FCSTD DOCUMENT  (FreeCAD 0.16R6712 (Git))
Label: Core(XY)
License: CreativeCommons Attribution-ShareAlike
LicenseURL: http://creativecommons.org/licenses/by-sa/4.0/
objects: Part::FeaturePython×717, Part::Feature×181, App::DocumentObjectGroup×163, Part::Compound×24, Sketcher::SketchObject×10, Part::MultiFuse×5, Part::Sweep×5, Part::Cylinder×1, PartDesign::Pocket×1
note: 945 computed .brp shape members not serialized (recipe doc carries the construction recipe); baked Part::Feature solids carry a one-line shape summary decoded from their .brp

FEATURE [Part::FeaturePython] Wuerfelverbinder_20x20_import01010  label="Wuerfelverbinder_20x20_VUL"  # a2plus imported part (geometry in sourceFile) (typed FeaturePython)
  Placement = pos=(10,10,10) rot=(1,0,0;1.5708rad)
  fixedPosition = true
  sourceFile = <userpath>/CloudStation/Hobbyprojekte/3D Drucker/CoreXY/Assembly/Parts/Alu Extrusion/Wuerfelverbinder-20x20.FCStd
  timeLastImport = 1444069248
  updateColors = true
FEATURE [Part::FeaturePython] tslot20x20_import13  label="tslot20x20_import_VU"  # a2plus imported part (geometry in sourceFile) (typed FeaturePython)
  Placement = pos=(420,20,0) rot=(0,-1,0;1.5708rad)
  fixedPosition = true
  sourceFile = <userpath>/CloudStation/Hobbyprojekte/3D Drucker/CoreXY/Assembly/Parts/Alu Extrusion/tslot20x20x400.FCStd
  timeLastImport = 1444069248
  updateColors = true
FEATURE [Part::FeaturePython] tslot20x20x500_import04  label="tslot20x20x500_VL"  # a2plus imported part (geometry in sourceFile) (typed FeaturePython)
  Placement = pos=(4e-11,2.55588e-06,520) rot=(1,0,0;3.14159rad)
  fixedPosition = true
  sourceFile = <userpath>/CloudStation/Hobbyprojekte/3D Drucker/CoreXY/Assembly/Parts/Alu Extrusion/tslot20x20x500.FCStd
  timeLastImport = 1444069248
  updateColors = true
FEATURE [Part::FeaturePython] tslot20x20_import16  label="tslot20x20_UL"  # a2plus imported part (geometry in sourceFile) (typed FeaturePython)
  Placement = pos=(4e-11,420,20) rot=(1,0,0;1.5708rad)
  fixedPosition = true
  sourceFile = <userpath>/CloudStation/Hobbyprojekte/3D Drucker/CoreXY/Assembly/Parts/Alu Extrusion/tslot20x20x400.FCStd
  timeLastImport = 1444069248
  updateColors = true
FEATURE [Part::FeaturePython] Wuerfelverbinder_20x20_import01011  label="Wuerfelverbinder_20x20_HUL"  # a2plus imported part (geometry in sourceFile) (typed FeaturePython)
  Placement = pos=(10,430,10) rot=(1,0,0;3.14159rad)
  fixedPosition = true
  sourceFile = <userpath>/CloudStation/Hobbyprojekte/3D Drucker/CoreXY/Assembly/Parts/Alu Extrusion/Wuerfelverbinder-20x20.FCStd
  timeLastImport = 1444069248
  updateColors = true
FEATURE [Part::FeaturePython] tslot20x20x500_import01  # a2plus imported part (geometry in sourceFile) (typed FeaturePython)
  Placement = pos=(-1.6e-10,420,520) rot=(1,0,0;3.14159rad)
  fixedPosition = true
  sourceFile = <userpath>/CloudStation/Hobbyprojekte/3D Drucker/CoreXY/Assembly/Parts/Alu Extrusion/tslot20x20x500.FCStd
  timeLastImport = 1444069248
  updateColors = true
FEATURE [Part::FeaturePython] tslot20x20_import017  # a2plus imported part (geometry in sourceFile) (typed FeaturePython)
  Placement = pos=(420,440,0) rot=(0,-1,0;1.5708rad)
  fixedPosition = true
  sourceFile = <userpath>/CloudStation/Hobbyprojekte/3D Drucker/CoreXY/Assembly/Parts/Alu Extrusion/tslot20x20x400.FCStd
  timeLastImport = 1444069248
  updateColors = true
FEATURE [Part::FeaturePython] tslot20x20x500_import02  # a2plus imported part (geometry in sourceFile) (typed FeaturePython)
  Placement = pos=(420,420,520) rot=(1,0,0;3.14159rad)
  fixedPosition = true
  sourceFile = <userpath>/CloudStation/Hobbyprojekte/3D Drucker/CoreXY/Assembly/Parts/Alu Extrusion/tslot20x20x500.FCStd
  timeLastImport = 1444069248
  updateColors = true
FEATURE [Part::FeaturePython] tslot20x20_import14  label="tslot20x20 (RU)"  # a2plus imported part (geometry in sourceFile) (typed FeaturePython)
  Placement = pos=(420,420,20) rot=(1,0,0;1.5708rad)
  fixedPosition = true
  sourceFile = <userpath>/CloudStation/Hobbyprojekte/3D Drucker/CoreXY/Assembly/Parts/Alu Extrusion/tslot20x20x400.FCStd
  timeLastImport = 1444069248
  updateColors = true
FEATURE [Part::FeaturePython] tslot20x20x500_import03  # a2plus imported part (geometry in sourceFile) (typed FeaturePython)
  Placement = pos=(420,2.55538e-06,520) rot=(1,0,0;3.14159rad)
  fixedPosition = true
  sourceFile = <userpath>/CloudStation/Hobbyprojekte/3D Drucker/CoreXY/Assembly/Parts/Alu Extrusion/tslot20x20x500.FCStd
  timeLastImport = 1444069248
  updateColors = true
FEATURE [Part::FeaturePython] tslot20x20_import05  label="tslot20x20 (LO)"  # a2plus imported part (geometry in sourceFile) (typed FeaturePython)
  Placement = pos=(-1.6e-10,420,540) rot=(1,0,0;1.5708rad)
  fixedPosition = true
  sourceFile = <userpath>/CloudStation/Hobbyprojekte/3D Drucker/CoreXY/Assembly/Parts/Alu Extrusion/tslot20x20x400.FCStd
  timeLastImport = 1444069248
  updateColors = true
FEATURE [Part::FeaturePython] tslot20x20_import10  label="tslot20x20 (HO)"  # a2plus imported part (geometry in sourceFile) (typed FeaturePython)
  Placement = pos=(20,440,540) rot=(0,1,0;1.5708rad)
  fixedPosition = true
  sourceFile = <userpath>/CloudStation/Hobbyprojekte/3D Drucker/CoreXY/Assembly/Parts/Alu Extrusion/tslot20x20x400.FCStd
  timeLastImport = 1444069248
  updateColors = true
FEATURE [Part::FeaturePython] tslot20x20_import01  label="tslot20x20 (VO)"  # a2plus imported part (geometry in sourceFile) (typed FeaturePython)
  Placement = pos=(420,20,520) rot=(0,-1,0;1.5708rad)
  fixedPosition = true
  sourceFile = <userpath>/CloudStation/Hobbyprojekte/3D Drucker/CoreXY/Assembly/Parts/Alu Extrusion/tslot20x20x400.FCStd
  timeLastImport = 1444069248
  updateColors = true
FEATURE [Part::FeaturePython] tslot20x20_import06  label="tslot20x20 (RO)"  # a2plus imported part (geometry in sourceFile) (typed FeaturePython)
  Placement = pos=(420,420,540) rot=(1,0,0;1.5708rad)
  fixedPosition = true
  sourceFile = <userpath>/CloudStation/Hobbyprojekte/3D Drucker/CoreXY/Assembly/Parts/Alu Extrusion/tslot20x20x400.FCStd
  timeLastImport = 1444069248
  updateColors = true
FEATURE [Part::FeaturePython] Wuerfelverbinder_20x20_import01009  # a2plus imported part (geometry in sourceFile) (typed FeaturePython)
  Placement = pos=(430,10,10) rot=(0.57735,0.57735,0.57735;2.0944rad)
  fixedPosition = true
  sourceFile = <userpath>/CloudStation/Hobbyprojekte/3D Drucker/CoreXY/Assembly/Parts/Alu Extrusion/Wuerfelverbinder-20x20.FCStd
  timeLastImport = 1444069248
  updateColors = true
FEATURE [Part::FeaturePython] Wuerfelverbinder_20x20_import01008  # a2plus imported part (geometry in sourceFile) (typed FeaturePython)
  Placement = pos=(430,430,10) rot=(0.707107,-0.707107,0;3.14159rad)
  fixedPosition = true
  sourceFile = <userpath>/CloudStation/Hobbyprojekte/3D Drucker/CoreXY/Assembly/Parts/Alu Extrusion/Wuerfelverbinder-20x20.FCStd
  timeLastImport = 1444069248
  updateColors = true
FEATURE [Part::FeaturePython] Wuerfelverbinder_20x20_import01  label="Wuerfelverbinder_20x20 (VLO)"  # a2plus imported part (geometry in sourceFile) (typed FeaturePython)
  Placement = pos=(10,10,530) rot=(0,0,1;0rad)
  fixedPosition = true
  sourceFile = <userpath>/CloudStation/Hobbyprojekte/3D Drucker/CoreXY/Assembly/Parts/Alu Extrusion/Wuerfelverbinder-20x20.FCStd
  timeLastImport = 1444069248
  updateColors = true
FEATURE [Part::FeaturePython] Wuerfelverbinder_20x20_import01004  label="Wuerfelverbinder_20x20 (HIL)"  # a2plus imported part (geometry in sourceFile) (typed FeaturePython)
  Placement = pos=(10,430,530) rot=(0,0,-1;1.5708rad)
  fixedPosition = true
  sourceFile = <userpath>/CloudStation/Hobbyprojekte/3D Drucker/CoreXY/Assembly/Parts/Alu Extrusion/Wuerfelverbinder-20x20.FCStd
  timeLastImport = 1444069248
  updateColors = true
FEATURE [Part::FeaturePython] Wuerfelverbinder_20x20_import01005  label="Wuerfelverbinder_20x20 (HOR)"  # a2plus imported part (geometry in sourceFile) (typed FeaturePython)
  Placement = pos=(430,430,530) rot=(0,0,1;3.14159rad)
  fixedPosition = true
  sourceFile = <userpath>/CloudStation/Hobbyprojekte/3D Drucker/CoreXY/Assembly/Parts/Alu Extrusion/Wuerfelverbinder-20x20.FCStd
  timeLastImport = 1444069248
  updateColors = true
FEATURE [Part::FeaturePython] Wuerfelverbinder_20x20_import01001  label="Wuerfelverbinder_20x20 (VRO)"  # a2plus imported part (geometry in sourceFile) (typed FeaturePython)
  Placement = pos=(430,10,530) rot=(0,0,1;1.5708rad)
  fixedPosition = true
  sourceFile = <userpath>/CloudStation/Hobbyprojekte/3D Drucker/CoreXY/Assembly/Parts/Alu Extrusion/Wuerfelverbinder-20x20.FCStd
  timeLastImport = 1444069248
  updateColors = true
FEATURE [App::DocumentObjectGroup] Gruppe002  label="Würfelverbinder"
  Group = -> [Wuerfelverbinder_20x20_import01010,Wuerfelverbinder_20x20_import01011,Wuerfelverbinder_20x20_import01009,Wuerfelverbinder_20x20_import01008,Wuerfelverbinder_20x20_import01,Wuerfelverbinder_20x20_import01004,Wuerfelverbinder_20x20_import01005,Wuerfelverbinder_20x20_import01001]
FEATURE [Part::FeaturePython] tslot20x20_import018  # a2plus imported part (geometry in sourceFile) (typed FeaturePython)
  Placement = pos=(420,440,100) rot=(0,-1,0;1.5708rad)
  fixedPosition = true
  sourceFile = <userpath>/CloudStation/Hobbyprojekte/3D Drucker/CoreXY/Assembly/Parts/Alu Extrusion/tslot20x20x400.FCStd
  timeLastImport = 1444069248
  updateColors = true
FEATURE [Part::FeaturePython] tslot20x20_import019  label="tslot20x20_UL001"  # a2plus imported part (geometry in sourceFile) (typed FeaturePython)
  Placement = pos=(4e-11,420,120) rot=(1,0,0;1.5708rad)
  fixedPosition = true
  sourceFile = <userpath>/CloudStation/Hobbyprojekte/3D Drucker/CoreXY/Assembly/Parts/Alu Extrusion/tslot20x20x400.FCStd
  timeLastImport = 1444069248
  updateColors = true
FEATURE [Part::FeaturePython] tslot20x20_import020  label="tslot20x20_import_VU001"  # a2plus imported part (geometry in sourceFile) (typed FeaturePython)
  Placement = pos=(420,20,100) rot=(0,-1,0;1.5708rad)
  fixedPosition = true
  sourceFile = <userpath>/CloudStation/Hobbyprojekte/3D Drucker/CoreXY/Assembly/Parts/Alu Extrusion/tslot20x20x400.FCStd
  timeLastImport = 1444069248
  updateColors = true
FEATURE [Part::FeaturePython] tslot20x20_import021  label="tslot20x20 (RU)001"  # a2plus imported part (geometry in sourceFile) (typed FeaturePython)
  Placement = pos=(420,420,120) rot=(1,0,0;1.5708rad)
  fixedPosition = true
  sourceFile = <userpath>/CloudStation/Hobbyprojekte/3D Drucker/CoreXY/Assembly/Parts/Alu Extrusion/tslot20x20x400.FCStd
  timeLastImport = 1444069248
  updateColors = true
FEATURE [App::DocumentObjectGroup] Gruppe003  label="Zwischenboden"
  Group = -> [tslot20x20_import018,tslot20x20_import019,tslot20x20_import020,tslot20x20_import021]
FEATURE [Part::FeaturePython] Angle_Bracket_import02  label="Angle_Bracket_VLU_01"  # a2plus imported part (geometry in sourceFile) (typed FeaturePython)
  Placement = pos=(71.9933,2.55588e-06,100) rot=(-1,0,0;1.5708rad)
  fixedPosition = true
  sourceFile = <userpath>/CloudStation/Hobbyprojekte/3D Drucker/CoreXY/Assembly/Parts/Printed Parts/Angle_Bracket.FCStd
  timeLastImport = 1444069248
  updateColors = true
FEATURE [Part::FeaturePython] Angle_Bracket_import14  label="Angle_Bracket_VHU_01"  # a2plus imported part (geometry in sourceFile) (typed FeaturePython)
  Placement = pos=(-1.6e-10,368.007,100) rot=(0.57735,-0.57735,0.57735;4.18879rad)
  fixedPosition = true
  sourceFile = <userpath>/CloudStation/Hobbyprojekte/3D Drucker/CoreXY/Assembly/Parts/Printed Parts/Angle_Bracket.FCStd
  timeLastImport = 1444069248
  updateColors = true
FEATURE [Part::FeaturePython] Angle_Bracket_import04  label="Angle_Bracket_VRU_01"  # a2plus imported part (geometry in sourceFile) (typed FeaturePython)
  Placement = pos=(368.007,20,100) rot=(0,0.707107,-0.707107;3.14159rad)
  fixedPosition = true
  sourceFile = <userpath>/CloudStation/Hobbyprojekte/3D Drucker/CoreXY/Assembly/Parts/Printed Parts/Angle_Bracket.FCStd
  timeLastImport = 1444069248
  updateColors = true
FEATURE [Part::FeaturePython] Angle_Bracket_import10  label="Angle_Bracket_VHU_02"  # a2plus imported part (geometry in sourceFile) (typed FeaturePython)
  Placement = pos=(71.9933,420,100) rot=(-1,0,0;1.5708rad)
  fixedPosition = true
  sourceFile = <userpath>/CloudStation/Hobbyprojekte/3D Drucker/CoreXY/Assembly/Parts/Printed Parts/Angle_Bracket.FCStd
  timeLastImport = 1444069248
  updateColors = true
FEATURE [Part::FeaturePython] Angle_Bracket_import12  label="Angle_Bracket_HRU_01"  # a2plus imported part (geometry in sourceFile) (typed FeaturePython)
  Placement = pos=(420,420,48.0067) rot=(-0.57735,0.57735,0.57735;2.0944rad)
  fixedPosition = true
  sourceFile = <userpath>/CloudStation/Hobbyprojekte/3D Drucker/CoreXY/Assembly/Parts/Printed Parts/Angle_Bracket.FCStd
  timeLastImport = 1444069248
  updateColors = true
FEATURE [Part::FeaturePython] Angle_Bracket_import06  label="Angle_Bracket_VRU_02"  # a2plus imported part (geometry in sourceFile) (typed FeaturePython)
  Placement = pos=(440,71.9933,100) rot=(0.57735,0.57735,-0.57735;4.18879rad)
  fixedPosition = true
  sourceFile = <userpath>/CloudStation/Hobbyprojekte/3D Drucker/CoreXY/Assembly/Parts/Printed Parts/Angle_Bracket.FCStd
  timeLastImport = 1444069248
  updateColors = true
FEATURE [Part::FeaturePython] Angle_Bracket_import08  label="Angle_Bracket_HRU_02"  # a2plus imported part (geometry in sourceFile) (typed FeaturePython)
  Placement = pos=(420,368.007,100) rot=(0.57735,-0.57735,0.57735;4.18879rad)
  fixedPosition = true
  sourceFile = <userpath>/CloudStation/Hobbyprojekte/3D Drucker/CoreXY/Assembly/Parts/Printed Parts/Angle_Bracket.FCStd
  timeLastImport = 1444069248
  updateColors = true
FEATURE [Part::FeaturePython] Angle_Bracket_import16  label="Angle_Bracket_VLU_02"  # a2plus imported part (geometry in sourceFile) (typed FeaturePython)
  Placement = pos=(20,71.9933,100) rot=(0.57735,0.57735,-0.57735;4.18879rad)
  fixedPosition = true
  sourceFile = <userpath>/CloudStation/Hobbyprojekte/3D Drucker/CoreXY/Assembly/Parts/Printed Parts/Angle_Bracket.FCStd
  timeLastImport = 1444069248
  updateColors = true
FEATURE [Part::FeaturePython] Angle_Bracket_import11  label="Angle_Bracket_HRO_01"  # a2plus imported part (geometry in sourceFile) (typed FeaturePython)
  Placement = pos=(368.007,420,120) rot=(0,0.707107,0.707107;3.14159rad)
  fixedPosition = true
  sourceFile = <userpath>/CloudStation/Hobbyprojekte/3D Drucker/CoreXY/Assembly/Parts/Printed Parts/Angle_Bracket.FCStd
  timeLastImport = 1444069248
  updateColors = true
FEATURE [Part::FeaturePython] Angle_Bracket_import01  label="Angle_Bracket_VLO_01"  # a2plus imported part (geometry in sourceFile) (typed FeaturePython)
  Placement = pos=(71.9933,20,120) rot=(1,0,0;1.5708rad)
  fixedPosition = true
  sourceFile = <userpath>/CloudStation/Hobbyprojekte/3D Drucker/CoreXY/Assembly/Parts/Printed Parts/Angle_Bracket.FCStd
  timeLastImport = 1444069248
  updateColors = true
FEATURE [Part::FeaturePython] Angle_Bracket_import13  label="Angle_Bracket_HLO_01"  # a2plus imported part (geometry in sourceFile) (typed FeaturePython)
  Placement = pos=(20,368.007,120) rot=(0.57735,-0.57735,-0.57735;2.0944rad)
  fixedPosition = true
  sourceFile = <userpath>/CloudStation/Hobbyprojekte/3D Drucker/CoreXY/Assembly/Parts/Printed Parts/Angle_Bracket.FCStd
  timeLastImport = 1444069248
  updateColors = true
FEATURE [Part::FeaturePython] Angle_Bracket_import15  label="Angle_Bracket_VLO_02"  # a2plus imported part (geometry in sourceFile) (typed FeaturePython)
  Placement = pos=(4.1e-11,71.9933,120) rot=(0.57735,0.57735,0.57735;2.0944rad)
  fixedPosition = true
  sourceFile = <userpath>/CloudStation/Hobbyprojekte/3D Drucker/CoreXY/Assembly/Parts/Printed Parts/Angle_Bracket.FCStd
  timeLastImport = 1444069248
  updateColors = true
FEATURE [Part::FeaturePython] Angle_Bracket_import03  label="Angle_Bracket_VRO_01"  # a2plus imported part (geometry in sourceFile) (typed FeaturePython)
  Placement = pos=(368.007,2.55538e-06,120) rot=(0,0.707107,0.707107;3.14159rad)
  fixedPosition = true
  sourceFile = <userpath>/CloudStation/Hobbyprojekte/3D Drucker/CoreXY/Assembly/Parts/Printed Parts/Angle_Bracket.FCStd
  timeLastImport = 1444069248
  updateColors = true
FEATURE [Part::FeaturePython] Angle_Bracket_import09  label="Angle_Bracket_HLO_02"  # a2plus imported part (geometry in sourceFile) (typed FeaturePython)
  Placement = pos=(71.9933,440,120) rot=(1,0,0;1.5708rad)
  fixedPosition = true
  sourceFile = <userpath>/CloudStation/Hobbyprojekte/3D Drucker/CoreXY/Assembly/Parts/Printed Parts/Angle_Bracket.FCStd
  timeLastImport = 1444069248
  updateColors = true
FEATURE [Part::FeaturePython] Angle_Bracket_import05  label="Angle_Bracket_VRO_02"  # a2plus imported part (geometry in sourceFile) (typed FeaturePython)
  Placement = pos=(420,71.9933,120) rot=(0.57735,0.57735,0.57735;2.0944rad)
  fixedPosition = true
  sourceFile = <userpath>/CloudStation/Hobbyprojekte/3D Drucker/CoreXY/Assembly/Parts/Printed Parts/Angle_Bracket.FCStd
  timeLastImport = 1444069248
  updateColors = true
FEATURE [Part::FeaturePython] Angle_Bracket_import07  label="Angle_Bracket_HRO_02"  # a2plus imported part (geometry in sourceFile) (typed FeaturePython)
  Placement = pos=(440,368.007,120) rot=(0.57735,-0.57735,-0.57735;2.0944rad)
  fixedPosition = true
  sourceFile = <userpath>/CloudStation/Hobbyprojekte/3D Drucker/CoreXY/Assembly/Parts/Printed Parts/Angle_Bracket.FCStd
  timeLastImport = 1444069248
  updateColors = true
FEATURE [App::DocumentObjectGroup] Gruppe007  label="Zusätzliche Eckverbinder"
  Group = -> [Angle_Bracket_import01,Angle_Bracket_import15,Angle_Bracket_import03,Angle_Bracket_import05,Angle_Bracket_import13,Angle_Bracket_import07,Angle_Bracket_import11,Angle_Bracket_import09]
FEATURE [Part::FeaturePython] NEMA_17_Stepper_Motor_40mm_with_connector_import01  # a2plus imported part (geometry in sourceFile) (typed FeaturePython)
  Placement = pos=(356,399,524.6) rot=(1,0,0;3.14159rad)
  fixedPosition = true
  sourceFile = <userpath>/CloudStation/Hobbyprojekte/3D Drucker/CoreXY/Assembly/Parts/3D Printer Components/NEMA-17_Stepper_Motor_40mm_with_connector.fcstd
  timeLastImport = 1444068474
  updateColors = true
FEATURE [Part::FeaturePython] DIN625_1_624_ZZ_import01003  # a2plus imported part (geometry in sourceFile) (typed FeaturePython)
  Placement = pos=(383.5,417.7,478) rot=(0,1,0;3.14159rad)
  fixedPosition = false
  sourceFile = <userpath>/CloudStation/Hobbyprojekte/3D Drucker/CoreXY/Assembly/Parts/Bearings/DIN625-1_624-ZZ.FCStd
  timeLastImport = 1430517302
  updateColors = true
FEATURE [Part::FeaturePython] DIN625_1_624_ZZ_import01004  # a2plus imported part (geometry in sourceFile) (typed FeaturePython)
  Placement = pos=(383.5,417.7,473) rot=(0,1,0;3.14159rad)
  fixedPosition = false
  sourceFile = <userpath>/CloudStation/Hobbyprojekte/3D Drucker/CoreXY/Assembly/Parts/Bearings/DIN625-1_624-ZZ.FCStd
  timeLastImport = 1430517302
  updateColors = true
FEATURE [Part::FeaturePython] DIN7965___Schraubeinsatz___M3_import01  # a2plus imported part (geometry in sourceFile) (typed FeaturePython)
  Placement = pos=(385,383,478.2) rot=(0,1,0;3.14159rad)
  fixedPosition = false
  sourceFile = <userpath>/CloudStation/Hobbyprojekte/3D Drucker/CoreXY/Assembly/Parts/Screws/DIN7965 - Schraubeinsatz - M3.FCStd
  timeLastImport = 1430763186
  updateColors = true
FEATURE [Part::FeaturePython] Hammermutter_B_Typ_Nut6_M4_import01003  # a2plus imported part (geometry in sourceFile) (typed FeaturePython)
  Placement = pos=(430,408,445.3) rot=(0,0,1;3.14159rad)
  fixedPosition = false
  sourceFile = <userpath>/CloudStation/Hobbyprojekte/3D Drucker/CoreXY/Assembly/Parts/Screws/Hammermutter B-Typ Nut6 M4.FCStd
  timeLastImport = 1430523528
  updateColors = true
FEATURE [Part::FeaturePython] Hammermutter_B_Typ_Nut6_M4_import01002  # a2plus imported part (geometry in sourceFile) (typed FeaturePython)
  Placement = pos=(430,393,445.3) rot=(0,0,1;3.14159rad)
  fixedPosition = false
  sourceFile = <userpath>/CloudStation/Hobbyprojekte/3D Drucker/CoreXY/Assembly/Parts/Screws/Hammermutter B-Typ Nut6 M4.FCStd
  timeLastImport = 1430523528
  updateColors = true
FEATURE [Part::FeaturePython] Hammermutter_B_Typ_Nut6_M4_import01  # a2plus imported part (geometry in sourceFile) (typed FeaturePython)
  Placement = pos=(398,430,445.3) rot=(0,0,-1;1.5708rad)
  fixedPosition = false
  sourceFile = <userpath>/CloudStation/Hobbyprojekte/3D Drucker/CoreXY/Assembly/Parts/Screws/Hammermutter B-Typ Nut6 M4.FCStd
  timeLastImport = 1430523528
  updateColors = true
FEATURE [Part::FeaturePython] Hammermutter_B_Typ_Nut6_M4_import01001  # a2plus imported part (geometry in sourceFile) (typed FeaturePython)
  Placement = pos=(346,430,445.3) rot=(0,0,-1;1.5708rad)
  fixedPosition = false
  sourceFile = <userpath>/CloudStation/Hobbyprojekte/3D Drucker/CoreXY/Assembly/Parts/Screws/Hammermutter B-Typ Nut6 M4.FCStd
  timeLastImport = 1430523528
  updateColors = true
FEATURE [Part::FeaturePython] spacer16mm_import01  # a2plus imported part (geometry in sourceFile) (typed FeaturePython)
  Placement = pos=(407,413,452.5) rot=(0,0,1;3.14159rad)
  fixedPosition = false
  sourceFile = <userpath>/CloudStation/Hobbyprojekte/3D Drucker/CoreXY/Assembly/Parts/Printed Parts/spacer16mm.FCStd
  timeLastImport = 1444069248
  updateColors = true
FEATURE [Part::FeaturePython] spacer16mm_import03  # a2plus imported part (geometry in sourceFile) (typed FeaturePython)
  Placement = pos=(402,388,452.5) rot=(0,0,1;3.14159rad)
  fixedPosition = false
  sourceFile = <userpath>/CloudStation/Hobbyprojekte/3D Drucker/CoreXY/Assembly/Parts/Printed Parts/spacer16mm.FCStd
  timeLastImport = 1444069248
  updateColors = true
FEATURE [Part::FeaturePython] NEMA_17_Stepper_Motor_40mm_with_connector_import002  # a2plus imported part (geometry in sourceFile) (typed FeaturePython)
  Placement = pos=(84,399,524.6) rot=(0,1,0;3.14159rad)
  fixedPosition = true
  sourceFile = <userpath>/CloudStation/Hobbyprojekte/3D Drucker/CoreXY/Assembly/Parts/3D Printer Components/NEMA-17_Stepper_Motor_40mm_with_connector.fcstd
  timeLastImport = 1444068474
  updateColors = true
FEATURE [Part::FeaturePython] Hammermutter_B_Typ_Nut6_M4_import01004  # a2plus imported part (geometry in sourceFile) (typed FeaturePython)
  Placement = pos=(10,408,445.3) rot=(0,0,1;3.14159rad)
  fixedPosition = false
  sourceFile = <userpath>/CloudStation/Hobbyprojekte/3D Drucker/CoreXY/Assembly/Parts/Screws/Hammermutter B-Typ Nut6 M4.FCStd
  timeLastImport = 1430523528
  updateColors = true
FEATURE [Part::FeaturePython] Hammermutter_B_Typ_Nut6_M4_import01005  # a2plus imported part (geometry in sourceFile) (typed FeaturePython)
  Placement = pos=(42,430,445.3) rot=(0,0,-1;1.5708rad)
  fixedPosition = false
  sourceFile = <userpath>/CloudStation/Hobbyprojekte/3D Drucker/CoreXY/Assembly/Parts/Screws/Hammermutter B-Typ Nut6 M4.FCStd
  timeLastImport = 1430523528
  updateColors = true
FEATURE [Part::FeaturePython] Hammermutter_B_Typ_Nut6_M4_import01006  # a2plus imported part (geometry in sourceFile) (typed FeaturePython)
  Placement = pos=(10,393,445.3) rot=(0,0,1;3.14159rad)
  fixedPosition = false
  sourceFile = <userpath>/CloudStation/Hobbyprojekte/3D Drucker/CoreXY/Assembly/Parts/Screws/Hammermutter B-Typ Nut6 M4.FCStd
  timeLastImport = 1430523528
  updateColors = true
FEATURE [Part::FeaturePython] Hammermutter_B_Typ_Nut6_M4_import01007  # a2plus imported part (geometry in sourceFile) (typed FeaturePython)
  Placement = pos=(94,430,445.3) rot=(0,0,-1;1.5708rad)
  fixedPosition = false
  sourceFile = <userpath>/CloudStation/Hobbyprojekte/3D Drucker/CoreXY/Assembly/Parts/Screws/Hammermutter B-Typ Nut6 M4.FCStd
  timeLastImport = 1430523528
  updateColors = true
FEATURE [Part::FeaturePython] Hammermutter_B_Typ_Nut6_M4_import01009  # a2plus imported part (geometry in sourceFile) (typed FeaturePython)
  Placement = pos=(430,15,478.5) rot=(0,0.707107,0.707107;3.14159rad)
  fixedPosition = false
  sourceFile = <userpath>/CloudStation/Hobbyprojekte/3D Drucker/CoreXY/Assembly/Parts/Screws/Hammermutter B-Typ Nut6 M4.FCStd
  timeLastImport = 1430523528
  updateColors = true
FEATURE [Part::FeaturePython] Hammermutter_B_Typ_Nut6_M4_import01011  # a2plus imported part (geometry in sourceFile) (typed FeaturePython)
  Placement = pos=(430,15,455.5) rot=(0,0.707107,0.707107;3.14159rad)
  fixedPosition = false
  sourceFile = <userpath>/CloudStation/Hobbyprojekte/3D Drucker/CoreXY/Assembly/Parts/Screws/Hammermutter B-Typ Nut6 M4.FCStd
  timeLastImport = 1430523528
  updateColors = true
FEATURE [Part::FeaturePython] Hammermutter_B_Typ_Nut6_M4_import01012  # a2plus imported part (geometry in sourceFile) (typed FeaturePython)
  Placement = pos=(48,10,445.3) rot=(0,0,-1;1.5708rad)
  fixedPosition = false
  sourceFile = <userpath>/CloudStation/Hobbyprojekte/3D Drucker/CoreXY/Assembly/Parts/Screws/Hammermutter B-Typ Nut6 M4.FCStd
  timeLastImport = 1430523528
  updateColors = true
FEATURE [Part::FeaturePython] DIN7965___Schraubeinsatz___M3_import004  # a2plus imported part (geometry in sourceFile) (typed FeaturePython)
  Placement = pos=(55,35,469.5) rot=(0,1,0;3.14159rad)
  fixedPosition = false
  sourceFile = <userpath>/CloudStation/Hobbyprojekte/3D Drucker/CoreXY/Assembly/Parts/Screws/DIN7965 - Schraubeinsatz - M3.FCStd
  timeLastImport = 1430763186
  updateColors = true
FEATURE [Part::FeaturePython] Hammermutter_B_Typ_Nut6_M4_import01013  # a2plus imported part (geometry in sourceFile) (typed FeaturePython)
  Placement = pos=(10,15,478.5) rot=(0,0.707107,0.707107;3.14159rad)
  fixedPosition = false
  sourceFile = <userpath>/CloudStation/Hobbyprojekte/3D Drucker/CoreXY/Assembly/Parts/Screws/Hammermutter B-Typ Nut6 M4.FCStd
  timeLastImport = 1430523528
  updateColors = true
FEATURE [Part::FeaturePython] Hammermutter_B_Typ_Nut6_M4_import01014  # a2plus imported part (geometry in sourceFile) (typed FeaturePython)
  Placement = pos=(33,10,445.3) rot=(0,0,-1;1.5708rad)
  fixedPosition = false
  sourceFile = <userpath>/CloudStation/Hobbyprojekte/3D Drucker/CoreXY/Assembly/Parts/Screws/Hammermutter B-Typ Nut6 M4.FCStd
  timeLastImport = 1430523528
  updateColors = true
FEATURE [Part::FeaturePython] Hammermutter_B_Typ_Nut6_M4_import01015  # a2plus imported part (geometry in sourceFile) (typed FeaturePython)
  Placement = pos=(10,15,455.5) rot=(0,0.707107,0.707107;3.14159rad)
  fixedPosition = false
  sourceFile = <userpath>/CloudStation/Hobbyprojekte/3D Drucker/CoreXY/Assembly/Parts/Screws/Hammermutter B-Typ Nut6 M4.FCStd
  timeLastImport = 1430523528
  updateColors = true
FEATURE [Part::FeaturePython] spacer9mm_import006  # a2plus imported part (geometry in sourceFile) (typed FeaturePython)
  Placement = pos=(33,10,478.8) rot=(0,1,0;3.14159rad)
  fixedPosition = false
  sourceFile = <userpath>/CloudStation/Hobbyprojekte/3D Drucker/CoreXY/Assembly/Parts/Printed Parts/spacer9mm.FCStd
  timeLastImport = 1444069248
  updateColors = true
FEATURE [Part::FeaturePython] spacer9mm_import007  # a2plus imported part (geometry in sourceFile) (typed FeaturePython)
  Placement = pos=(38,28,468.9) rot=(0,1,0;3.14159rad)
  fixedPosition = false
  sourceFile = <userpath>/CloudStation/Hobbyprojekte/3D Drucker/CoreXY/Assembly/Parts/Printed Parts/spacer9mm.FCStd
  timeLastImport = 1444069248
  updateColors = true
FEATURE [App::DocumentObjectGroup] Gruppe027  label="Distancers003"
  Group = -> [spacer9mm_import007,spacer9mm_import006]
FEATURE [App::DocumentObjectGroup] Gruppe033  label="Distancers004"
FEATURE [App::DocumentObjectGroup] Gruppe038  label="Distancers005"
FEATURE [Part::FeaturePython] LM8uu_005  # a2plus imported part (geometry in sourceFile) (typed FeaturePython)
  Placement = pos=(206.657,188.8,470.2) rot=(0,0,1;1.5708rad)
  fixedPosition = false
  sourceFile = <userpath>/CloudStation/Hobbyprojekte/3D Drucker/CoreXY/Assembly/Parts/Bearings/LM8uu.fcstd
  timeLastImport = 1430143348
  updateColors = true
FEATURE [Part::FeaturePython] LM8uu_006  # a2plus imported part (geometry in sourceFile) (typed FeaturePython)
  Placement = pos=(206.657,228.8,470.2) rot=(0,0,1;1.5708rad)
  fixedPosition = false
  sourceFile = <userpath>/CloudStation/Hobbyprojekte/3D Drucker/CoreXY/Assembly/Parts/Bearings/LM8uu.fcstd
  timeLastImport = 1430143348
  updateColors = true
FEATURE [Part::FeaturePython] LM8uu_007  # a2plus imported part (geometry in sourceFile) (typed FeaturePython)
  Placement = pos=(233.657,228.8,470.2) rot=(0,0,1;1.5708rad)
  fixedPosition = false
  sourceFile = <userpath>/CloudStation/Hobbyprojekte/3D Drucker/CoreXY/Assembly/Parts/Bearings/LM8uu.fcstd
  timeLastImport = 1430143348
  updateColors = true
FEATURE [Part::FeaturePython] LM8uu_008  # a2plus imported part (geometry in sourceFile) (typed FeaturePython)
  Placement = pos=(233.657,188.8,470.2) rot=(0,0,1;1.5708rad)
  fixedPosition = true
  sourceFile = <userpath>/CloudStation/Hobbyprojekte/3D Drucker/CoreXY/Assembly/Parts/Bearings/LM8uu.fcstd
  timeLastImport = 1430143348
  updateColors = true
FEATURE [App::DocumentObjectGroup] Gruppe041  label="Bearings006"
  Group = -> [LM8uu_005,LM8uu_006,LM8uu_007,LM8uu_008]
FEATURE [App::DocumentObjectGroup] Gruppe042  label="Screws006"
FEATURE [Part::FeaturePython] GT2Pulley_01  # a2plus imported part (geometry in sourceFile) (typed FeaturePython)
  Placement = pos=(356,399,463.95) rot=(0,0,1;3.14159rad)
  fixedPosition = true
  sourceFile = <userpath>/CloudStation/Hobbyprojekte/3D Drucker/CoreXY/Assembly/Parts/Belts/GT2Pulley.fcstd
  timeLastImport = 1444675797
  updateColors = true
FEATURE [Part::FeaturePython] GT2Pulley_002  # a2plus imported part (geometry in sourceFile) (typed FeaturePython)
  Placement = pos=(84,399,474.2) rot=(1,0,0;3.14159rad)
  fixedPosition = true
  sourceFile = <userpath>/CloudStation/Hobbyprojekte/3D Drucker/CoreXY/Assembly/Parts/Belts/GT2Pulley.fcstd
  timeLastImport = 1444675797
  updateColors = true
FEATURE [Part::Feature] Part__Feature124  label="belt-clamp"
  Placement = pos=(202.907,208.742,301.2) rot=(0,0,1;0rad)
  shape: bbox 15 x 22 x 10 mm, 58 faces (baked)
FEATURE [Part::Feature] Part__Feature125  label="belt-clamp001"
  Placement = pos=(202.907,208.742,300.2) rot=(0,0,1;0rad)
  shape: bbox 15 x 22 x 10 mm, 58 faces (baked)
FEATURE [Part::Feature] Part__Feature348  label="C04H030010-Fibonacci-Support"
  Placement = pos=(216.254,203.086,536.966) rot=(0,0.707107,0.707107;3.14159rad)
  shape: bbox 41.5 x 15 x 48 mm, 19 faces (baked)
FEATURE [Part::Feature] Cut  label="carriage-up"
  Placement = pos=(219.907,209.1,476) rot=(0,0,1;3.14159rad)
  shape: bbox 70 x 90 x 3 mm, 67 faces (baked)
FEATURE [Part::Feature] Part__Feature349  label="C04H020001-Extruder-heat-sink"
  Placement = pos=(210.254,193.086,499.001) rot=(0.57735,0.57735,-0.57735;4.18879rad)
  shape: bbox 40.01 x 11.01 x 40.01 mm, 661 faces (baked)
FEATURE [Part::Feature] Part__Feature350  label="C04H030096-extruder-motor-support"
  Placement = pos=(210.254,213.086,478.001) rot=(1,0,0;1.5708rad)
  shape: bbox 45.02 x 20.02 x 47.52 mm, 42 faces (baked)
FEATURE [Part::Feature] Part__Feature354  label="Extruder_tube-end"
  Placement = pos=(216.254,203.086,541.576) rot=(0,0.707107,0.707107;3.14159rad)
  shape: bbox 54.22 x 4 x 43.22 mm, 8 faces (baked)
FEATURE [Part::Feature] Part__Feature353  label="C04H020019-extruder-spring"
  Placement = pos=(195.504,203.086,500.141) rot=(1,0,0;1.5708rad)
  shape: bbox 4 x 4.003 x 16.76 mm, 15 faces (baked)
FEATURE [Part::Feature] Part__Feature352  label="C04H020035-MK7-Drive-Gear-1.75mm"
  Placement = pos=(210.254,210.086,504.501) rot=(0.247035,-0.247035,-0.936988;1.63583rad)
  shape: bbox 12.5 x 11 x 12.5 mm, 7 faces (baked)
FEATURE [Part::Feature] Part__Feature351  label="C04H030009-Extruder-lever"
  Placement = pos=(210.254,200.586,504.501) rot=(1,0,0;1.5708rad)
  shape: bbox 42.51 x 15.01 x 16.01 mm, 23 faces (baked)
FEATURE [Part::Feature] Part__Feature377  label="Extruder-body-bolt-2"
  Placement = pos=(227.754,203.086,476.001) rot=(0.576292,-0.579462,0.576292;2.09123rad)
  shape: bbox 7.583 x 7.583 x 12.01 mm, 15 faces (baked)
FEATURE [Part::Feature] Part__Feature376  label="Extruder-body-bolt-1"
  Placement = pos=(192.754,203.086,476.001) rot=(0.576292,-0.579462,0.576292;2.09123rad)
  shape: bbox 7.583 x 7.583 x 12.01 mm, 15 faces (baked)
FEATURE [Part::Compound] Compound004  label="C04H010007-blower-fan"
  Placement = pos=(319.907,695.1,404) rot=(1,0,0;1.5708rad)
FEATURE [Part::Feature] Part__Feature375  label="C04H030024-air-nozzle"
  Placement = pos=(236.004,202.086,475.251) rot=(0,0.707107,0.707107;3.14159rad)
  shape: bbox 25.01 x 19.01 x 26.01 mm, 43 faces (baked)
FEATURE [Part::Feature] Part__Feature365  label="Extruder_thermistor"
  Placement = pos=(216.254,215.086,465.001) rot=(-1,0,0;1.5708rad)
  shape: bbox 4.68 x 42.11 x 18.36 mm, 26 faces (baked)
FEATURE [Part::Feature] Part__Feature364  label="Extruder_thermistor-connector"
  Placement = pos=(216.254,266.393,479.951) rot=(0,0.707107,0.707107;3.14159rad)
  shape: bbox 6.4 x 13.2 x 2.9 mm, 48 faces (baked)
FEATURE [Part::Feature] Part__Feature363  label="C04H040004-PTFE-tube-hotend"
  Placement = pos=(216.254,203.086,496.001) rot=(-0.707107,0.707107,0;3.14159rad)
  shape: bbox 4 x 4 x 25.2 mm, 4 faces (baked)
FEATURE [Part::Feature] Part__Feature362  label="C04H030020-hotend_short-metal-tube"
  Placement = pos=(216.254,203.086,471.001) rot=(-0.707107,0.707107,0;3.14159rad)
  shape: bbox 4 x 4 x 6 mm, 8 faces (baked)
FEATURE [Part::Feature] Part__Feature361  label="Extruder_heater-cartrigde"
  Placement = pos=(209.254,196.086,465.001) rot=(0,0.707107,0.707107;3.14159rad)
  shape: bbox 7 x 58.5 x 21.14 mm, 24 faces (baked)
FEATURE [Part::Compound] Compound003  label="C04H010011-extruder-motor"
  Placement = pos=(310.754,695.1,614.154) rot=(0.57735,-0.57735,0.57735;2.0944rad)
FEATURE [Part::Feature] Part__Feature358  label="C04H020004-hot-end-nozzle"
  Placement = pos=(216.254,203.086,465.001) rot=(-0.69493,0.719077,0;3.14159rad)
  shape: bbox 8.083 x 8.083 x 13 mm, 15 faces (baked)
FEATURE [Part::Feature] Part__Feature359  label="hot-end-PLA-filament"
  Placement = pos=(216.254,203.086,517.501) rot=(1,0,0;3.14159rad)
  shape: bbox 1.75 x 1.75 x 50 mm, 3 faces (baked)
FEATURE [Part::Feature] Part__Feature360  label="Extruder_heater-connector"
  Placement = pos=(209.254,260.736,484.401) rot=(-1,0,0;1.5708rad)
  shape: bbox 7.86 x 13.3 x 10.6 mm, 58 faces (baked)
FEATURE [Part::Compound] Compound002  label="C04H010006-Cooling-Fan-RD4010B12H"
  Placement = pos=(319.907,695.1,404) rot=(1,0,0;1.5708rad)
FEATURE [Part::Feature] Part__Feature128  label="belt-clamp002"
  Placement = pos=(236.907,208.742,300.2) rot=(0,0,1;0rad)
  shape: bbox 15 x 22 x 10 mm, 58 faces (baked)
FEATURE [Part::Feature] Part__Feature129  label="belt-clamp003"
  Placement = pos=(236.907,208.742,301.2) rot=(0,0,1;0rad)
  shape: bbox 15 x 22 x 10 mm, 58 faces (baked)
FEATURE [Part::Feature] Part__Feature357  label="C04H030007-Hot-end-main-tube"
  Placement = pos=(216.254,203.086,465.001) rot=(0.57735,0.57735,0.57735;2.0944rad)
  shape: bbox 10 x 10 x 36 mm, 30 faces (baked)
FEATURE [Part::Feature] Part__Feature356  label="C04H030011-Hot-end-heater-block"
  Placement = pos=(212.754,205.586,465.001) rot=(0,0,1;0rad)
  shape: bbox 19.01 x 19.01 x 10.01 mm, 31 faces (baked)
FEATURE [Part::Feature] Part__Feature355  label="C04H040001-pneumatic-fitting"
  Placement = pos=(216.254,203.086,552.001) rot=(-0.333674,0.666582,0.666582;3.78571rad)
  shape: bbox 13.2 x 13.2 x 34.5 mm, 43 faces (baked)
FEATURE [Part::Feature] Part__Feature372  label="C04H030033-blower-support"
  Placement = pos=(259.517,225.086,498.063) rot=(1,0,0;1.5708rad)
  shape: bbox 2.01 x 50.71 x 61.51 mm, 27 faces (baked)
FEATURE [Part::Feature] Part__Feature371  label="C04H050004-dowel-pin"
  Placement = pos=(227.504,193.086,512.501) rot=(0.57735,0.57735,-0.57735;4.18879rad)
  shape: bbox 3 x 20 x 3 mm, 5 faces (baked)
FEATURE [Part::Feature] Part__Feature370  label="Extruder_small-top-tube"
  Placement = pos=(216.254,203.086,537.576) rot=(1,0,0;1.5708rad)
  shape: bbox 4 x 4 x 4 mm, 5 faces (baked)
FEATURE [Part::Feature] Part__Feature369  label="Extruder-bolt-2"
  Placement = pos=(226.254,175.326,483.001) rot=(0.57735,0.57735,0.57735;2.0944rad)
  shape: bbox 5.958 x 23.01 x 5.958 mm, 15 faces (baked)
FEATURE [Part::Feature] Part__Feature368  label="Extruder_bolt-1"
  Placement = pos=(194.254,175.326,483.001) rot=(0.57735,0.57735,0.57735;2.0944rad)
  shape: bbox 5.958 x 23.01 x 5.958 mm, 15 faces (baked)
FEATURE [Part::Feature] Part__Feature367  label="Extruder-setscrew"
  Placement = pos=(216.254,196.086,489.001) rot=(0.57735,-0.57735,0.57735;4.18879rad)
  shape: bbox 3 x 3 x 3 mm, 12 faces (baked)
FEATURE [Part::Feature] Part__Feature366  label="C04H020008-Bearing-623zz"
  Placement = pos=(221.754,205.086,504.501) rot=(1,-0.000322,0.000322;1.5708rad)
  shape: bbox 10.82 x 4 x 10.82 mm, 29 faces (baked)
FEATURE [Part::FeaturePython] LM8uu_009  # a2plus imported part (geometry in sourceFile) (typed FeaturePython)
  Placement = pos=(206.657,176.205,470.2) rot=(0,0,1;1.5708rad)
  fixedPosition = false
  sourceFile = <userpath>/CloudStation/Hobbyprojekte/3D Drucker/CoreXY/Assembly/Parts/Bearings/LM8uu.fcstd
  timeLastImport = 1430143348
  updateColors = true
FEATURE [Part::FeaturePython] LM8uu_010  # a2plus imported part (geometry in sourceFile) (typed FeaturePython)
  Placement = pos=(233.657,241.242,470.2) rot=(0,0,1;1.5708rad)
  fixedPosition = false
  sourceFile = <userpath>/CloudStation/Hobbyprojekte/3D Drucker/CoreXY/Assembly/Parts/Bearings/LM8uu.fcstd
  timeLastImport = 1430143348
  updateColors = true
FEATURE [Part::FeaturePython] LM8uu_011  # a2plus imported part (geometry in sourceFile) (typed FeaturePython)
  Placement = pos=(206.657,241.242,470.2) rot=(0,0,1;1.5708rad)
  fixedPosition = false
  sourceFile = <userpath>/CloudStation/Hobbyprojekte/3D Drucker/CoreXY/Assembly/Parts/Bearings/LM8uu.fcstd
  timeLastImport = 1430143348
  updateColors = true
FEATURE [Part::FeaturePython] LM8uu_012  # a2plus imported part (geometry in sourceFile) (typed FeaturePython)
  Placement = pos=(233.657,176.205,470.2) rot=(0,0,1;1.5708rad)
  fixedPosition = false
  sourceFile = <userpath>/CloudStation/Hobbyprojekte/3D Drucker/CoreXY/Assembly/Parts/Bearings/LM8uu.fcstd
  timeLastImport = 1430143348
  updateColors = true
FEATURE [Part::FeaturePython] LM8uu_013  # a2plus imported part (geometry in sourceFile) (typed FeaturePython)
  Placement = pos=(13,188.705,470.2) rot=(0,0,1;0rad)
  fixedPosition = false
  sourceFile = <userpath>/CloudStation/Hobbyprojekte/3D Drucker/CoreXY/Assembly/Parts/Bearings/LM8uu.fcstd
  timeLastImport = 1430143348
  updateColors = true
FEATURE [Part::FeaturePython] LM8uu_014  # a2plus imported part (geometry in sourceFile) (typed FeaturePython)
  Placement = pos=(13,228.705,470.2) rot=(0,0,1;0rad)
  fixedPosition = false
  sourceFile = <userpath>/CloudStation/Hobbyprojekte/3D Drucker/CoreXY/Assembly/Parts/Bearings/LM8uu.fcstd
  timeLastImport = 1430143348
  updateColors = true
FEATURE [Part::FeaturePython] DIN7965___Schraubeinsatz___M3_import013  # a2plus imported part (geometry in sourceFile) (typed FeaturePython)
  Placement = pos=(41,249.705,462.2) rot=(0,0,1;0rad)
  fixedPosition = false
  sourceFile = <userpath>/CloudStation/Hobbyprojekte/3D Drucker/CoreXY/Assembly/Parts/Screws/DIN7965 - Schraubeinsatz - M3.FCStd
  timeLastImport = 1430763186
  updateColors = true
FEATURE [Part::FeaturePython] DIN7965___Schraubeinsatz___M3_import014  # a2plus imported part (geometry in sourceFile) (typed FeaturePython)
  Placement = pos=(41,231.705,462.2) rot=(0,0,1;0rad)
  fixedPosition = false
  sourceFile = <userpath>/CloudStation/Hobbyprojekte/3D Drucker/CoreXY/Assembly/Parts/Screws/DIN7965 - Schraubeinsatz - M3.FCStd
  timeLastImport = 1430763186
  updateColors = true
FEATURE [Part::FeaturePython] DIN7965___Schraubeinsatz___M3_import015  # a2plus imported part (geometry in sourceFile) (typed FeaturePython)
  Placement = pos=(41,167.705,462.2) rot=(0,0,1;0rad)
  fixedPosition = false
  sourceFile = <userpath>/CloudStation/Hobbyprojekte/3D Drucker/CoreXY/Assembly/Parts/Screws/DIN7965 - Schraubeinsatz - M3.FCStd
  timeLastImport = 1430763186
  updateColors = true
FEATURE [Part::FeaturePython] DIN7965___Schraubeinsatz___M3_import016  # a2plus imported part (geometry in sourceFile) (typed FeaturePython)
  Placement = pos=(41,185.705,462.2) rot=(0,0,1;0rad)
  fixedPosition = false
  sourceFile = <userpath>/CloudStation/Hobbyprojekte/3D Drucker/CoreXY/Assembly/Parts/Screws/DIN7965 - Schraubeinsatz - M3.FCStd
  timeLastImport = 1430763186
  updateColors = true
FEATURE [App::DocumentObjectGroup] Gruppe063  label="Bearings008"
  Group = -> [LM8uu_013,LM8uu_014]
FEATURE [App::DocumentObjectGroup] Gruppe065  label="Distancers006"
FEATURE [App::DocumentObjectGroup] Gruppe069  label="Bearings009"
  Group = -> [LM8uu_009,LM8uu_010,LM8uu_011,LM8uu_012]
FEATURE [App::DocumentObjectGroup] Gruppe070  label="Screws009"
FEATURE [App::DocumentObjectGroup] Gruppe072  label="C04H010033-Ceramic-cartridge-heater"
  Group = -> [Part__Feature361,Part__Feature360]
FEATURE [App::DocumentObjectGroup] Gruppe073  label="C04H010008-B57560G104F-Thermistor"
  Group = -> [Part__Feature365,Part__Feature364]
FEATURE [App::DocumentObjectGroup] Group001  label="Hot-end-v1"
  Group = -> [Part__Feature357,Part__Feature358,Part__Feature356,Part__Feature363,Part__Feature362,Gruppe072,Gruppe073]
FEATURE [App::DocumentObjectGroup] Gruppe077  label="Distancers007"
FEATURE [Part::FeaturePython] GT2_Belt_left_01001  label="GT2_Belt_left_01"  # a2plus imported part (geometry in sourceFile) (typed FeaturePython)
  Placement = pos=(-0.05,378.05,462.254) rot=(0,0,1;0rad)
  fixedPosition = false
  sourceFile = <userpath>/CloudStation/Hobbyprojekte/3D Drucker/CoreXY/Assembly/Parts/Belts/GT2-Belt_left.FCStd
  timeLastImport = 1444865939
  updateColors = true
FEATURE [App::DocumentObjectGroup] Gruppe087  label="Carrier002"
  Group = -> [Cut]
FEATURE [App::DocumentObjectGroup] Group  label="BQ Witbox Extruder"
  Group = -> [Compound002,Part__Feature350,Compound003,Part__Feature348,Part__Feature349,Part__Feature351,Part__Feature352,Part__Feature353,Part__Feature354,Part__Feature355,Part__Feature366,Part__Feature367,Part__Feature368,Part__Feature369,Part__Feature370,Part__Feature371,Part__Feature372,Compound004,Part__Feature375,Part__Feature359,Part__Feature376,Part__Feature377,Group001,Gruppe087]
FEATURE [App::DocumentObjectGroup] Gruppe088  label="E3D Extruder"
FEATURE [App::DocumentObjectGroup] Gruppe089  label="Stepstruder MK7"
FEATURE [App::DocumentObjectGroup] Gruppe091  label="Dual E3D Mk6 Bowden"
FEATURE [Part::FeaturePython] Kraken_01  # a2plus imported part (geometry in sourceFile) (typed FeaturePython)
  Placement = pos=(220.157,208.742,454.2) rot=(0.57735,0.57735,0.57735;2.0944rad)
  fixedPosition = false
  sourceFile = <userpath>/CloudStation/Hobbyprojekte/3D Drucker/CoreXY/Assembly/Parts/Hotend/Kraken.FCStd
  timeLastImport = 1444085950
  updateColors = true
FEATURE [Part::FeaturePython] Chimera_01  # a2plus imported part (geometry in sourceFile) (typed FeaturePython)
  Placement = pos=(170.937,210.507,514.276) rot=(0,0,1;0rad)
  fixedPosition = false
  sourceFile = /Applications/FreeCAD.app/Contents/Mod/FreeCAD-library/Electrical Parts/Hotend/E3D Cyclops/Chimera.FCStd
  timeLastImport = 1444947291
  updateColors = true
FEATURE [App::DocumentObjectGroup] Gruppe096  label="E3D Chimera"
  Group = -> [Chimera_01]
FEATURE [Part::FeaturePython] Kraken_Carriage_01  # a2plus imported part (geometry in sourceFile) (typed FeaturePython)
  Placement = pos=(222.157,208.742,477.2) rot=(0,0,1;0rad)
  fixedPosition = false
  sourceFile = <userpath>/CloudStation/Hobbyprojekte/3D Drucker/CoreXY/Assembly/Parts/Printed Parts/Kraken_Carriage.FCStd
  timeLastImport = 1445212377
  updateColors = true
FEATURE [App::DocumentObjectGroup] Gruppe090  label="Kraken"
  Group = -> [Kraken_01,Kraken_Carriage_01]
FEATURE [Part::FeaturePython] MK2_Heatbed_Mockup_215x215_01  # a2plus imported part (geometry in sourceFile) (typed FeaturePython)
  Placement = pos=(110.544,322.172,401.913) rot=(0,0,-1;1.5708rad)
  fixedPosition = false
  sourceFile = <userpath>/CloudStation/Hobbyprojekte/3D Drucker/CoreXY/Assembly/Parts/!Temp Folder/3D Printer Parts/MK2_Heatbed_Mockup_215x215.FCStd
  timeLastImport = 1428781808
  updateColors = true
FEATURE [Part::Feature] Part__Feature176  label="cable-guide010"
  Placement = pos=(247.116,0.269836,252.949) rot=(0,0,1;0rad)
  shape: bbox 14.65 x 15.57 x 5 mm, 24 faces (baked)
FEATURE [Part::Feature] BOLTS_part001  label="Radial Ball Bearing DIN625-1 608-2RS"
  Placement = pos=(55,42,107) rot=(0.707107,0.707107,0;3.14159rad)
  shape: bbox 23.81 x 23.81 x 7 mm, 20 faces, 3 solids (baked)
FEATURE [Part::Feature] BOLTS_part002  label="Radial Ball Bearing DIN625-1 608-2RS001"
  Placement = pos=(55,42,120) rot=(0.707107,0.707107,0;3.14159rad)
  shape: bbox 23.81 x 23.81 x 7 mm, 20 faces, 3 solids (baked)
FEATURE [Part::Feature] BOLTS_part003  label="Radial Ball Bearing DIN625-1 608-2RS002"
  Placement = pos=(385,42,113) rot=(0,0,1;0rad)
  shape: bbox 23.81 x 23.81 x 7 mm, 20 faces, 3 solids (baked)
FEATURE [Part::Feature] BOLTS_part004  label="Radial Ball Bearing DIN625-1 608-2RS003"
  Placement = pos=(385,42,100) rot=(0,0,1;0rad)
  shape: bbox 23.81 x 23.81 x 7 mm, 20 faces, 3 solids (baked)
FEATURE [Part::FeaturePython] Angle_Bracket_import017  label="Angle_Bracket_VHU_003"  # a2plus imported part (geometry in sourceFile) (typed FeaturePython)
  Placement = pos=(-1.6e-10,368.007,429.5) rot=(0.57735,-0.57735,0.57735;4.18879rad)
  fixedPosition = true
  sourceFile = <userpath>/CloudStation/Hobbyprojekte/3D Drucker/CoreXY/Assembly/Parts/Printed Parts/Angle_Bracket.FCStd
  timeLastImport = 1444069248
  updateColors = true
FEATURE [Part::FeaturePython] tslot20x20_import022  label="tslot20x20_UL002"  # a2plus imported part (geometry in sourceFile) (typed FeaturePython)
  Placement = pos=(4e-11,420,449.5) rot=(1,0,0;1.5708rad)
  fixedPosition = true
  sourceFile = <userpath>/CloudStation/Hobbyprojekte/3D Drucker/CoreXY/Assembly/Parts/Alu Extrusion/tslot20x20x400.FCStd
  timeLastImport = 1444069248
  updateColors = true
FEATURE [Part::FeaturePython] Angle_Bracket_import018  label="Angle_Bracket_VLU_003"  # a2plus imported part (geometry in sourceFile) (typed FeaturePython)
  Placement = pos=(20,71.9933,429.5) rot=(0.57735,0.57735,-0.57735;4.18879rad)
  fixedPosition = true
  sourceFile = <userpath>/CloudStation/Hobbyprojekte/3D Drucker/CoreXY/Assembly/Parts/Printed Parts/Angle_Bracket.FCStd
  timeLastImport = 1444069248
  updateColors = true
FEATURE [Part::FeaturePython] Angle_Bracket_import019  label="Angle_Bracket_HRU_003"  # a2plus imported part (geometry in sourceFile) (typed FeaturePython)
  Placement = pos=(420,368.007,429.5) rot=(0.57735,-0.57735,0.57735;4.18879rad)
  fixedPosition = true
  sourceFile = <userpath>/CloudStation/Hobbyprojekte/3D Drucker/CoreXY/Assembly/Parts/Printed Parts/Angle_Bracket.FCStd
  timeLastImport = 1444069248
  updateColors = true
FEATURE [Part::FeaturePython] tslot20x20_import023  label="tslot20x20 (RU)002"  # a2plus imported part (geometry in sourceFile) (typed FeaturePython)
  Placement = pos=(420,420,449.5) rot=(1,0,0;1.5708rad)
  fixedPosition = true
  sourceFile = <userpath>/CloudStation/Hobbyprojekte/3D Drucker/CoreXY/Assembly/Parts/Alu Extrusion/tslot20x20x400.FCStd
  timeLastImport = 1444069248
  updateColors = true
FEATURE [Part::FeaturePython] Angle_Bracket_import020  label="Angle_Bracket_VRU_003"  # a2plus imported part (geometry in sourceFile) (typed FeaturePython)
  Placement = pos=(440,71.9933,429.5) rot=(0.57735,0.57735,-0.57735;4.18879rad)
  fixedPosition = true
  sourceFile = <userpath>/CloudStation/Hobbyprojekte/3D Drucker/CoreXY/Assembly/Parts/Printed Parts/Angle_Bracket.FCStd
  timeLastImport = 1444069248
  updateColors = true
FEATURE [Part::FeaturePython] Hammermutter_B_Typ_Nut6_M4_import01048  # a2plus imported part (geometry in sourceFile) (typed FeaturePython)
  Placement = pos=(10,425,415.5) rot=(1,0,0;1.5708rad)
  fixedPosition = false
  sourceFile = <userpath>/CloudStation/Hobbyprojekte/3D Drucker/CoreXY/Assembly/Parts/Screws/Hammermutter B-Typ Nut6 M4.FCStd
  timeLastImport = 1430523528
  updateColors = true
FEATURE [Part::FeaturePython] Hammermutter_B_Typ_Nut6_M4_import01049  # a2plus imported part (geometry in sourceFile) (typed FeaturePython)
  Placement = pos=(10,15,415.5) rot=(-1,0,0;1.5708rad)
  fixedPosition = false
  sourceFile = <userpath>/CloudStation/Hobbyprojekte/3D Drucker/CoreXY/Assembly/Parts/Screws/Hammermutter B-Typ Nut6 M4.FCStd
  timeLastImport = 1430523528
  updateColors = true
FEATURE [Part::FeaturePython] Hammermutter_B_Typ_Nut6_M4_import01050  # a2plus imported part (geometry in sourceFile) (typed FeaturePython)
  Placement = pos=(10,33.9988,434.5) rot=(1,0,0;3.14159rad)
  fixedPosition = false
  sourceFile = <userpath>/CloudStation/Hobbyprojekte/3D Drucker/CoreXY/Assembly/Parts/Screws/Hammermutter B-Typ Nut6 M4.FCStd
  timeLastImport = 1430523528
  updateColors = true
FEATURE [Part::FeaturePython] Hammermutter_B_Typ_Nut6_M4_import01051  # a2plus imported part (geometry in sourceFile) (typed FeaturePython)
  Placement = pos=(10,406.001,434.5) rot=(1,0,0;3.14159rad)
  fixedPosition = false
  sourceFile = <userpath>/CloudStation/Hobbyprojekte/3D Drucker/CoreXY/Assembly/Parts/Screws/Hammermutter B-Typ Nut6 M4.FCStd
  timeLastImport = 1430523528
  updateColors = true
FEATURE [Part::FeaturePython] Hammermutter_B_Typ_Nut6_M4_import01052  # a2plus imported part (geometry in sourceFile) (typed FeaturePython)
  Placement = pos=(430,15,415.5) rot=(-1,0,0;1.5708rad)
  fixedPosition = false
  sourceFile = <userpath>/CloudStation/Hobbyprojekte/3D Drucker/CoreXY/Assembly/Parts/Screws/Hammermutter B-Typ Nut6 M4.FCStd
  timeLastImport = 1430523528
  updateColors = true
FEATURE [Part::FeaturePython] Hammermutter_B_Typ_Nut6_M4_import01053  # a2plus imported part (geometry in sourceFile) (typed FeaturePython)
  Placement = pos=(430,33.9988,434.4) rot=(1,0,0;3.14159rad)
  fixedPosition = false
  sourceFile = <userpath>/CloudStation/Hobbyprojekte/3D Drucker/CoreXY/Assembly/Parts/Screws/Hammermutter B-Typ Nut6 M4.FCStd
  timeLastImport = 1430523528
  updateColors = true
FEATURE [Part::FeaturePython] Hammermutter_B_Typ_Nut6_M4_import01054  # a2plus imported part (geometry in sourceFile) (typed FeaturePython)
  Placement = pos=(430,425,415.5) rot=(1,0,0;1.5708rad)
  fixedPosition = false
  sourceFile = <userpath>/CloudStation/Hobbyprojekte/3D Drucker/CoreXY/Assembly/Parts/Screws/Hammermutter B-Typ Nut6 M4.FCStd
  timeLastImport = 1430523528
  updateColors = true
FEATURE [Part::FeaturePython] Hammermutter_B_Typ_Nut6_M4_import01055  # a2plus imported part (geometry in sourceFile) (typed FeaturePython)
  Placement = pos=(430,406.001,434.5) rot=(1,0,0;3.14159rad)
  fixedPosition = false
  sourceFile = <userpath>/CloudStation/Hobbyprojekte/3D Drucker/CoreXY/Assembly/Parts/Screws/Hammermutter B-Typ Nut6 M4.FCStd
  timeLastImport = 1430523528
  updateColors = true
FEATURE [App::DocumentObjectGroup] Gruppe100  label="Zwischenboden001"
  Group = -> [Angle_Bracket_import02,Angle_Bracket_import16,Angle_Bracket_import14,Angle_Bracket_import10,Angle_Bracket_import04,Angle_Bracket_import06,Angle_Bracket_import12,Angle_Bracket_import08,Gruppe007]
FEATURE [Part::FeaturePython] Hammermutter_B_Typ_Nut6_M4_import01056  # a2plus imported part (geometry in sourceFile) (typed FeaturePython)
  Placement = pos=(357.5,15,110) rot=(0.57735,-0.57735,-0.57735;4.18879rad)
  fixedPosition = false
  sourceFile = <userpath>/CloudStation/Hobbyprojekte/3D Drucker/CoreXY/Assembly/Parts/Screws/Hammermutter B-Typ Nut6 M4.FCStd
  timeLastImport = 1430523528
  updateColors = true
FEATURE [Part::FeaturePython] Hammermutter_B_Typ_Nut6_M4_import01057  # a2plus imported part (geometry in sourceFile) (typed FeaturePython)
  Placement = pos=(425,74,110) rot=(0,-1,0;1.5708rad)
  fixedPosition = false
  sourceFile = <userpath>/CloudStation/Hobbyprojekte/3D Drucker/CoreXY/Assembly/Parts/Screws/Hammermutter B-Typ Nut6 M4.FCStd
  timeLastImport = 1430523528
  updateColors = true
FEATURE [Part::FeaturePython] Hammermutter_B_Typ_Nut6_M4_import01058  # a2plus imported part (geometry in sourceFile) (typed FeaturePython)
  Placement = pos=(82.5,15,110) rot=(0.57735,-0.57735,-0.57735;4.18879rad)
  fixedPosition = false
  sourceFile = <userpath>/CloudStation/Hobbyprojekte/3D Drucker/CoreXY/Assembly/Parts/Screws/Hammermutter B-Typ Nut6 M4.FCStd
  timeLastImport = 1430523528
  updateColors = true
FEATURE [Part::FeaturePython] Hammermutter_B_Typ_Nut6_M4_import01059  # a2plus imported part (geometry in sourceFile) (typed FeaturePython)
  Placement = pos=(15,74,110) rot=(0,1,0;1.5708rad)
  fixedPosition = false
  sourceFile = <userpath>/CloudStation/Hobbyprojekte/3D Drucker/CoreXY/Assembly/Parts/Screws/Hammermutter B-Typ Nut6 M4.FCStd
  timeLastImport = 1430523528
  updateColors = true
FEATURE [Part::FeaturePython] Z_leadscrew_edge_bearing_block_01  # a2plus imported part (geometry in sourceFile) (typed FeaturePython)
  Placement = pos=(385,42,120) rot=(1,0,0;3.14159rad)
  fixedPosition = false
  sourceFile = <userpath>/CloudStation/Hobbyprojekte/3D Drucker/CoreXY/Assembly/Parts/Printed Parts/Z-leadscrew-edge-bearing-block.FCStd
  timeLastImport = 1445300322
  updateColors = true
FEATURE [Part::FeaturePython] Z_leadscrew_edge_bearing_block_01001  # a2plus imported part (geometry in sourceFile) (typed FeaturePython)
  Placement = pos=(55,42,100) rot=(0,0,1;3.14159rad)
  fixedPosition = false
  sourceFile = <userpath>/CloudStation/Hobbyprojekte/3D Drucker/CoreXY/Assembly/Parts/Printed Parts/Z-leadscrew-edge-bearing-block.FCStd
  timeLastImport = 1445300322
  updateColors = true
FEATURE [Part::FeaturePython] Z_axis_clamp_1_01  # a2plus imported part (geometry in sourceFile) (typed FeaturePython)
  Placement = pos=(35,65,429.5) rot=(0,0,1;1.5708rad)
  fixedPosition = true
  sourceFile = <userpath>/CloudStation/Hobbyprojekte/3D Drucker/CoreXY/Assembly/Parts/Printed Parts/Z-axis-clamp-1.FCStd
  timeLastImport = 1445300847
  updateColors = true
FEATURE [Part::FeaturePython] Z_axis_clamp_1_01001  # a2plus imported part (geometry in sourceFile) (typed FeaturePython)
  Placement = pos=(405,65,429.5) rot=(0,0,-1;1.5708rad)
  fixedPosition = false
  sourceFile = <userpath>/CloudStation/Hobbyprojekte/3D Drucker/CoreXY/Assembly/Parts/Printed Parts/Z-axis-clamp-1.FCStd
  timeLastImport = 1445300847
  updateColors = true
FEATURE [Part::FeaturePython] Z_axis_clamp_2_01  # a2plus imported part (geometry in sourceFile) (typed FeaturePython)
  Placement = pos=(405,65,429.5) rot=(0,0,-1;1.5708rad)
  fixedPosition = false
  sourceFile = <userpath>/CloudStation/Hobbyprojekte/3D Drucker/CoreXY/Assembly/Parts/Printed Parts/Z-axis-clamp-2.FCStd
  timeLastImport = 1445301196
  updateColors = true
FEATURE [Part::FeaturePython] Hammermutter_B_Typ_Nut6_M4_import01060  # a2plus imported part (geometry in sourceFile) (typed FeaturePython)
  Placement = pos=(425,76,439.5) rot=(0,-1,0;1.5708rad)
  fixedPosition = false
  sourceFile = <userpath>/CloudStation/Hobbyprojekte/3D Drucker/CoreXY/Assembly/Parts/Screws/Hammermutter B-Typ Nut6 M4.FCStd
  timeLastImport = 1430523528
  updateColors = true
FEATURE [Part::FeaturePython] Hammermutter_B_Typ_Nut6_M4_import01061  # a2plus imported part (geometry in sourceFile) (typed FeaturePython)
  Placement = pos=(425,54,439.5) rot=(0,-1,0;1.5708rad)
  fixedPosition = false
  sourceFile = <userpath>/CloudStation/Hobbyprojekte/3D Drucker/CoreXY/Assembly/Parts/Screws/Hammermutter B-Typ Nut6 M4.FCStd
  timeLastImport = 1430523528
  updateColors = true
FEATURE [Part::FeaturePython] Hammermutter_B_Typ_Nut6_M4_import01062  # a2plus imported part (geometry in sourceFile) (typed FeaturePython)
  Placement = pos=(15,54,439.5) rot=(0,1,0;1.5708rad)
  fixedPosition = false
  sourceFile = <userpath>/CloudStation/Hobbyprojekte/3D Drucker/CoreXY/Assembly/Parts/Screws/Hammermutter B-Typ Nut6 M4.FCStd
  timeLastImport = 1430523528
  updateColors = true
FEATURE [Part::FeaturePython] Hammermutter_B_Typ_Nut6_M4_import01063  # a2plus imported part (geometry in sourceFile) (typed FeaturePython)
  Placement = pos=(15,76,439.5) rot=(0,1,0;1.5708rad)
  fixedPosition = false
  sourceFile = <userpath>/CloudStation/Hobbyprojekte/3D Drucker/CoreXY/Assembly/Parts/Screws/Hammermutter B-Typ Nut6 M4.FCStd
  timeLastImport = 1430523528
  updateColors = true
FEATURE [Part::FeaturePython] XY_Chain_01  # a2plus imported part (geometry in sourceFile) (typed FeaturePython)
  Placement = pos=(1.89117,-1.744,-31.9) rot=(0,0,1;0rad)
  fixedPosition = false
  sourceFile = <userpath>/CloudStation/Hobbyprojekte/3D Drucker/CoreXY/Assembly/Parts/Cable Chain/XY-Chain.FCStd
  timeLastImport = 1445302721
  updateColors = true
FEATURE [Part::FeaturePython] GT2_Belt_right_01  # a2plus imported part (geometry in sourceFile) (typed FeaturePython)
  Placement = pos=(-0.018028,377.997,464.507) rot=(0,0,1;0rad)
  fixedPosition = false
  sourceFile = <userpath>/CloudStation/Hobbyprojekte/3D Drucker/CoreXY/Assembly/Parts/Belts/GT2-Belt_right.FCStd
  timeLastImport = 1445379945
  updateColors = true
FEATURE [App::DocumentObjectGroup] Gruppe044  label="Belt"
  Group = -> [GT2_Belt_left_01001,GT2_Belt_right_01]
FEATURE [Part::FeaturePython] motor_block_left_top_01  label="idler_block_mirrored_bottom_topM001"  # a2plus imported part (geometry in sourceFile) (typed FeaturePython)
  Placement = pos=(20,20,449.5) rot=(0,0,1;3.14159rad)
  fixedPosition = true
  sourceFile = <userpath>/CloudStation/Hobbyprojekte/3D Drucker/CoreXY/Assembly/Parts/Printed Parts/idler-block-bottom-mirrored-topM.FCStd
  timeLastImport = 1445381463
  updateColors = true
FEATURE [Part::FeaturePython] tslot20x20_import024  label="tslot20x20_import_VU002"  # a2plus imported part (geometry in sourceFile) (typed FeaturePython)
  Placement = pos=(420,20,429.5) rot=(0,-1,0;1.5708rad)
  fixedPosition = true
  sourceFile = <userpath>/CloudStation/Hobbyprojekte/3D Drucker/CoreXY/Assembly/Parts/Alu Extrusion/tslot20x20x400.FCStd
  timeLastImport = 1444069248
  updateColors = true
FEATURE [Part::FeaturePython] Angle_Bracket_import022  label="Angle_Bracket_VRU_004"  # a2plus imported part (geometry in sourceFile) (typed FeaturePython)
  Placement = pos=(368.007,20,429.5) rot=(0,0.707107,-0.707107;3.14159rad)
  fixedPosition = true
  sourceFile = <userpath>/CloudStation/Hobbyprojekte/3D Drucker/CoreXY/Assembly/Parts/Printed Parts/Angle_Bracket.FCStd
  timeLastImport = 1444069248
  updateColors = true
FEATURE [Part::FeaturePython] Hammermutter_B_Typ_Nut6_M4_import01065  # a2plus imported part (geometry in sourceFile) (typed FeaturePython)
  Placement = pos=(425,10,415.5) rot=(0.57735,0.57735,-0.57735;4.18879rad)
  fixedPosition = false
  sourceFile = <userpath>/CloudStation/Hobbyprojekte/3D Drucker/CoreXY/Assembly/Parts/Screws/Hammermutter B-Typ Nut6 M4.FCStd
  timeLastImport = 1430523528
  updateColors = true
FEATURE [Part::FeaturePython] Angle_Bracket_import024  label="Angle_Bracket_VLU_004"  # a2plus imported part (geometry in sourceFile) (typed FeaturePython)
  Placement = pos=(71.9933,2.55588e-06,429.5) rot=(-1,0,0;1.5708rad)
  fixedPosition = true
  sourceFile = <userpath>/CloudStation/Hobbyprojekte/3D Drucker/CoreXY/Assembly/Parts/Printed Parts/Angle_Bracket.FCStd
  timeLastImport = 1444069248
  updateColors = true
FEATURE [Part::FeaturePython] Hammermutter_B_Typ_Nut6_M4_import01066  # a2plus imported part (geometry in sourceFile) (typed FeaturePython)
  Placement = pos=(406.001,10,434.5) rot=(0.707107,0.707107,0;3.14159rad)
  fixedPosition = false
  sourceFile = <userpath>/CloudStation/Hobbyprojekte/3D Drucker/CoreXY/Assembly/Parts/Screws/Hammermutter B-Typ Nut6 M4.FCStd
  timeLastImport = 1430523528
  updateColors = true
FEATURE [Part::FeaturePython] Hammermutter_B_Typ_Nut6_M4_import01069  # a2plus imported part (geometry in sourceFile) (typed FeaturePython)
  Placement = pos=(15,10,415.5) rot=(0.57735,-0.57735,0.57735;4.18879rad)
  fixedPosition = false
  sourceFile = <userpath>/CloudStation/Hobbyprojekte/3D Drucker/CoreXY/Assembly/Parts/Screws/Hammermutter B-Typ Nut6 M4.FCStd
  timeLastImport = 1430523528
  updateColors = true
FEATURE [Part::FeaturePython] Hammermutter_B_Typ_Nut6_M4_import01071  # a2plus imported part (geometry in sourceFile) (typed FeaturePython)
  Placement = pos=(33.9988,10,434.5) rot=(0.707107,0.707107,0;3.14159rad)
  fixedPosition = false
  sourceFile = <userpath>/CloudStation/Hobbyprojekte/3D Drucker/CoreXY/Assembly/Parts/Screws/Hammermutter B-Typ Nut6 M4.FCStd
  timeLastImport = 1430523528
  updateColors = true
FEATURE [Part::FeaturePython] tslot20x20_import025  # a2plus imported part (geometry in sourceFile) (typed FeaturePython)
  Placement = pos=(420,440,429.5) rot=(0,-1,0;1.5708rad)
  fixedPosition = true
  sourceFile = <userpath>/CloudStation/Hobbyprojekte/3D Drucker/CoreXY/Assembly/Parts/Alu Extrusion/tslot20x20x400.FCStd
  timeLastImport = 1444069248
  updateColors = true
FEATURE [App::DocumentObjectGroup] Gruppe098  label="x-Befestigung"
  Group = -> [tslot20x20_import024,tslot20x20_import025]
FEATURE [Part::FeaturePython] Angle_Bracket_import026  label="Angle_Bracket_HRU_004"  # a2plus imported part (geometry in sourceFile) (typed FeaturePython)
  Placement = pos=(420,420,377.507) rot=(-0.57735,0.57735,0.57735;2.0944rad)
  fixedPosition = true
  sourceFile = <userpath>/CloudStation/Hobbyprojekte/3D Drucker/CoreXY/Assembly/Parts/Printed Parts/Angle_Bracket.FCStd
  timeLastImport = 1444069248
  updateColors = true
FEATURE [Part::FeaturePython] Hammermutter_B_Typ_Nut6_M4_import01073  # a2plus imported part (geometry in sourceFile) (typed FeaturePython)
  Placement = pos=(425,430,415.501) rot=(0.57735,-0.57735,-0.57735;2.0944rad)
  fixedPosition = false
  sourceFile = <userpath>/CloudStation/Hobbyprojekte/3D Drucker/CoreXY/Assembly/Parts/Screws/Hammermutter B-Typ Nut6 M4.FCStd
  timeLastImport = 1430523528
  updateColors = true
FEATURE [Part::FeaturePython] Hammermutter_B_Typ_Nut6_M4_import01075  # a2plus imported part (geometry in sourceFile) (typed FeaturePython)
  Placement = pos=(406,430,434.5) rot=(0.707107,0.707107,0;3.14159rad)
  fixedPosition = false
  sourceFile = <userpath>/CloudStation/Hobbyprojekte/3D Drucker/CoreXY/Assembly/Parts/Screws/Hammermutter B-Typ Nut6 M4.FCStd
  timeLastImport = 1430523528
  updateColors = true
FEATURE [Part::FeaturePython] Hammermutter_B_Typ_Nut6_M4_import01077  # a2plus imported part (geometry in sourceFile) (typed FeaturePython)
  Placement = pos=(15,430,415.501) rot=(0.57735,0.57735,0.57735;2.0944rad)
  fixedPosition = false
  sourceFile = <userpath>/CloudStation/Hobbyprojekte/3D Drucker/CoreXY/Assembly/Parts/Screws/Hammermutter B-Typ Nut6 M4.FCStd
  timeLastImport = 1430523528
  updateColors = true
FEATURE [Part::FeaturePython] Angle_Bracket_import028  label="Angle_Bracket_VHU_004"  # a2plus imported part (geometry in sourceFile) (typed FeaturePython)
  Placement = pos=(71.9933,420,429.5) rot=(-1,0,0;1.5708rad)
  fixedPosition = true
  sourceFile = <userpath>/CloudStation/Hobbyprojekte/3D Drucker/CoreXY/Assembly/Parts/Printed Parts/Angle_Bracket.FCStd
  timeLastImport = 1444069248
  updateColors = true
FEATURE [Part::FeaturePython] Hammermutter_B_Typ_Nut6_M4_import01079  # a2plus imported part (geometry in sourceFile) (typed FeaturePython)
  Placement = pos=(33.9988,430,434.5) rot=(0.707107,0.707107,0;3.14159rad)
  fixedPosition = false
  sourceFile = <userpath>/CloudStation/Hobbyprojekte/3D Drucker/CoreXY/Assembly/Parts/Screws/Hammermutter B-Typ Nut6 M4.FCStd
  timeLastImport = 1430523528
  updateColors = true
FEATURE [Part::FeaturePython] smooth_bar_8x350_01  # a2plus imported part (geometry in sourceFile) (typed FeaturePython)
  Placement = pos=(45,228.8,470.2) rot=(0.57735,0.57735,0.57735;2.0944rad)
  fixedPosition = true
  sourceFile = <userpath>/CloudStation/Hobbyprojekte/3D Drucker/CoreXY/Assembly/Parts/Bearings/smooth-bar-8x350.FCStd
  timeLastImport = 1445473492
  updateColors = true
FEATURE [Part::FeaturePython] smooth_bar_8x350_002  # a2plus imported part (geometry in sourceFile) (typed FeaturePython)
  Placement = pos=(45,188.8,470.2) rot=(0.57735,0.57735,0.57735;2.0944rad)
  fixedPosition = true
  sourceFile = <userpath>/CloudStation/Hobbyprojekte/3D Drucker/CoreXY/Assembly/Parts/Bearings/smooth-bar-8x350.FCStd
  timeLastImport = 1445473492
  updateColors = true
FEATURE [App::DocumentObjectGroup] Gruppe067  label="Smooth Bars001"
  Group = -> [smooth_bar_8x350_01,smooth_bar_8x350_002]
FEATURE [Part::FeaturePython] DIN7965___Schraubeinsatz___M3_import021  # a2plus imported part (geometry in sourceFile) (typed FeaturePython)
  Placement = pos=(53,235.8,462.2) rot=(0,0,1;3.14159rad)
  fixedPosition = false
  sourceFile = <userpath>/CloudStation/Hobbyprojekte/3D Drucker/CoreXY/Assembly/Parts/Screws/DIN7965 - Schraubeinsatz - M3.FCStd
  timeLastImport = 1430763186
  updateColors = true
FEATURE [Part::FeaturePython] DIN7965___Schraubeinsatz___M3_import022  # a2plus imported part (geometry in sourceFile) (typed FeaturePython)
  Placement = pos=(53,181.8,462.2) rot=(0,0,1;3.14159rad)
  fixedPosition = false
  sourceFile = <userpath>/CloudStation/Hobbyprojekte/3D Drucker/CoreXY/Assembly/Parts/Screws/DIN7965 - Schraubeinsatz - M3.FCStd
  timeLastImport = 1430763186
  updateColors = true
FEATURE [Part::FeaturePython] DIN7965___Schraubeinsatz___M3_import023  # a2plus imported part (geometry in sourceFile) (typed FeaturePython)
  Placement = pos=(53,195.8,462.2) rot=(0,0,1;3.14159rad)
  fixedPosition = false
  sourceFile = <userpath>/CloudStation/Hobbyprojekte/3D Drucker/CoreXY/Assembly/Parts/Screws/DIN7965 - Schraubeinsatz - M3.FCStd
  timeLastImport = 1430763186
  updateColors = true
FEATURE [Part::FeaturePython] DIN7965___Schraubeinsatz___M3_import024  # a2plus imported part (geometry in sourceFile) (typed FeaturePython)
  Placement = pos=(53,221.8,462.2) rot=(0,0,1;3.14159rad)
  fixedPosition = false
  sourceFile = <userpath>/CloudStation/Hobbyprojekte/3D Drucker/CoreXY/Assembly/Parts/Screws/DIN7965 - Schraubeinsatz - M3.FCStd
  timeLastImport = 1430763186
  updateColors = true
FEATURE [Part::FeaturePython] XY_block_top_topM_002  # a2plus imported part (geometry in sourceFile) (typed FeaturePython)
  Placement = pos=(13,208.8,481.2) rot=(1,0,0;3.14159rad)
  fixedPosition = false
  sourceFile = <userpath>/CloudStation/Hobbyprojekte/3D Drucker/CoreXY/Assembly/Parts/Printed Parts/XY-block-top topM.FCStd
  timeLastImport = 1445594597
  updateColors = true
FEATURE [Part::FeaturePython] LM8uu_018  # a2plus imported part (geometry in sourceFile) (typed FeaturePython)
  Placement = pos=(13,222.3,470.2) rot=(0,0,1;3.14159rad)
  fixedPosition = false
  sourceFile = <userpath>/CloudStation/Hobbyprojekte/3D Drucker/CoreXY/Assembly/Parts/Bearings/LM8uu.fcstd
  timeLastImport = 1430143348
  updateColors = true
FEATURE [Part::FeaturePython] F624zz_import017  # a2plus imported part (geometry in sourceFile) (typed FeaturePython)
  Placement = pos=(38,216.3,459) rot=(0,0,1;0rad)
  fixedPosition = false
  sourceFile = <userpath>/CloudStation/Hobbyprojekte/3D Drucker/CoreXY/Assembly/Parts/Bearings/DIN625-1_F624zz.FCStd
  timeLastImport = 1430848638
FEATURE [Part::FeaturePython] LM8uu_017  # a2plus imported part (geometry in sourceFile) (typed FeaturePython)
  Placement = pos=(13,195.3,470.2) rot=(0,0,1;3.14159rad)
  fixedPosition = false
  sourceFile = <userpath>/CloudStation/Hobbyprojekte/3D Drucker/CoreXY/Assembly/Parts/Bearings/LM8uu.fcstd
  timeLastImport = 1430143348
  updateColors = true
FEATURE [App::DocumentObjectGroup] Gruppe031  label="Bearings004"
  Group = -> [LM8uu_017,LM8uu_018]
FEATURE [Part::FeaturePython] GT2Bearing_002  # a2plus imported part (geometry in sourceFile) (typed FeaturePython)
  Placement = pos=(38,201.3,468.61) rot=(0,0,1;3.14159rad)
  fixedPosition = false
  sourceFile = <userpath>/CloudStation/Hobbyprojekte/3D Drucker/CoreXY/Assembly/Parts/Belts/GT2Bearing.FCStd
  timeLastImport = 1444935738
  updateColors = true
FEATURE [Part::FeaturePython] DIN625_1_624_ZZ_import01021  # a2plus imported part (geometry in sourceFile) (typed FeaturePython)
  Placement = pos=(38,216.3,464) rot=(0,0,1;0rad)
  fixedPosition = false
  sourceFile = <userpath>/CloudStation/Hobbyprojekte/3D Drucker/CoreXY/Assembly/Parts/Bearings/DIN625-1_624-ZZ.FCStd
  timeLastImport = 1430517302
  updateColors = true
FEATURE [Part::FeaturePython] GT2Bearing_003  # a2plus imported part (geometry in sourceFile) (typed FeaturePython)
  Placement = pos=(38,28,469.01) rot=(0,0,1;3.14159rad)
  fixedPosition = false
  sourceFile = <userpath>/CloudStation/Hobbyprojekte/3D Drucker/CoreXY/Assembly/Parts/Belts/GT2Bearing.FCStd
  timeLastImport = 1444935738
  updateColors = true
FEATURE [Part::FeaturePython] GT2Bearing_004  # a2plus imported part (geometry in sourceFile) (typed FeaturePython)
  Placement = pos=(33,10,459.69) rot=(0,0,1;3.14159rad)
  fixedPosition = true
  sourceFile = <userpath>/CloudStation/Hobbyprojekte/3D Drucker/CoreXY/Assembly/Parts/Belts/GT2Bearing.FCStd
  timeLastImport = 1444935738
  updateColors = true
FEATURE [App::DocumentObjectGroup] Gruppe025  label="Bearings003"
  Group = -> [GT2Bearing_004,GT2Bearing_003]
FEATURE [Part::FeaturePython] carriage_01  # a2plus imported part (geometry in sourceFile) (typed FeaturePython)
  Placement = pos=(220.157,208.8,459.9) rot=(0,0,1;0rad)
  fixedPosition = false
  sourceFile = <userpath>/CloudStation/Hobbyprojekte/3D Drucker/CoreXY/Assembly/Parts/Printed Parts/carriage.FCStd
  timeLastImport = 1445632270
  updateColors = true
FEATURE [Part::FeaturePython] carriage_down_01  # a2plus imported part (geometry in sourceFile) (typed FeaturePython)
  Placement = pos=(220.157,208.742,474.2) rot=(0,0,1;0rad)
  fixedPosition = false
  sourceFile = <userpath>/CloudStation/Hobbyprojekte/3D Drucker/CoreXY/Assembly/Parts/Printed Parts/carriage-down.FCStd
  timeLastImport = 1445639657
  updateColors = true
FEATURE [App::DocumentObjectGroup] Gruppe071  label="Main Parts009"
  Group = -> [Part__Feature124,Part__Feature125,Part__Feature128,Part__Feature129,carriage_down_01]
FEATURE [App::DocumentObjectGroup] Gruppe061  label="Carrier001"
  Group = -> [Gruppe069,Gruppe070,Gruppe071]
FEATURE [Part::FeaturePython] idler_block_bottom_topM_01  # a2plus imported part (geometry in sourceFile) (typed FeaturePython)
  Placement = pos=(420,20,449.5) rot=(0,1,0;3.14159rad)
  fixedPosition = true
  sourceFile = <userpath>/CloudStation/Hobbyprojekte/3D Drucker/CoreXY/Assembly/Parts/Printed Parts/idler-block-bottom-topM.FCStd
  timeLastImport = 1444924419
  updateColors = true
FEATURE [Part::FeaturePython] spacer9mm_import008  # a2plus imported part (geometry in sourceFile) (typed FeaturePython)
  Placement = pos=(402,28,478.8) rot=(0,1,0;3.14159rad)
  fixedPosition = false
  sourceFile = <userpath>/CloudStation/Hobbyprojekte/3D Drucker/CoreXY/Assembly/Parts/Printed Parts/spacer9mm.FCStd
  timeLastImport = 1444069248
  updateColors = true
FEATURE [Part::FeaturePython] GT2Bearing_005  # a2plus imported part (geometry in sourceFile) (typed FeaturePython)
  Placement = pos=(402,28,459.69) rot=(0,0,1;3.14159rad)
  fixedPosition = false
  sourceFile = <userpath>/CloudStation/Hobbyprojekte/3D Drucker/CoreXY/Assembly/Parts/Belts/GT2Bearing.FCStd
  timeLastImport = 1444935738
  updateColors = true
FEATURE [Part::FeaturePython] Hammermutter_B_Typ_Nut6_M4_import01080  # a2plus imported part (geometry in sourceFile) (typed FeaturePython)
  Placement = pos=(407,10,445.3) rot=(0,0,-1;1.5708rad)
  fixedPosition = false
  sourceFile = <userpath>/CloudStation/Hobbyprojekte/3D Drucker/CoreXY/Assembly/Parts/Screws/Hammermutter B-Typ Nut6 M4.FCStd
  timeLastImport = 1430523528
  updateColors = true
FEATURE [Part::FeaturePython] GT2Bearing_006  # a2plus imported part (geometry in sourceFile) (typed FeaturePython)
  Placement = pos=(407,10,469.01) rot=(0,0,1;3.14159rad)
  fixedPosition = false
  sourceFile = <userpath>/CloudStation/Hobbyprojekte/3D Drucker/CoreXY/Assembly/Parts/Belts/GT2Bearing.FCStd
  timeLastImport = 1444935738
  updateColors = true
FEATURE [App::DocumentObjectGroup] Gruppe021  label="Bearings002"
  Group = -> [GT2Bearing_005,GT2Bearing_006]
FEATURE [Part::FeaturePython] spacer9mm_import010  # a2plus imported part (geometry in sourceFile) (typed FeaturePython)
  Placement = pos=(407,10,468.9) rot=(0,1,0;3.14159rad)
  fixedPosition = false
  sourceFile = <userpath>/CloudStation/Hobbyprojekte/3D Drucker/CoreXY/Assembly/Parts/Printed Parts/spacer9mm.FCStd
  timeLastImport = 1444069248
  updateColors = true
FEATURE [App::DocumentObjectGroup] Gruppe023  label="Distancers002"
  Group = -> [spacer9mm_import008,spacer9mm_import010]
FEATURE [Part::FeaturePython] DIN7965___Schraubeinsatz___M3_import025  # a2plus imported part (geometry in sourceFile) (typed FeaturePython)
  Placement = pos=(385,35,469.5) rot=(0,1,0;3.14159rad)
  fixedPosition = false
  sourceFile = <userpath>/CloudStation/Hobbyprojekte/3D Drucker/CoreXY/Assembly/Parts/Screws/DIN7965 - Schraubeinsatz - M3.FCStd
  timeLastImport = 1430763186
  updateColors = true
FEATURE [Part::FeaturePython] Hammermutter_B_Typ_Nut6_M4_import01081  # a2plus imported part (geometry in sourceFile) (typed FeaturePython)
  Placement = pos=(392,10,445.3) rot=(0,0,-1;1.5708rad)
  fixedPosition = false
  sourceFile = <userpath>/CloudStation/Hobbyprojekte/3D Drucker/CoreXY/Assembly/Parts/Screws/Hammermutter B-Typ Nut6 M4.FCStd
  timeLastImport = 1430523528
  updateColors = true
FEATURE [Part::FeaturePython] idler_block_mirrored_topM_01  # a2plus imported part (geometry in sourceFile) (typed FeaturePython)
  Placement = pos=(20,20,484.5) rot=(0,1,0;3.14159rad)
  fixedPosition = false
  sourceFile = <userpath>/CloudStation/Hobbyprojekte/3D Drucker/CoreXY/Assembly/Parts/Printed Parts/idler-block-mirrored-topM.FCStd
  timeLastImport = 1445647594
  updateColors = true
FEATURE [App::DocumentObjectGroup] Gruppe028  label="Main Parts003"
  Group = -> [motor_block_left_top_01,idler_block_mirrored_topM_01]
FEATURE [Part::Feature] Part__Feature403  label="belt-clamp004"
  Placement = pos=(220.157,208.6,299.9) rot=(0,0,1;0rad)
  shape: bbox 15 x 22 x 10 mm, 58 faces (baked)
FEATURE [Part::Feature] Part__Feature404  label="belt-clamp005"
  Placement = pos=(220.157,208.6,298.9) rot=(0,0,1;0rad)
  shape: bbox 15 x 22 x 10 mm, 58 faces (baked)
FEATURE [Part::Feature] Part__Feature405  label="belt-clamp006"
  Placement = pos=(220.157,208.6,298.9) rot=(0,0,1;0rad)
  shape: bbox 15 x 22 x 10 mm, 58 faces (baked)
FEATURE [Part::Feature] Part__Feature406  label="belt-clamp007"
  Placement = pos=(220.157,208.6,299.9) rot=(0,0,1;0rad)
  shape: bbox 15 x 22 x 10 mm, 58 faces (baked)
FEATURE [App::DocumentObjectGroup] Gruppe043  label="Main Parts006"
  Group = -> [carriage_01,Part__Feature403,Part__Feature404,Part__Feature405,Part__Feature406]
FEATURE [App::DocumentObjectGroup] Gruppe040  label="Carrier"
  Group = -> [Gruppe041,Gruppe042,Gruppe043]
FEATURE [Part::FeaturePython] smooth_bar_8x360_01002  # a2plus imported part (geometry in sourceFile) (typed FeaturePython)
  Placement = pos=(13,388.542,470.2) rot=(1,0,0;1.5708rad)
  fixedPosition = true
  sourceFile = <userpath>/CloudStation/Hobbyprojekte/3D Drucker/CoreXY/Assembly/Parts/Bearings/smooth-bar-8x360.FCStd
  timeLastImport = 1445692653
  updateColors = true
FEATURE [Part::FeaturePython] XY_block_topM_01001  label="XY_block_topM_01"  # a2plus imported part (geometry in sourceFile) (typed FeaturePython)
  Placement = pos=(13,208.8,456.2) rot=(0,0,1;0rad)
  fixedPosition = true
  sourceFile = <userpath>/CloudStation/Hobbyprojekte/3D Drucker/CoreXY/Assembly/Parts/Printed Parts/XY-block topM.FCStd
  timeLastImport = 1445693115
  updateColors = true
FEATURE [App::DocumentObjectGroup] Gruppe034  label="Main Parts004"
  Group = -> [XY_block_top_topM_002,XY_block_topM_01001]
FEATURE [Part::FeaturePython] GT2Bearing_007  # a2plus imported part (geometry in sourceFile) (typed FeaturePython)
  Placement = pos=(407,413,469.007) rot=(0,0,1;3.14159rad)
  fixedPosition = false
  sourceFile = <userpath>/CloudStation/Hobbyprojekte/3D Drucker/CoreXY/Assembly/Parts/Belts/GT2Bearing.FCStd
  timeLastImport = 1444935738
  updateColors = true
FEATURE [Part::FeaturePython] DIN625_1_624_ZZ_import01022  # a2plus imported part (geometry in sourceFile) (typed FeaturePython)
  Placement = pos=(402,388,472.9) rot=(0,0,1;0rad)
  fixedPosition = false
  sourceFile = <userpath>/CloudStation/Hobbyprojekte/3D Drucker/CoreXY/Assembly/Parts/Bearings/DIN625-1_624-ZZ.FCStd
  timeLastImport = 1430517302
  updateColors = true
FEATURE [Part::FeaturePython] F624zz_import018  # a2plus imported part (geometry in sourceFile) (typed FeaturePython)
  Placement = pos=(402,388,467.9) rot=(0,0,1;0rad)
  fixedPosition = false
  sourceFile = <userpath>/CloudStation/Hobbyprojekte/3D Drucker/CoreXY/Assembly/Parts/Bearings/DIN625-1_F624zz.FCStd
  timeLastImport = 1430848638
FEATURE [App::DocumentObjectGroup] Gruppe010  label="Bearings"
  Group = -> [DIN625_1_624_ZZ_import01003,DIN625_1_624_ZZ_import01004,GT2Pulley_01,GT2Bearing_007,F624zz_import018,DIN625_1_624_ZZ_import01022]
FEATURE [Part::FeaturePython] spacer18_3mm_01  # a2plus imported part (geometry in sourceFile) (typed FeaturePython)
  Placement = pos=(371.5,414.5,460.5) rot=(0,0,1;0rad)
  fixedPosition = false
  sourceFile = <userpath>/CloudStation/Hobbyprojekte/3D Drucker/CoreXY/Assembly/Parts/Printed Parts/spacer18_3mm.FCStd
  timeLastImport = 1445700465
  updateColors = true
FEATURE [Part::FeaturePython] DIN625_1_624_ZZ_import01023  # a2plus imported part (geometry in sourceFile) (typed FeaturePython)
  Placement = pos=(38,388,464.3) rot=(0,0,1;0rad)
  fixedPosition = false
  sourceFile = <userpath>/CloudStation/Hobbyprojekte/3D Drucker/CoreXY/Assembly/Parts/Bearings/DIN625-1_624-ZZ.FCStd
  timeLastImport = 1430517302
  updateColors = true
FEATURE [Part::FeaturePython] DIN625_1_624_ZZ_import01024  # a2plus imported part (geometry in sourceFile) (typed FeaturePython)
  Placement = pos=(56.5,403,464.3) rot=(0,1,0;3.14159rad)
  fixedPosition = false
  sourceFile = <userpath>/CloudStation/Hobbyprojekte/3D Drucker/CoreXY/Assembly/Parts/Bearings/DIN625-1_624-ZZ.FCStd
  timeLastImport = 1430517302
  updateColors = true
FEATURE [Part::FeaturePython] DIN625_1_624_ZZ_import01025  # a2plus imported part (geometry in sourceFile) (typed FeaturePython)
  Placement = pos=(56.5,403,469.3) rot=(0,1,0;3.14159rad)
  fixedPosition = false
  sourceFile = <userpath>/CloudStation/Hobbyprojekte/3D Drucker/CoreXY/Assembly/Parts/Bearings/DIN625-1_624-ZZ.FCStd
  timeLastImport = 1430517302
  updateColors = true
FEATURE [Part::FeaturePython] GT2Bearing_008  # a2plus imported part (geometry in sourceFile) (typed FeaturePython)
  Placement = pos=(33,413,459.507) rot=(0,0,1;3.14159rad)
  fixedPosition = false
  sourceFile = <userpath>/CloudStation/Hobbyprojekte/3D Drucker/CoreXY/Assembly/Parts/Belts/GT2Bearing.FCStd
  timeLastImport = 1444935738
  updateColors = true
FEATURE [Part::FeaturePython] F624zz_import019  # a2plus imported part (geometry in sourceFile) (typed FeaturePython)
  Placement = pos=(38,388,459.3) rot=(0,0,1;0rad)
  fixedPosition = false
  sourceFile = <userpath>/CloudStation/Hobbyprojekte/3D Drucker/CoreXY/Assembly/Parts/Bearings/DIN625-1_F624zz.FCStd
  timeLastImport = 1430848638
  updateColors = true
FEATURE [App::DocumentObjectGroup] Gruppe014  label="Bearings001"
  Group = -> [GT2Pulley_002,DIN625_1_624_ZZ_import01023,DIN625_1_624_ZZ_import01024,DIN625_1_624_ZZ_import01025,GT2Bearing_008,F624zz_import019]
FEATURE [Part::FeaturePython] spacer18_3mm_002  # a2plus imported part (geometry in sourceFile) (typed FeaturePython)
  Placement = pos=(68.5,414.5,460.5) rot=(0,0,1;0rad)
  fixedPosition = false
  sourceFile = <userpath>/CloudStation/Hobbyprojekte/3D Drucker/CoreXY/Assembly/Parts/Printed Parts/spacer18_3mm.FCStd
  timeLastImport = 1445700465
  updateColors = true
FEATURE [Part::FeaturePython] DIN7965___Schraubeinsatz___M3_import026  # a2plus imported part (geometry in sourceFile) (typed FeaturePython)
  Placement = pos=(55,383,476.5) rot=(0,1,0;3.14159rad)
  fixedPosition = false
  sourceFile = <userpath>/CloudStation/Hobbyprojekte/3D Drucker/CoreXY/Assembly/Parts/Screws/DIN7965 - Schraubeinsatz - M3.FCStd
  timeLastImport = 1430763186
  updateColors = true
FEATURE [Part::FeaturePython] smooth_bar_8x360_01004  # a2plus imported part (geometry in sourceFile) (typed FeaturePython)
  Placement = pos=(427,388.542,470.2) rot=(1,0,0;1.5708rad)
  fixedPosition = true
  sourceFile = <userpath>/CloudStation/Hobbyprojekte/3D Drucker/CoreXY/Assembly/Parts/Bearings/smooth-bar-8x360.FCStd
  timeLastImport = 1445692653
  updateColors = true
FEATURE [App::DocumentObjectGroup] Gruppe029  label="Smooth Bars"
  Group = -> [smooth_bar_8x360_01002,smooth_bar_8x360_01004]
FEATURE [Part::FeaturePython] motor_block_topM_01  # a2plus imported part (geometry in sourceFile) (typed FeaturePython)
  Placement = pos=(440,378,484.5) rot=(0,1,0;3.14159rad)
  fixedPosition = false
  sourceFile = <userpath>/CloudStation/Hobbyprojekte/3D Drucker/CoreXY/Assembly/Parts/Printed Parts/motor-block-topM.FCStd
  timeLastImport = 1458344698
  updateColors = true
FEATURE [Part::FeaturePython] motor_block_mirrored_topM_01  # a2plus imported part (geometry in sourceFile) (typed FeaturePython)
  Placement = pos=(-1.6e-10,378,484.5) rot=(0,1,0;3.14159rad)
  fixedPosition = true
  sourceFile = <userpath>/CloudStation/Hobbyprojekte/3D Drucker/CoreXY/Assembly/Parts/Printed Parts/motor-block-mirrored-topM.FCStd
  timeLastImport = 1445706114
  updateColors = true
FEATURE [Part::FeaturePython] spacer_6_0mm_01  # a2plus imported part (geometry in sourceFile) (typed FeaturePython)
  Placement = pos=(56.5,403,452.5) rot=(0,0,1;0rad)
  fixedPosition = false
  sourceFile = <userpath>/CloudStation/Hobbyprojekte/3D Drucker/CoreXY/Assembly/Parts/Printed Parts/spacer_6_0mm.FCStd
  timeLastImport = 1445709955
  updateColors = true
FEATURE [Part::FeaturePython] spacer14_7mm_01  # a2plus imported part (geometry in sourceFile) (typed FeaturePython)
  Placement = pos=(383.5,418,452.5) rot=(0,0,1;0rad)
  fixedPosition = false
  sourceFile = <userpath>/CloudStation/Hobbyprojekte/3D Drucker/CoreXY/Assembly/Parts/Printed Parts/spacer14_7mm.FCStd
  timeLastImport = 1445711056
  updateColors = true
FEATURE [App::DocumentObjectGroup] Gruppe012  label="Distancers"
  Group = -> [spacer16mm_import01,spacer16mm_import03,spacer18_3mm_01,spacer14_7mm_01]
FEATURE [Part::FeaturePython] spacer7mm_01  # a2plus imported part (geometry in sourceFile) (typed FeaturePython)
  Placement = pos=(33,413,452.5) rot=(0,0,1;0rad)
  fixedPosition = false
  sourceFile = <userpath>/CloudStation/Hobbyprojekte/3D Drucker/CoreXY/Assembly/Parts/Printed Parts/spacer7mm.FCStd
  timeLastImport = 1444069248
  updateColors = true
FEATURE [Part::FeaturePython] spacer8_7mm_01  # a2plus imported part (geometry in sourceFile) (typed FeaturePython)
  Placement = pos=(56.5,403,470.1) rot=(0,0,1;0rad)
  fixedPosition = false
  sourceFile = <userpath>/CloudStation/Hobbyprojekte/3D Drucker/CoreXY/Assembly/Parts/Printed Parts/spacer8_7mm.FCStd
  timeLastImport = 1445710246
  updateColors = true
FEATURE [Part::FeaturePython] spacer9mm_01  # a2plus imported part (geometry in sourceFile) (typed FeaturePython)
  Placement = pos=(33,413,469.367) rot=(0,0,1;0rad)
  fixedPosition = false
  sourceFile = <userpath>/CloudStation/Hobbyprojekte/3D Drucker/CoreXY/Assembly/Parts/Printed Parts/spacer9mm.FCStd
  timeLastImport = 1444069248
  updateColors = true
FEATURE [Part::FeaturePython] spacer8_7mm_002  # a2plus imported part (geometry in sourceFile) (typed FeaturePython)
  Placement = pos=(38,388,470.1) rot=(0,0,1;0rad)
  fixedPosition = false
  sourceFile = <userpath>/CloudStation/Hobbyprojekte/3D Drucker/CoreXY/Assembly/Parts/Printed Parts/spacer8_7mm.FCStd
  timeLastImport = 1445710246
  updateColors = true
FEATURE [Part::FeaturePython] spacer_6_0mm_002  # a2plus imported part (geometry in sourceFile) (typed FeaturePython)
  Placement = pos=(38,388,452.5) rot=(0,0,1;0rad)
  fixedPosition = false
  sourceFile = <userpath>/CloudStation/Hobbyprojekte/3D Drucker/CoreXY/Assembly/Parts/Printed Parts/spacer_6_0mm.FCStd
  timeLastImport = 1445709955
  updateColors = true
FEATURE [App::DocumentObjectGroup] Gruppe016  label="Distancers001"
  Group = -> [spacer18_3mm_002,spacer8_7mm_01,spacer_6_0mm_01,spacer9mm_01,spacer7mm_01,spacer8_7mm_002,spacer_6_0mm_002]
FEATURE [Part::FeaturePython] XY_block_wide_topM_01002  # a2plus imported part (geometry in sourceFile) (typed FeaturePython)
  Placement = pos=(13,208.705,456.2) rot=(0,0,1;0rad)
  fixedPosition = true
  sourceFile = <userpath>/CloudStation/Hobbyprojekte/3D Drucker/CoreXY/Assembly/Parts/Printed Parts/XY-block wide topM.FCStd
  timeLastImport = 1445713302
  updateColors = true
FEATURE [App::DocumentObjectGroup] Gruppe105  label="Bearings011"
  Group = -> [GT2Bearing_002,F624zz_import017,DIN625_1_624_ZZ_import01021]
FEATURE [Part::FeaturePython] smooth_bar_8x370_01  # a2plus imported part (geometry in sourceFile) (typed FeaturePython)
  Placement = pos=(404,176.205,470.2) rot=(0,-1,0;1.5708rad)
  fixedPosition = false
  sourceFile = <userpath>/CloudStation/Hobbyprojekte/3D Drucker/CoreXY/Assembly/Parts/Bearings/smooth-bar-8x370.FCStd
  timeLastImport = 1444069248
  updateColors = true
FEATURE [Part::FeaturePython] XY_block_top_wide_topM_01  # a2plus imported part (geometry in sourceFile) (typed FeaturePython)
  Placement = pos=(13,208.705,481.2) rot=(1,0,0;3.14159rad)
  fixedPosition = true
  sourceFile = <userpath>/CloudStation/Hobbyprojekte/3D Drucker/CoreXY/Assembly/Parts/Printed Parts/XY-block-top wide topM.FCStd
  timeLastImport = 1445714576
  updateColors = true
FEATURE [App::DocumentObjectGroup] Gruppe066  label="Main Parts008"
  Group = -> [XY_block_wide_topM_01002,XY_block_top_wide_topM_01]
FEATURE [Part::FeaturePython] smooth_bar_8x370_002  # a2plus imported part (geometry in sourceFile) (typed FeaturePython)
  Placement = pos=(404,241.242,470.2) rot=(0,-1,0;1.5708rad)
  fixedPosition = false
  sourceFile = <userpath>/CloudStation/Hobbyprojekte/3D Drucker/CoreXY/Assembly/Parts/Bearings/smooth-bar-8x370.FCStd
  timeLastImport = 1444069248
  updateColors = true
FEATURE [App::DocumentObjectGroup] Gruppe068  label="Smooth Bars002"
  Group = -> [smooth_bar_8x370_01,smooth_bar_8x370_002]
FEATURE [Part::FeaturePython] XY_block_top_wide_topM_002  # a2plus imported part (geometry in sourceFile) (typed FeaturePython)
  Placement = pos=(427,208.742,481.2) rot=(0,1,0;3.14159rad)
  fixedPosition = true
  sourceFile = <userpath>/CloudStation/Hobbyprojekte/3D Drucker/CoreXY/Assembly/Parts/Printed Parts/XY-block-top wide topM.FCStd
  timeLastImport = 1445714576
  updateColors = true
FEATURE [Part::FeaturePython] DIN7965___Schraubeinsatz___M3_import027  # a2plus imported part (geometry in sourceFile) (typed FeaturePython)
  Placement = pos=(399,231.742,462.2) rot=(0,0,1;3.14159rad)
  fixedPosition = false
  sourceFile = <userpath>/CloudStation/Hobbyprojekte/3D Drucker/CoreXY/Assembly/Parts/Screws/DIN7965 - Schraubeinsatz - M3.FCStd
  timeLastImport = 1430763186
  updateColors = true
FEATURE [Part::FeaturePython] DIN7965___Schraubeinsatz___M3_import028  # a2plus imported part (geometry in sourceFile) (typed FeaturePython)
  Placement = pos=(399,249.742,462.2) rot=(0,0,1;3.14159rad)
  fixedPosition = false
  sourceFile = <userpath>/CloudStation/Hobbyprojekte/3D Drucker/CoreXY/Assembly/Parts/Screws/DIN7965 - Schraubeinsatz - M3.FCStd
  timeLastImport = 1430763186
  updateColors = true
FEATURE [Part::FeaturePython] XY_block_wide_topM_01003  # a2plus imported part (geometry in sourceFile) (typed FeaturePython)
  Placement = pos=(427,208.742,456.2) rot=(0,0,1;3.14159rad)
  fixedPosition = true
  sourceFile = <userpath>/CloudStation/Hobbyprojekte/3D Drucker/CoreXY/Assembly/Parts/Printed Parts/XY-block wide topM.FCStd
  timeLastImport = 1445713302
  updateColors = true
FEATURE [App::DocumentObjectGroup] Gruppe078  label="Main Parts010"
  Group = -> [XY_block_wide_topM_01003,XY_block_top_wide_topM_002]
FEATURE [Part::FeaturePython] DIN7965___Schraubeinsatz___M3_import029  # a2plus imported part (geometry in sourceFile) (typed FeaturePython)
  Placement = pos=(399,185.742,462.2) rot=(0,0,1;3.14159rad)
  fixedPosition = false
  sourceFile = <userpath>/CloudStation/Hobbyprojekte/3D Drucker/CoreXY/Assembly/Parts/Screws/DIN7965 - Schraubeinsatz - M3.FCStd
  timeLastImport = 1430763186
  updateColors = true
FEATURE [Part::FeaturePython] DIN7965___Schraubeinsatz___M3_import030  # a2plus imported part (geometry in sourceFile) (typed FeaturePython)
  Placement = pos=(399,167.742,462.2) rot=(0,0,1;3.14159rad)
  fixedPosition = false
  sourceFile = <userpath>/CloudStation/Hobbyprojekte/3D Drucker/CoreXY/Assembly/Parts/Screws/DIN7965 - Schraubeinsatz - M3.FCStd
  timeLastImport = 1430763186
  updateColors = true
FEATURE [Part::FeaturePython] LM8uu_019  # a2plus imported part (geometry in sourceFile) (typed FeaturePython)
  Placement = pos=(427,188.742,470.2) rot=(0,0,1;3.14159rad)
  fixedPosition = false
  sourceFile = <userpath>/CloudStation/Hobbyprojekte/3D Drucker/CoreXY/Assembly/Parts/Bearings/LM8uu.fcstd
  timeLastImport = 1430143348
  updateColors = true
FEATURE [Part::FeaturePython] LM8uu_020  # a2plus imported part (geometry in sourceFile) (typed FeaturePython)
  Placement = pos=(427,228.742,470.2) rot=(0,0,1;3.14159rad)
  fixedPosition = false
  sourceFile = <userpath>/CloudStation/Hobbyprojekte/3D Drucker/CoreXY/Assembly/Parts/Bearings/LM8uu.fcstd
  timeLastImport = 1430143348
  updateColors = true
FEATURE [App::DocumentObjectGroup] Gruppe075  label="Bearings010"
  Group = -> [LM8uu_020,LM8uu_019]
FEATURE [Part::FeaturePython] DIN625_1_624_ZZ_import01026  # a2plus imported part (geometry in sourceFile) (typed FeaturePython)
  Placement = pos=(402,216.3,473.4) rot=(0,0,1;0rad)
  fixedPosition = false
  sourceFile = <userpath>/CloudStation/Hobbyprojekte/3D Drucker/CoreXY/Assembly/Parts/Bearings/DIN625-1_624-ZZ.FCStd
  timeLastImport = 1430517302
  updateColors = true
FEATURE [Part::FeaturePython] GT2Bearing_009  # a2plus imported part (geometry in sourceFile) (typed FeaturePython)
  Placement = pos=(402,201.3,459.19) rot=(0,0,1;3.14159rad)
  fixedPosition = false
  sourceFile = <userpath>/CloudStation/Hobbyprojekte/3D Drucker/CoreXY/Assembly/Parts/Belts/GT2Bearing.FCStd
  timeLastImport = 1444935738
  updateColors = true
FEATURE [Part::FeaturePython] F624zz_import020  # a2plus imported part (geometry in sourceFile) (typed FeaturePython)
  Placement = pos=(402,216.3,468.4) rot=(0,0,1;0rad)
  fixedPosition = false
  sourceFile = <userpath>/CloudStation/Hobbyprojekte/3D Drucker/CoreXY/Assembly/Parts/Bearings/DIN625-1_F624zz.FCStd
  timeLastImport = 1430848638
FEATURE [App::DocumentObjectGroup] Gruppe109  label="Bearings012"
  Group = -> [GT2Bearing_009,F624zz_import020,DIN625_1_624_ZZ_import01026]
FEATURE [Part::FeaturePython] Lead_Screw_8mm_2_0_x_350mm_01  # a2plus imported part (geometry in sourceFile) (typed FeaturePython)
  Placement = pos=(385,42.0001,90) rot=(0,0,1;0rad)
  fixedPosition = false
  sourceFile = <userpath>/CloudStation/Hobbyprojekte/3D Drucker/CoreXY/Assembly/Parts/Bearings/Lead Screw 8mm-2.0 x 350mm.FCStd
  timeLastImport = 1445721650
  updateColors = true
FEATURE [Part::FeaturePython] Lead_Screw_8mm_2_0_x_350mm_002  # a2plus imported part (geometry in sourceFile) (typed FeaturePython)
  Placement = pos=(55,42.0001,90) rot=(0,0,1;0rad)
  fixedPosition = false
  sourceFile = <userpath>/CloudStation/Hobbyprojekte/3D Drucker/CoreXY/Assembly/Parts/Bearings/Lead Screw 8mm-2.0 x 350mm.FCStd
  timeLastImport = 1445721650
  updateColors = true
FEATURE [Part::FeaturePython] Angle_Bracket_import029  label="Angle_Bracket_HRO_003"  # a2plus imported part (geometry in sourceFile) (typed FeaturePython)
  Placement = pos=(368.007,210,100) rot=(0,0,1;3.14159rad)
  fixedPosition = true
  sourceFile = <userpath>/CloudStation/Hobbyprojekte/3D Drucker/CoreXY/Assembly/Parts/Printed Parts/Angle_Bracket.FCStd
  timeLastImport = 1444069248
  updateColors = true
FEATURE [Part::FeaturePython] Angle_Bracket_import030  label="Angle_Bracket_HRU_005"  # a2plus imported part (geometry in sourceFile) (typed FeaturePython)
  Placement = pos=(420,281.993,100) rot=(0,0,1;1.5708rad)
  fixedPosition = true
  sourceFile = <userpath>/CloudStation/Hobbyprojekte/3D Drucker/CoreXY/Assembly/Parts/Printed Parts/Angle_Bracket.FCStd
  timeLastImport = 1444069248
  updateColors = true
FEATURE [Part::FeaturePython] tslot20x20_import026  # a2plus imported part (geometry in sourceFile) (typed FeaturePython)
  Placement = pos=(420,230,120) rot=(0.57735,-0.57735,-0.57735;2.0944rad)
  fixedPosition = true
  sourceFile = <userpath>/CloudStation/Hobbyprojekte/3D Drucker/CoreXY/Assembly/Parts/Alu Extrusion/tslot20x20x400.FCStd
  timeLastImport = 1444069248
  updateColors = true
FEATURE [Part::FeaturePython] Angle_Bracket_import031  label="Angle_Bracket_HLO_003"  # a2plus imported part (geometry in sourceFile) (typed FeaturePython)
  Placement = pos=(71.9933,210,120) rot=(1,0,0;3.14159rad)
  fixedPosition = true
  sourceFile = <userpath>/CloudStation/Hobbyprojekte/3D Drucker/CoreXY/Assembly/Parts/Printed Parts/Angle_Bracket.FCStd
  timeLastImport = 1444069248
  updateColors = true
FEATURE [Part::FeaturePython] Angle_Bracket_import032  label="Angle_Bracket_VHU_005"  # a2plus imported part (geometry in sourceFile) (typed FeaturePython)
  Placement = pos=(71.9933,230,100) rot=(0,0,1;0rad)
  fixedPosition = true
  sourceFile = <userpath>/CloudStation/Hobbyprojekte/3D Drucker/CoreXY/Assembly/Parts/Printed Parts/Angle_Bracket.FCStd
  timeLastImport = 1444069248
  updateColors = true
FEATURE [Part::FeaturePython] Hammermutter_B_Typ_Nut6_M4_import01082  # a2plus imported part (geometry in sourceFile) (typed FeaturePython)
  Placement = pos=(33.9988,215,110) rot=(0.57735,-0.57735,0.57735;2.0944rad)
  fixedPosition = false
  sourceFile = <userpath>/CloudStation/Hobbyprojekte/3D Drucker/CoreXY/Assembly/Parts/Screws/Hammermutter B-Typ Nut6 M4.FCStd
  timeLastImport = 1430523528
  updateColors = true
FEATURE [Part::FeaturePython] Hammermutter_B_Typ_Nut6_M4_import01083  # a2plus imported part (geometry in sourceFile) (typed FeaturePython)
  Placement = pos=(15,196,110) rot=(0.707107,0,0.707107;3.14159rad)
  fixedPosition = false
  sourceFile = <userpath>/CloudStation/Hobbyprojekte/3D Drucker/CoreXY/Assembly/Parts/Screws/Hammermutter B-Typ Nut6 M4.FCStd
  timeLastImport = 1430523528
  updateColors = true
FEATURE [Part::FeaturePython] Hammermutter_B_Typ_Nut6_M4_import01084  # a2plus imported part (geometry in sourceFile) (typed FeaturePython)
  Placement = pos=(33.9988,225,110) rot=(0.57735,0.57735,0.57735;4.18879rad)
  fixedPosition = false
  sourceFile = <userpath>/CloudStation/Hobbyprojekte/3D Drucker/CoreXY/Assembly/Parts/Screws/Hammermutter B-Typ Nut6 M4.FCStd
  timeLastImport = 1430523528
  updateColors = true
FEATURE [Part::FeaturePython] Hammermutter_B_Typ_Nut6_M4_import01085  # a2plus imported part (geometry in sourceFile) (typed FeaturePython)
  Placement = pos=(15,243.999,110) rot=(0.707107,0,0.707107;3.14159rad)
  fixedPosition = false
  sourceFile = <userpath>/CloudStation/Hobbyprojekte/3D Drucker/CoreXY/Assembly/Parts/Screws/Hammermutter B-Typ Nut6 M4.FCStd
  timeLastImport = 1430523528
  updateColors = true
FEATURE [Part::FeaturePython] Hammermutter_B_Typ_Nut6_M4_import01086  # a2plus imported part (geometry in sourceFile) (typed FeaturePython)
  Placement = pos=(425,196,110) rot=(0.707107,0,-0.707107;3.14159rad)
  fixedPosition = false
  sourceFile = <userpath>/CloudStation/Hobbyprojekte/3D Drucker/CoreXY/Assembly/Parts/Screws/Hammermutter B-Typ Nut6 M4.FCStd
  timeLastImport = 1430523528
  updateColors = true
FEATURE [Part::FeaturePython] Hammermutter_B_Typ_Nut6_M4_import01087  # a2plus imported part (geometry in sourceFile) (typed FeaturePython)
  Placement = pos=(406.001,215,110) rot=(0.57735,-0.57735,0.57735;2.0944rad)
  fixedPosition = false
  sourceFile = <userpath>/CloudStation/Hobbyprojekte/3D Drucker/CoreXY/Assembly/Parts/Screws/Hammermutter B-Typ Nut6 M4.FCStd
  timeLastImport = 1430523528
  updateColors = true
FEATURE [Part::FeaturePython] Hammermutter_B_Typ_Nut6_M4_import01088  # a2plus imported part (geometry in sourceFile) (typed FeaturePython)
  Placement = pos=(406,225,110) rot=(0.57735,0.57735,0.57735;4.18879rad)
  fixedPosition = false
  sourceFile = <userpath>/CloudStation/Hobbyprojekte/3D Drucker/CoreXY/Assembly/Parts/Screws/Hammermutter B-Typ Nut6 M4.FCStd
  timeLastImport = 1430523528
  updateColors = true
FEATURE [Part::FeaturePython] Hammermutter_B_Typ_Nut6_M4_import01089  # a2plus imported part (geometry in sourceFile) (typed FeaturePython)
  Placement = pos=(425,243.999,110) rot=(0.707107,0,-0.707107;3.14159rad)
  fixedPosition = false
  sourceFile = <userpath>/CloudStation/Hobbyprojekte/3D Drucker/CoreXY/Assembly/Parts/Screws/Hammermutter B-Typ Nut6 M4.FCStd
  timeLastImport = 1430523528
  updateColors = true
FEATURE [App::DocumentObjectGroup] Gruppe112  label="z-Axis-Mounting"
  Group = -> [tslot20x20_import026]
FEATURE [App::DocumentObjectGroup] Gruppe114  label="z-Axis-Mounting002"
  Group = -> [Angle_Bracket_import029,Angle_Bracket_import030,Angle_Bracket_import031,Angle_Bracket_import032]
FEATURE [Part::FeaturePython] smooth_bar_12x360_01  # a2plus imported part (geometry in sourceFile) (typed FeaturePython)
  Placement = pos=(405,65,89.5) rot=(0,0,1;0rad)
  fixedPosition = false
  sourceFile = <userpath>/CloudStation/Hobbyprojekte/3D Drucker/CoreXY/Assembly/Parts/Bearings/smooth-bar-12x360.FCStd
  timeLastImport = 1445722460
  updateColors = true
FEATURE [Part::FeaturePython] smooth_bar_12x360_002  # a2plus imported part (geometry in sourceFile) (typed FeaturePython)
  Placement = pos=(35,65,89.5) rot=(0,0,1;0rad)
  fixedPosition = false
  sourceFile = <userpath>/CloudStation/Hobbyprojekte/3D Drucker/CoreXY/Assembly/Parts/Bearings/smooth-bar-12x360.FCStd
  timeLastImport = 1445722460
  updateColors = true
FEATURE [Part::FeaturePython] _mm_flanged_lead_screw_nut_with_2mm_thread_01  # a2plus imported part (geometry in sourceFile) (typed FeaturePython)
  Placement = pos=(55,42,224.228) rot=(0,0,1;0rad)
  fixedPosition = false
  sourceFile = <userpath>/CloudStation/Hobbyprojekte/3D Drucker/CoreXY/Assembly/Parts/Bearings/8mm flanged lead screw nut with 2mm thread.FCStd
  timeLastImport = 1432176046
  updateColors = true
FEATURE [Part::FeaturePython] _mm_flanged_lead_screw_nut_with_2mm_thread_002  # a2plus imported part (geometry in sourceFile) (typed FeaturePython)
  Placement = pos=(385,42,224.228) rot=(0,0,1;0rad)
  fixedPosition = false
  sourceFile = <userpath>/CloudStation/Hobbyprojekte/3D Drucker/CoreXY/Assembly/Parts/Bearings/8mm flanged lead screw nut with 2mm thread.FCStd
  timeLastImport = 1432176046
  updateColors = true
FEATURE [Part::FeaturePython] NEMA_17_Stepper_Motor_40mm_with_connector_import003  # a2plus imported part (geometry in sourceFile) (typed FeaturePython)
  Placement = pos=(273.57,396,145.1) rot=(0,1,0;3.14159rad)
  fixedPosition = true
  sourceFile = <userpath>/CloudStation/Hobbyprojekte/3D Drucker/CoreXY/Assembly/Parts/3D Printer Components/NEMA-17_Stepper_Motor_40mm_with_connector.fcstd
  timeLastImport = 1444068474
  updateColors = true
FEATURE [Part::FeaturePython] smooth_bar_12x360_003  # a2plus imported part (geometry in sourceFile) (typed FeaturePython)
  Placement = pos=(184.82,403,89.5) rot=(0,0,1;0rad)
  fixedPosition = false
  sourceFile = <userpath>/CloudStation/Hobbyprojekte/3D Drucker/CoreXY/Assembly/Parts/Bearings/smooth-bar-12x360.FCStd
  timeLastImport = 1445722460
  updateColors = true
FEATURE [Part::FeaturePython] Hammermutter_B_Typ_Nut6_M4_import01090  # a2plus imported part (geometry in sourceFile) (typed FeaturePython)
  Placement = pos=(174.82,425,110) rot=(0.57735,0.57735,-0.57735;2.0944rad)
  fixedPosition = false
  sourceFile = <userpath>/CloudStation/Hobbyprojekte/3D Drucker/CoreXY/Assembly/Parts/Screws/Hammermutter B-Typ Nut6 M4.FCStd
  timeLastImport = 1430523528
  updateColors = true
FEATURE [Part::FeaturePython] Lead_Screw_8mm_2_0_x_350mm_003  # a2plus imported part (geometry in sourceFile) (typed FeaturePython)
  Placement = pos=(219.82,398,90) rot=(0,0,1;0rad)
  fixedPosition = false
  sourceFile = <userpath>/CloudStation/Hobbyprojekte/3D Drucker/CoreXY/Assembly/Parts/Bearings/Lead Screw 8mm-2.0 x 350mm.FCStd
  timeLastImport = 1445721650
  updateColors = true
FEATURE [Part::FeaturePython] _mm_flanged_lead_screw_nut_with_2mm_thread_003  # a2plus imported part (geometry in sourceFile) (typed FeaturePython)
  Placement = pos=(219.82,398,224.228) rot=(0,0,1;0rad)
  fixedPosition = false
  sourceFile = <userpath>/CloudStation/Hobbyprojekte/3D Drucker/CoreXY/Assembly/Parts/Bearings/8mm flanged lead screw nut with 2mm thread.FCStd
  timeLastImport = 1432176046
  updateColors = true
FEATURE [Part::Feature] BOLTS_part005  label="Radial Ball Bearing DIN625-1 608-2RS004"
  Placement = pos=(219.82,398,120) rot=(0.707107,0.707107,0;3.14159rad)
  shape: bbox 23.81 x 23.81 x 7 mm, 20 faces, 3 solids (baked)
FEATURE [Part::Feature] BOLTS_part006  label="Radial Ball Bearing DIN625-1 608-2RS005"
  Placement = pos=(219.82,398,107) rot=(0.707107,0.707107,0;3.14159rad)
  shape: bbox 23.81 x 23.81 x 7 mm, 20 faces, 3 solids (baked)
FEATURE [Part::FeaturePython] Z_axis_clamp_2_01002  # a2plus imported part (geometry in sourceFile) (typed FeaturePython)
  Placement = pos=(184.82,403,429.5) rot=(0,0,1;0rad)
  fixedPosition = false
  sourceFile = <userpath>/CloudStation/Hobbyprojekte/3D Drucker/CoreXY/Assembly/Parts/Printed Parts/Z-axis-clamp-2.FCStd
  timeLastImport = 1445301196
  updateColors = true
FEATURE [Part::FeaturePython] Z_axis_clamp_1_01002  # a2plus imported part (geometry in sourceFile) (typed FeaturePython)
  Placement = pos=(184.82,403,429.5) rot=(0,0,1;0rad)
  fixedPosition = false
  sourceFile = <userpath>/CloudStation/Hobbyprojekte/3D Drucker/CoreXY/Assembly/Parts/Printed Parts/Z-axis-clamp-1.FCStd
  timeLastImport = 1445300847
  updateColors = true
FEATURE [Part::FeaturePython] Hammermutter_B_Typ_Nut6_M4_import01091  # a2plus imported part (geometry in sourceFile) (typed FeaturePython)
  Placement = pos=(173.82,425,439.5) rot=(0.57735,0.57735,-0.57735;2.0944rad)
  fixedPosition = false
  sourceFile = <userpath>/CloudStation/Hobbyprojekte/3D Drucker/CoreXY/Assembly/Parts/Screws/Hammermutter B-Typ Nut6 M4.FCStd
  timeLastImport = 1430523528
  updateColors = true
FEATURE [Part::FeaturePython] Hammermutter_B_Typ_Nut6_M4_import01092  # a2plus imported part (geometry in sourceFile) (typed FeaturePython)
  Placement = pos=(195.82,425,439.5) rot=(0.57735,0.57735,-0.57735;2.0944rad)
  fixedPosition = false
  sourceFile = <userpath>/CloudStation/Hobbyprojekte/3D Drucker/CoreXY/Assembly/Parts/Screws/Hammermutter B-Typ Nut6 M4.FCStd
  timeLastImport = 1430523528
  updateColors = true
FEATURE [Part::FeaturePython] Z_axis_clamp_2_01003  # a2plus imported part (geometry in sourceFile) (typed FeaturePython)
  Placement = pos=(35,65,429.5) rot=(0,0,1;1.5708rad)
  fixedPosition = false
  sourceFile = <userpath>/CloudStation/Hobbyprojekte/3D Drucker/CoreXY/Assembly/Parts/Printed Parts/Z-axis-clamp-2.FCStd
  timeLastImport = 1445301196
  updateColors = true
FEATURE [Part::FeaturePython] Hammermutter_B_Typ_Nut6_M4_import01093  # a2plus imported part (geometry in sourceFile) (typed FeaturePython)
  Placement = pos=(241.57,425,110) rot=(0.57735,0.57735,-0.57735;2.0944rad)
  fixedPosition = false
  sourceFile = <userpath>/CloudStation/Hobbyprojekte/3D Drucker/CoreXY/Assembly/Parts/Screws/Hammermutter B-Typ Nut6 M4.FCStd
  timeLastImport = 1430523528
  updateColors = true
FEATURE [Part::FeaturePython] Hammermutter_B_Typ_Nut6_M4_import01094  # a2plus imported part (geometry in sourceFile) (typed FeaturePython)
  Placement = pos=(306.82,425,110) rot=(0.57735,0.57735,-0.57735;2.0944rad)
  fixedPosition = false
  sourceFile = <userpath>/CloudStation/Hobbyprojekte/3D Drucker/CoreXY/Assembly/Parts/Screws/Hammermutter B-Typ Nut6 M4.FCStd
  timeLastImport = 1430523528
  updateColors = true
FEATURE [Part::FeaturePython] GT2Pulley_003  # a2plus imported part (geometry in sourceFile) (typed FeaturePython)
  Placement = pos=(273.57,396,95) rot=(1,0,0;3.14159rad)
  fixedPosition = true
  sourceFile = <userpath>/CloudStation/Hobbyprojekte/3D Drucker/CoreXY/Assembly/Parts/Belts/GT2Pulley.fcstd
  timeLastImport = 1444675797
  updateColors = true
FEATURE [Part::FeaturePython] GT28mmPulley_01  # a2plus imported part (geometry in sourceFile) (typed FeaturePython)
  Placement = pos=(219.82,398,95) rot=(0,1,0;3.14159rad)
  fixedPosition = false
  sourceFile = <userpath>/CloudStation/Hobbyprojekte/3D Drucker/CoreXY/Assembly/Parts/Belts/GT28mmPulley.FCStd
  timeLastImport = 1445734545
  updateColors = true
FEATURE [Part::FeaturePython] GT28mmPulley_002  # a2plus imported part (geometry in sourceFile) (typed FeaturePython)
  Placement = pos=(385,42,95) rot=(0,1,0;3.14159rad)
  fixedPosition = false
  sourceFile = <userpath>/CloudStation/Hobbyprojekte/3D Drucker/CoreXY/Assembly/Parts/Belts/GT28mmPulley.FCStd
  timeLastImport = 1445734545
  updateColors = true
FEATURE [Part::FeaturePython] GT28mmPulley_003  # a2plus imported part (geometry in sourceFile) (typed FeaturePython)
  Placement = pos=(55,42,95) rot=(0,1,0;3.14159rad)
  fixedPosition = false
  sourceFile = <userpath>/CloudStation/Hobbyprojekte/3D Drucker/CoreXY/Assembly/Parts/Belts/GT28mmPulley.FCStd
  timeLastImport = 1445734545
  updateColors = true
FEATURE [Part::FeaturePython] Hammermutter_B_Typ_Nut6_M4_import01095  # a2plus imported part (geometry in sourceFile) (typed FeaturePython)
  Placement = pos=(220.35,220.05,105) rot=(0.707107,0.707107,0;3.14159rad)
  fixedPosition = true
  sourceFile = <userpath>/CloudStation/Hobbyprojekte/3D Drucker/CoreXY/Assembly/Parts/Screws/Hammermutter B-Typ Nut6 M4.FCStd
  timeLastImport = 1430523528
  updateColors = true
FEATURE [Part::FeaturePython] Hammermutter_B_Typ_Nut6_M4_import01096  # a2plus imported part (geometry in sourceFile) (typed FeaturePython)
  Placement = pos=(286.35,220.05,105) rot=(0.707107,0.707107,0;3.14159rad)
  fixedPosition = true
  sourceFile = <userpath>/CloudStation/Hobbyprojekte/3D Drucker/CoreXY/Assembly/Parts/Screws/Hammermutter B-Typ Nut6 M4.FCStd
  timeLastImport = 1430523528
  updateColors = true
FEATURE [Part::FeaturePython] DIN7965___Schraubeinsatz___M3_import031  # a2plus imported part (geometry in sourceFile) (typed FeaturePython)
  Placement = pos=(387,181.8,462.2) rot=(0,0,1;0rad)
  fixedPosition = false
  sourceFile = <userpath>/CloudStation/Hobbyprojekte/3D Drucker/CoreXY/Assembly/Parts/Screws/DIN7965 - Schraubeinsatz - M3.FCStd
  timeLastImport = 1430763186
  updateColors = true
FEATURE [Part::FeaturePython] DIN7965___Schraubeinsatz___M3_import032  # a2plus imported part (geometry in sourceFile) (typed FeaturePython)
  Placement = pos=(387,221.8,462.2) rot=(0,0,1;0rad)
  fixedPosition = false
  sourceFile = <userpath>/CloudStation/Hobbyprojekte/3D Drucker/CoreXY/Assembly/Parts/Screws/DIN7965 - Schraubeinsatz - M3.FCStd
  timeLastImport = 1430763186
  updateColors = true
FEATURE [Part::FeaturePython] DIN7965___Schraubeinsatz___M3_import033  # a2plus imported part (geometry in sourceFile) (typed FeaturePython)
  Placement = pos=(387,235.8,462.2) rot=(0,0,1;0rad)
  fixedPosition = false
  sourceFile = <userpath>/CloudStation/Hobbyprojekte/3D Drucker/CoreXY/Assembly/Parts/Screws/DIN7965 - Schraubeinsatz - M3.FCStd
  timeLastImport = 1430763186
  updateColors = true
FEATURE [Part::FeaturePython] DIN7965___Schraubeinsatz___M3_import034  # a2plus imported part (geometry in sourceFile) (typed FeaturePython)
  Placement = pos=(387,195.8,462.2) rot=(0,0,1;0rad)
  fixedPosition = false
  sourceFile = <userpath>/CloudStation/Hobbyprojekte/3D Drucker/CoreXY/Assembly/Parts/Screws/DIN7965 - Schraubeinsatz - M3.FCStd
  timeLastImport = 1430763186
  updateColors = true
FEATURE [Part::FeaturePython] XY_block_top_topM_003  # a2plus imported part (geometry in sourceFile) (typed FeaturePython)
  Placement = pos=(427,208.8,481.2) rot=(0,1,0;3.14159rad)
  fixedPosition = false
  sourceFile = <userpath>/CloudStation/Hobbyprojekte/3D Drucker/CoreXY/Assembly/Parts/Printed Parts/XY-block-top topM.FCStd
  timeLastImport = 1445594597
  updateColors = true
FEATURE [Part::FeaturePython] LM8uu_021  # a2plus imported part (geometry in sourceFile) (typed FeaturePython)
  Placement = pos=(427,195.3,470.2) rot=(0,0,1;0rad)
  fixedPosition = false
  sourceFile = <userpath>/CloudStation/Hobbyprojekte/3D Drucker/CoreXY/Assembly/Parts/Bearings/LM8uu.fcstd
  timeLastImport = 1430143348
  updateColors = true
FEATURE [Part::FeaturePython] LM8uu_022  # a2plus imported part (geometry in sourceFile) (typed FeaturePython)
  Placement = pos=(427,222.3,470.2) rot=(0,0,1;0rad)
  fixedPosition = false
  sourceFile = <userpath>/CloudStation/Hobbyprojekte/3D Drucker/CoreXY/Assembly/Parts/Bearings/LM8uu.fcstd
  timeLastImport = 1430143348
  updateColors = true
FEATURE [App::DocumentObjectGroup] Gruppe036  label="Bearings005"
  Group = -> [LM8uu_022,LM8uu_021]
FEATURE [Part::FeaturePython] XY_block_topM_01002  label="XY_block_topM_002"  # a2plus imported part (geometry in sourceFile) (typed FeaturePython)
  Placement = pos=(427,208.8,456.2) rot=(0,0,1;3.14159rad)
  fixedPosition = true
  sourceFile = <userpath>/CloudStation/Hobbyprojekte/3D Drucker/CoreXY/Assembly/Parts/Printed Parts/XY-block topM.FCStd
  timeLastImport = 1445693115
  updateColors = true
FEATURE [App::DocumentObjectGroup] Gruppe039  label="Main Parts005"
  Group = -> [XY_block_top_topM_003,XY_block_topM_01002]
FEATURE [Part::FeaturePython] GT2_Belt_Z_01  # a2plus imported part (geometry in sourceFile) (typed FeaturePython)
  Placement = pos=(0,395,87.6) rot=(0,0,1;0rad)
  fixedPosition = false
  sourceFile = <userpath>/CloudStation/Hobbyprojekte/3D Drucker/CoreXY/Assembly/Parts/Belts/GT2-Belt_Z.FCStd
  timeLastImport = 1445808796
  updateColors = true
FEATURE [App::DocumentObjectGroup] Gruppe118  label="Other"
  Group = -> [GT28mmPulley_003,GT28mmPulley_01,GT2Pulley_003,GT28mmPulley_002,NEMA_17_Stepper_Motor_40mm_with_connector_import003,GT2_Belt_Z_01]
FEATURE [Part::FeaturePython] DIN625_1_624_ZZ_import01027  # a2plus imported part (geometry in sourceFile) (typed FeaturePython)
  Placement = pos=(220.35,220.05,85.8) rot=(0,0,1;0rad)
  fixedPosition = false
  sourceFile = <userpath>/CloudStation/Hobbyprojekte/3D Drucker/CoreXY/Assembly/Parts/Bearings/DIN625-1_624-ZZ.FCStd
  timeLastImport = 1430517302
  updateColors = true
FEATURE [Part::FeaturePython] F624zz_import021  # a2plus imported part (geometry in sourceFile) (typed FeaturePython)
  Placement = pos=(220.35,220.05,80.8) rot=(0,0,1;0rad)
  fixedPosition = false
  sourceFile = <userpath>/CloudStation/Hobbyprojekte/3D Drucker/CoreXY/Assembly/Parts/Bearings/DIN625-1_F624zz.FCStd
  timeLastImport = 1430848638
FEATURE [Part::FeaturePython] DIN625_1_624_ZZ_import01028  # a2plus imported part (geometry in sourceFile) (typed FeaturePython)
  Placement = pos=(286.35,220.05,85.8) rot=(0,0,1;0rad)
  fixedPosition = false
  sourceFile = <userpath>/CloudStation/Hobbyprojekte/3D Drucker/CoreXY/Assembly/Parts/Bearings/DIN625-1_624-ZZ.FCStd
  timeLastImport = 1430517302
  updateColors = true
FEATURE [Part::FeaturePython] F624zz_import022  # a2plus imported part (geometry in sourceFile) (typed FeaturePython)
  Placement = pos=(286.35,220.05,80.8) rot=(0,0,1;0rad)
  fixedPosition = false
  sourceFile = <userpath>/CloudStation/Hobbyprojekte/3D Drucker/CoreXY/Assembly/Parts/Bearings/DIN625-1_F624zz.FCStd
  timeLastImport = 1430848638
FEATURE [App::DocumentObjectGroup] Gruppe115  label="Bearings013"
  Group = -> [Lead_Screw_8mm_2_0_x_350mm_002,_mm_flanged_lead_screw_nut_with_2mm_thread_01,Lead_Screw_8mm_2_0_x_350mm_01,_mm_flanged_lead_screw_nut_with_2mm_thread_002,smooth_bar_12x360_002,smooth_bar_12x360_01,smooth_bar_12x360_003,Lead_Screw_8mm_2_0_x_350mm_003,_mm_flanged_lead_screw_nut_with_2mm_thread_003,BOLTS_part005,BOLTS_part006,BOLTS_part002,BOLTS_part001,BOLTS_part003,BOLTS_part004,+4 more]
FEATURE [Part::FeaturePython] Z_leadscrew_back_bearing_block_01  # a2plus imported part (geometry in sourceFile) (typed FeaturePython)
  Placement = pos=(219.82,398,100) rot=(0,0,1;0rad)
  fixedPosition = true
  sourceFile = <userpath>/CloudStation/Hobbyprojekte/3D Drucker/CoreXY/Assembly/Parts/Printed Parts/Z-leadscrew-back-bearing-block.FCStd
  timeLastImport = 1445811023
  updateColors = true
FEATURE [Part::FeaturePython] LM8uu_023  # a2plus imported part (geometry in sourceFile) (typed FeaturePython)
  Placement = pos=(427,220.8,470.2) rot=(0,0,1;0rad)
  fixedPosition = false
  sourceFile = <userpath>/CloudStation/Hobbyprojekte/3D Drucker/CoreXY/Assembly/Parts/Bearings/LM8uu.fcstd
  timeLastImport = 1430143348
  updateColors = true
FEATURE [Part::FeaturePython] LM8uu_024  # a2plus imported part (geometry in sourceFile) (typed FeaturePython)
  Placement = pos=(427,196.8,470.2) rot=(0,0,1;0rad)
  fixedPosition = true
  sourceFile = <userpath>/CloudStation/Hobbyprojekte/3D Drucker/CoreXY/Assembly/Parts/Bearings/LM8uu.fcstd
  timeLastImport = 1430143348
  updateColors = true
FEATURE [Part::FeaturePython] spacer9mm_import011  # a2plus imported part (geometry in sourceFile) (typed FeaturePython)
  Placement = pos=(38,216.3,479.2) rot=(0,1,0;3.14159rad)
  fixedPosition = false
  sourceFile = <userpath>/CloudStation/Hobbyprojekte/3D Drucker/CoreXY/Assembly/Parts/Printed Parts/spacer9mm.FCStd
  timeLastImport = 1444069248
  updateColors = true
FEATURE [Part::FeaturePython] spacer10_2mm_002  # a2plus imported part (geometry in sourceFile) (typed FeaturePython)
  Placement = pos=(402,201.3,469) rot=(0,0,1;0rad)
  fixedPosition = false
  sourceFile = <userpath>/CloudStation/Hobbyprojekte/3D Drucker/CoreXY/Assembly/Parts/Printed Parts/spacer10_2mm.FCStd
  timeLastImport = 1448490812
  updateColors = true
FEATURE [Part::FeaturePython] spacer9mm_import012  # a2plus imported part (geometry in sourceFile) (typed FeaturePython)
  Placement = pos=(402,216.3,467.6) rot=(0,1,0;3.14159rad)
  fixedPosition = true
  sourceFile = <userpath>/CloudStation/Hobbyprojekte/3D Drucker/CoreXY/Assembly/Parts/Printed Parts/spacer9mm.FCStd
  timeLastImport = 1444069248
  updateColors = true
FEATURE [App::DocumentObjectGroup] Gruppe111  label="Distancers009"
  Group = -> [spacer10_2mm_002,spacer9mm_import012]
FEATURE [Part::FeaturePython] spacer10_2mm_003  # a2plus imported part (geometry in sourceFile) (typed FeaturePython)
  Placement = pos=(38,201.3,458.2) rot=(0,0,1;0rad)
  fixedPosition = false
  sourceFile = <userpath>/CloudStation/Hobbyprojekte/3D Drucker/CoreXY/Assembly/Parts/Printed Parts/spacer10_2mm.FCStd
  timeLastImport = 1448490812
  updateColors = true
FEATURE [App::DocumentObjectGroup] Gruppe107  label="Distancers008"
  Group = -> [spacer9mm_import011,spacer10_2mm_003]
FEATURE [Part::FeaturePython] MK3_300x300_01  # a2plus imported part (geometry in sourceFile) (typed FeaturePython)
  Placement = pos=(62.5,50.7697,393.014) rot=(0,0,-1;1.5708rad)
  fixedPosition = false
  sourceFile = <userpath>/CloudStation/Hobbyprojekte/3D Drucker/CoreXY/Assembly/Parts/Electronics/MK3-300x300.FCStd
  timeLastImport = 1448566582
  updateColors = true
FEATURE [App::DocumentObjectGroup] Gruppe097  label="Heatbed"
  Group = -> [MK2_Heatbed_Mockup_215x215_01,MK3_300x300_01]
FEATURE [Part::FeaturePython] Toranado_Assembly_01  # a2plus imported part (geometry in sourceFile) (typed FeaturePython)
  Placement = pos=(203.815,146.4,499.2) rot=(0.579113,0.576467,0.576467;2.0944rad)
  fixedPosition = false
  sourceFile = <userpath>/CloudStation/Hobbyprojekte/3D Drucker/CoreXY/Assembly/Parts/Extruder/Toranado_Assembly.FCStd
  timeLastImport = 1458407076
  updateColors = true
FEATURE [Part::FeaturePython] F624zz_import023  # a2plus imported part (geometry in sourceFile) (typed FeaturePython)
  Placement = pos=(402.3,215.9,469.45) rot=(0,0,1;0rad)
  fixedPosition = false
  sourceFile = <userpath>/CloudStation/Hobbyprojekte/3D Drucker/CoreXY/Assembly/Parts/Bearings/DIN625-1_F624zz.FCStd
  timeLastImport = 1430848638
FEATURE [Part::FeaturePython] DIN625_1_624_ZZ_import01029  # a2plus imported part (geometry in sourceFile) (typed FeaturePython)
  Placement = pos=(402.3,215.9,474.45) rot=(0,0,1;0rad)
  fixedPosition = false
  sourceFile = <userpath>/CloudStation/Hobbyprojekte/3D Drucker/CoreXY/Assembly/Parts/Bearings/DIN625-1_624-ZZ.FCStd
  timeLastImport = 1430517302
  updateColors = true
FEATURE [Part::FeaturePython] GT2Bearing_010  # a2plus imported part (geometry in sourceFile) (typed FeaturePython)
  Placement = pos=(402.3,201.5,460.49) rot=(0,0,1;3.14159rad)
  fixedPosition = false
  sourceFile = <userpath>/CloudStation/Hobbyprojekte/3D Drucker/CoreXY/Assembly/Parts/Belts/GT2Bearing.FCStd
  timeLastImport = 1444935738
  updateColors = true
FEATURE [App::DocumentObjectGroup] Gruppe122  label="Bearings014"
  Group = -> [F624zz_import023,DIN625_1_624_ZZ_import01029,GT2Bearing_010]
FEATURE [Part::FeaturePython] CustomBushingXYBlock_LM8UU_01  # a2plus imported part (geometry in sourceFile) (typed FeaturePython)
  Placement = pos=(437,176,470.2) rot=(0,0,1;1.5708rad)
  fixedPosition = true
  sourceFile = <userpath>/CloudStation/Hobbyprojekte/3D Drucker/CoreXY/Assembly/Parts/Printed Parts/CustomBushingXYBlock_LM8UU.FCStd
  timeLastImport = 1458171204
  updateColors = true
FEATURE [Part::FeaturePython] CustomBushingXYBlock_LM8UU_002  # a2plus imported part (geometry in sourceFile) (typed FeaturePython)
  Placement = pos=(437,241.4,470.2) rot=(-0.707107,0.707107,0;3.14159rad)
  fixedPosition = false
  sourceFile = <userpath>/CloudStation/Hobbyprojekte/3D Drucker/CoreXY/Assembly/Parts/Printed Parts/CustomBushingXYBlock_LM8UU.FCStd
  timeLastImport = 1458171204
  updateColors = true
FEATURE [Part::FeaturePython] Hammermutter_B_Typ_Nut6_M4_import01097  # a2plus imported part (geometry in sourceFile) (typed FeaturePython)
  Placement = pos=(10,425,86.0002) rot=(1,0,0;1.5708rad)
  fixedPosition = false
  sourceFile = <userpath>/CloudStation/Hobbyprojekte/3D Drucker/CoreXY/Assembly/Parts/Screws/Hammermutter B-Typ Nut6 M4.FCStd
  timeLastImport = 1430523528
  updateColors = true
FEATURE [Part::FeaturePython] Hammermutter_B_Typ_Nut6_M4_import01098  # a2plus imported part (geometry in sourceFile) (typed FeaturePython)
  Placement = pos=(10,15,86.0002) rot=(-1,0,0;1.5708rad)
  fixedPosition = false
  sourceFile = <userpath>/CloudStation/Hobbyprojekte/3D Drucker/CoreXY/Assembly/Parts/Screws/Hammermutter B-Typ Nut6 M4.FCStd
  timeLastImport = 1430523528
  updateColors = true
FEATURE [Part::FeaturePython] Hammermutter_B_Typ_Nut6_M4_import01099  # a2plus imported part (geometry in sourceFile) (typed FeaturePython)
  Placement = pos=(10,33.9988,105) rot=(1,0,0;3.14159rad)
  fixedPosition = false
  sourceFile = <userpath>/CloudStation/Hobbyprojekte/3D Drucker/CoreXY/Assembly/Parts/Screws/Hammermutter B-Typ Nut6 M4.FCStd
  timeLastImport = 1430523528
  updateColors = true
FEATURE [Part::FeaturePython] Hammermutter_B_Typ_Nut6_M4_import01100  # a2plus imported part (geometry in sourceFile) (typed FeaturePython)
  Placement = pos=(10,406.001,105) rot=(1,0,0;3.14159rad)
  fixedPosition = false
  sourceFile = <userpath>/CloudStation/Hobbyprojekte/3D Drucker/CoreXY/Assembly/Parts/Screws/Hammermutter B-Typ Nut6 M4.FCStd
  timeLastImport = 1430523528
  updateColors = true
FEATURE [Part::FeaturePython] Hammermutter_B_Typ_Nut6_M4_import01101  # a2plus imported part (geometry in sourceFile) (typed FeaturePython)
  Placement = pos=(430,15,86.0002) rot=(-1,0,0;1.5708rad)
  fixedPosition = false
  sourceFile = <userpath>/CloudStation/Hobbyprojekte/3D Drucker/CoreXY/Assembly/Parts/Screws/Hammermutter B-Typ Nut6 M4.FCStd
  timeLastImport = 1430523528
  updateColors = true
FEATURE [Part::FeaturePython] Hammermutter_B_Typ_Nut6_M4_import01102  # a2plus imported part (geometry in sourceFile) (typed FeaturePython)
  Placement = pos=(430,33.9988,105) rot=(1,0,0;3.14159rad)
  fixedPosition = false
  sourceFile = <userpath>/CloudStation/Hobbyprojekte/3D Drucker/CoreXY/Assembly/Parts/Screws/Hammermutter B-Typ Nut6 M4.FCStd
  timeLastImport = 1430523528
  updateColors = true
FEATURE [Part::FeaturePython] Hammermutter_B_Typ_Nut6_M4_import01103  # a2plus imported part (geometry in sourceFile) (typed FeaturePython)
  Placement = pos=(430,425,86.0002) rot=(1,0,0;1.5708rad)
  fixedPosition = false
  sourceFile = <userpath>/CloudStation/Hobbyprojekte/3D Drucker/CoreXY/Assembly/Parts/Screws/Hammermutter B-Typ Nut6 M4.FCStd
  timeLastImport = 1430523528
  updateColors = true
FEATURE [Part::FeaturePython] Hammermutter_B_Typ_Nut6_M4_import01104  # a2plus imported part (geometry in sourceFile) (typed FeaturePython)
  Placement = pos=(430,406.001,105) rot=(1,0,0;3.14159rad)
  fixedPosition = false
  sourceFile = <userpath>/CloudStation/Hobbyprojekte/3D Drucker/CoreXY/Assembly/Parts/Screws/Hammermutter B-Typ Nut6 M4.FCStd
  timeLastImport = 1430523528
  updateColors = true
FEATURE [Part::FeaturePython] Hammermutter_B_Typ_Nut6_M4_import01105  # a2plus imported part (geometry in sourceFile) (typed FeaturePython)
  Placement = pos=(425,10,86.0002) rot=(0.57735,0.57735,-0.57735;4.18879rad)
  fixedPosition = false
  sourceFile = <userpath>/CloudStation/Hobbyprojekte/3D Drucker/CoreXY/Assembly/Parts/Screws/Hammermutter B-Typ Nut6 M4.FCStd
  timeLastImport = 1430523528
  updateColors = true
FEATURE [Part::FeaturePython] Hammermutter_B_Typ_Nut6_M4_import01106  # a2plus imported part (geometry in sourceFile) (typed FeaturePython)
  Placement = pos=(406.001,10,105) rot=(0.707107,0.707107,0;3.14159rad)
  fixedPosition = false
  sourceFile = <userpath>/CloudStation/Hobbyprojekte/3D Drucker/CoreXY/Assembly/Parts/Screws/Hammermutter B-Typ Nut6 M4.FCStd
  timeLastImport = 1430523528
  updateColors = true
FEATURE [Part::FeaturePython] Hammermutter_B_Typ_Nut6_M4_import01107  # a2plus imported part (geometry in sourceFile) (typed FeaturePython)
  Placement = pos=(15,10,86.0002) rot=(0.57735,-0.57735,0.57735;4.18879rad)
  fixedPosition = false
  sourceFile = <userpath>/CloudStation/Hobbyprojekte/3D Drucker/CoreXY/Assembly/Parts/Screws/Hammermutter B-Typ Nut6 M4.FCStd
  timeLastImport = 1430523528
  updateColors = true
FEATURE [Part::FeaturePython] Hammermutter_B_Typ_Nut6_M4_import01108  # a2plus imported part (geometry in sourceFile) (typed FeaturePython)
  Placement = pos=(33.9988,10,105) rot=(0.707107,0.707107,0;3.14159rad)
  fixedPosition = false
  sourceFile = <userpath>/CloudStation/Hobbyprojekte/3D Drucker/CoreXY/Assembly/Parts/Screws/Hammermutter B-Typ Nut6 M4.FCStd
  timeLastImport = 1430523528
  updateColors = true
FEATURE [Part::FeaturePython] Hammermutter_B_Typ_Nut6_M4_import01109  # a2plus imported part (geometry in sourceFile) (typed FeaturePython)
  Placement = pos=(425,430,86.0012) rot=(0.57735,-0.57735,-0.57735;2.0944rad)
  fixedPosition = false
  sourceFile = <userpath>/CloudStation/Hobbyprojekte/3D Drucker/CoreXY/Assembly/Parts/Screws/Hammermutter B-Typ Nut6 M4.FCStd
  timeLastImport = 1430523528
  updateColors = true
FEATURE [Part::FeaturePython] Hammermutter_B_Typ_Nut6_M4_import01110  # a2plus imported part (geometry in sourceFile) (typed FeaturePython)
  Placement = pos=(406,430,105) rot=(0.707107,0.707107,0;3.14159rad)
  fixedPosition = false
  sourceFile = <userpath>/CloudStation/Hobbyprojekte/3D Drucker/CoreXY/Assembly/Parts/Screws/Hammermutter B-Typ Nut6 M4.FCStd
  timeLastImport = 1430523528
  updateColors = true
FEATURE [Part::FeaturePython] Hammermutter_B_Typ_Nut6_M4_import01111  # a2plus imported part (geometry in sourceFile) (typed FeaturePython)
  Placement = pos=(15,430,86.0012) rot=(0.57735,0.57735,0.57735;2.0944rad)
  fixedPosition = false
  sourceFile = <userpath>/CloudStation/Hobbyprojekte/3D Drucker/CoreXY/Assembly/Parts/Screws/Hammermutter B-Typ Nut6 M4.FCStd
  timeLastImport = 1430523528
  updateColors = true
FEATURE [Part::FeaturePython] Hammermutter_B_Typ_Nut6_M4_import01112  # a2plus imported part (geometry in sourceFile) (typed FeaturePython)
  Placement = pos=(33.9988,430,105) rot=(0.707107,0.707107,0;3.14159rad)
  fixedPosition = false
  sourceFile = <userpath>/CloudStation/Hobbyprojekte/3D Drucker/CoreXY/Assembly/Parts/Screws/Hammermutter B-Typ Nut6 M4.FCStd
  timeLastImport = 1430523528
  updateColors = true
FEATURE [Part::FeaturePython] Hammermutter_B_Typ_Nut6_M4_import01113  # a2plus imported part (geometry in sourceFile) (typed FeaturePython)
  Placement = pos=(10,15,134) rot=(-1,0,0;1.5708rad)
  fixedPosition = false
  sourceFile = <userpath>/CloudStation/Hobbyprojekte/3D Drucker/CoreXY/Assembly/Parts/Screws/Hammermutter B-Typ Nut6 M4.FCStd
  timeLastImport = 1430523528
  updateColors = true
FEATURE [Part::FeaturePython] Hammermutter_B_Typ_Nut6_M4_import01114  # a2plus imported part (geometry in sourceFile) (typed FeaturePython)
  Placement = pos=(10,425,134) rot=(1,0,0;1.5708rad)
  fixedPosition = false
  sourceFile = <userpath>/CloudStation/Hobbyprojekte/3D Drucker/CoreXY/Assembly/Parts/Screws/Hammermutter B-Typ Nut6 M4.FCStd
  timeLastImport = 1430523528
  updateColors = true
FEATURE [Part::FeaturePython] Hammermutter_B_Typ_Nut6_M4_import01115  # a2plus imported part (geometry in sourceFile) (typed FeaturePython)
  Placement = pos=(10,406.001,115) rot=(0,0,1;0rad)
  fixedPosition = false
  sourceFile = <userpath>/CloudStation/Hobbyprojekte/3D Drucker/CoreXY/Assembly/Parts/Screws/Hammermutter B-Typ Nut6 M4.FCStd
  timeLastImport = 1430523528
  updateColors = true
FEATURE [Part::FeaturePython] Hammermutter_B_Typ_Nut6_M4_import01116  # a2plus imported part (geometry in sourceFile) (typed FeaturePython)
  Placement = pos=(10,33.9988,115) rot=(0,0,1;0rad)
  fixedPosition = false
  sourceFile = <userpath>/CloudStation/Hobbyprojekte/3D Drucker/CoreXY/Assembly/Parts/Screws/Hammermutter B-Typ Nut6 M4.FCStd
  timeLastImport = 1430523528
  updateColors = true
FEATURE [Part::FeaturePython] Hammermutter_B_Typ_Nut6_M4_import01117  # a2plus imported part (geometry in sourceFile) (typed FeaturePython)
  Placement = pos=(430,425,134) rot=(1,0,0;1.5708rad)
  fixedPosition = false
  sourceFile = <userpath>/CloudStation/Hobbyprojekte/3D Drucker/CoreXY/Assembly/Parts/Screws/Hammermutter B-Typ Nut6 M4.FCStd
  timeLastImport = 1430523528
  updateColors = true
FEATURE [Part::FeaturePython] Hammermutter_B_Typ_Nut6_M4_import01118  # a2plus imported part (geometry in sourceFile) (typed FeaturePython)
  Placement = pos=(430,406.001,115) rot=(0,0,1;0rad)
  fixedPosition = false
  sourceFile = <userpath>/CloudStation/Hobbyprojekte/3D Drucker/CoreXY/Assembly/Parts/Screws/Hammermutter B-Typ Nut6 M4.FCStd
  timeLastImport = 1430523528
  updateColors = true
FEATURE [Part::FeaturePython] Hammermutter_B_Typ_Nut6_M4_import01119  # a2plus imported part (geometry in sourceFile) (typed FeaturePython)
  Placement = pos=(430,15,134) rot=(-1,0,0;1.5708rad)
  fixedPosition = false
  sourceFile = <userpath>/CloudStation/Hobbyprojekte/3D Drucker/CoreXY/Assembly/Parts/Screws/Hammermutter B-Typ Nut6 M4.FCStd
  timeLastImport = 1430523528
  updateColors = true
FEATURE [Part::FeaturePython] Hammermutter_B_Typ_Nut6_M4_import01120  # a2plus imported part (geometry in sourceFile) (typed FeaturePython)
  Placement = pos=(430,33.9988,115) rot=(0,0,1;0rad)
  fixedPosition = false
  sourceFile = <userpath>/CloudStation/Hobbyprojekte/3D Drucker/CoreXY/Assembly/Parts/Screws/Hammermutter B-Typ Nut6 M4.FCStd
  timeLastImport = 1430523528
  updateColors = true
FEATURE [Part::FeaturePython] Hammermutter_B_Typ_Nut6_M4_import01121  # a2plus imported part (geometry in sourceFile) (typed FeaturePython)
  Placement = pos=(425,430,134) rot=(0.57735,-0.57735,-0.57735;2.0944rad)
  fixedPosition = false
  sourceFile = <userpath>/CloudStation/Hobbyprojekte/3D Drucker/CoreXY/Assembly/Parts/Screws/Hammermutter B-Typ Nut6 M4.FCStd
  timeLastImport = 1430523528
  updateColors = true
FEATURE [Part::FeaturePython] Hammermutter_B_Typ_Nut6_M4_import01122  # a2plus imported part (geometry in sourceFile) (typed FeaturePython)
  Placement = pos=(406.001,430,115) rot=(0,0,-1;1.5708rad)
  fixedPosition = false
  sourceFile = <userpath>/CloudStation/Hobbyprojekte/3D Drucker/CoreXY/Assembly/Parts/Screws/Hammermutter B-Typ Nut6 M4.FCStd
  timeLastImport = 1430523528
  updateColors = true
FEATURE [Part::FeaturePython] Hammermutter_B_Typ_Nut6_M4_import01123  # a2plus imported part (geometry in sourceFile) (typed FeaturePython)
  Placement = pos=(15,430,134) rot=(0.57735,0.57735,0.57735;2.0944rad)
  fixedPosition = false
  sourceFile = <userpath>/CloudStation/Hobbyprojekte/3D Drucker/CoreXY/Assembly/Parts/Screws/Hammermutter B-Typ Nut6 M4.FCStd
  timeLastImport = 1430523528
  updateColors = true
FEATURE [Part::FeaturePython] Hammermutter_B_Typ_Nut6_M4_import01124  # a2plus imported part (geometry in sourceFile) (typed FeaturePython)
  Placement = pos=(33.9988,430,115) rot=(0,0,-1;1.5708rad)
  fixedPosition = false
  sourceFile = <userpath>/CloudStation/Hobbyprojekte/3D Drucker/CoreXY/Assembly/Parts/Screws/Hammermutter B-Typ Nut6 M4.FCStd
  timeLastImport = 1430523528
  updateColors = true
FEATURE [Part::FeaturePython] Hammermutter_B_Typ_Nut6_M4_import01125  # a2plus imported part (geometry in sourceFile) (typed FeaturePython)
  Placement = pos=(425,10,133.999) rot=(0.57735,0.57735,-0.57735;4.18879rad)
  fixedPosition = false
  sourceFile = <userpath>/CloudStation/Hobbyprojekte/3D Drucker/CoreXY/Assembly/Parts/Screws/Hammermutter B-Typ Nut6 M4.FCStd
  timeLastImport = 1430523528
  updateColors = true
FEATURE [Part::FeaturePython] Hammermutter_B_Typ_Nut6_M4_import01126  # a2plus imported part (geometry in sourceFile) (typed FeaturePython)
  Placement = pos=(406,9.99999,115) rot=(0,0,-1;1.5708rad)
  fixedPosition = false
  sourceFile = <userpath>/CloudStation/Hobbyprojekte/3D Drucker/CoreXY/Assembly/Parts/Screws/Hammermutter B-Typ Nut6 M4.FCStd
  timeLastImport = 1430523528
  updateColors = true
FEATURE [Part::FeaturePython] Hammermutter_B_Typ_Nut6_M4_import01127  # a2plus imported part (geometry in sourceFile) (typed FeaturePython)
  Placement = pos=(15,9.99999,133.999) rot=(0.57735,-0.57735,0.57735;4.18879rad)
  fixedPosition = false
  sourceFile = <userpath>/CloudStation/Hobbyprojekte/3D Drucker/CoreXY/Assembly/Parts/Screws/Hammermutter B-Typ Nut6 M4.FCStd
  timeLastImport = 1430523528
  updateColors = true
FEATURE [Part::FeaturePython] Hammermutter_B_Typ_Nut6_M4_import01128  # a2plus imported part (geometry in sourceFile) (typed FeaturePython)
  Placement = pos=(33.9988,9.99999,115) rot=(0,0,-1;1.5708rad)
  fixedPosition = false
  sourceFile = <userpath>/CloudStation/Hobbyprojekte/3D Drucker/CoreXY/Assembly/Parts/Screws/Hammermutter B-Typ Nut6 M4.FCStd
  timeLastImport = 1430523528
  updateColors = true
FEATURE [Part::FeaturePython] idler_block_topM_01001  # a2plus imported part (geometry in sourceFile) (typed FeaturePython)
  Placement = pos=(420,20,484.5) rot=(0,1,0;3.14159rad)
  fixedPosition = false
  sourceFile = <userpath>/CloudStation/Hobbyprojekte/3D Drucker/CoreXY/Assembly/Parts/Printed Parts/idler-block-topM.FCStd
  timeLastImport = 1445695894
  updateColors = true
FEATURE [App::DocumentObjectGroup] Gruppe024  label="Main Parts002"
  Group = -> [idler_block_bottom_topM_01,idler_block_topM_01001]
FEATURE [Part::FeaturePython] spacer10_0mm_01  # a2plus imported part (geometry in sourceFile) (typed FeaturePython)
  Placement = pos=(402.3,215.9,458.6) rot=(0,0,1;0rad)
  fixedPosition = false
  sourceFile = <userpath>/CloudStation/Hobbyprojekte/3D Drucker/CoreXY/Assembly/Parts/Printed Parts/spacer10_0mm.FCStd
  timeLastImport = 1458256983
  updateColors = true
FEATURE [Part::FeaturePython] spacer12_3mm_01  # a2plus imported part (geometry in sourceFile) (typed FeaturePython)
  Placement = pos=(402.3,201.5,469.5) rot=(0,0,1;0rad)
  fixedPosition = false
  sourceFile = <userpath>/CloudStation/Hobbyprojekte/3D Drucker/CoreXY/Assembly/Parts/Printed Parts/spacer12_3mm.FCStd
  timeLastImport = 1458257729
  updateColors = true
FEATURE [App::DocumentObjectGroup] Gruppe124  label="Distancers010"
  Group = -> [spacer10_0mm_01,spacer12_3mm_01]
FEATURE [Part::FeaturePython] Screw157  label="M4x30-Screw028"  # Fasteners workbench fastener (typed FeaturePython)
  Placement = pos=(38,216.205,482.1) rot=(0,0,1;0rad)
  diameter = 5
  invert = false
  length = 9
  matchOuter = false
  offset = 0
  thread = false
  type = 6
FEATURE [Part::FeaturePython] Washer105  label="M4-Washer318"  # Fasteners workbench fastener (typed FeaturePython)
  Placement = pos=(38,201.3,481.2) rot=(0,0,1;0rad)
  diameter = 5
  invert = false
  matchOuter = false
  offset = 0
  type = 0
FEATURE [Part::FeaturePython] Washer106  label="M4-Washer323"  # Fasteners workbench fastener (typed FeaturePython)
  Placement = pos=(38,201.3,477.85) rot=(0,0,1;0rad)
  diameter = 5
  invert = false
  matchOuter = false
  offset = 0
  type = 2
FEATURE [Part::FeaturePython] Nut037  label="M4-Nut027"  # Fasteners workbench fastener (typed FeaturePython)
  Placement = pos=(38,216.205,452.1) rot=(0,0,1;0rad)
  diameter = 6
  invert = false
  matchOuter = false
  offset = 0
  thread = false
  type = 1
FEATURE [Part::FeaturePython] Washer107  label="M4-Washer317"  # Fasteners workbench fastener (typed FeaturePython)
  Placement = pos=(38,216.3,481.2) rot=(0,0,1;0rad)
  diameter = 5
  invert = false
  matchOuter = false
  offset = 0
  type = 0
FEATURE [Part::FeaturePython] Washer109  label="M4-Washer324"  # Fasteners workbench fastener (typed FeaturePython)
  Placement = pos=(38,201.3,478.4) rot=(0,0,1;0rad)
  diameter = 5
  invert = false
  matchOuter = false
  offset = 0
  type = 0
FEATURE [Part::FeaturePython] Washer110  label="M4-Washer326"  # Fasteners workbench fastener (typed FeaturePython)
  Placement = pos=(38,216.3,469) rot=(0,0,1;0rad)
  diameter = 5
  invert = false
  matchOuter = false
  offset = 0
  type = 0
FEATURE [Part::FeaturePython] Washer111  label="M4-Washer327"  # Fasteners workbench fastener (typed FeaturePython)
  Placement = pos=(38,216.205,458.1) rot=(0,0,1;0rad)
  diameter = 5
  invert = false
  matchOuter = false
  offset = 0
  type = 0
FEATURE [Part::FeaturePython] Washer112  label="M4-Washer328"  # Fasteners workbench fastener (typed FeaturePython)
  Placement = pos=(38,216.205,455.3) rot=(0,0,1;0rad)
  diameter = 5
  invert = false
  matchOuter = false
  offset = 0
  type = 0
FEATURE [Part::FeaturePython] Screw158  label="M4x30-Screw029"  # Fasteners workbench fastener (typed FeaturePython)
  Placement = pos=(38,201.205,482.1) rot=(0,0,1;0rad)
  diameter = 5
  invert = false
  length = 9
  matchOuter = false
  offset = 0
  thread = false
  type = 6
FEATURE [Part::FeaturePython] Washer113  label="M4-Washer325"  # Fasteners workbench fastener (typed FeaturePython)
  Placement = pos=(38,201.3,468.42) rot=(0,0,1;0rad)
  diameter = 5
  invert = false
  matchOuter = false
  offset = 0
  type = 2
FEATURE [Part::FeaturePython] Washer114  label="M4-Washer329"  # Fasteners workbench fastener (typed FeaturePython)
  Placement = pos=(38,201.205,455.3) rot=(0,0,1;0rad)
  diameter = 5
  invert = false
  matchOuter = false
  offset = 0
  type = 0
FEATURE [Part::FeaturePython] Nut038  label="M4-Nut028"  # Fasteners workbench fastener (typed FeaturePython)
  Placement = pos=(38,201.205,452.1) rot=(0,0,1;0rad)
  diameter = 6
  invert = false
  matchOuter = false
  offset = 0
  thread = false
  type = 1
FEATURE [App::DocumentObjectGroup] Gruppe106  label="Screws011"
  Group = -> [Washer107,Screw157,Washer105,Screw158,Washer106,Washer109,Washer113,Washer110,Washer111,Nut037,Washer112,Washer114,Nut038]
FEATURE [App::DocumentObjectGroup] Gruppe104  label="XY-Slide_left"
  Group = -> [Gruppe105,Gruppe106,Gruppe107]
FEATURE [Part::FeaturePython] Nut039  label="M4-Nut033"  # Fasteners workbench fastener (typed FeaturePython)
  Placement = pos=(402,201.242,452.1) rot=(0,0,1;0rad)
  diameter = 6
  invert = false
  matchOuter = false
  offset = 0
  thread = false
  type = 1
FEATURE [Part::FeaturePython] Washer115  label="M4-Washer348"  # Fasteners workbench fastener (typed FeaturePython)
  Placement = pos=(402,216.242,467.5) rot=(0,0,1;0rad)
  diameter = 5
  invert = false
  matchOuter = false
  offset = 0
  type = 0
FEATURE [Part::FeaturePython] Washer116  label="M4-Washer358"  # Fasteners workbench fastener (typed FeaturePython)
  Placement = pos=(402,216.242,481.2) rot=(0,0,1;0rad)
  diameter = 5
  invert = false
  matchOuter = false
  offset = 0
  type = 0
FEATURE [Part::FeaturePython] Washer117  label="M4-Washer355"  # Fasteners workbench fastener (typed FeaturePython)
  Placement = pos=(402,216.242,478.4) rot=(0,0,1;0rad)
  diameter = 5
  invert = false
  matchOuter = false
  offset = 0
  type = 0
FEATURE [Part::FeaturePython] Nut040  label="M4-Nut034"  # Fasteners workbench fastener (typed FeaturePython)
  Placement = pos=(402,216.242,452.1) rot=(0,0,1;0rad)
  diameter = 6
  invert = false
  matchOuter = false
  offset = 0
  thread = false
  type = 1
FEATURE [Part::FeaturePython] Washer118  label="M4-Washer356"  # Fasteners workbench fastener (typed FeaturePython)
  Placement = pos=(402,201.242,468.43) rot=(0,0,1;0rad)
  diameter = 5
  invert = false
  matchOuter = false
  offset = 0
  type = 2
FEATURE [Part::FeaturePython] Washer119  label="M4-Washer359"  # Fasteners workbench fastener (typed FeaturePython)
  Placement = pos=(402,201.242,481.2) rot=(0,0,1;0rad)
  diameter = 5
  invert = false
  matchOuter = false
  offset = 0
  type = 0
FEATURE [Part::FeaturePython] Screw159  label="M4x30-Screw036"  # Fasteners workbench fastener (typed FeaturePython)
  Placement = pos=(402,216.242,482.1) rot=(0,0,1;0rad)
  diameter = 5
  invert = false
  length = 9
  matchOuter = false
  offset = 0
  thread = false
  type = 6
FEATURE [Part::FeaturePython] Screw160  label="M4x30-Screw037"  # Fasteners workbench fastener (typed FeaturePython)
  Placement = pos=(402,201.242,482.1) rot=(0,0,1;0rad)
  diameter = 5
  invert = false
  length = 9
  matchOuter = false
  offset = 0
  thread = false
  type = 6
FEATURE [Part::FeaturePython] Washer120  label="M4-Washer350"  # Fasteners workbench fastener (typed FeaturePython)
  Placement = pos=(402,216.242,455.3) rot=(0,0,1;0rad)
  diameter = 5
  invert = false
  matchOuter = false
  offset = 0
  type = 0
FEATURE [Part::FeaturePython] Washer121  label="M4-Washer351"  # Fasteners workbench fastener (typed FeaturePython)
  Placement = pos=(402,201.242,455.3) rot=(0,0,1;0rad)
  diameter = 5
  invert = false
  matchOuter = false
  offset = 0
  type = 0
FEATURE [Part::FeaturePython] Washer122  label="M4-Washer352"  # Fasteners workbench fastener (typed FeaturePython)
  Placement = pos=(402,201.242,458.2) rot=(0,0,1;0rad)
  diameter = 5
  invert = false
  matchOuter = false
  offset = 0
  type = 0
FEATURE [Part::FeaturePython] Washer123  label="M4-Washer353"  # Fasteners workbench fastener (typed FeaturePython)
  Placement = pos=(402,201.242,459.1) rot=(0,0,1;0rad)
  diameter = 5
  invert = false
  matchOuter = false
  offset = 0
  type = 2
FEATURE [App::DocumentObjectGroup] Gruppe110  label="Screws012"
  Group = -> [Nut039,Washer115,Washer116,Washer117,Nut040,Washer118,Washer119,Screw159,Screw160,Washer120,Washer121,Washer122,Washer123]
FEATURE [App::DocumentObjectGroup] Gruppe108  label="XY-Slide_right"
  Group = -> [Gruppe109,Gruppe110,Gruppe111]
FEATURE [Part::FeaturePython] Screw161  label="M6x16-Screw085"  # Fasteners workbench fastener (typed FeaturePython)
  Placement = pos=(10,18,530) rot=(1,0,0;1.5708rad)
  baseObject = -> Wuerfelverbinder_20x20_import01 [Edge77]
  diameter = 4
  invert = true
  length = 3
  matchOuter = false
  offset = 0
  thread = false
  type = 20
FEATURE [Part::FeaturePython] Screw162  label="M6x16-Screw086"  # Fasteners workbench fastener (typed FeaturePython)
  Placement = pos=(18,10,530) rot=(0,-1,0;1.5708rad)
  baseObject = -> Wuerfelverbinder_20x20_import01 [Edge94]
  diameter = 4
  invert = true
  length = 3
  matchOuter = false
  offset = 0
  thread = false
  type = 20
FEATURE [Part::FeaturePython] Screw163  label="M6x16-Screw087"  # Fasteners workbench fastener (typed FeaturePython)
  Placement = pos=(10,10,522) rot=(0,0,1;0rad)
  baseObject = -> Wuerfelverbinder_20x20_import01 [Edge113]
  diameter = 4
  invert = true
  length = 3
  matchOuter = false
  offset = 0
  thread = false
  type = 20
FEATURE [App::DocumentObjectGroup] Gruppe139  label="OVL"
  Group = -> [Screw161,Screw162,Screw163]
FEATURE [Part::FeaturePython] Screw  label="M6x16-Screw"  # Fasteners workbench fastener (typed FeaturePython)
  Placement = pos=(430,10,522) rot=(0,0,1;0rad)
  baseObject = -> Wuerfelverbinder_20x20_import01001 [Edge113]
  diameter = 4
  invert = true
  length = 3
  matchOuter = false
  offset = 0
  thread = false
  type = 20
FEATURE [Part::FeaturePython] Screw164  label="M6x16-Screw088"  # Fasteners workbench fastener (typed FeaturePython)
  Placement = pos=(422,10,530) rot=(0,1,0;1.5708rad)
  baseObject = -> Wuerfelverbinder_20x20_import01001 [Edge77]
  diameter = 4
  invert = true
  length = 3
  matchOuter = false
  offset = 0
  thread = false
  type = 20
FEATURE [Part::FeaturePython] Screw165  label="M6x16-Screw089"  # Fasteners workbench fastener (typed FeaturePython)
  Placement = pos=(430,18,530) rot=(1,0,0;1.5708rad)
  baseObject = -> Wuerfelverbinder_20x20_import01001 [Edge94]
  diameter = 4
  invert = true
  length = 3
  matchOuter = false
  offset = 0
  thread = false
  type = 20
FEATURE [App::DocumentObjectGroup] Gruppe140  label="OVR"
  Group = -> [Screw,Screw164,Screw165]
FEATURE [Part::FeaturePython] Screw166  label="M6x16-Screw090"  # Fasteners workbench fastener (typed FeaturePython)
  Placement = pos=(10,422,530) rot=(-1,0,0;1.5708rad)
  baseObject = -> Wuerfelverbinder_20x20_import01004 [Edge94]
  diameter = 4
  invert = true
  length = 3
  matchOuter = false
  offset = 0
  thread = false
  type = 20
FEATURE [Part::FeaturePython] Screw167  label="M6x16-Screw091"  # Fasteners workbench fastener (typed FeaturePython)
  Placement = pos=(18,430,530) rot=(0,-1,0;1.5708rad)
  baseObject = -> Wuerfelverbinder_20x20_import01004 [Edge77]
  diameter = 4
  invert = true
  length = 3
  matchOuter = false
  offset = 0
  thread = false
  type = 20
FEATURE [Part::FeaturePython] Screw168  label="M6x16-Screw092"  # Fasteners workbench fastener (typed FeaturePython)
  Placement = pos=(10,430,522) rot=(0,0,1;0rad)
  baseObject = -> Wuerfelverbinder_20x20_import01004 [Edge113]
  diameter = 4
  invert = true
  length = 3
  matchOuter = false
  offset = 0
  thread = false
  type = 20
FEATURE [App::DocumentObjectGroup] Gruppe141  label="OHL"
  Group = -> [Screw166,Screw167,Screw168]
FEATURE [Part::FeaturePython] Screw169  label="M6x16-Screw093"  # Fasteners workbench fastener (typed FeaturePython)
  Placement = pos=(422,430,530) rot=(0,1,0;1.5708rad)
  baseObject = -> Wuerfelverbinder_20x20_import01005 [Edge94]
  diameter = 4
  invert = true
  length = 3
  matchOuter = false
  offset = 0
  thread = false
  type = 20
FEATURE [Part::FeaturePython] Screw170  label="M6x16-Screw094"  # Fasteners workbench fastener (typed FeaturePython)
  Placement = pos=(430,422,530) rot=(-1,0,0;1.5708rad)
  baseObject = -> Wuerfelverbinder_20x20_import01005 [Edge77]
  diameter = 4
  invert = true
  length = 3
  matchOuter = false
  offset = 0
  thread = false
  type = 20
FEATURE [Part::FeaturePython] Screw171  label="M6x16-Screw095"  # Fasteners workbench fastener (typed FeaturePython)
  Placement = pos=(430,430,522) rot=(0,0,1;0rad)
  baseObject = -> Wuerfelverbinder_20x20_import01005 [Edge113]
  diameter = 4
  invert = true
  length = 3
  matchOuter = false
  offset = 0
  thread = false
  type = 20
FEATURE [App::DocumentObjectGroup] Gruppe142  label="OHR"
  Group = -> [Screw169,Screw170,Screw171]
FEATURE [Part::FeaturePython] Screw172  label="M6x16-Screw096"  # Fasteners workbench fastener (typed FeaturePython)
  Placement = pos=(10,10,18) rot=(1,0,0;3.14159rad)
  baseObject = -> Wuerfelverbinder_20x20_import01010 [Edge77]
  diameter = 4
  invert = true
  length = 3
  matchOuter = false
  offset = 0
  thread = false
  type = 20
FEATURE [Part::FeaturePython] Screw173  label="M6x16-Screw097"  # Fasteners workbench fastener (typed FeaturePython)
  Placement = pos=(10,18,10) rot=(1,0,0;1.5708rad)
  baseObject = -> Wuerfelverbinder_20x20_import01010 [Edge113]
  diameter = 4
  invert = true
  length = 3
  matchOuter = false
  offset = 0
  thread = false
  type = 20
FEATURE [Part::FeaturePython] Screw174  label="M6x16-Screw098"  # Fasteners workbench fastener (typed FeaturePython)
  Placement = pos=(18,10,10) rot=(0,-1,0;1.5708rad)
  baseObject = -> Wuerfelverbinder_20x20_import01010 [Edge94]
  diameter = 4
  invert = true
  length = 3
  matchOuter = false
  offset = 0
  thread = false
  type = 20
FEATURE [App::DocumentObjectGroup] Gruppe143  label="UVL"
  Group = -> [Screw172,Screw173,Screw174]
FEATURE [Part::FeaturePython] Screw175  label="M6x16-Screw099"  # Fasteners workbench fastener (typed FeaturePython)
  Placement = pos=(430,10,18) rot=(1,0,0;3.14159rad)
  baseObject = -> Wuerfelverbinder_20x20_import01009 [Edge77]
  diameter = 4
  invert = true
  length = 3
  matchOuter = false
  offset = 0
  thread = false
  type = 20
FEATURE [Part::FeaturePython] Screw176  label="M6x16-Screw100"  # Fasteners workbench fastener (typed FeaturePython)
  Placement = pos=(422,10,10) rot=(0,1,0;1.5708rad)
  baseObject = -> Wuerfelverbinder_20x20_import01009 [Edge113]
  diameter = 4
  invert = true
  length = 3
  matchOuter = false
  offset = 0
  thread = false
  type = 20
FEATURE [Part::FeaturePython] Screw177  label="M6x16-Screw101"  # Fasteners workbench fastener (typed FeaturePython)
  Placement = pos=(430,18,10) rot=(1,0,0;1.5708rad)
  baseObject = -> Wuerfelverbinder_20x20_import01009 [Edge94]
  diameter = 4
  invert = true
  length = 3
  matchOuter = false
  offset = 0
  thread = false
  type = 20
FEATURE [App::DocumentObjectGroup] Gruppe144  label="UVR"
  Group = -> [Screw175,Screw176,Screw177]
FEATURE [Part::FeaturePython] Screw178  label="M6x16-Screw102"  # Fasteners workbench fastener (typed FeaturePython)
  Placement = pos=(10,430,18) rot=(1,0,0;3.14159rad)
  baseObject = -> Wuerfelverbinder_20x20_import01011 [Edge113]
  diameter = 4
  invert = true
  length = 3
  matchOuter = false
  offset = 0
  thread = false
  type = 20
FEATURE [Part::FeaturePython] Screw179  label="M6x16-Screw103"  # Fasteners workbench fastener (typed FeaturePython)
  Placement = pos=(10,422,10) rot=(-1,0,0;1.5708rad)
  baseObject = -> Wuerfelverbinder_20x20_import01011 [Edge77]
  diameter = 4
  invert = true
  length = 3
  matchOuter = false
  offset = 0
  thread = false
  type = 20
FEATURE [Part::FeaturePython] Screw180  label="M6x16-Screw104"  # Fasteners workbench fastener (typed FeaturePython)
  Placement = pos=(18,430,10) rot=(0,-1,0;1.5708rad)
  baseObject = -> Wuerfelverbinder_20x20_import01011 [Edge94]
  diameter = 4
  invert = true
  length = 3
  matchOuter = false
  offset = 0
  thread = false
  type = 20
FEATURE [App::DocumentObjectGroup] Gruppe145  label="UHL"
  Group = -> [Screw178,Screw179,Screw180]
FEATURE [Part::FeaturePython] Screw181  label="M6x16-Screw105"  # Fasteners workbench fastener (typed FeaturePython)
  Placement = pos=(430,422,10) rot=(-1,0,0;1.5708rad)
  baseObject = -> Wuerfelverbinder_20x20_import01008 [Edge94]
  diameter = 4
  invert = true
  length = 3
  matchOuter = false
  offset = 0
  thread = false
  type = 20
FEATURE [Part::FeaturePython] Screw182  label="M6x16-Screw106"  # Fasteners workbench fastener (typed FeaturePython)
  Placement = pos=(430,430,18) rot=(1,0,0;3.14159rad)
  baseObject = -> Wuerfelverbinder_20x20_import01008 [Edge113]
  diameter = 4
  invert = true
  length = 3
  matchOuter = false
  offset = 0
  thread = false
  type = 20
FEATURE [Part::FeaturePython] Screw183  label="M6x16-Screw107"  # Fasteners workbench fastener (typed FeaturePython)
  Placement = pos=(422,430,10) rot=(0,1,0;1.5708rad)
  baseObject = -> Wuerfelverbinder_20x20_import01008 [Edge77]
  diameter = 4
  invert = true
  length = 3
  matchOuter = false
  offset = 0
  thread = false
  type = 20
FEATURE [App::DocumentObjectGroup] Gruppe146  label="UHR"
  Group = -> [Screw181,Screw182,Screw183]
FEATURE [App::DocumentObjectGroup] Gruppe005  label="Würfel/T-Slot Screws"
  Group = -> [Gruppe139,Gruppe140,Gruppe141,Gruppe142,Gruppe143,Gruppe144,Gruppe145,Gruppe146]
FEATURE [Part::FeaturePython] Washer124  label="M4-Washer632"  # Fasteners workbench fastener (typed FeaturePython)
  Placement = pos=(406,430,96.0012) rot=(1,0,0;3.14159rad)
  baseObject = -> Angle_Bracket_import12 [Edge19]
  diameter = 5
  invert = false
  matchOuter = false
  offset = 0
  type = 0
FEATURE [Part::FeaturePython] Washer125  label="M4-Washer633"  # Fasteners workbench fastener (typed FeaturePython)
  Placement = pos=(416,430,86.0012) rot=(0,-1,0;1.5708rad)
  baseObject = -> Angle_Bracket_import12 [Edge22]
  diameter = 5
  invert = false
  matchOuter = false
  offset = 0
  type = 0
FEATURE [Part::FeaturePython] Washer126  label="M4-Washer634"  # Fasteners workbench fastener (typed FeaturePython)
  Placement = pos=(430,416.001,86.0002) rot=(1,0,0;1.5708rad)
  baseObject = -> Angle_Bracket_import08 [Edge19]
  diameter = 5
  invert = false
  matchOuter = false
  offset = 0
  type = 0
FEATURE [Part::FeaturePython] Washer127  label="M4-Washer635"  # Fasteners workbench fastener (typed FeaturePython)
  Placement = pos=(430,406.001,95.9997) rot=(1,0,0;3.14159rad)
  baseObject = -> Angle_Bracket_import08 [Edge22]
  diameter = 5
  invert = false
  matchOuter = false
  offset = 0
  type = 0
FEATURE [Part::FeaturePython] Screw184  label="M4x10-Screw268"  # Fasteners workbench fastener (typed FeaturePython)
  Placement = pos=(415.1,430,86.0012) rot=(0,-1,0;1.5708rad)
  baseObject = -> Washer125 [Edge1]
  diameter = 4
  invert = false
  length = 2
  matchOuter = false
  offset = 0
  thread = false
  type = 5
FEATURE [Part::FeaturePython] Screw185  label="M4x10-Screw269"  # Fasteners workbench fastener (typed FeaturePython)
  Placement = pos=(406,430,95.1012) rot=(1,0,0;3.14159rad)
  baseObject = -> Washer124 [Edge1]
  diameter = 4
  invert = false
  length = 2
  matchOuter = false
  offset = 0
  thread = false
  type = 5
FEATURE [Part::FeaturePython] Screw186  label="M4x10-Screw270"  # Fasteners workbench fastener (typed FeaturePython)
  Placement = pos=(430,415.101,86.0002) rot=(1,0,0;1.5708rad)
  baseObject = -> Washer126 [Edge1]
  diameter = 4
  invert = false
  length = 2
  matchOuter = false
  offset = 0
  thread = false
  type = 5
FEATURE [Part::FeaturePython] Screw187  label="M4x10-Screw271"  # Fasteners workbench fastener (typed FeaturePython)
  Placement = pos=(430,406.001,95.0997) rot=(1,0,0;3.14159rad)
  baseObject = -> Washer127 [Edge1]
  diameter = 4
  invert = false
  length = 2
  matchOuter = false
  offset = 0
  thread = false
  type = 5
FEATURE [App::DocumentObjectGroup] Gruppe129  label="HR001"
  Group = -> [Hammermutter_B_Typ_Nut6_M4_import01110,Hammermutter_B_Typ_Nut6_M4_import01109,Hammermutter_B_Typ_Nut6_M4_import01103,Hammermutter_B_Typ_Nut6_M4_import01104,Washer124,Washer125,Washer126,Washer127,Screw184,Screw185,Screw186,Screw187]
FEATURE [Part::FeaturePython] Washer128  label="M4-Washer636"  # Fasteners workbench fastener (typed FeaturePython)
  Placement = pos=(23.9988,430,86.0002) rot=(0,1,0;1.5708rad)
  baseObject = -> Angle_Bracket_import10 [Edge19]
  diameter = 5
  invert = false
  matchOuter = false
  offset = 0
  type = 0
FEATURE [Part::FeaturePython] Washer129  label="M4-Washer637"  # Fasteners workbench fastener (typed FeaturePython)
  Placement = pos=(33.9988,430,95.9997) rot=(1,0,0;3.14159rad)
  baseObject = -> Angle_Bracket_import10 [Edge22]
  diameter = 5
  invert = false
  matchOuter = false
  offset = 0
  type = 0
FEATURE [Part::FeaturePython] Washer130  label="M4-Washer638"  # Fasteners workbench fastener (typed FeaturePython)
  Placement = pos=(10,416.001,86.0002) rot=(1,0,0;1.5708rad)
  baseObject = -> Angle_Bracket_import14 [Edge19]
  diameter = 5
  invert = false
  matchOuter = false
  offset = 0
  type = 0
FEATURE [Part::FeaturePython] Washer131  label="M4-Washer639"  # Fasteners workbench fastener (typed FeaturePython)
  Placement = pos=(10,406.001,95.9997) rot=(1,0,0;3.14159rad)
  baseObject = -> Angle_Bracket_import14 [Edge22]
  diameter = 5
  invert = false
  matchOuter = false
  offset = 0
  type = 0
FEATURE [Part::FeaturePython] Screw188  label="M4x10-Screw272"  # Fasteners workbench fastener (typed FeaturePython)
  Placement = pos=(24.8988,430,86.0002) rot=(0,1,0;1.5708rad)
  baseObject = -> Washer128 [Edge1]
  diameter = 4
  invert = false
  length = 2
  matchOuter = false
  offset = 0
  thread = false
  type = 5
FEATURE [Part::FeaturePython] Screw189  label="M4x10-Screw273"  # Fasteners workbench fastener (typed FeaturePython)
  Placement = pos=(33.9988,430,95.0997) rot=(1,0,0;3.14159rad)
  baseObject = -> Washer129 [Edge1]
  diameter = 4
  invert = false
  length = 2
  matchOuter = false
  offset = 0
  thread = false
  type = 5
FEATURE [Part::FeaturePython] Screw190  label="M4x10-Screw274"  # Fasteners workbench fastener (typed FeaturePython)
  Placement = pos=(10,406.001,95.0997) rot=(1,0,0;3.14159rad)
  baseObject = -> Washer131 [Edge1]
  diameter = 4
  invert = false
  length = 2
  matchOuter = false
  offset = 0
  thread = false
  type = 5
FEATURE [Part::FeaturePython] Screw191  label="M4x10-Screw275"  # Fasteners workbench fastener (typed FeaturePython)
  Placement = pos=(10,415.101,86.0002) rot=(1,0,0;1.5708rad)
  baseObject = -> Washer130 [Edge1]
  diameter = 4
  invert = false
  length = 2
  matchOuter = false
  offset = 0
  thread = false
  type = 5
FEATURE [App::DocumentObjectGroup] Gruppe130  label="HL001"
  Group = -> [Hammermutter_B_Typ_Nut6_M4_import01100,Hammermutter_B_Typ_Nut6_M4_import01111,Hammermutter_B_Typ_Nut6_M4_import01112,Hammermutter_B_Typ_Nut6_M4_import01097,Washer128,Washer129,Washer130,Washer131,Screw188,Screw189,Screw190,Screw191]
FEATURE [Part::FeaturePython] Washer132  label="M4-Washer640"  # Fasteners workbench fastener (typed FeaturePython)
  Placement = pos=(10,33.9988,95.9997) rot=(1,0,0;3.14159rad)
  baseObject = -> Angle_Bracket_import16 [Edge22]
  diameter = 5
  invert = false
  matchOuter = false
  offset = 0
  type = 0
FEATURE [Part::FeaturePython] Washer133  label="M4-Washer641"  # Fasteners workbench fastener (typed FeaturePython)
  Placement = pos=(10,23.9988,86.0002) rot=(-1,0,0;1.5708rad)
  baseObject = -> Angle_Bracket_import16 [Edge19]
  diameter = 5
  invert = false
  matchOuter = false
  offset = 0
  type = 0
FEATURE [Part::FeaturePython] Washer134  label="M4-Washer642"  # Fasteners workbench fastener (typed FeaturePython)
  Placement = pos=(23.9988,10,86.0002) rot=(0,1,0;1.5708rad)
  baseObject = -> Angle_Bracket_import02 [Edge19]
  diameter = 5
  invert = false
  matchOuter = false
  offset = 0
  type = 0
FEATURE [Part::FeaturePython] Washer135  label="M4-Washer643"  # Fasteners workbench fastener (typed FeaturePython)
  Placement = pos=(33.9988,10,95.9997) rot=(1,0,0;3.14159rad)
  baseObject = -> Angle_Bracket_import02 [Edge22]
  diameter = 5
  invert = false
  matchOuter = false
  offset = 0
  type = 0
FEATURE [Part::FeaturePython] Screw192  label="M4x10-Screw276"  # Fasteners workbench fastener (typed FeaturePython)
  Placement = pos=(10,33.9988,95.0997) rot=(1,0,0;3.14159rad)
  baseObject = -> Washer132 [Edge1]
  diameter = 4
  invert = false
  length = 2
  matchOuter = false
  offset = 0
  thread = false
  type = 5
FEATURE [Part::FeaturePython] Screw193  label="M4x10-Screw277"  # Fasteners workbench fastener (typed FeaturePython)
  Placement = pos=(10,24.8988,86.0002) rot=(-1,0,0;1.5708rad)
  baseObject = -> Washer133 [Edge1]
  diameter = 4
  invert = false
  length = 2
  matchOuter = false
  offset = 0
  thread = false
  type = 5
FEATURE [Part::FeaturePython] Screw194  label="M4x10-Screw278"  # Fasteners workbench fastener (typed FeaturePython)
  Placement = pos=(24.8988,10,86.0002) rot=(0,1,0;1.5708rad)
  baseObject = -> Washer134 [Edge1]
  diameter = 4
  invert = false
  length = 2
  matchOuter = false
  offset = 0
  thread = false
  type = 5
FEATURE [Part::FeaturePython] Screw195  label="M4x10-Screw279"  # Fasteners workbench fastener (typed FeaturePython)
  Placement = pos=(33.9988,10,95.0997) rot=(1,0,0;3.14159rad)
  baseObject = -> Washer135 [Edge1]
  diameter = 4
  invert = false
  length = 2
  matchOuter = false
  offset = 0
  thread = false
  type = 5
FEATURE [App::DocumentObjectGroup] Gruppe131  label="VL001"
  Group = -> [Hammermutter_B_Typ_Nut6_M4_import01098,Hammermutter_B_Typ_Nut6_M4_import01099,Hammermutter_B_Typ_Nut6_M4_import01107,Hammermutter_B_Typ_Nut6_M4_import01108,Washer132,Washer133,Washer134,Washer135,Screw192,Screw193,Screw194,Screw195]
FEATURE [Part::FeaturePython] Washer136  label="M4-Washer644"  # Fasteners workbench fastener (typed FeaturePython)
  Placement = pos=(430,33.9988,95.9997) rot=(1,0,0;3.14159rad)
  baseObject = -> Angle_Bracket_import06 [Edge22]
  diameter = 5
  invert = false
  matchOuter = false
  offset = 0
  type = 0
FEATURE [Part::FeaturePython] Washer137  label="M4-Washer645"  # Fasteners workbench fastener (typed FeaturePython)
  Placement = pos=(430,23.9988,86.0002) rot=(-1,0,0;1.5708rad)
  baseObject = -> Angle_Bracket_import06 [Edge19]
  diameter = 5
  invert = false
  matchOuter = false
  offset = 0
  type = 0
FEATURE [Part::FeaturePython] Washer138  label="M4-Washer646"  # Fasteners workbench fastener (typed FeaturePython)
  Placement = pos=(406.001,10,95.9997) rot=(1,0,0;3.14159rad)
  baseObject = -> Angle_Bracket_import04 [Edge22]
  diameter = 5
  invert = false
  matchOuter = false
  offset = 0
  type = 0
FEATURE [Part::FeaturePython] Washer139  label="M4-Washer647"  # Fasteners workbench fastener (typed FeaturePython)
  Placement = pos=(416.001,10,86.0002) rot=(0,-1,0;1.5708rad)
  baseObject = -> Angle_Bracket_import04 [Edge19]
  diameter = 5
  invert = false
  matchOuter = false
  offset = 0
  type = 0
FEATURE [Part::FeaturePython] Screw196  label="M4x10-Screw280"  # Fasteners workbench fastener (typed FeaturePython)
  Placement = pos=(406.001,10,95.0997) rot=(1,0,0;3.14159rad)
  baseObject = -> Washer138 [Edge1]
  diameter = 4
  invert = false
  length = 2
  matchOuter = false
  offset = 0
  thread = false
  type = 5
FEATURE [Part::FeaturePython] Screw197  label="M4x10-Screw281"  # Fasteners workbench fastener (typed FeaturePython)
  Placement = pos=(415.101,10,86.0002) rot=(0,-1,0;1.5708rad)
  baseObject = -> Washer139 [Edge1]
  diameter = 4
  invert = false
  length = 2
  matchOuter = false
  offset = 0
  thread = false
  type = 5
FEATURE [Part::FeaturePython] Screw198  label="M4x10-Screw282"  # Fasteners workbench fastener (typed FeaturePython)
  Placement = pos=(430,33.9988,95.0997) rot=(1,0,0;3.14159rad)
  baseObject = -> Washer136 [Edge1]
  diameter = 4
  invert = false
  length = 2
  matchOuter = false
  offset = 0
  thread = false
  type = 5
FEATURE [Part::FeaturePython] Screw199  label="M4x10-Screw283"  # Fasteners workbench fastener (typed FeaturePython)
  Placement = pos=(430,24.8988,86.0002) rot=(-1,0,0;1.5708rad)
  baseObject = -> Washer137 [Edge1]
  diameter = 4
  invert = false
  length = 2
  matchOuter = false
  offset = 0
  thread = false
  type = 5
FEATURE [App::DocumentObjectGroup] Gruppe132  label="VR001"
  Group = -> [Hammermutter_B_Typ_Nut6_M4_import01106,Hammermutter_B_Typ_Nut6_M4_import01105,Hammermutter_B_Typ_Nut6_M4_import01101,Hammermutter_B_Typ_Nut6_M4_import01102,Washer136,Washer137,Washer138,Washer139,Screw196,Screw197,Screw198,Screw199]
FEATURE [Part::FeaturePython] Washer140  label="M4-Washer648"  # Fasteners workbench fastener (typed FeaturePython)
  Placement = pos=(406.001,10,124) rot=(0,0,1;0rad)
  baseObject = -> Angle_Bracket_import03 [Edge22]
  diameter = 5
  invert = false
  matchOuter = false
  offset = 0
  type = 0
FEATURE [Part::FeaturePython] Washer141  label="M4-Washer649"  # Fasteners workbench fastener (typed FeaturePython)
  Placement = pos=(416.001,10,134) rot=(0,-1,0;1.5708rad)
  baseObject = -> Angle_Bracket_import03 [Edge19]
  diameter = 5
  invert = false
  matchOuter = false
  offset = 0
  type = 0
FEATURE [Part::FeaturePython] Washer142  label="M4-Washer650"  # Fasteners workbench fastener (typed FeaturePython)
  Placement = pos=(430,23.9988,134) rot=(-1,0,0;1.5708rad)
  baseObject = -> Angle_Bracket_import05 [Edge19]
  diameter = 5
  invert = false
  matchOuter = false
  offset = 0
  type = 0
FEATURE [Part::FeaturePython] Washer143  label="M4-Washer651"  # Fasteners workbench fastener (typed FeaturePython)
  Placement = pos=(430,33.9988,124) rot=(0,0,1;0rad)
  baseObject = -> Angle_Bracket_import05 [Edge22]
  diameter = 5
  invert = false
  matchOuter = false
  offset = 0
  type = 0
FEATURE [Part::FeaturePython] Screw200  label="M4x10-Screw284"  # Fasteners workbench fastener (typed FeaturePython)
  Placement = pos=(415.101,10,134) rot=(0,-1,0;1.5708rad)
  baseObject = -> Washer141 [Edge1]
  diameter = 4
  invert = false
  length = 2
  matchOuter = false
  offset = 0
  thread = false
  type = 5
FEATURE [Part::FeaturePython] Screw201  label="M4x10-Screw285"  # Fasteners workbench fastener (typed FeaturePython)
  Placement = pos=(406.001,10,124.9) rot=(0,0,1;0rad)
  baseObject = -> Washer140 [Edge1]
  diameter = 4
  invert = false
  length = 2
  matchOuter = false
  offset = 0
  thread = false
  type = 5
FEATURE [Part::FeaturePython] Screw202  label="M4x10-Screw286"  # Fasteners workbench fastener (typed FeaturePython)
  Placement = pos=(430,24.8988,134) rot=(-1,0,0;1.5708rad)
  baseObject = -> Washer142 [Edge1]
  diameter = 4
  invert = false
  length = 2
  matchOuter = false
  offset = 0
  thread = false
  type = 5
FEATURE [Part::FeaturePython] Screw203  label="M4x10-Screw287"  # Fasteners workbench fastener (typed FeaturePython)
  Placement = pos=(430,33.9988,124.9) rot=(0,0,1;0rad)
  baseObject = -> Washer143 [Edge1]
  diameter = 4
  invert = false
  length = 2
  matchOuter = false
  offset = 0
  thread = false
  type = 5
FEATURE [App::DocumentObjectGroup] Gruppe133  label="HR002"
  Group = -> [Hammermutter_B_Typ_Nut6_M4_import01126,Hammermutter_B_Typ_Nut6_M4_import01125,Hammermutter_B_Typ_Nut6_M4_import01119,Hammermutter_B_Typ_Nut6_M4_import01120,Washer140,Washer141,Washer142,Washer143,Screw200,Screw201,Screw202,Screw203]
FEATURE [Part::FeaturePython] Washer144  label="M4-Washer652"  # Fasteners workbench fastener (typed FeaturePython)
  Placement = pos=(33.9988,10,124) rot=(0,0,1;0rad)
  baseObject = -> Angle_Bracket_import01 [Edge22]
  diameter = 5
  invert = false
  matchOuter = false
  offset = 0
  type = 0
FEATURE [Part::FeaturePython] Washer145  label="M4-Washer653"  # Fasteners workbench fastener (typed FeaturePython)
  Placement = pos=(23.9988,10,134) rot=(0,1,0;1.5708rad)
  baseObject = -> Angle_Bracket_import01 [Edge19]
  diameter = 5
  invert = false
  matchOuter = false
  offset = 0
  type = 0
FEATURE [Part::FeaturePython] Washer146  label="M4-Washer654"  # Fasteners workbench fastener (typed FeaturePython)
  Placement = pos=(10,23.9988,134) rot=(-1,0,0;1.5708rad)
  baseObject = -> Angle_Bracket_import15 [Edge19]
  diameter = 5
  invert = false
  matchOuter = false
  offset = 0
  type = 0
FEATURE [Part::FeaturePython] Washer147  label="M4-Washer655"  # Fasteners workbench fastener (typed FeaturePython)
  Placement = pos=(10,33.9988,124) rot=(0,0,1;0rad)
  baseObject = -> Angle_Bracket_import15 [Edge22]
  diameter = 5
  invert = false
  matchOuter = false
  offset = 0
  type = 0
FEATURE [Part::FeaturePython] Screw204  label="M4x10-Screw288"  # Fasteners workbench fastener (typed FeaturePython)
  Placement = pos=(33.9988,10,124.9) rot=(0,0,1;0rad)
  baseObject = -> Washer144 [Edge1]
  diameter = 4
  invert = false
  length = 2
  matchOuter = false
  offset = 0
  thread = false
  type = 5
FEATURE [Part::FeaturePython] Screw205  label="M4x10-Screw289"  # Fasteners workbench fastener (typed FeaturePython)
  Placement = pos=(24.8988,10,134) rot=(0,1,0;1.5708rad)
  baseObject = -> Washer145 [Edge1]
  diameter = 4
  invert = false
  length = 2
  matchOuter = false
  offset = 0
  thread = false
  type = 5
FEATURE [Part::FeaturePython] Screw206  label="M4x10-Screw290"  # Fasteners workbench fastener (typed FeaturePython)
  Placement = pos=(10,24.8988,134) rot=(-1,0,0;1.5708rad)
  baseObject = -> Washer146 [Edge1]
  diameter = 4
  invert = false
  length = 2
  matchOuter = false
  offset = 0
  thread = false
  type = 5
FEATURE [Part::FeaturePython] Screw207  label="M4x10-Screw291"  # Fasteners workbench fastener (typed FeaturePython)
  Placement = pos=(10,33.9988,124.9) rot=(0,0,1;0rad)
  baseObject = -> Washer147 [Edge1]
  diameter = 4
  invert = false
  length = 2
  matchOuter = false
  offset = 0
  thread = false
  type = 5
FEATURE [App::DocumentObjectGroup] Gruppe134  label="HL002"
  Group = -> [Hammermutter_B_Typ_Nut6_M4_import01116,Hammermutter_B_Typ_Nut6_M4_import01127,Hammermutter_B_Typ_Nut6_M4_import01128,Hammermutter_B_Typ_Nut6_M4_import01113,Washer144,Washer145,Washer146,Washer147,Screw204,Screw205,Screw206,Screw207]
FEATURE [Part::FeaturePython] Washer148  label="M4-Washer656"  # Fasteners workbench fastener (typed FeaturePython)
  Placement = pos=(33.9988,430,124) rot=(0,0,1;0rad)
  baseObject = -> Angle_Bracket_import09 [Edge22]
  diameter = 5
  invert = false
  matchOuter = false
  offset = 0
  type = 0
FEATURE [Part::FeaturePython] Washer149  label="M4-Washer657"  # Fasteners workbench fastener (typed FeaturePython)
  Placement = pos=(23.9988,430,134) rot=(0,1,0;1.5708rad)
  baseObject = -> Angle_Bracket_import09 [Edge19]
  diameter = 5
  invert = false
  matchOuter = false
  offset = 0
  type = 0
FEATURE [Part::FeaturePython] Washer150  label="M4-Washer658"  # Fasteners workbench fastener (typed FeaturePython)
  Placement = pos=(10,406.001,124) rot=(0,0,1;0rad)
  baseObject = -> Angle_Bracket_import13 [Edge22]
  diameter = 5
  invert = false
  matchOuter = false
  offset = 0
  type = 0
FEATURE [Part::FeaturePython] Washer151  label="M4-Washer659"  # Fasteners workbench fastener (typed FeaturePython)
  Placement = pos=(10,416.001,134) rot=(1,0,0;1.5708rad)
  baseObject = -> Angle_Bracket_import13 [Edge19]
  diameter = 5
  invert = false
  matchOuter = false
  offset = 0
  type = 0
FEATURE [Part::FeaturePython] Screw208  label="M4x10-Screw292"  # Fasteners workbench fastener (typed FeaturePython)
  Placement = pos=(10,406.001,124.9) rot=(0,0,1;0rad)
  baseObject = -> Washer150 [Edge1]
  diameter = 4
  invert = false
  length = 2
  matchOuter = false
  offset = 0
  thread = false
  type = 5
FEATURE [Part::FeaturePython] Screw209  label="M4x10-Screw293"  # Fasteners workbench fastener (typed FeaturePython)
  Placement = pos=(10,415.101,134) rot=(1,0,0;1.5708rad)
  baseObject = -> Washer151 [Edge1]
  diameter = 4
  invert = false
  length = 2
  matchOuter = false
  offset = 0
  thread = false
  type = 5
FEATURE [Part::FeaturePython] Screw210  label="M4x10-Screw294"  # Fasteners workbench fastener (typed FeaturePython)
  Placement = pos=(24.8988,430,134) rot=(0,1,0;1.5708rad)
  baseObject = -> Washer149 [Edge1]
  diameter = 4
  invert = false
  length = 2
  matchOuter = false
  offset = 0
  thread = false
  type = 5
FEATURE [Part::FeaturePython] Screw211  label="M4x10-Screw295"  # Fasteners workbench fastener (typed FeaturePython)
  Placement = pos=(33.9988,430,124.9) rot=(0,0,1;0rad)
  baseObject = -> Washer148 [Edge1]
  diameter = 4
  invert = false
  length = 2
  matchOuter = false
  offset = 0
  thread = false
  type = 5
FEATURE [App::DocumentObjectGroup] Gruppe135  label="VL002"
  Group = -> [Hammermutter_B_Typ_Nut6_M4_import01114,Hammermutter_B_Typ_Nut6_M4_import01115,Hammermutter_B_Typ_Nut6_M4_import01123,Hammermutter_B_Typ_Nut6_M4_import01124,Washer148,Washer149,Washer150,Washer151,Screw208,Screw209,Screw210,Screw211]
FEATURE [Part::FeaturePython] Washer152  label="M4-Washer660"  # Fasteners workbench fastener (typed FeaturePython)
  Placement = pos=(430,406.001,124) rot=(0,0,1;0rad)
  baseObject = -> Angle_Bracket_import07 [Edge22]
  diameter = 5
  invert = false
  matchOuter = false
  offset = 0
  type = 0
FEATURE [Part::FeaturePython] Washer153  label="M4-Washer661"  # Fasteners workbench fastener (typed FeaturePython)
  Placement = pos=(430,416.001,134) rot=(1,0,0;1.5708rad)
  baseObject = -> Angle_Bracket_import07 [Edge19]
  diameter = 5
  invert = false
  matchOuter = false
  offset = 0
  type = 0
FEATURE [Part::FeaturePython] Washer154  label="M4-Washer662"  # Fasteners workbench fastener (typed FeaturePython)
  Placement = pos=(406.001,430,124) rot=(0,0,1;0rad)
  baseObject = -> Angle_Bracket_import11 [Edge22]
  diameter = 5
  invert = false
  matchOuter = false
  offset = 0
  type = 0
FEATURE [Part::FeaturePython] Washer155  label="M4-Washer663"  # Fasteners workbench fastener (typed FeaturePython)
  Placement = pos=(416.001,430,134) rot=(0,-1,0;1.5708rad)
  baseObject = -> Angle_Bracket_import11 [Edge19]
  diameter = 5
  invert = false
  matchOuter = false
  offset = 0
  type = 0
FEATURE [Part::FeaturePython] Screw212  label="M4x10-Screw296"  # Fasteners workbench fastener (typed FeaturePython)
  Placement = pos=(430,406.001,124.9) rot=(0,0,1;0rad)
  baseObject = -> Washer152 [Edge1]
  diameter = 4
  invert = false
  length = 2
  matchOuter = false
  offset = 0
  thread = false
  type = 5
FEATURE [Part::FeaturePython] Screw213  label="M4x10-Screw297"  # Fasteners workbench fastener (typed FeaturePython)
  Placement = pos=(430,415.101,134) rot=(1,0,0;1.5708rad)
  baseObject = -> Washer153 [Edge1]
  diameter = 4
  invert = false
  length = 2
  matchOuter = false
  offset = 0
  thread = false
  type = 5
FEATURE [Part::FeaturePython] Screw214  label="M4x10-Screw298"  # Fasteners workbench fastener (typed FeaturePython)
  Placement = pos=(406.001,430,124.9) rot=(0,0,1;0rad)
  baseObject = -> Washer154 [Edge1]
  diameter = 4
  invert = false
  length = 2
  matchOuter = false
  offset = 0
  thread = false
  type = 5
FEATURE [Part::FeaturePython] Screw215  label="M4x10-Screw299"  # Fasteners workbench fastener (typed FeaturePython)
  Placement = pos=(415.101,430,134) rot=(0,-1,0;1.5708rad)
  baseObject = -> Washer155 [Edge1]
  diameter = 4
  invert = false
  length = 2
  matchOuter = false
  offset = 0
  thread = false
  type = 5
FEATURE [App::DocumentObjectGroup] Gruppe136  label="VR002"
  Group = -> [Hammermutter_B_Typ_Nut6_M4_import01122,Hammermutter_B_Typ_Nut6_M4_import01121,Hammermutter_B_Typ_Nut6_M4_import01117,Hammermutter_B_Typ_Nut6_M4_import01118,Washer152,Washer153,Washer154,Washer155,Screw212,Screw213,Screw214,Screw215]
FEATURE [App::DocumentObjectGroup] Gruppe099  label="Zwischenboden002"
  Group = -> [Gruppe129,Gruppe130,Gruppe131,Gruppe132,Gruppe133,Gruppe134,Gruppe135,Gruppe136]
FEATURE [Part::FeaturePython] Washer156  label="M4-Washer672"  # Fasteners workbench fastener (typed FeaturePython)
  Placement = pos=(416,430,415.501) rot=(0,-1,0;1.5708rad)
  baseObject = -> Angle_Bracket_import026 [Edge22]
  diameter = 5
  invert = false
  matchOuter = false
  offset = 0
  type = 0
FEATURE [Part::FeaturePython] Washer157  label="M4-Washer673"  # Fasteners workbench fastener (typed FeaturePython)
  Placement = pos=(406,430,425.501) rot=(1,0,0;3.14159rad)
  baseObject = -> Angle_Bracket_import026 [Edge19]
  diameter = 5
  invert = false
  matchOuter = false
  offset = 0
  type = 0
FEATURE [Part::FeaturePython] Washer158  label="M4-Washer664"  # Fasteners workbench fastener (typed FeaturePython)
  Placement = pos=(430,416.001,415.5) rot=(1,0,0;1.5708rad)
  baseObject = -> Angle_Bracket_import019 [Edge19]
  diameter = 5
  invert = false
  matchOuter = false
  offset = 0
  type = 0
FEATURE [Part::FeaturePython] Washer159  label="M4-Washer665"  # Fasteners workbench fastener (typed FeaturePython)
  Placement = pos=(430,406.001,425.5) rot=(1,0,0;3.14159rad)
  baseObject = -> Angle_Bracket_import019 [Edge22]
  diameter = 5
  invert = false
  matchOuter = false
  offset = 0
  type = 0
FEATURE [Part::FeaturePython] Screw216  label="M4x10-Screw"  # Fasteners workbench fastener (typed FeaturePython)
  Placement = pos=(430,415.101,415.5) rot=(1,0,0;1.5708rad)
  baseObject = -> Washer158 [Edge1]
  diameter = 4
  invert = false
  length = 2
  matchOuter = false
  offset = 0
  thread = false
  type = 5
FEATURE [Part::FeaturePython] Screw217  label="M4x10-Screw300"  # Fasteners workbench fastener (typed FeaturePython)
  Placement = pos=(430,406.001,424.6) rot=(1,0,0;3.14159rad)
  baseObject = -> Washer159 [Edge1]
  diameter = 4
  invert = false
  length = 2
  matchOuter = false
  offset = 0
  thread = false
  type = 5
FEATURE [Part::FeaturePython] Screw218  label="M4x10-Screw307"  # Fasteners workbench fastener (typed FeaturePython)
  Placement = pos=(415.1,430,415.501) rot=(0,-1,0;1.5708rad)
  baseObject = -> Washer156 [Edge1]
  diameter = 4
  invert = false
  length = 2
  matchOuter = false
  offset = 0
  thread = false
  type = 5
FEATURE [Part::FeaturePython] Screw219  label="M4x10-Screw308"  # Fasteners workbench fastener (typed FeaturePython)
  Placement = pos=(406,430,424.601) rot=(1,0,0;3.14159rad)
  baseObject = -> Washer157 [Edge1]
  diameter = 4
  invert = false
  length = 2
  matchOuter = false
  offset = 0
  thread = false
  type = 5
FEATURE [App::DocumentObjectGroup] Gruppe125  label="HR"
  Group = -> [Hammermutter_B_Typ_Nut6_M4_import01075,Hammermutter_B_Typ_Nut6_M4_import01073,Washer156,Washer157,Screw218,Screw219]
FEATURE [Part::FeaturePython] Washer160  label="M4-Washer674"  # Fasteners workbench fastener (typed FeaturePython)
  Placement = pos=(33.9988,430,425.5) rot=(1,0,0;3.14159rad)
  baseObject = -> Angle_Bracket_import028 [Edge22]
  diameter = 5
  invert = false
  matchOuter = false
  offset = 0
  type = 0
FEATURE [Part::FeaturePython] Washer161  label="M4-Washer675"  # Fasteners workbench fastener (typed FeaturePython)
  Placement = pos=(23.9988,430,415.5) rot=(0,1,0;1.5708rad)
  baseObject = -> Angle_Bracket_import028 [Edge19]
  diameter = 5
  invert = false
  matchOuter = false
  offset = 0
  type = 0
FEATURE [Part::FeaturePython] Washer162  label="M4-Washer666"  # Fasteners workbench fastener (typed FeaturePython)
  Placement = pos=(10,416.001,415.5) rot=(1,0,0;1.5708rad)
  baseObject = -> Angle_Bracket_import017 [Edge19]
  diameter = 5
  invert = false
  matchOuter = false
  offset = 0
  type = 0
FEATURE [Part::FeaturePython] Washer163  label="M4-Washer667"  # Fasteners workbench fastener (typed FeaturePython)
  Placement = pos=(10,406.001,425.5) rot=(1,0,0;3.14159rad)
  baseObject = -> Angle_Bracket_import017 [Edge22]
  diameter = 5
  invert = false
  matchOuter = false
  offset = 0
  type = 0
FEATURE [Part::FeaturePython] Screw220  label="M4x10-Screw309"  # Fasteners workbench fastener (typed FeaturePython)
  Placement = pos=(33.9988,430,424.6) rot=(1,0,0;3.14159rad)
  baseObject = -> Washer160 [Edge1]
  diameter = 4
  invert = false
  length = 2
  matchOuter = false
  offset = 0
  thread = false
  type = 5
FEATURE [Part::FeaturePython] Screw221  label="M4x10-Screw310"  # Fasteners workbench fastener (typed FeaturePython)
  Placement = pos=(24.8988,430,415.5) rot=(0,1,0;1.5708rad)
  baseObject = -> Washer161 [Edge1]
  diameter = 4
  invert = false
  length = 2
  matchOuter = false
  offset = 0
  thread = false
  type = 5
FEATURE [App::DocumentObjectGroup] Gruppe126  label="HL"
  Group = -> [Hammermutter_B_Typ_Nut6_M4_import01077,Hammermutter_B_Typ_Nut6_M4_import01079,Washer160,Washer161,Screw220,Screw221]
FEATURE [Part::FeaturePython] Screw222  label="M4x10-Screw301"  # Fasteners workbench fastener (typed FeaturePython)
  Placement = pos=(10,415.101,415.5) rot=(1,0,0;1.5708rad)
  baseObject = -> Washer162 [Edge1]
  diameter = 4
  invert = false
  length = 2
  matchOuter = false
  offset = 0
  thread = false
  type = 5
FEATURE [Part::FeaturePython] Screw223  label="M4x10-Screw302"  # Fasteners workbench fastener (typed FeaturePython)
  Placement = pos=(10,406.001,424.6) rot=(1,0,0;3.14159rad)
  baseObject = -> Washer163 [Edge1]
  diameter = 4
  invert = false
  length = 2
  matchOuter = false
  offset = 0
  thread = false
  type = 5
FEATURE [Part::FeaturePython] Washer164  label="M4-Washer676"  # Fasteners workbench fastener (typed FeaturePython)
  Placement = pos=(33.9988,10,425.5) rot=(1,0,0;3.14159rad)
  baseObject = -> Angle_Bracket_import024 [Edge22]
  diameter = 5
  invert = false
  matchOuter = false
  offset = 0
  type = 0
FEATURE [Part::FeaturePython] Washer165  label="M4-Washer677"  # Fasteners workbench fastener (typed FeaturePython)
  Placement = pos=(23.9988,10,415.5) rot=(0,1,0;1.5708rad)
  baseObject = -> Angle_Bracket_import024 [Edge19]
  diameter = 5
  invert = false
  matchOuter = false
  offset = 0
  type = 0
FEATURE [Part::FeaturePython] Washer166  label="M4-Washer669"  # Fasteners workbench fastener (typed FeaturePython)
  Placement = pos=(10,23.9988,415.5) rot=(-1,0,0;1.5708rad)
  baseObject = -> Angle_Bracket_import018 [Edge19]
  diameter = 5
  invert = false
  matchOuter = false
  offset = 0
  type = 0
FEATURE [Part::FeaturePython] Washer167  label="M4-Washer668"  # Fasteners workbench fastener (typed FeaturePython)
  Placement = pos=(10,33.9988,425.5) rot=(1,0,0;3.14159rad)
  baseObject = -> Angle_Bracket_import018 [Edge22]
  diameter = 5
  invert = false
  matchOuter = false
  offset = 0
  type = 0
FEATURE [Part::FeaturePython] Screw224  label="M4x10-Screw303"  # Fasteners workbench fastener (typed FeaturePython)
  Placement = pos=(10,33.9988,424.6) rot=(1,0,0;3.14159rad)
  baseObject = -> Washer167 [Edge1]
  diameter = 4
  invert = false
  length = 2
  matchOuter = false
  offset = 0
  thread = false
  type = 5
FEATURE [Part::FeaturePython] Screw225  label="M4x10-Screw304"  # Fasteners workbench fastener (typed FeaturePython)
  Placement = pos=(10,24.8988,415.5) rot=(-1,0,0;1.5708rad)
  baseObject = -> Washer166 [Edge1]
  diameter = 4
  invert = false
  length = 2
  matchOuter = false
  offset = 0
  thread = false
  type = 5
FEATURE [Part::FeaturePython] Screw226  label="M4x10-Screw311"  # Fasteners workbench fastener (typed FeaturePython)
  Placement = pos=(24.8988,10,415.5) rot=(0,1,0;1.5708rad)
  baseObject = -> Washer165 [Edge1]
  diameter = 4
  invert = false
  length = 2
  matchOuter = false
  offset = 0
  thread = false
  type = 5
FEATURE [Part::FeaturePython] Screw227  label="M4x10-Screw312"  # Fasteners workbench fastener (typed FeaturePython)
  Placement = pos=(33.9988,10,424.6) rot=(1,0,0;3.14159rad)
  baseObject = -> Washer164 [Edge1]
  diameter = 4
  invert = false
  length = 2
  matchOuter = false
  offset = 0
  thread = false
  type = 5
FEATURE [App::DocumentObjectGroup] Gruppe127  label="VL"
  Group = -> [Hammermutter_B_Typ_Nut6_M4_import01069,Hammermutter_B_Typ_Nut6_M4_import01071,Washer164,Washer165,Screw226,Screw227]
FEATURE [Part::FeaturePython] Washer168  label="M4-Washer670"  # Fasteners workbench fastener (typed FeaturePython)
  Placement = pos=(430,33.9988,425.5) rot=(1,0,0;3.14159rad)
  baseObject = -> Angle_Bracket_import020 [Edge22]
  diameter = 5
  invert = false
  matchOuter = false
  offset = 0
  type = 0
FEATURE [Part::FeaturePython] Washer169  label="M4-Washer671"  # Fasteners workbench fastener (typed FeaturePython)
  Placement = pos=(430,23.9988,415.5) rot=(-1,0,0;1.5708rad)
  baseObject = -> Angle_Bracket_import020 [Edge19]
  diameter = 5
  invert = false
  matchOuter = false
  offset = 0
  type = 0
FEATURE [Part::FeaturePython] Washer170  label="M4-Washer678"  # Fasteners workbench fastener (typed FeaturePython)
  Placement = pos=(406.001,10,425.5) rot=(1,0,0;3.14159rad)
  baseObject = -> Angle_Bracket_import022 [Edge22]
  diameter = 5
  invert = false
  matchOuter = false
  offset = 0
  type = 0
FEATURE [Part::FeaturePython] Washer171  label="M4-Washer679"  # Fasteners workbench fastener (typed FeaturePython)
  Placement = pos=(416.001,10,415.5) rot=(0,-1,0;1.5708rad)
  baseObject = -> Angle_Bracket_import022 [Edge19]
  diameter = 5
  invert = false
  matchOuter = false
  offset = 0
  type = 0
FEATURE [Part::FeaturePython] Screw228  label="M4x10-Screw305"  # Fasteners workbench fastener (typed FeaturePython)
  Placement = pos=(430,33.9988,424.6) rot=(1,0,0;3.14159rad)
  baseObject = -> Washer168 [Edge1]
  diameter = 4
  invert = false
  length = 2
  matchOuter = false
  offset = 0
  thread = false
  type = 5
FEATURE [Part::FeaturePython] Screw229  label="M4x10-Screw306"  # Fasteners workbench fastener (typed FeaturePython)
  Placement = pos=(430,24.8988,415.5) rot=(-1,0,0;1.5708rad)
  baseObject = -> Washer169 [Edge1]
  diameter = 4
  invert = false
  length = 2
  matchOuter = false
  offset = 0
  thread = false
  type = 5
FEATURE [Part::FeaturePython] Screw230  label="M4x10-Screw313"  # Fasteners workbench fastener (typed FeaturePython)
  Placement = pos=(406.001,10,424.6) rot=(1,0,0;3.14159rad)
  baseObject = -> Washer170 [Edge1]
  diameter = 4
  invert = false
  length = 2
  matchOuter = false
  offset = 0
  thread = false
  type = 5
FEATURE [Part::FeaturePython] Screw231  label="M4x10-Screw314"  # Fasteners workbench fastener (typed FeaturePython)
  Placement = pos=(415.101,10,415.5) rot=(0,-1,0;1.5708rad)
  baseObject = -> Washer171 [Edge1]
  diameter = 4
  invert = false
  length = 2
  matchOuter = false
  offset = 0
  thread = false
  type = 5
FEATURE [App::DocumentObjectGroup] Gruppe128  label="VR"
  Group = -> [Hammermutter_B_Typ_Nut6_M4_import01066,Hammermutter_B_Typ_Nut6_M4_import01065,Washer170,Washer171,Screw230,Screw231]
FEATURE [Part::FeaturePython] Washer172  label="M4-Washer680"  # Fasteners workbench fastener (typed FeaturePython)
  Placement = pos=(416,243.999,110) rot=(0,-1,0;1.5708rad)
  baseObject = -> Angle_Bracket_import030 [Edge22]
  diameter = 5
  invert = false
  matchOuter = false
  offset = 0
  type = 0
FEATURE [Part::FeaturePython] Washer173  label="M4-Washer681"  # Fasteners workbench fastener (typed FeaturePython)
  Placement = pos=(406,233.999,110) rot=(-1,0,0;1.5708rad)
  baseObject = -> Angle_Bracket_import030 [Edge19]
  diameter = 5
  invert = false
  matchOuter = false
  offset = 0
  type = 0
FEATURE [Part::FeaturePython] Washer174  label="M4-Washer682"  # Fasteners workbench fastener (typed FeaturePython)
  Placement = pos=(406.001,206,110) rot=(1,0,0;1.5708rad)
  baseObject = -> Angle_Bracket_import029 [Edge22]
  diameter = 5
  invert = false
  matchOuter = false
  offset = 0
  type = 0
FEATURE [Part::FeaturePython] Washer175  label="M4-Washer683"  # Fasteners workbench fastener (typed FeaturePython)
  Placement = pos=(416.001,196,110) rot=(0,-1,0;1.5708rad)
  baseObject = -> Angle_Bracket_import029 [Edge19]
  diameter = 5
  invert = false
  matchOuter = false
  offset = 0
  type = 0
FEATURE [Part::FeaturePython] Screw232  label="M4x10-Screw315"  # Fasteners workbench fastener (typed FeaturePython)
  Placement = pos=(415.101,196,110) rot=(0,-1,0;1.5708rad)
  baseObject = -> Washer175 [Edge1]
  diameter = 4
  invert = false
  length = 2
  matchOuter = false
  offset = 0
  thread = false
  type = 5
FEATURE [Part::FeaturePython] Screw233  label="M4x10-Screw316"  # Fasteners workbench fastener (typed FeaturePython)
  Placement = pos=(406.001,205.1,110) rot=(1,0,0;1.5708rad)
  baseObject = -> Washer174 [Edge1]
  diameter = 4
  invert = false
  length = 2
  matchOuter = false
  offset = 0
  thread = false
  type = 5
FEATURE [Part::FeaturePython] Screw234  label="M4x10-Screw317"  # Fasteners workbench fastener (typed FeaturePython)
  Placement = pos=(406,234.899,110) rot=(-1,0,0;1.5708rad)
  baseObject = -> Washer173 [Edge1]
  diameter = 4
  invert = false
  length = 2
  matchOuter = false
  offset = 0
  thread = false
  type = 5
FEATURE [Part::FeaturePython] Screw235  label="M4x10-Screw318"  # Fasteners workbench fastener (typed FeaturePython)
  Placement = pos=(415.1,243.999,110) rot=(0,-1,0;1.5708rad)
  baseObject = -> Washer172 [Edge1]
  diameter = 4
  invert = false
  length = 2
  matchOuter = false
  offset = 0
  thread = false
  type = 5
FEATURE [App::DocumentObjectGroup] Gruppe137  label="V"
  Group = -> [Hammermutter_B_Typ_Nut6_M4_import01089,Hammermutter_B_Typ_Nut6_M4_import01088,Hammermutter_B_Typ_Nut6_M4_import01087,Hammermutter_B_Typ_Nut6_M4_import01086,Washer172,Washer173,Washer174,Washer175,Screw232,Screw233,Screw234,Screw235]
FEATURE [Part::FeaturePython] Washer176  label="M4-Washer684"  # Fasteners workbench fastener (typed FeaturePython)
  Placement = pos=(23.9988,244,110) rot=(0,1,0;1.5708rad)
  baseObject = -> Angle_Bracket_import032 [Edge19]
  diameter = 5
  invert = false
  matchOuter = false
  offset = 0
  type = 0
FEATURE [Part::FeaturePython] Washer177  label="M4-Washer685"  # Fasteners workbench fastener (typed FeaturePython)
  Placement = pos=(33.9988,234,110) rot=(-1,0,0;1.5708rad)
  baseObject = -> Angle_Bracket_import032 [Edge22]
  diameter = 5
  invert = false
  matchOuter = false
  offset = 0
  type = 0
FEATURE [Part::FeaturePython] Washer178  label="M4-Washer686"  # Fasteners workbench fastener (typed FeaturePython)
  Placement = pos=(33.9988,206,110) rot=(1,0,0;1.5708rad)
  baseObject = -> Angle_Bracket_import031 [Edge22]
  diameter = 5
  invert = false
  matchOuter = false
  offset = 0
  type = 0
FEATURE [Part::FeaturePython] Washer179  label="M4-Washer687"  # Fasteners workbench fastener (typed FeaturePython)
  Placement = pos=(23.9988,196,110) rot=(0,1,0;1.5708rad)
  baseObject = -> Angle_Bracket_import031 [Edge19]
  diameter = 5
  invert = false
  matchOuter = false
  offset = 0
  type = 0
FEATURE [Part::FeaturePython] Screw236  label="M4x10-Screw319"  # Fasteners workbench fastener (typed FeaturePython)
  Placement = pos=(24.8988,196,110) rot=(0,1,0;1.5708rad)
  baseObject = -> Washer179 [Edge1]
  diameter = 4
  invert = false
  length = 2
  matchOuter = false
  offset = 0
  thread = false
  type = 5
FEATURE [Part::FeaturePython] Screw237  label="M4x10-Screw320"  # Fasteners workbench fastener (typed FeaturePython)
  Placement = pos=(33.9988,205.1,110) rot=(1,0,0;1.5708rad)
  baseObject = -> Washer178 [Edge1]
  diameter = 4
  invert = false
  length = 2
  matchOuter = false
  offset = 0
  thread = false
  type = 5
FEATURE [Part::FeaturePython] Screw238  label="M4x10-Screw321"  # Fasteners workbench fastener (typed FeaturePython)
  Placement = pos=(33.9988,234.9,110) rot=(-1,0,0;1.5708rad)
  baseObject = -> Washer177 [Edge1]
  diameter = 4
  invert = false
  length = 2
  matchOuter = false
  offset = 0
  thread = false
  type = 5
FEATURE [Part::FeaturePython] Screw239  label="M4x10-Screw322"  # Fasteners workbench fastener (typed FeaturePython)
  Placement = pos=(24.8988,244,110) rot=(0,1,0;1.5708rad)
  baseObject = -> Washer176 [Edge1]
  diameter = 4
  invert = false
  length = 2
  matchOuter = false
  offset = 0
  thread = false
  type = 5
FEATURE [App::DocumentObjectGroup] Gruppe138  label="H"
  Group = -> [Hammermutter_B_Typ_Nut6_M4_import01085,Hammermutter_B_Typ_Nut6_M4_import01084,Hammermutter_B_Typ_Nut6_M4_import01082,Hammermutter_B_Typ_Nut6_M4_import01083,Washer176,Washer177,Washer178,Washer179,Screw236,Screw237,Screw238,Screw239]
FEATURE [App::DocumentObjectGroup] Gruppe113  label="z-Axis-Mounting001"
  Group = -> [Gruppe137,Gruppe138]
FEATURE [Part::FeaturePython] motor_block_bottom_topM_01  # a2plus imported part (geometry in sourceFile) (typed FeaturePython)
  Placement = pos=(440,378,449.5) rot=(0,1,0;3.14159rad)
  fixedPosition = false
  sourceFile = <userpath>/CloudStation/Hobbyprojekte/3D Drucker/CoreXY/Assembly/Parts/Printed Parts/motor-block-bottom-topM.FCStd
  timeLastImport = 1458321684
  updateColors = true
FEATURE [App::DocumentObjectGroup] Gruppe017  label="Main Parts"
  Group = -> [NEMA_17_Stepper_Motor_40mm_with_connector_import01,motor_block_topM_01,motor_block_bottom_topM_01]
FEATURE [Part::FeaturePython] Washer180  label="M4-Washer688"  # Fasteners workbench fastener (typed FeaturePython)
  Placement = pos=(383.5,418,484.5) rot=(0,0,1;0rad)
  baseObject = -> motor_block_topM_01 [Edge27]
  diameter = 5
  invert = true
  matchOuter = false
  offset = 0
  type = 0
FEATURE [Part::FeaturePython] Washer181  label="M4-Washer689"  # Fasteners workbench fastener (typed FeaturePython)
  Placement = pos=(430,408,484.5) rot=(1,0,0;3.14159rad)
  baseObject = -> motor_block_topM_01 [Edge33]
  diameter = 5
  invert = true
  matchOuter = false
  offset = 0
  type = 0
FEATURE [Part::FeaturePython] Washer182  label="M4-Washer690"  # Fasteners workbench fastener (typed FeaturePython)
  Placement = pos=(340.5,414.5,484.5) rot=(0,0,1;0rad)
  baseObject = -> motor_block_topM_01 [Edge21]
  diameter = 5
  invert = true
  matchOuter = false
  offset = 0
  type = 0
FEATURE [Part::FeaturePython] Washer183  label="M4-Washer429"  # Fasteners workbench fastener (typed FeaturePython)
  Placement = pos=(383.5,418,449.5) rot=(1,0,0;3.14159rad)
  baseObject = -> motor_block_bottom_topM_01 [Edge33]
  diameter = 5
  invert = false
  matchOuter = false
  offset = 0
  type = 0
FEATURE [Part::FeaturePython] Washer184  label="M4-Washer430"  # Fasteners workbench fastener (typed FeaturePython)
  Placement = pos=(407,413,449.5) rot=(1,0,0;3.14159rad)
  baseObject = -> motor_block_bottom_topM_01 [Edge23]
  diameter = 5
  invert = false
  matchOuter = false
  offset = 0
  type = 0
FEATURE [Part::FeaturePython] Washer185  label="M4-Washer431"  # Fasteners workbench fastener (typed FeaturePython)
  Placement = pos=(402,388,449.5) rot=(1,0,0;3.14159rad)
  baseObject = -> motor_block_bottom_topM_01 [Edge24]
  diameter = 5
  invert = false
  matchOuter = false
  offset = 0
  type = 0
FEATURE [Part::FeaturePython] Washer186  label="M4-Washer691"  # Fasteners workbench fastener (typed FeaturePython)
  Placement = pos=(383.5,417.7,468) rot=(1,0,0;3.14159rad)
  baseObject = -> DIN625_1_624_ZZ_import01004 [Edge29]
  diameter = 5
  invert = false
  matchOuter = false
  offset = 0
  type = 0
FEATURE [Part::FeaturePython] Washer187  label="M4-Washer618"  # Fasteners workbench fastener (typed FeaturePython)
  Placement = pos=(402,388,467.9) rot=(1,0,0;3.14159rad)
  baseObject = -> F624zz_import018 [Edge8]
  diameter = 5
  invert = true
  matchOuter = false
  offset = 0
  type = 0
FEATURE [Part::FeaturePython] Washer188  label="M4-Washer692"  # Fasteners workbench fastener (typed FeaturePython)
  Placement = pos=(402,388,479.8) rot=(1,0,0;3.14159rad)
  baseObject = -> motor_block_topM_01 [Edge64]
  diameter = 5
  invert = true
  matchOuter = false
  offset = 0
  type = 0
FEATURE [Part::FeaturePython] Washer189  label="M4-Washer693"  # Fasteners workbench fastener (typed FeaturePython)
  Placement = pos=(383.5,418,479.8) rot=(1,0,0;3.14159rad)
  baseObject = -> motor_block_topM_01 [Edge67]
  diameter = 5
  invert = true
  matchOuter = false
  offset = 0
  type = 0
FEATURE [Part::FeaturePython] Washer190  label="M4-Washer436"  # Fasteners workbench fastener (typed FeaturePython)
  Placement = pos=(407,413,469.367) rot=(1,0,0;3.14159rad)
  baseObject = -> GT2Bearing_007 [Edge381]
  diameter = 5
  invert = true
  matchOuter = false
  offset = 0
  type = 2
FEATURE [Part::FeaturePython] Washer191  label="M4-Washer694"  # Fasteners workbench fastener (typed FeaturePython)
  Placement = pos=(407,413,479.8) rot=(1,0,0;3.14159rad)
  baseObject = -> motor_block_topM_01 [Edge72]
  diameter = 5
  invert = true
  matchOuter = false
  offset = 0
  type = 2
FEATURE [Part::FeaturePython] Screw247  label="M4x40-Screw"  # Fasteners workbench fastener (typed FeaturePython)
  Placement = pos=(340.5,414.5,485.4) rot=(0,0,1;0rad)
  baseObject = -> Washer182 [Edge1]
  diameter = 5
  invert = false
  length = 11
  matchOuter = false
  offset = 0
  thread = false
  type = 6
FEATURE [Part::FeaturePython] Screw248  label="M4x40-Screw041"  # Fasteners workbench fastener (typed FeaturePython)
  Placement = pos=(430,408,483.6) rot=(1,0,0;3.14159rad)
  baseObject = -> Washer181 [Edge1]
  diameter = 5
  invert = false
  length = 11
  matchOuter = false
  offset = 0
  thread = false
  type = 6
FEATURE [Part::FeaturePython] Screw249  label="M4x40-Screw042"  # Fasteners workbench fastener (typed FeaturePython)
  Placement = pos=(383.5,418,485.4) rot=(0,0,1;0rad)
  baseObject = -> Washer180 [Edge1]
  diameter = 5
  invert = false
  length = 11
  matchOuter = false
  offset = 0
  thread = false
  type = 6
FEATURE [Part::FeaturePython] Nut041  label="M4-Nut035"  # Fasteners workbench fastener (typed FeaturePython)
  Placement = pos=(383.5,418,448.6) rot=(1,0,0;3.14159rad)
  baseObject = -> Washer183 [Edge1]
  diameter = 6
  invert = false
  matchOuter = false
  offset = 0
  thread = false
  type = 1
FEATURE [Part::FeaturePython] Nut042  label="M4-Nut036"  # Fasteners workbench fastener (typed FeaturePython)
  Placement = pos=(407,413,448.6) rot=(1,0,0;3.14159rad)
  baseObject = -> Washer184 [Edge1]
  diameter = 6
  invert = false
  matchOuter = false
  offset = 0
  thread = false
  type = 1
FEATURE [Part::FeaturePython] Nut043  label="M4-Nut037"  # Fasteners workbench fastener (typed FeaturePython)
  Placement = pos=(402,388,448.6) rot=(1,0,0;3.14159rad)
  baseObject = -> Washer185 [Edge1]
  diameter = 6
  invert = false
  matchOuter = false
  offset = 0
  thread = false
  type = 1
FEATURE [Part::FeaturePython] Screw250  label="M3x16-Screw"  # Fasteners workbench fastener (typed FeaturePython)
  Placement = pos=(385,383,457.5) rot=(1,0,0;3.14159rad)
  baseObject = -> motor_block_bottom_topM_01 [Edge141]
  diameter = 3
  invert = false
  length = 5
  matchOuter = false
  offset = 0
  thread = false
  type = 5
FEATURE [Part::FeaturePython] Screw251  label="M3x30-Screw"  # Fasteners workbench fastener (typed FeaturePython)
  Placement = pos=(371.5,414.5,457.5) rot=(1,0,0;3.14159rad)
  baseObject = -> motor_block_bottom_topM_01 [Edge145]
  diameter = 3
  invert = false
  length = 8
  matchOuter = false
  offset = 0
  thread = false
  type = 5
FEATURE [Part::FeaturePython] Screw252  label="M3x30-Screw022"  # Fasteners workbench fastener (typed FeaturePython)
  Placement = pos=(371.5,383.5,457.5) rot=(1,0,0;3.14159rad)
  baseObject = -> motor_block_bottom_topM_01 [Edge143]
  diameter = 3
  invert = false
  length = 8
  matchOuter = false
  offset = 0
  thread = false
  type = 5
FEATURE [Part::FeaturePython] Screw253  label="M3x30-Screw023"  # Fasteners workbench fastener (typed FeaturePython)
  Placement = pos=(340.5,414.5,457.5) rot=(1,0,0;3.14159rad)
  baseObject = -> motor_block_bottom_topM_01 [Edge146]
  diameter = 3
  invert = false
  length = 8
  matchOuter = false
  offset = 0
  thread = false
  type = 5
FEATURE [Part::FeaturePython] Screw254  label="M3x30-Screw024"  # Fasteners workbench fastener (typed FeaturePython)
  Placement = pos=(340.5,383.5,457.5) rot=(1,0,0;3.14159rad)
  baseObject = -> motor_block_bottom_topM_01 [Edge128]
  diameter = 3
  invert = false
  length = 8
  matchOuter = false
  offset = 0
  thread = false
  type = 5
FEATURE [Part::FeaturePython] Screw255  label="M4x30-Screw"  # Fasteners workbench fastener (typed FeaturePython)
  Placement = pos=(430,393,475.3) rot=(0,0,1;0rad)
  baseObject = -> motor_block_topM_01 [Edge136]
  diameter = 4
  invert = false
  length = 7
  matchOuter = false
  offset = 0
  thread = false
  type = 5
FEATURE [Part::FeaturePython] Screw256  label="M4x30-Screw060"  # Fasteners workbench fastener (typed FeaturePython)
  Placement = pos=(430,408,475.3) rot=(0,0,1;0rad)
  baseObject = -> motor_block_topM_01 [Edge138]
  diameter = 4
  invert = false
  length = 7
  matchOuter = false
  offset = 0
  thread = false
  type = 5
FEATURE [Part::FeaturePython] Screw257  label="M4x30-Screw061"  # Fasteners workbench fastener (typed FeaturePython)
  Placement = pos=(346,430,475.3) rot=(0,0,1;0rad)
  baseObject = -> motor_block_topM_01 [Edge141]
  diameter = 4
  invert = false
  length = 7
  matchOuter = false
  offset = 0
  thread = false
  type = 5
FEATURE [Part::FeaturePython] Screw258  label="M4x30-Screw062"  # Fasteners workbench fastener (typed FeaturePython)
  Placement = pos=(398,430,475.3) rot=(0,0,1;0rad)
  baseObject = -> motor_block_topM_01 [Edge142]
  diameter = 4
  invert = false
  length = 7
  matchOuter = false
  offset = 0
  thread = false
  type = 5
FEATURE [App::DocumentObjectGroup] Gruppe011  label="Screws"
  Group = -> [DIN7965___Schraubeinsatz___M3_import01,Hammermutter_B_Typ_Nut6_M4_import01003,Hammermutter_B_Typ_Nut6_M4_import01002,Hammermutter_B_Typ_Nut6_M4_import01,Hammermutter_B_Typ_Nut6_M4_import01001,Washer180,Washer181,Washer182,Washer183,Washer184,Washer185,Washer186,Washer187,Washer188,Washer189,Washer190,Washer191,Screw247,Screw248,Screw249,Nut041,Nut042,Nut043,Screw250,Screw251,Screw252,Screw253,+5 more]
FEATURE [App::DocumentObjectGroup] Gruppe009  label="Right Motor"
  Group = -> [Gruppe010,Gruppe011,Gruppe012,Gruppe017]
FEATURE [Part::FeaturePython] motor_block_bottom_mirrored_topM_01001  # a2plus imported part (geometry in sourceFile) (typed FeaturePython)
  Placement = pos=(-1.6e-10,378,449.5) rot=(0,1,0;3.14159rad)
  fixedPosition = false
  sourceFile = <userpath>/CloudStation/Hobbyprojekte/3D Drucker/CoreXY/Assembly/Parts/Printed Parts/motor-block-bottom-mirrored-topM.FCStd
  timeLastImport = 1458323372
  updateColors = true
FEATURE [App::DocumentObjectGroup] Gruppe018  label="Main Parts001"
  Group = -> [NEMA_17_Stepper_Motor_40mm_with_connector_import002,motor_block_mirrored_topM_01,motor_block_bottom_mirrored_topM_01001]
FEATURE [Part::FeaturePython] Washer204  label="M4-Washer453"  # Fasteners workbench fastener (typed FeaturePython)
  Placement = pos=(56.5,403,484.5) rot=(0,0,1;0rad)
  baseObject = -> motor_block_mirrored_topM_01 [Edge24]
  diameter = 5
  invert = false
  matchOuter = false
  offset = 0
  type = 0
FEATURE [Part::FeaturePython] Washer205  label="M4-Washer454"  # Fasteners workbench fastener (typed FeaturePython)
  Placement = pos=(38,388,484.5) rot=(0,0,1;0rad)
  baseObject = -> motor_block_mirrored_topM_01 [Edge21]
  diameter = 5
  invert = false
  matchOuter = false
  offset = 0
  type = 0
FEATURE [Part::FeaturePython] Washer206  label="M4-Washer455"  # Fasteners workbench fastener (typed FeaturePython)
  Placement = pos=(33,413,484.5) rot=(0,0,1;0rad)
  baseObject = -> motor_block_mirrored_topM_01 [Edge33]
  diameter = 5
  invert = false
  matchOuter = false
  offset = 0
  type = 0
FEATURE [Part::FeaturePython] Washer207  label="M4-Washer459"  # Fasteners workbench fastener (typed FeaturePython)
  Placement = pos=(56.5,403,449.5) rot=(1,0,0;3.14159rad)
  baseObject = -> motor_block_bottom_mirrored_topM_01001 [Edge30]
  diameter = 5
  invert = true
  matchOuter = false
  offset = 0
  type = 0
FEATURE [Part::FeaturePython] Washer208  label="M4-Washer460"  # Fasteners workbench fastener (typed FeaturePython)
  Placement = pos=(33,413,449.5) rot=(1,0,0;3.14159rad)
  baseObject = -> motor_block_bottom_mirrored_topM_01001 [Edge23]
  diameter = 5
  invert = true
  matchOuter = false
  offset = 0
  type = 0
FEATURE [Part::FeaturePython] Washer209  label="M4-Washer461"  # Fasteners workbench fastener (typed FeaturePython)
  Placement = pos=(38,388,449.5) rot=(1,0,0;3.14159rad)
  baseObject = -> motor_block_bottom_mirrored_topM_01001 [Edge24]
  diameter = 5
  invert = true
  matchOuter = false
  offset = 0
  type = 0
FEATURE [Part::FeaturePython] Washer210  label="M4-Washer695"  # Fasteners workbench fastener (typed FeaturePython)
  Placement = pos=(56.5,403,459.3) rot=(1,0,0;3.14159rad)
  baseObject = -> DIN625_1_624_ZZ_import01024 [Edge29]
  diameter = 5
  invert = false
  matchOuter = false
  offset = 0
  type = 0
FEATURE [Part::FeaturePython] Washer211  label="M4-Washer712"  # Fasteners workbench fastener (typed FeaturePython)
  Placement = pos=(38,388,459.3) rot=(-1,0,0;3.14159rad)
  baseObject = -> F624zz_import019 [Edge8]
  diameter = 5
  invert = true
  matchOuter = false
  offset = 0
  type = 0
FEATURE [Part::FeaturePython] Washer212  label="M4-Washer697"  # Fasteners workbench fastener (typed FeaturePython)
  Placement = pos=(56.5,403,469.3) rot=(0,0,1;0rad)
  baseObject = -> DIN625_1_624_ZZ_import01025 [Edge28]
  diameter = 5
  invert = true
  matchOuter = false
  offset = 0
  type = 0
FEATURE [Part::FeaturePython] Washer213  label="M4-Washer698"  # Fasteners workbench fastener (typed FeaturePython)
  Placement = pos=(38,388,469.3) rot=(0,0,1;0rad)
  baseObject = -> DIN625_1_624_ZZ_import01023 [Edge29]
  diameter = 5
  invert = false
  matchOuter = false
  offset = 0
  type = 0
FEATURE [Part::FeaturePython] Washer214  label="M4-Washer466"  # Fasteners workbench fastener (typed FeaturePython)
  Placement = pos=(33,413,468.807) rot=(0,0,1;0rad)
  baseObject = -> GT2Bearing_008 [Edge590]
  diameter = 5
  invert = false
  matchOuter = false
  offset = 0
  type = 2
FEATURE [Part::FeaturePython] Washer215  label="M4-Washer467"  # Fasteners workbench fastener (typed FeaturePython)
  Placement = pos=(33,413,459.807) rot=(1,0,0;3.14159rad)
  baseObject = -> GT2Bearing_008 [Edge325]
  diameter = 5
  invert = false
  matchOuter = false
  offset = 0
  type = 2
FEATURE [Part::FeaturePython] Nut044  label="M4-Nut038"  # Fasteners workbench fastener (typed FeaturePython)
  Placement = pos=(56.5,403,448.6) rot=(1,0,0;3.14159rad)
  baseObject = -> Washer207 [Edge1]
  diameter = 6
  invert = false
  matchOuter = false
  offset = 0
  thread = false
  type = 1
FEATURE [Part::FeaturePython] Nut045  label="M4-Nut039"  # Fasteners workbench fastener (typed FeaturePython)
  Placement = pos=(38,388,448.6) rot=(1,0,0;3.14159rad)
  baseObject = -> Washer209 [Edge1]
  diameter = 6
  invert = false
  matchOuter = false
  offset = 0
  thread = false
  type = 1
FEATURE [Part::FeaturePython] Nut046  label="M4-Nut040"  # Fasteners workbench fastener (typed FeaturePython)
  Placement = pos=(33,413,448.6) rot=(1,0,0;3.14159rad)
  baseObject = -> Washer208 [Edge1]
  diameter = 6
  invert = false
  matchOuter = false
  offset = 0
  thread = false
  type = 1
FEATURE [Part::FeaturePython] Screw267  label="M4x40-Screw032"  # Fasteners workbench fastener (typed FeaturePython)
  Placement = pos=(56.5,403,485.4) rot=(0,0,1;0rad)
  baseObject = -> Washer204 [Edge1]
  diameter = 5
  invert = false
  length = 11
  matchOuter = false
  offset = 0
  thread = false
  type = 6
FEATURE [Part::FeaturePython] Screw268  label="M4x40-Screw033"  # Fasteners workbench fastener (typed FeaturePython)
  Placement = pos=(38,388,485.4) rot=(0,0,1;0rad)
  baseObject = -> Washer205 [Edge1]
  diameter = 5
  invert = false
  length = 11
  matchOuter = false
  offset = 0
  thread = false
  type = 6
FEATURE [Part::FeaturePython] Screw269  label="M4x40-Screw034"  # Fasteners workbench fastener (typed FeaturePython)
  Placement = pos=(33,413,485.4) rot=(0,0,1;0rad)
  baseObject = -> Washer206 [Edge1]
  diameter = 5
  invert = false
  length = 11
  matchOuter = false
  offset = 0
  thread = false
  type = 6
FEATURE [Part::FeaturePython] Screw270  label="M4x30-Screw045"  # Fasteners workbench fastener (typed FeaturePython)
  Placement = pos=(94,430,475.3) rot=(0,0,1;0rad)
  baseObject = -> motor_block_mirrored_topM_01 [Edge142]
  diameter = 4
  invert = true
  length = 7
  matchOuter = false
  offset = 0
  thread = false
  type = 5
FEATURE [Part::FeaturePython] Screw271  label="M4x30-Screw046"  # Fasteners workbench fastener (typed FeaturePython)
  Placement = pos=(42,430,475.3) rot=(0,0,1;0rad)
  baseObject = -> motor_block_mirrored_topM_01 [Edge141]
  diameter = 4
  invert = true
  length = 7
  matchOuter = false
  offset = 0
  thread = false
  type = 5
FEATURE [Part::FeaturePython] Screw272  label="M4x30-Screw047"  # Fasteners workbench fastener (typed FeaturePython)
  Placement = pos=(10,408,475.3) rot=(0,0,1;0rad)
  baseObject = -> motor_block_mirrored_topM_01 [Edge138]
  diameter = 4
  invert = true
  length = 7
  matchOuter = false
  offset = 0
  thread = false
  type = 5
FEATURE [Part::FeaturePython] Screw273  label="M4x30-Screw048"  # Fasteners workbench fastener (typed FeaturePython)
  Placement = pos=(10,393,475.3) rot=(0,0,1;0rad)
  baseObject = -> motor_block_mirrored_topM_01 [Edge136]
  diameter = 4
  invert = true
  length = 7
  matchOuter = false
  offset = 0
  thread = false
  type = 5
FEATURE [Part::FeaturePython] Screw274  label="M3x16-Screw030"  # Fasteners workbench fastener (typed FeaturePython)
  Placement = pos=(55,383,457.5) rot=(1,0,0;3.14159rad)
  baseObject = -> motor_block_bottom_mirrored_topM_01001 [Edge141]
  diameter = 3
  invert = true
  length = 5
  matchOuter = false
  offset = 0
  thread = false
  type = 5
FEATURE [Part::FeaturePython] Screw275  label="M3x30-Screw029"  # Fasteners workbench fastener (typed FeaturePython)
  Placement = pos=(99.5,414.5,457.5) rot=(1,0,0;3.14159rad)
  baseObject = -> motor_block_bottom_mirrored_topM_01001 [Edge146]
  diameter = 3
  invert = true
  length = 8
  matchOuter = false
  offset = 0
  thread = false
  type = 5
FEATURE [Part::FeaturePython] Screw276  label="M3x30-Screw030"  # Fasteners workbench fastener (typed FeaturePython)
  Placement = pos=(68.5,414.5,457.5) rot=(1,0,0;3.14159rad)
  baseObject = -> motor_block_bottom_mirrored_topM_01001 [Edge145]
  diameter = 3
  invert = true
  length = 8
  matchOuter = false
  offset = 0
  thread = false
  type = 5
FEATURE [Part::FeaturePython] Screw277  label="M3x30-Screw031"  # Fasteners workbench fastener (typed FeaturePython)
  Placement = pos=(99.5,383.5,457.5) rot=(1,0,0;3.14159rad)
  baseObject = -> motor_block_bottom_mirrored_topM_01001 [Edge128]
  diameter = 3
  invert = true
  length = 8
  matchOuter = false
  offset = 0
  thread = false
  type = 5
FEATURE [Part::FeaturePython] Screw278  label="M3x30-Screw032"  # Fasteners workbench fastener (typed FeaturePython)
  Placement = pos=(68.5,383.5,457.5) rot=(1,0,0;3.14159rad)
  baseObject = -> motor_block_bottom_mirrored_topM_01001 [Edge143]
  diameter = 3
  invert = true
  length = 8
  matchOuter = false
  offset = 0
  thread = false
  type = 5
FEATURE [App::DocumentObjectGroup] Gruppe015  label="Screws001"
  Group = -> [Hammermutter_B_Typ_Nut6_M4_import01004,Hammermutter_B_Typ_Nut6_M4_import01005,Hammermutter_B_Typ_Nut6_M4_import01006,Hammermutter_B_Typ_Nut6_M4_import01007,DIN7965___Schraubeinsatz___M3_import026,Washer204,Washer205,Washer206,Washer207,Washer208,Washer209,Washer210,Washer211,Washer212,Washer213,Washer214,Washer215,Nut044,Nut045,Nut046,Screw267,Screw268,Screw269,Screw270,Screw271,Screw272,Screw273,+5 more]
FEATURE [App::DocumentObjectGroup] Gruppe013  label="Left Motor"
  Group = -> [Gruppe014,Gruppe015,Gruppe016,Gruppe018]
FEATURE [Part::FeaturePython] Washer216  label="M4-Washer468"  # Fasteners workbench fastener (typed FeaturePython)
  Placement = pos=(407,10,484.5) rot=(0,0,1;0rad)
  baseObject = -> idler_block_topM_01001 [Edge11]
  diameter = 5
  invert = true
  matchOuter = false
  offset = 0
  type = 0
FEATURE [Part::FeaturePython] Washer217  label="M4-Washer469"  # Fasteners workbench fastener (typed FeaturePython)
  Placement = pos=(402,28,484.5) rot=(0,0,1;0rad)
  baseObject = -> idler_block_topM_01001 [Edge12]
  diameter = 5
  invert = true
  matchOuter = false
  offset = 0
  type = 0
FEATURE [Part::FeaturePython] Washer218  label="M4-Washer470"  # Fasteners workbench fastener (typed FeaturePython)
  Placement = pos=(402,28,449.5) rot=(1,0,0;3.14159rad)
  baseObject = -> idler_block_bottom_topM_01 [Edge10]
  diameter = 5
  invert = false
  matchOuter = false
  offset = 0
  type = 0
FEATURE [Part::FeaturePython] Washer219  label="M4-Washer471"  # Fasteners workbench fastener (typed FeaturePython)
  Placement = pos=(402,28,468.99) rot=(0,0,1;0rad)
  baseObject = -> GT2Bearing_005 [Edge590]
  diameter = 5
  invert = false
  matchOuter = false
  offset = 0
  type = 2
FEATURE [Part::FeaturePython] Washer220  label="M4-Washer472"  # Fasteners workbench fastener (typed FeaturePython)
  Placement = pos=(407,10,478.31) rot=(0,0,1;0rad)
  baseObject = -> GT2Bearing_006 [Edge590]
  diameter = 5
  invert = false
  matchOuter = false
  offset = 0
  type = 2
FEATURE [Part::FeaturePython] Washer221  label="M4-Washer473"  # Fasteners workbench fastener (typed FeaturePython)
  Placement = pos=(407,10,469.31) rot=(1,0,0;3.14159rad)
  baseObject = -> GT2Bearing_006 [Edge325]
  diameter = 5
  invert = false
  matchOuter = false
  offset = 0
  type = 2
FEATURE [Part::FeaturePython] Washer222  label="M4-Washer474"  # Fasteners workbench fastener (typed FeaturePython)
  Placement = pos=(402,28,459.99) rot=(1,0,0;3.14159rad)
  baseObject = -> GT2Bearing_005 [Edge330]
  diameter = 5
  invert = false
  matchOuter = false
  offset = 0
  type = 2
FEATURE [Part::FeaturePython] Screw279  label="M4x40-Screw037"  # Fasteners workbench fastener (typed FeaturePython)
  Placement = pos=(407,10,484.5) rot=(0,0,1;0rad)
  baseObject = -> idler_block_topM_01001 [Edge11]
  diameter = 5
  invert = true
  length = 11
  matchOuter = false
  offset = 0
  thread = false
  type = 6
FEATURE [Part::FeaturePython] Screw280  label="M4x40-Screw038"  # Fasteners workbench fastener (typed FeaturePython)
  Placement = pos=(402,28,484.5) rot=(0,0,1;0rad)
  baseObject = -> idler_block_topM_01001 [Edge12]
  diameter = 5
  invert = true
  length = 11
  matchOuter = false
  offset = 0
  thread = false
  type = 6
FEATURE [Part::FeaturePython] Screw281  label="M4x30-Screw049"  # Fasteners workbench fastener (typed FeaturePython)
  Placement = pos=(392,10,475.3) rot=(0,0,1;0rad)
  baseObject = -> idler_block_topM_01001 [Edge65]
  diameter = 4
  invert = false
  length = 7
  matchOuter = false
  offset = 0
  thread = false
  type = 5
FEATURE [Part::FeaturePython] Screw282  label="M4x16-Screw002"  # Fasteners workbench fastener (typed FeaturePython)
  Placement = pos=(430,30,479.2) rot=(-1,0,0;1.5708rad)
  baseObject = -> idler_block_topM_01001 [Edge61]
  diameter = 4
  invert = true
  length = 4
  matchOuter = false
  offset = 0
  thread = false
  type = 5
FEATURE [Part::FeaturePython] Screw283  label="M4x16-Screw003"  # Fasteners workbench fastener (typed FeaturePython)
  Placement = pos=(430,30,455.5) rot=(-1,0,0;1.5708rad)
  baseObject = -> idler_block_bottom_topM_01 [Edge61]
  diameter = 4
  invert = true
  length = 4
  matchOuter = false
  offset = 0
  thread = false
  type = 5
FEATURE [Part::FeaturePython] Screw284  label="M3x12-Screw001"  # Fasteners workbench fastener (typed FeaturePython)
  Placement = pos=(385,35,457.5) rot=(1,0,0;3.14159rad)
  baseObject = -> idler_block_bottom_topM_01 [Edge64]
  diameter = 3
  invert = false
  length = 4
  matchOuter = false
  offset = 0
  thread = false
  type = 5
FEATURE [Part::FeaturePython] Nut047  label="M4-Nut041"  # Fasteners workbench fastener (typed FeaturePython)
  Placement = pos=(402,28,448.6) rot=(1,0,0;3.14159rad)
  baseObject = -> Washer218 [Edge1]
  diameter = 6
  invert = false
  matchOuter = false
  offset = 0
  thread = false
  type = 1
FEATURE [App::DocumentObjectGroup] Gruppe022  label="Screws002"
  Group = -> [Hammermutter_B_Typ_Nut6_M4_import01009,Hammermutter_B_Typ_Nut6_M4_import01011,DIN7965___Schraubeinsatz___M3_import025,Hammermutter_B_Typ_Nut6_M4_import01081,Hammermutter_B_Typ_Nut6_M4_import01080,Washer216,Washer217,Washer218,Washer219,Washer220,Washer221,Washer222,Screw279,Screw280,Screw281,Screw282,Screw283,Screw284,Nut047]
FEATURE [App::DocumentObjectGroup] Gruppe019  label="Right Idler"
  Group = -> [Gruppe021,Gruppe022,Gruppe023,Gruppe024]
FEATURE [Part::FeaturePython] Washer223  label="M4-Washer709"  # Fasteners workbench fastener (typed FeaturePython)
  Placement = pos=(38,28,449.5) rot=(1,0,0;3.14159rad)
  baseObject = -> motor_block_left_top_01 [Edge10]
  diameter = 5
  invert = true
  matchOuter = false
  offset = 0
  type = 0
FEATURE [Part::FeaturePython] Washer224  label="M4-Washer476"  # Fasteners workbench fastener (typed FeaturePython)
  Placement = pos=(33,10,484.5) rot=(0,0,1;0rad)
  baseObject = -> idler_block_mirrored_topM_01 [Edge11]
  diameter = 5
  invert = false
  matchOuter = false
  offset = 0
  type = 0
FEATURE [Part::FeaturePython] Washer225  label="M4-Washer477"  # Fasteners workbench fastener (typed FeaturePython)
  Placement = pos=(38,28,484.5) rot=(0,0,1;0rad)
  baseObject = -> idler_block_mirrored_topM_01 [Edge12]
  diameter = 5
  invert = false
  matchOuter = false
  offset = 0
  type = 0
FEATURE [Part::FeaturePython] Washer226  label="M4-Washer478"  # Fasteners workbench fastener (typed FeaturePython)
  Placement = pos=(38,28,478.31) rot=(0,0,1;0rad)
  baseObject = -> GT2Bearing_003 [Edge590]
  diameter = 5
  invert = false
  matchOuter = false
  offset = 0
  type = 2
FEATURE [Part::FeaturePython] Washer227  label="M4-Washer479"  # Fasteners workbench fastener (typed FeaturePython)
  Placement = pos=(33,10,468.99) rot=(0,0,1;0rad)
  baseObject = -> GT2Bearing_004 [Edge590]
  diameter = 5
  invert = false
  matchOuter = false
  offset = 0
  type = 2
FEATURE [Part::FeaturePython] Washer228  label="M4-Washer480"  # Fasteners workbench fastener (typed FeaturePython)
  Placement = pos=(33,10,459.99) rot=(1,0,0;3.14159rad)
  baseObject = -> GT2Bearing_004 [Edge325]
  diameter = 5
  invert = false
  matchOuter = false
  offset = 0
  type = 2
FEATURE [Part::FeaturePython] Washer229  label="M4-Washer481"  # Fasteners workbench fastener (typed FeaturePython)
  Placement = pos=(38,28,469.31) rot=(1,0,0;3.14159rad)
  baseObject = -> GT2Bearing_003 [Edge325]
  diameter = 5
  invert = false
  matchOuter = false
  offset = 0
  type = 2
FEATURE [Part::FeaturePython] Screw285  label="M4x40-Screw039"  # Fasteners workbench fastener (typed FeaturePython)
  Placement = pos=(33,10,485.4) rot=(0,0,1;0rad)
  baseObject = -> Washer224 [Edge1]
  diameter = 5
  invert = false
  length = 11
  matchOuter = false
  offset = 0
  thread = false
  type = 6
FEATURE [Part::FeaturePython] Screw286  label="M4x40-Screw040"  # Fasteners workbench fastener (typed FeaturePython)
  Placement = pos=(38,28,485.4) rot=(0,0,1;0rad)
  baseObject = -> Washer225 [Edge1]
  diameter = 5
  invert = false
  length = 11
  matchOuter = false
  offset = 0
  thread = false
  type = 6
FEATURE [Part::FeaturePython] Screw287  label="M4x30-Screw050"  # Fasteners workbench fastener (typed FeaturePython)
  Placement = pos=(48,10,475.3) rot=(0,0,1;0rad)
  baseObject = -> idler_block_mirrored_topM_01 [Edge65]
  diameter = 4
  invert = true
  length = 7
  matchOuter = false
  offset = 0
  thread = false
  type = 5
FEATURE [Part::FeaturePython] Screw288  label="M4x16-Screw"  # Fasteners workbench fastener (typed FeaturePython)
  Placement = pos=(10,30,479.2) rot=(-1,0,0;1.5708rad)
  baseObject = -> idler_block_mirrored_topM_01 [Edge61]
  diameter = 4
  invert = false
  length = 4
  matchOuter = false
  offset = 0
  thread = false
  type = 5
FEATURE [Part::FeaturePython] Screw289  label="M4x16-Screw007"  # Fasteners workbench fastener (typed FeaturePython)
  Placement = pos=(10,30,455.5) rot=(-1,0,0;1.5708rad)
  baseObject = -> motor_block_left_top_01 [Edge61]
  diameter = 4
  invert = false
  length = 4
  matchOuter = false
  offset = 0
  thread = false
  type = 5
FEATURE [Part::FeaturePython] Screw290  label="M3x12-Screw"  # Fasteners workbench fastener (typed FeaturePython)
  Placement = pos=(55,35,457.5) rot=(1,0,0;3.14159rad)
  baseObject = -> motor_block_left_top_01 [Edge64]
  diameter = 3
  invert = true
  length = 4
  matchOuter = false
  offset = 0
  thread = false
  type = 5
FEATURE [Part::FeaturePython] Nut048  label="M4-Nut072"  # Fasteners workbench fastener (typed FeaturePython)
  Placement = pos=(38,28,448.6) rot=(1,0,0;3.14159rad)
  baseObject = -> Washer223 [Edge1]
  diameter = 6
  invert = false
  matchOuter = false
  offset = 0
  thread = false
  type = 1
FEATURE [App::DocumentObjectGroup] Gruppe026  label="Screws003"
  Group = -> [Hammermutter_B_Typ_Nut6_M4_import01012,DIN7965___Schraubeinsatz___M3_import004,Hammermutter_B_Typ_Nut6_M4_import01013,Hammermutter_B_Typ_Nut6_M4_import01014,Hammermutter_B_Typ_Nut6_M4_import01015,Washer223,Washer224,Washer225,Washer226,Washer227,Washer228,Washer229,Screw285,Screw286,Screw287,Screw288,Screw289,Screw290,Nut048]
FEATURE [App::DocumentObjectGroup] Gruppe020  label="Left Idler"
  Group = -> [Gruppe025,Gruppe026,Gruppe027,Gruppe028]
FEATURE [App::DocumentObjectGroup] Gruppe057  label="Gleichteile"
  Group = -> [Gruppe009,Gruppe013,Gruppe029,Gruppe019,Gruppe020,Gruppe044]
FEATURE [App::DocumentObjectGroup] Gruppe147  label="Sides"
  Group = -> [Angle_Bracket_import017,Angle_Bracket_import018,Angle_Bracket_import019,Angle_Bracket_import020]
FEATURE [App::DocumentObjectGroup] Gruppe148  label="Front/Back"
  Group = -> [Angle_Bracket_import022,Angle_Bracket_import024,Angle_Bracket_import026,Angle_Bracket_import028]
FEATURE [App::DocumentObjectGroup] Gruppe101  label="xy-Befestigung001"
  Group = -> [Gruppe147,Gruppe148]
FEATURE [App::DocumentObjectGroup] Gruppe006  label="Eckverbinder"
  Group = -> [Gruppe100,Gruppe101,Gruppe114]
FEATURE [App::DocumentObjectGroup] Gruppe150  label="Front/Back001"
  Group = -> [Gruppe125,Gruppe126,Gruppe127,Gruppe128]
FEATURE [App::DocumentObjectGroup] Gruppe151  label="y-Befestigung"
  Group = -> [tslot20x20_import022,tslot20x20_import023]
FEATURE [App::DocumentObjectGroup] Gruppe001  label="Alu-Profile"
  Group = -> [tslot20x20_import13,tslot20x20x500_import04,tslot20x20_import16,tslot20x20_import017,tslot20x20x500_import01,tslot20x20_import05,tslot20x20_import10,tslot20x20x500_import03,tslot20x20_import01,tslot20x20_import06,tslot20x20_import14,tslot20x20x500_import02,Gruppe003,Gruppe098,Gruppe112,Gruppe151]
FEATURE [App::DocumentObjectGroup] Gruppe152  label="HR003"
  Group = -> [Hammermutter_B_Typ_Nut6_M4_import01055,Hammermutter_B_Typ_Nut6_M4_import01054,Screw216,Screw217,Washer159,Washer158]
FEATURE [App::DocumentObjectGroup] Gruppe153  label="HL003"
  Group = -> [Hammermutter_B_Typ_Nut6_M4_import01048,Hammermutter_B_Typ_Nut6_M4_import01051,Screw222,Screw223,Washer162,Washer163]
FEATURE [App::DocumentObjectGroup] Gruppe154  label="VL003"
  Group = -> [Hammermutter_B_Typ_Nut6_M4_import01049,Hammermutter_B_Typ_Nut6_M4_import01050,Screw224,Screw225,Washer167,Washer166]
FEATURE [App::DocumentObjectGroup] Gruppe155  label="VR003"
  Group = -> [Hammermutter_B_Typ_Nut6_M4_import01052,Hammermutter_B_Typ_Nut6_M4_import01053,Screw228,Screw229,Washer168,Washer169]
FEATURE [App::DocumentObjectGroup] Gruppe149  label="Sides001"
  Group = -> [Gruppe152,Gruppe153,Gruppe154,Gruppe155]
FEATURE [App::DocumentObjectGroup] Gruppe102  label="xy-Befestigung002"
  Group = -> [Gruppe149,Gruppe150]
FEATURE [App::DocumentObjectGroup] Gruppe045  label="Eckverbinder Screws"
  Group = -> [Gruppe099,Gruppe102,Gruppe113]
FEATURE [App::DocumentObjectGroup] Gruppe  label="Frame"
  Group = -> [Gruppe001,Gruppe002,Gruppe006,Gruppe005,Gruppe045]
FEATURE [Part::FeaturePython] Washer230  label="M4-Washer482"  # Fasteners workbench fastener (typed FeaturePython)
  Placement = pos=(402.3,215.9,496.627) rot=(0,0,1;0rad)
  baseObject = -> CustomBushingXYBlock_LM8UU_01 [Edge141]
  diameter = 5
  invert = false
  matchOuter = false
  offset = 0
  type = 0
FEATURE [Part::FeaturePython] Washer231  label="M4-Washer483"  # Fasteners workbench fastener (typed FeaturePython)
  Placement = pos=(402.3,201.5,496.627) rot=(0,0,1;0rad)
  baseObject = -> CustomBushingXYBlock_LM8UU_01 [Edge139]
  diameter = 5
  invert = false
  matchOuter = false
  offset = 0
  type = 0
FEATURE [Part::FeaturePython] Washer232  label="M4-Washer484"  # Fasteners workbench fastener (typed FeaturePython)
  Placement = pos=(402.3,215.9,443.773) rot=(1,0,0;3.14159rad)
  baseObject = -> CustomBushingXYBlock_LM8UU_002 [Edge139]
  diameter = 5
  invert = false
  matchOuter = false
  offset = 0
  type = 0
FEATURE [Part::FeaturePython] Washer233  label="M4-Washer485"  # Fasteners workbench fastener (typed FeaturePython)
  Placement = pos=(402.3,201.5,443.773) rot=(1,0,0;3.14159rad)
  baseObject = -> CustomBushingXYBlock_LM8UU_002 [Edge141]
  diameter = 5
  invert = false
  matchOuter = false
  offset = 0
  type = 0
FEATURE [Part::FeaturePython] Nut  label="M4-Nut"  # Fasteners workbench fastener (typed FeaturePython)
  Placement = pos=(402.3,215.9,497.527) rot=(0,0,1;0rad)
  baseObject = -> Washer230 [Edge1]
  diameter = 6
  invert = false
  matchOuter = false
  offset = 0
  thread = false
  type = 1
FEATURE [Part::FeaturePython] Nut049  label="M4-Nut043"  # Fasteners workbench fastener (typed FeaturePython)
  Placement = pos=(402.3,201.5,497.527) rot=(0,0,1;0rad)
  baseObject = -> Washer231 [Edge1]
  diameter = 6
  invert = false
  matchOuter = false
  offset = 0
  thread = false
  type = 1
FEATURE [Part::FeaturePython] Nut050  label="M4-Nut044"  # Fasteners workbench fastener (typed FeaturePython)
  Placement = pos=(402.3,215.9,442.873) rot=(1,0,0;3.14159rad)
  baseObject = -> Washer232 [Edge1]
  diameter = 6
  invert = false
  matchOuter = false
  offset = 0
  thread = false
  type = 1
FEATURE [Part::FeaturePython] Nut051  label="M4-Nut045"  # Fasteners workbench fastener (typed FeaturePython)
  Placement = pos=(402.3,201.5,442.873) rot=(1,0,0;3.14159rad)
  baseObject = -> Washer233 [Edge1]
  diameter = 6
  invert = false
  matchOuter = false
  offset = 0
  thread = false
  type = 1
FEATURE [Part::FeaturePython] ScrewTap002  label="M4x62.0-ScrewTap002"  # Fasteners workbench fastener (typed FeaturePython)
  Placement = pos=(402.3,215.9,500.927) rot=(0,0,1;0rad)
  baseObject = -> CustomBushingXYBlock_LM8UU_01 [Edge141]
  diameter = 6
  invert = false
  length = 62
  matchOuter = false
  offset = 4.3
  thread = false
FEATURE [Part::FeaturePython] ScrewTap003  label="M4x62.0-ScrewTap003"  # Fasteners workbench fastener (typed FeaturePython)
  Placement = pos=(402.3,201.5,500.927) rot=(0,0,1;0rad)
  baseObject = -> CustomBushingXYBlock_LM8UU_01 [Edge139]
  diameter = 6
  invert = false
  length = 62
  matchOuter = false
  offset = 4.3
  thread = false
FEATURE [Part::FeaturePython] Washer234  label="M4-Washer700"  # Fasteners workbench fastener (typed FeaturePython)
  Placement = pos=(402.3,215.9,479.45) rot=(0,0,1;0rad)
  baseObject = -> DIN625_1_624_ZZ_import01029 [Edge29]
  diameter = 5
  invert = false
  matchOuter = false
  offset = 0
  type = 2
FEATURE [Part::FeaturePython] Washer235  label="M4-Washer701"  # Fasteners workbench fastener (typed FeaturePython)
  Placement = pos=(402.3,215.9,480) rot=(0,0,1;0rad)
  baseObject = -> Washer234 [Edge1]
  diameter = 5
  invert = false
  matchOuter = false
  offset = 0
  type = 0
FEATURE [Part::FeaturePython] Washer236  label="M4-Washer702"  # Fasteners workbench fastener (typed FeaturePython)
  Placement = pos=(402.3,215.9,480.9) rot=(0,0,1;0rad)
  baseObject = -> Washer235 [Edge1]
  diameter = 5
  invert = false
  matchOuter = false
  offset = 0
  type = 0
FEATURE [Part::FeaturePython] Washer  label="M4-Washer"  # Fasteners workbench fastener (typed FeaturePython)
  Placement = pos=(402.3,201.5,469.79) rot=(0,0,1;0rad)
  baseObject = -> GT2Bearing_010 [Edge566]
  diameter = 5
  invert = true
  matchOuter = false
  offset = 0
  type = 2
FEATURE [Part::FeaturePython] Washer237  label="M4-Washer583"  # Fasteners workbench fastener (typed FeaturePython)
  Placement = pos=(402.3,201.5,460.79) rot=(1,0,0;3.14159rad)
  baseObject = -> GT2Bearing_010 [Edge336]
  diameter = 5
  invert = false
  matchOuter = false
  offset = 0
  type = 2
FEATURE [Part::FeaturePython] Washer238  label="M4-Washer584"  # Fasteners workbench fastener (typed FeaturePython)
  Placement = pos=(402.3,201.5,460.24) rot=(1,0,0;3.14159rad)
  baseObject = -> Washer237 [Edge1]
  diameter = 5
  invert = false
  matchOuter = false
  offset = 0
  type = 0
FEATURE [Part::FeaturePython] Washer239  label="M4-Washer625"  # Fasteners workbench fastener (typed FeaturePython)
  Placement = pos=(402.3,215.9,469.45) rot=(1,0,0;3.14159rad)
  baseObject = -> F624zz_import023 [Edge8]
  diameter = 5
  invert = true
  matchOuter = false
  offset = 0
  type = 0
FEATURE [Part::FeaturePython] Screw291  label="M3x20-Screw"  # Fasteners workbench fastener (typed FeaturePython)
  Placement = pos=(7,167.705,477.7) rot=(0,0,1;0rad)
  baseObject = -> XY_block_top_wide_topM_01 [Edge72]
  diameter = 3
  invert = true
  length = 6
  matchOuter = false
  offset = 0
  thread = false
  type = 5
FEATURE [Part::FeaturePython] Screw292  label="M3x20-Screw063"  # Fasteners workbench fastener (typed FeaturePython)
  Placement = pos=(19,167.705,477.7) rot=(0,0,1;0rad)
  baseObject = -> XY_block_top_wide_topM_01 [Edge104]
  diameter = 3
  invert = true
  length = 6
  matchOuter = false
  offset = 0
  thread = false
  type = 5
FEATURE [Part::FeaturePython] Screw293  label="M3x20-Screw064"  # Fasteners workbench fastener (typed FeaturePython)
  Placement = pos=(7,208.705,477.7) rot=(0,0,1;0rad)
  baseObject = -> XY_block_top_wide_topM_01 [Edge96]
  diameter = 3
  invert = true
  length = 6
  matchOuter = false
  offset = 0
  thread = false
  type = 5
FEATURE [Part::FeaturePython] Screw294  label="M3x20-Screw065"  # Fasteners workbench fastener (typed FeaturePython)
  Placement = pos=(19,208.705,477.7) rot=(0,0,1;0rad)
  baseObject = -> XY_block_top_wide_topM_01 [Edge115]
  diameter = 3
  invert = true
  length = 6
  matchOuter = false
  offset = 0
  thread = false
  type = 5
FEATURE [Part::FeaturePython] Screw295  label="M3x20-Screw066"  # Fasteners workbench fastener (typed FeaturePython)
  Placement = pos=(7,249.705,477.7) rot=(0,0,1;0rad)
  baseObject = -> XY_block_top_wide_topM_01 [Edge89]
  diameter = 3
  invert = true
  length = 6
  matchOuter = false
  offset = 0
  thread = false
  type = 5
FEATURE [Part::FeaturePython] Screw296  label="M3x20-Screw067"  # Fasteners workbench fastener (typed FeaturePython)
  Placement = pos=(19,249.705,477.7) rot=(0,0,1;0rad)
  baseObject = -> XY_block_top_wide_topM_01 [Edge102]
  diameter = 3
  invert = true
  length = 6
  matchOuter = false
  offset = 0
  thread = false
  type = 5
FEATURE [Part::FeaturePython] Screw297  label="M3x16-Screw035"  # Fasteners workbench fastener (typed FeaturePython)
  Placement = pos=(41,167.705,477.7) rot=(0,0,1;0rad)
  baseObject = -> XY_block_top_wide_topM_01 [Edge189]
  diameter = 3
  invert = true
  length = 5
  matchOuter = false
  offset = 0
  thread = false
  type = 5
FEATURE [Part::FeaturePython] Screw298  label="M3x16-Screw036"  # Fasteners workbench fastener (typed FeaturePython)
  Placement = pos=(41,185.705,477.7) rot=(0,0,1;0rad)
  baseObject = -> XY_block_top_wide_topM_01 [Edge194]
  diameter = 3
  invert = true
  length = 5
  matchOuter = false
  offset = 0
  thread = false
  type = 5
FEATURE [Part::FeaturePython] Screw299  label="M3x16-Screw037"  # Fasteners workbench fastener (typed FeaturePython)
  Placement = pos=(41,231.705,477.7) rot=(0,0,1;0rad)
  baseObject = -> XY_block_top_wide_topM_01 [Edge195]
  diameter = 3
  invert = true
  length = 5
  matchOuter = false
  offset = 0
  thread = false
  type = 5
FEATURE [Part::FeaturePython] Screw300  label="M3x16-Screw038"  # Fasteners workbench fastener (typed FeaturePython)
  Placement = pos=(41,249.705,477.7) rot=(0,0,1;0rad)
  baseObject = -> XY_block_top_wide_topM_01 [Edge193]
  diameter = 3
  invert = true
  length = 5
  matchOuter = false
  offset = 0
  thread = false
  type = 5
FEATURE [Part::FeaturePython] Nut052  label="M3-Nut"  # Fasteners workbench fastener (typed FeaturePython)
  Placement = pos=(19,249.705,459.7) rot=(1,0,0;3.14159rad)
  baseObject = -> XY_block_wide_topM_01002 [Edge104]
  diameter = 4
  invert = true
  matchOuter = false
  offset = 0
  thread = false
  type = 1
FEATURE [Part::FeaturePython] Nut053  label="M3-Nut058"  # Fasteners workbench fastener (typed FeaturePython)
  Placement = pos=(7,249.705,459.7) rot=(1,0,0;3.14159rad)
  baseObject = -> XY_block_wide_topM_01002 [Edge72]
  diameter = 4
  invert = true
  matchOuter = false
  offset = 0
  thread = false
  type = 1
FEATURE [Part::FeaturePython] Nut054  label="M3-Nut059"  # Fasteners workbench fastener (typed FeaturePython)
  Placement = pos=(19,208.705,459.7) rot=(1,0,0;3.14159rad)
  baseObject = -> XY_block_wide_topM_01002 [Edge115]
  diameter = 4
  invert = true
  matchOuter = false
  offset = 0
  thread = false
  type = 1
FEATURE [Part::FeaturePython] Nut055  label="M3-Nut060"  # Fasteners workbench fastener (typed FeaturePython)
  Placement = pos=(7,208.705,459.7) rot=(1,0,0;3.14159rad)
  baseObject = -> XY_block_wide_topM_01002 [Edge96]
  diameter = 4
  invert = true
  matchOuter = false
  offset = 0
  thread = false
  type = 1
FEATURE [Part::FeaturePython] Nut056  label="M3-Nut061"  # Fasteners workbench fastener (typed FeaturePython)
  Placement = pos=(19,167.705,459.7) rot=(1,0,0;3.14159rad)
  baseObject = -> XY_block_wide_topM_01002 [Edge102]
  diameter = 4
  invert = true
  matchOuter = false
  offset = 0
  thread = false
  type = 1
FEATURE [Part::FeaturePython] Nut057  label="M3-Nut062"  # Fasteners workbench fastener (typed FeaturePython)
  Placement = pos=(7,167.705,459.7) rot=(1,0,0;3.14159rad)
  baseObject = -> XY_block_wide_topM_01002 [Edge89]
  diameter = 4
  invert = true
  matchOuter = false
  offset = 0
  thread = false
  type = 1
FEATURE [App::DocumentObjectGroup] Gruppe064  label="Screws008"
  Group = -> [DIN7965___Schraubeinsatz___M3_import013,DIN7965___Schraubeinsatz___M3_import014,DIN7965___Schraubeinsatz___M3_import015,DIN7965___Schraubeinsatz___M3_import016,Screw291,Screw292,Screw293,Screw294,Screw295,Screw296,Screw297,Screw298,Screw299,Screw300,Nut052,Nut053,Nut054,Nut055,Nut056,Nut057]
FEATURE [App::DocumentObjectGroup] Gruppe060  label="Left Slider001"
  Group = -> [Gruppe063,Gruppe064,Gruppe065,Gruppe066]
FEATURE [Part::FeaturePython] Screw301  label="M3x20-Screw074"  # Fasteners workbench fastener (typed FeaturePython)
  Placement = pos=(433,167.742,477.7) rot=(0,0,1;0rad)
  baseObject = -> XY_block_top_wide_topM_002 [Edge89]
  diameter = 3
  invert = true
  length = 6
  matchOuter = false
  offset = 0
  thread = false
  type = 5
FEATURE [Part::FeaturePython] Screw302  label="M3x20-Screw075"  # Fasteners workbench fastener (typed FeaturePython)
  Placement = pos=(421,167.742,477.7) rot=(0,0,1;0rad)
  baseObject = -> XY_block_top_wide_topM_002 [Edge102]
  diameter = 3
  invert = true
  length = 6
  matchOuter = false
  offset = 0
  thread = false
  type = 5
FEATURE [Part::FeaturePython] Screw303  label="M3x20-Screw076"  # Fasteners workbench fastener (typed FeaturePython)
  Placement = pos=(433,208.742,477.7) rot=(0,0,1;0rad)
  baseObject = -> XY_block_top_wide_topM_002 [Edge96]
  diameter = 3
  invert = true
  length = 6
  matchOuter = false
  offset = 0
  thread = false
  type = 5
FEATURE [Part::FeaturePython] Screw304  label="M3x20-Screw077"  # Fasteners workbench fastener (typed FeaturePython)
  Placement = pos=(421,208.742,477.7) rot=(0,0,1;0rad)
  baseObject = -> XY_block_top_wide_topM_002 [Edge115]
  diameter = 3
  invert = true
  length = 6
  matchOuter = false
  offset = 0
  thread = false
  type = 5
FEATURE [Part::FeaturePython] Screw305  label="M3x20-Screw078"  # Fasteners workbench fastener (typed FeaturePython)
  Placement = pos=(433,249.742,477.7) rot=(0,0,1;0rad)
  baseObject = -> XY_block_top_wide_topM_002 [Edge72]
  diameter = 3
  invert = true
  length = 6
  matchOuter = false
  offset = 0
  thread = false
  type = 5
FEATURE [Part::FeaturePython] Screw306  label="M3x20-Screw079"  # Fasteners workbench fastener (typed FeaturePython)
  Placement = pos=(421,249.742,477.7) rot=(0,0,1;0rad)
  baseObject = -> XY_block_top_wide_topM_002 [Edge104]
  diameter = 3
  invert = true
  length = 6
  matchOuter = false
  offset = 0
  thread = false
  type = 5
FEATURE [Part::FeaturePython] Screw307  label="M3x16-Screw043"  # Fasteners workbench fastener (typed FeaturePython)
  Placement = pos=(399,167.742,477.7) rot=(0,0,1;0rad)
  baseObject = -> XY_block_top_wide_topM_002 [Edge193]
  diameter = 3
  invert = true
  length = 5
  matchOuter = false
  offset = 0
  thread = false
  type = 5
FEATURE [Part::FeaturePython] Screw308  label="M3x16-Screw044"  # Fasteners workbench fastener (typed FeaturePython)
  Placement = pos=(399,185.742,477.7) rot=(0,0,1;0rad)
  baseObject = -> XY_block_top_wide_topM_002 [Edge195]
  diameter = 3
  invert = true
  length = 5
  matchOuter = false
  offset = 0
  thread = false
  type = 5
FEATURE [Part::FeaturePython] Screw309  label="M3x16-Screw045"  # Fasteners workbench fastener (typed FeaturePython)
  Placement = pos=(399,231.742,477.7) rot=(0,0,1;0rad)
  baseObject = -> XY_block_top_wide_topM_002 [Edge194]
  diameter = 3
  invert = true
  length = 5
  matchOuter = false
  offset = 0
  thread = false
  type = 5
FEATURE [Part::FeaturePython] Screw310  label="M3x16-Screw046"  # Fasteners workbench fastener (typed FeaturePython)
  Placement = pos=(399,249.742,477.7) rot=(0,0,1;0rad)
  baseObject = -> XY_block_top_wide_topM_002 [Edge189]
  diameter = 3
  invert = true
  length = 5
  matchOuter = false
  offset = 0
  thread = false
  type = 5
FEATURE [Part::FeaturePython] Nut058  label="M3-Nut069"  # Fasteners workbench fastener (typed FeaturePython)
  Placement = pos=(433,249.742,459.7) rot=(1,0,0;3.14159rad)
  baseObject = -> XY_block_wide_topM_01003 [Edge89]
  diameter = 4
  invert = true
  matchOuter = false
  offset = 0
  thread = false
  type = 1
FEATURE [Part::FeaturePython] Nut059  label="M3-Nut070"  # Fasteners workbench fastener (typed FeaturePython)
  Placement = pos=(421,249.742,459.7) rot=(1,0,0;3.14159rad)
  baseObject = -> XY_block_wide_topM_01003 [Edge102]
  diameter = 4
  invert = true
  matchOuter = false
  offset = 0
  thread = false
  type = 1
FEATURE [Part::FeaturePython] Nut060  label="M3-Nut071"  # Fasteners workbench fastener (typed FeaturePython)
  Placement = pos=(433,208.742,459.7) rot=(1,0,0;3.14159rad)
  baseObject = -> XY_block_wide_topM_01003 [Edge96]
  diameter = 4
  invert = true
  matchOuter = false
  offset = 0
  thread = false
  type = 1
FEATURE [Part::FeaturePython] Nut061  label="M3-Nut072"  # Fasteners workbench fastener (typed FeaturePython)
  Placement = pos=(421,208.742,459.7) rot=(1,0,0;3.14159rad)
  baseObject = -> XY_block_wide_topM_01003 [Edge115]
  diameter = 4
  invert = true
  matchOuter = false
  offset = 0
  thread = false
  type = 1
FEATURE [Part::FeaturePython] Nut062  label="M3-Nut073"  # Fasteners workbench fastener (typed FeaturePython)
  Placement = pos=(433,167.742,459.7) rot=(1,0,0;3.14159rad)
  baseObject = -> XY_block_wide_topM_01003 [Edge72]
  diameter = 4
  invert = true
  matchOuter = false
  offset = 0
  thread = false
  type = 1
FEATURE [Part::FeaturePython] Nut063  label="M3-Nut074"  # Fasteners workbench fastener (typed FeaturePython)
  Placement = pos=(421,167.742,459.7) rot=(1,0,0;3.14159rad)
  baseObject = -> XY_block_wide_topM_01003 [Edge104]
  diameter = 4
  invert = true
  matchOuter = false
  offset = 0
  thread = false
  type = 1
FEATURE [App::DocumentObjectGroup] Gruppe076  label="Screws010"
  Group = -> [DIN7965___Schraubeinsatz___M3_import030,DIN7965___Schraubeinsatz___M3_import029,DIN7965___Schraubeinsatz___M3_import028,DIN7965___Schraubeinsatz___M3_import027,Screw301,Screw302,Screw303,Screw304,Screw305,Screw306,Screw307,Screw308,Screw309,Screw310,Nut058,Nut059,Nut060,Nut061,Nut062,Nut063]
FEATURE [App::DocumentObjectGroup] Gruppe062  label="Right Slider001"
  Group = -> [Gruppe075,Gruppe076,Gruppe077,Gruppe078]
FEATURE [App::DocumentObjectGroup] Gruppe059  label="80x90 Carrier"
  Group = -> [Gruppe060,Gruppe062,Gruppe061,Gruppe068]
FEATURE [Part::FeaturePython] Screw311  label="M3x20-Screw086"  # Fasteners workbench fastener (typed FeaturePython)
  Placement = pos=(7,235.8,477.7) rot=(0,0,1;0rad)
  baseObject = -> XY_block_top_topM_002 [Edge151]
  diameter = 3
  invert = true
  length = 6
  matchOuter = false
  offset = 0
  thread = false
  type = 5
FEATURE [Part::FeaturePython] Screw312  label="M3x20-Screw087"  # Fasteners workbench fastener (typed FeaturePython)
  Placement = pos=(19,235.8,477.7) rot=(0,0,1;0rad)
  baseObject = -> XY_block_top_topM_002 [Edge152]
  diameter = 3
  invert = true
  length = 6
  matchOuter = false
  offset = 0
  thread = false
  type = 5
FEATURE [Part::FeaturePython] Screw313  label="M3x20-Screw088"  # Fasteners workbench fastener (typed FeaturePython)
  Placement = pos=(7,208.8,477.7) rot=(0,0,1;0rad)
  baseObject = -> XY_block_top_topM_002 [Edge158]
  diameter = 3
  invert = true
  length = 6
  matchOuter = false
  offset = 0
  thread = false
  type = 5
FEATURE [Part::FeaturePython] Screw314  label="M3x20-Screw089"  # Fasteners workbench fastener (typed FeaturePython)
  Placement = pos=(19,208.8,477.7) rot=(0,0,1;0rad)
  baseObject = -> XY_block_top_topM_002 [Edge156]
  diameter = 3
  invert = true
  length = 6
  matchOuter = false
  offset = 0
  thread = false
  type = 5
FEATURE [Part::FeaturePython] Screw315  label="M3x20-Screw090"  # Fasteners workbench fastener (typed FeaturePython)
  Placement = pos=(7,181.8,477.7) rot=(0,0,1;0rad)
  baseObject = -> XY_block_top_topM_002 [Edge157]
  diameter = 3
  invert = true
  length = 6
  matchOuter = false
  offset = 0
  thread = false
  type = 5
FEATURE [Part::FeaturePython] Screw316  label="M3x20-Screw091"  # Fasteners workbench fastener (typed FeaturePython)
  Placement = pos=(19,181.8,477.7) rot=(0,0,1;0rad)
  baseObject = -> XY_block_top_topM_002 [Edge155]
  diameter = 3
  invert = true
  length = 6
  matchOuter = false
  offset = 0
  thread = false
  type = 5
FEATURE [Part::FeaturePython] Screw317  label="M3x16-Screw051"  # Fasteners workbench fastener (typed FeaturePython)
  Placement = pos=(53,235.8,477.7) rot=(0,0,1;0rad)
  baseObject = -> XY_block_top_topM_002 [Edge153]
  diameter = 3
  invert = true
  length = 5
  matchOuter = false
  offset = 0
  thread = false
  type = 5
FEATURE [Part::FeaturePython] Screw318  label="M3x16-Screw052"  # Fasteners workbench fastener (typed FeaturePython)
  Placement = pos=(53,221.8,477.7) rot=(0,0,1;0rad)
  baseObject = -> XY_block_top_topM_002 [Edge154]
  diameter = 3
  invert = true
  length = 5
  matchOuter = false
  offset = 0
  thread = false
  type = 5
FEATURE [Part::FeaturePython] Screw319  label="M3x16-Screw053"  # Fasteners workbench fastener (typed FeaturePython)
  Placement = pos=(53,195.8,477.7) rot=(0,0,1;0rad)
  baseObject = -> XY_block_top_topM_002 [Edge160]
  diameter = 3
  invert = true
  length = 5
  matchOuter = false
  offset = 0
  thread = false
  type = 5
FEATURE [Part::FeaturePython] Screw320  label="M3x16-Screw054"  # Fasteners workbench fastener (typed FeaturePython)
  Placement = pos=(53,181.8,477.7) rot=(0,0,1;0rad)
  baseObject = -> XY_block_top_topM_002 [Edge159]
  diameter = 3
  invert = true
  length = 5
  matchOuter = false
  offset = 0
  thread = false
  type = 5
FEATURE [Part::FeaturePython] Nut064  label="M3-Nut081"  # Fasteners workbench fastener (typed FeaturePython)
  Placement = pos=(7,181.8,460.2) rot=(1,0,0;3.14159rad)
  baseObject = -> XY_block_topM_01001 [Edge233]
  diameter = 4
  invert = true
  matchOuter = false
  offset = 0
  thread = false
  type = 1
FEATURE [Part::FeaturePython] Nut065  label="M3-Nut082"  # Fasteners workbench fastener (typed FeaturePython)
  Placement = pos=(19,181.8,460.2) rot=(1,0,0;3.14159rad)
  baseObject = -> XY_block_topM_01001 [Edge234]
  diameter = 4
  invert = true
  matchOuter = false
  offset = 0
  thread = false
  type = 1
FEATURE [Part::FeaturePython] Nut066  label="M3-Nut083"  # Fasteners workbench fastener (typed FeaturePython)
  Placement = pos=(7,208.8,460.2) rot=(1,0,0;3.14159rad)
  baseObject = -> XY_block_topM_01001 [Edge232]
  diameter = 4
  invert = true
  matchOuter = false
  offset = 0
  thread = false
  type = 1
FEATURE [Part::FeaturePython] Nut067  label="M3-Nut084"  # Fasteners workbench fastener (typed FeaturePython)
  Placement = pos=(19,208.8,460.2) rot=(1,0,0;3.14159rad)
  baseObject = -> XY_block_topM_01001 [Edge229]
  diameter = 4
  invert = true
  matchOuter = false
  offset = 0
  thread = false
  type = 1
FEATURE [Part::FeaturePython] Nut068  label="M3-Nut085"  # Fasteners workbench fastener (typed FeaturePython)
  Placement = pos=(7,235.8,460.2) rot=(1,0,0;3.14159rad)
  baseObject = -> XY_block_topM_01001 [Edge230]
  diameter = 4
  invert = true
  matchOuter = false
  offset = 0
  thread = false
  type = 1
FEATURE [Part::FeaturePython] Nut069  label="M3-Nut086"  # Fasteners workbench fastener (typed FeaturePython)
  Placement = pos=(19,235.8,460.2) rot=(1,0,0;3.14159rad)
  baseObject = -> XY_block_topM_01001 [Edge231]
  diameter = 4
  invert = true
  matchOuter = false
  offset = 0
  thread = false
  type = 1
FEATURE [App::DocumentObjectGroup] Gruppe032  label="Screws004"
  Group = -> [DIN7965___Schraubeinsatz___M3_import021,DIN7965___Schraubeinsatz___M3_import022,DIN7965___Schraubeinsatz___M3_import023,DIN7965___Schraubeinsatz___M3_import024,Screw311,Screw312,Screw313,Screw314,Screw315,Screw316,Screw317,Screw318,Screw319,Screw320,Nut064,Nut065,Nut066,Nut067,Nut068,Nut069]
FEATURE [App::DocumentObjectGroup] Gruppe030  label="Left Slider"
  Group = -> [Gruppe031,Gruppe032,Gruppe033,Gruppe034]
FEATURE [Part::FeaturePython] Screw321  label="M3x20-Screw098"  # Fasteners workbench fastener (typed FeaturePython)
  Placement = pos=(433,235.8,477.7) rot=(0,0,1;0rad)
  baseObject = -> XY_block_top_topM_003 [Edge157]
  diameter = 3
  invert = true
  length = 6
  matchOuter = false
  offset = 0
  thread = false
  type = 5
FEATURE [Part::FeaturePython] Screw322  label="M3x20-Screw099"  # Fasteners workbench fastener (typed FeaturePython)
  Placement = pos=(421,235.8,477.7) rot=(0,0,1;0rad)
  baseObject = -> XY_block_top_topM_003 [Edge155]
  diameter = 3
  invert = true
  length = 6
  matchOuter = false
  offset = 0
  thread = false
  type = 5
FEATURE [Part::FeaturePython] Screw323  label="M3x20-Screw100"  # Fasteners workbench fastener (typed FeaturePython)
  Placement = pos=(433,208.8,477.7) rot=(0,0,1;0rad)
  baseObject = -> XY_block_top_topM_003 [Edge158]
  diameter = 3
  invert = true
  length = 6
  matchOuter = false
  offset = 0
  thread = false
  type = 5
FEATURE [Part::FeaturePython] Screw324  label="M3x20-Screw101"  # Fasteners workbench fastener (typed FeaturePython)
  Placement = pos=(421,208.8,477.7) rot=(0,0,1;0rad)
  baseObject = -> XY_block_top_topM_003 [Edge156]
  diameter = 3
  invert = true
  length = 6
  matchOuter = false
  offset = 0
  thread = false
  type = 5
FEATURE [Part::FeaturePython] Screw325  label="M3x20-Screw102"  # Fasteners workbench fastener (typed FeaturePython)
  Placement = pos=(433,181.8,477.7) rot=(0,0,1;0rad)
  baseObject = -> XY_block_top_topM_003 [Edge151]
  diameter = 3
  invert = true
  length = 6
  matchOuter = false
  offset = 0
  thread = false
  type = 5
FEATURE [Part::FeaturePython] Screw326  label="M3x20-Screw103"  # Fasteners workbench fastener (typed FeaturePython)
  Placement = pos=(421,181.8,477.7) rot=(0,0,1;0rad)
  baseObject = -> XY_block_top_topM_003 [Edge152]
  diameter = 3
  invert = true
  length = 6
  matchOuter = false
  offset = 0
  thread = false
  type = 5
FEATURE [Part::FeaturePython] Screw327  label="M3x16-Screw059"  # Fasteners workbench fastener (typed FeaturePython)
  Placement = pos=(387,235.8,477.7) rot=(0,0,1;0rad)
  baseObject = -> XY_block_top_topM_003 [Edge159]
  diameter = 3
  invert = true
  length = 5
  matchOuter = false
  offset = 0
  thread = false
  type = 5
FEATURE [Part::FeaturePython] Screw328  label="M3x16-Screw060"  # Fasteners workbench fastener (typed FeaturePython)
  Placement = pos=(387,221.8,477.7) rot=(0,0,1;0rad)
  baseObject = -> XY_block_top_topM_003 [Edge160]
  diameter = 3
  invert = true
  length = 5
  matchOuter = false
  offset = 0
  thread = false
  type = 5
FEATURE [Part::FeaturePython] Screw329  label="M3x16-Screw061"  # Fasteners workbench fastener (typed FeaturePython)
  Placement = pos=(387,195.8,477.7) rot=(0,0,1;0rad)
  baseObject = -> XY_block_top_topM_003 [Edge154]
  diameter = 3
  invert = true
  length = 5
  matchOuter = false
  offset = 0
  thread = false
  type = 5
FEATURE [Part::FeaturePython] Screw330  label="M3x16-Screw062"  # Fasteners workbench fastener (typed FeaturePython)
  Placement = pos=(387,181.8,477.7) rot=(0,0,1;0rad)
  baseObject = -> XY_block_top_topM_003 [Edge153]
  diameter = 3
  invert = true
  length = 5
  matchOuter = false
  offset = 0
  thread = false
  type = 5
FEATURE [Part::FeaturePython] Nut070  label="M3-Nut087"  # Fasteners workbench fastener (typed FeaturePython)
  Placement = pos=(421,181.8,460.2) rot=(1,0,0;3.14159rad)
  baseObject = -> XY_block_topM_01002 [Edge231]
  diameter = 4
  invert = true
  matchOuter = false
  offset = 0
  thread = false
  type = 1
FEATURE [Part::FeaturePython] Nut071  label="M3-Nut088"  # Fasteners workbench fastener (typed FeaturePython)
  Placement = pos=(433,181.8,460.2) rot=(1,0,0;3.14159rad)
  baseObject = -> XY_block_topM_01002 [Edge230]
  diameter = 4
  invert = true
  matchOuter = false
  offset = 0
  thread = false
  type = 1
FEATURE [Part::FeaturePython] Nut072  label="M3-Nut089"  # Fasteners workbench fastener (typed FeaturePython)
  Placement = pos=(421,208.8,460.2) rot=(1,0,0;3.14159rad)
  baseObject = -> XY_block_topM_01002 [Edge229]
  diameter = 4
  invert = true
  matchOuter = false
  offset = 0
  thread = false
  type = 1
FEATURE [Part::FeaturePython] Nut073  label="M3-Nut090"  # Fasteners workbench fastener (typed FeaturePython)
  Placement = pos=(433,208.8,460.2) rot=(1,0,0;3.14159rad)
  baseObject = -> XY_block_topM_01002 [Edge232]
  diameter = 4
  invert = true
  matchOuter = false
  offset = 0
  thread = false
  type = 1
FEATURE [Part::FeaturePython] Nut074  label="M3-Nut091"  # Fasteners workbench fastener (typed FeaturePython)
  Placement = pos=(421,235.8,460.2) rot=(1,0,0;3.14159rad)
  baseObject = -> XY_block_topM_01002 [Edge234]
  diameter = 4
  invert = true
  matchOuter = false
  offset = 0
  thread = false
  type = 1
FEATURE [Part::FeaturePython] Nut075  label="M3-Nut092"  # Fasteners workbench fastener (typed FeaturePython)
  Placement = pos=(433,235.8,460.2) rot=(1,0,0;3.14159rad)
  baseObject = -> XY_block_topM_01002 [Edge233]
  diameter = 4
  invert = true
  matchOuter = false
  offset = 0
  thread = false
  type = 1
FEATURE [App::DocumentObjectGroup] Gruppe037  label="Screws005"
  Group = -> [DIN7965___Schraubeinsatz___M3_import031,DIN7965___Schraubeinsatz___M3_import033,DIN7965___Schraubeinsatz___M3_import032,DIN7965___Schraubeinsatz___M3_import034,Screw321,Screw322,Screw323,Screw324,Screw325,Screw326,Screw327,Screw328,Screw329,Screw330,Nut070,Nut071,Nut072,Nut073,Nut074,Nut075]
FEATURE [App::DocumentObjectGroup] Gruppe035  label="Right Slider"
  Group = -> [Gruppe036,Gruppe037,Gruppe038,Gruppe039]
FEATURE [App::DocumentObjectGroup] Gruppe058  label="60x60 Carrier"
  Group = -> [Gruppe030,Gruppe035,Gruppe040,Gruppe067]
FEATURE [App::DocumentObjectGroup] Gruppe121  label="Horizontal Carriers"
  Group = -> [Gruppe059,Gruppe058,Gruppe104,Gruppe108]
FEATURE [Part::FeaturePython] Washer240  label="M4-Washer496"  # Fasteners workbench fastener (typed FeaturePython)
  Placement = pos=(395,76,439.5) rot=(0,-1,0;1.5708rad)
  baseObject = -> Z_axis_clamp_2_01 [Edge21]
  diameter = 5
  invert = false
  matchOuter = false
  offset = 0
  type = 0
FEATURE [Part::FeaturePython] Washer241  label="M4-Washer497"  # Fasteners workbench fastener (typed FeaturePython)
  Placement = pos=(395,54,439.5) rot=(0,-1,0;1.5708rad)
  baseObject = -> Z_axis_clamp_2_01 [Edge24]
  diameter = 5
  invert = false
  matchOuter = false
  offset = 0
  type = 0
FEATURE [Part::FeaturePython] Washer242  label="M4-Washer494"  # Fasteners workbench fastener (typed FeaturePython)
  Placement = pos=(173.82,393,439.5) rot=(1,0,0;1.5708rad)
  baseObject = -> Z_axis_clamp_2_01002 [Edge21]
  diameter = 5
  invert = false
  matchOuter = false
  offset = 0
  type = 0
FEATURE [Part::FeaturePython] Washer243  label="M4-Washer495"  # Fasteners workbench fastener (typed FeaturePython)
  Placement = pos=(195.82,393,439.5) rot=(1,0,0;1.5708rad)
  baseObject = -> Z_axis_clamp_2_01002 [Edge24]
  diameter = 5
  invert = false
  matchOuter = false
  offset = 0
  type = 0
FEATURE [Part::FeaturePython] Washer244  label="M4-Washer492"  # Fasteners workbench fastener (typed FeaturePython)
  Placement = pos=(45,54,439.5) rot=(0,1,0;1.5708rad)
  baseObject = -> Z_axis_clamp_2_01003 [Edge21]
  diameter = 5
  invert = false
  matchOuter = false
  offset = 0
  type = 0
FEATURE [Part::FeaturePython] Washer245  label="M4-Washer493"  # Fasteners workbench fastener (typed FeaturePython)
  Placement = pos=(45,76,439.5) rot=(0,1,0;1.5708rad)
  baseObject = -> Z_axis_clamp_2_01003 [Edge24]
  diameter = 5
  invert = false
  matchOuter = false
  offset = 0
  type = 0
FEATURE [Part::FeaturePython] Screw331  label="M4x30-Screw051"  # Fasteners workbench fastener (typed FeaturePython)
  Placement = pos=(45.9,54,439.5) rot=(0,1,0;1.5708rad)
  baseObject = -> Washer244 [Edge1]
  diameter = 4
  invert = false
  length = 7
  matchOuter = false
  offset = 0
  thread = false
  type = 5
FEATURE [Part::FeaturePython] Screw332  label="M4x30-Screw052"  # Fasteners workbench fastener (typed FeaturePython)
  Placement = pos=(45.9,76,439.5) rot=(0,1,0;1.5708rad)
  baseObject = -> Washer245 [Edge1]
  diameter = 4
  invert = false
  length = 7
  matchOuter = false
  offset = 0
  thread = false
  type = 5
FEATURE [Part::FeaturePython] Screw333  label="M4x30-Screw053"  # Fasteners workbench fastener (typed FeaturePython)
  Placement = pos=(173.82,392.1,439.5) rot=(1,0,0;1.5708rad)
  baseObject = -> Washer242 [Edge1]
  diameter = 4
  invert = false
  length = 7
  matchOuter = false
  offset = 0
  thread = false
  type = 5
FEATURE [Part::FeaturePython] Screw334  label="M4x30-Screw054"  # Fasteners workbench fastener (typed FeaturePython)
  Placement = pos=(195.82,392.1,439.5) rot=(1,0,0;1.5708rad)
  baseObject = -> Washer243 [Edge1]
  diameter = 4
  invert = false
  length = 7
  matchOuter = false
  offset = 0
  thread = false
  type = 5
FEATURE [Part::FeaturePython] Screw335  label="M4x30-Screw055"  # Fasteners workbench fastener (typed FeaturePython)
  Placement = pos=(394.1,76,439.5) rot=(0,-1,0;1.5708rad)
  baseObject = -> Washer240 [Edge1]
  diameter = 4
  invert = false
  length = 7
  matchOuter = false
  offset = 0
  thread = false
  type = 5
FEATURE [Part::FeaturePython] Screw336  label="M4x30-Screw056"  # Fasteners workbench fastener (typed FeaturePython)
  Placement = pos=(394.1,54,439.5) rot=(0,-1,0;1.5708rad)
  baseObject = -> Washer241 [Edge1]
  diameter = 4
  invert = false
  length = 7
  matchOuter = false
  offset = 0
  thread = false
  type = 5
FEATURE [Part::FeaturePython] Washer246  label="M4-Washer498"  # Fasteners workbench fastener (typed FeaturePython)
  Placement = pos=(82.5,30,110) rot=(-1,0,0;1.5708rad)
  baseObject = -> Z_leadscrew_edge_bearing_block_01001 [Edge65]
  diameter = 5
  invert = true
  matchOuter = false
  offset = 0
  type = 0
FEATURE [Part::FeaturePython] Washer247  label="M4-Washer499"  # Fasteners workbench fastener (typed FeaturePython)
  Placement = pos=(44,74,110) rot=(0,1,0;1.5708rad)
  baseObject = -> Z_leadscrew_edge_bearing_block_01001 [Edge67]
  diameter = 5
  invert = true
  matchOuter = false
  offset = 0
  type = 0
FEATURE [Part::FeaturePython] Screw337  label="M4x16-Screw005"  # Fasteners workbench fastener (typed FeaturePython)
  Placement = pos=(82.5,30.9,110) rot=(-1,0,0;1.5708rad)
  baseObject = -> Washer246 [Edge1]
  diameter = 4
  invert = false
  length = 4
  matchOuter = false
  offset = 0
  thread = false
  type = 5
FEATURE [Part::FeaturePython] Screw338  label="M4x30-Screw057"  # Fasteners workbench fastener (typed FeaturePython)
  Placement = pos=(44.9,74,110) rot=(0,1,0;1.5708rad)
  baseObject = -> Washer247 [Edge1]
  diameter = 4
  invert = false
  length = 7
  matchOuter = false
  offset = 0
  thread = false
  type = 5
FEATURE [Part::FeaturePython] Washer248  label="M4-Washer500"  # Fasteners workbench fastener (typed FeaturePython)
  Placement = pos=(396,74,110) rot=(0,-1,0;1.5708rad)
  baseObject = -> Z_leadscrew_edge_bearing_block_01 [Edge67]
  diameter = 5
  invert = true
  matchOuter = false
  offset = 0
  type = 0
FEATURE [Part::FeaturePython] Washer249  label="M4-Washer501"  # Fasteners workbench fastener (typed FeaturePython)
  Placement = pos=(357.5,30,110) rot=(-1,0,0;1.5708rad)
  baseObject = -> Z_leadscrew_edge_bearing_block_01 [Edge65]
  diameter = 5
  invert = true
  matchOuter = false
  offset = 0
  type = 0
FEATURE [Part::FeaturePython] Screw339  label="M4x30-Screw058"  # Fasteners workbench fastener (typed FeaturePython)
  Placement = pos=(395.1,74,110) rot=(0,-1,0;1.5708rad)
  baseObject = -> Washer248 [Edge1]
  diameter = 4
  invert = false
  length = 7
  matchOuter = false
  offset = 0
  thread = false
  type = 5
FEATURE [Part::FeaturePython] Screw340  label="M4x16-Screw006"  # Fasteners workbench fastener (typed FeaturePython)
  Placement = pos=(357.5,30.9,110) rot=(-1,0,0;1.5708rad)
  baseObject = -> Washer249 [Edge1]
  diameter = 4
  invert = false
  length = 4
  matchOuter = false
  offset = 0
  thread = false
  type = 5
FEATURE [Part::FeaturePython] Washer250  label="M4-Washer502"  # Fasteners workbench fastener (typed FeaturePython)
  Placement = pos=(174.82,395,110) rot=(1,0,0;1.5708rad)
  baseObject = -> Z_leadscrew_back_bearing_block_01 [Edge102]
  diameter = 5
  invert = false
  matchOuter = false
  offset = 0
  type = 0
FEATURE [Part::FeaturePython] Washer251  label="M4-Washer503"  # Fasteners workbench fastener (typed FeaturePython)
  Placement = pos=(241.57,390.361,110) rot=(1,0,0;1.5708rad)
  baseObject = -> Z_leadscrew_back_bearing_block_01 [Edge104]
  diameter = 5
  invert = false
  matchOuter = false
  offset = 0
  type = 0
FEATURE [Part::FeaturePython] Washer252  label="M4-Washer504"  # Fasteners workbench fastener (typed FeaturePython)
  Placement = pos=(306.82,415.5,110) rot=(1,0,0;1.5708rad)
  baseObject = -> Z_leadscrew_back_bearing_block_01 [Edge106]
  diameter = 5
  invert = false
  matchOuter = false
  offset = 0
  type = 0
FEATURE [Part::FeaturePython] Screw341  label="M4x30-Screw059"  # Fasteners workbench fastener (typed FeaturePython)
  Placement = pos=(174.82,394.1,110) rot=(1,0,0;1.5708rad)
  baseObject = -> Washer250 [Edge1]
  diameter = 4
  invert = false
  length = 7
  matchOuter = false
  offset = 0
  thread = false
  type = 5
FEATURE [Part::FeaturePython] Screw342  label="M4x35-Screw"  # Fasteners workbench fastener (typed FeaturePython)
  Placement = pos=(241.57,389.461,110) rot=(1,0,0;1.5708rad)
  baseObject = -> Washer251 [Edge1]
  diameter = 4
  invert = false
  length = 8
  matchOuter = false
  offset = 0
  thread = false
  type = 5
FEATURE [Part::FeaturePython] Screw343  label="M4x10-Screw244"  # Fasteners workbench fastener (typed FeaturePython)
  Placement = pos=(306.82,414.6,110) rot=(1,0,0;1.5708rad)
  baseObject = -> Washer252 [Edge1]
  diameter = 4
  invert = false
  length = 2
  matchOuter = false
  offset = 0
  thread = false
  type = 5
FEATURE [Part::FeaturePython] Washer253  label="M4-Washer630"  # Fasteners workbench fastener (typed FeaturePython)
  Placement = pos=(220.35,220.05,80.8) rot=(1,0,0;3.14159rad)
  baseObject = -> F624zz_import021 [Edge8]
  diameter = 5
  invert = true
  matchOuter = false
  offset = 0
  type = 0
FEATURE [Part::FeaturePython] Washer254  label="M4-Washer631"  # Fasteners workbench fastener (typed FeaturePython)
  Placement = pos=(286.35,220.05,80.8) rot=(1,0,0;3.14159rad)
  baseObject = -> F624zz_import022 [Edge8]
  diameter = 5
  invert = true
  matchOuter = false
  offset = 0
  type = 0
FEATURE [Part::FeaturePython] Screw344  label="M4x25-Screw"  # Fasteners workbench fastener (typed FeaturePython)
  Placement = pos=(220.35,220.05,79.9) rot=(1,0,0;3.14159rad)
  baseObject = -> Washer253 [Edge1]
  diameter = 4
  invert = false
  length = 6
  matchOuter = false
  offset = 0
  thread = false
  type = 5
FEATURE [Part::FeaturePython] Screw345  label="M4x25-Screw001"  # Fasteners workbench fastener (typed FeaturePython)
  Placement = pos=(286.35,220.05,79.9) rot=(1,0,0;3.14159rad)
  baseObject = -> Washer254 [Edge1]
  diameter = 4
  invert = false
  length = 6
  matchOuter = false
  offset = 0
  thread = false
  type = 5
FEATURE [Part::FeaturePython] z_Pulley_Holder_02  label="z_Pulley_Holder"  # a2plus imported part (geometry in sourceFile) (typed FeaturePython)
  Placement = pos=(286.35,220.05,100) rot=(1,0,0;3.14159rad)
  fixedPosition = false
  sourceFile = <userpath>/CloudStation/Hobbyprojekte/3D Drucker/CoreXY/Assembly/Parts/Printed Parts/z_Pulley_Holder.FCStd
  timeLastImport = 1458328100
  updateColors = true
FEATURE [Part::FeaturePython] z_Pulley_Holder_003  label="z_Pulley_Holder001"  # a2plus imported part (geometry in sourceFile) (typed FeaturePython)
  Placement = pos=(220.35,220.05,100) rot=(1,0,0;3.14159rad)
  fixedPosition = false
  sourceFile = <userpath>/CloudStation/Hobbyprojekte/3D Drucker/CoreXY/Assembly/Parts/Printed Parts/z_Pulley_Holder.FCStd
  timeLastImport = 1458328100
  updateColors = true
FEATURE [App::DocumentObjectGroup] Gruppe117  label="Printed Parts"
  Group = -> [Z_axis_clamp_2_01003,Z_axis_clamp_2_01002,Z_axis_clamp_1_01002,Z_leadscrew_edge_bearing_block_01001,Z_leadscrew_edge_bearing_block_01,Z_axis_clamp_1_01,Z_axis_clamp_2_01,Z_axis_clamp_1_01001,Z_leadscrew_back_bearing_block_01,z_Pulley_Holder_02,z_Pulley_Holder_003]
FEATURE [Part::FeaturePython] Washer255  label="M4-Washer710"  # Fasteners workbench fastener (typed FeaturePython)
  Placement = pos=(220.35,220.05,90.8) rot=(0,0,1;0rad)
  baseObject = -> DIN625_1_624_ZZ_import01027 [Edge29]
  diameter = 5
  invert = false
  matchOuter = false
  offset = 0
  type = 0
FEATURE [Part::FeaturePython] Washer256  label="M4-Washer711"  # Fasteners workbench fastener (typed FeaturePython)
  Placement = pos=(286.35,220.05,90.8) rot=(0,0,1;0rad)
  baseObject = -> DIN625_1_624_ZZ_import01028 [Edge29]
  diameter = 5
  invert = false
  matchOuter = false
  offset = 0
  type = 0
FEATURE [Part::FeaturePython] Screw346  label="M3x12-Screw002"  # Fasteners workbench fastener (typed FeaturePython)
  Placement = pos=(258.07,380.5,103) rot=(1,0,0;3.14159rad)
  baseObject = -> Z_leadscrew_back_bearing_block_01 [Edge109]
  diameter = 3
  invert = false
  length = 4
  matchOuter = false
  offset = 0
  thread = false
  type = 5
FEATURE [Part::FeaturePython] Screw347  label="M3x12-Screw003"  # Fasteners workbench fastener (typed FeaturePython)
  Placement = pos=(289.07,380.5,103) rot=(1,0,0;3.14159rad)
  baseObject = -> Z_leadscrew_back_bearing_block_01 [Edge112]
  diameter = 3
  invert = false
  length = 4
  matchOuter = false
  offset = 0
  thread = false
  type = 5
FEATURE [Part::FeaturePython] Screw348  label="M3x12-Screw004"  # Fasteners workbench fastener (typed FeaturePython)
  Placement = pos=(258.07,411.5,103) rot=(1,0,0;3.14159rad)
  baseObject = -> Z_leadscrew_back_bearing_block_01 [Edge110]
  diameter = 3
  invert = false
  length = 4
  matchOuter = false
  offset = 0
  thread = false
  type = 5
FEATURE [Part::FeaturePython] Screw349  label="M3x12-Screw005"  # Fasteners workbench fastener (typed FeaturePython)
  Placement = pos=(289.07,411.5,103) rot=(1,0,0;3.14159rad)
  baseObject = -> Z_leadscrew_back_bearing_block_01 [Edge125]
  diameter = 3
  invert = false
  length = 4
  matchOuter = false
  offset = 0
  thread = false
  type = 5
FEATURE [Part::FeaturePython] Screw350  label="M3x5-Screw"  # Fasteners workbench fastener (typed FeaturePython)
  Placement = pos=(208.129,404.75,100) rot=(1,0,0;3.14159rad)
  baseObject = -> Z_leadscrew_back_bearing_block_01 [Edge20]
  diameter = 1
  invert = true
  length = 1
  matchOuter = false
  offset = 0
  thread = false
  type = 0
FEATURE [Part::FeaturePython] Screw351  label="M3x5-Screw001"  # Fasteners workbench fastener (typed FeaturePython)
  Placement = pos=(219.82,384.5,100) rot=(1,0,0;3.14159rad)
  baseObject = -> Z_leadscrew_back_bearing_block_01 [Edge23]
  diameter = 1
  invert = true
  length = 1
  matchOuter = false
  offset = 0
  thread = false
  type = 0
FEATURE [Part::FeaturePython] Screw352  label="M3x5-Screw002"  # Fasteners workbench fastener (typed FeaturePython)
  Placement = pos=(231.511,404.75,100) rot=(1,0,0;3.14159rad)
  baseObject = -> Z_leadscrew_back_bearing_block_01 [Edge22]
  diameter = 1
  invert = true
  length = 1
  matchOuter = false
  offset = 0
  thread = false
  type = 0
FEATURE [Part::FeaturePython] Screw353  label="M3x5-Screw003"  # Fasteners workbench fastener (typed FeaturePython)
  Placement = pos=(208.129,404.75,120) rot=(0,0,1;0rad)
  baseObject = -> Z_leadscrew_back_bearing_block_01 [Edge73]
  diameter = 1
  invert = false
  length = 1
  matchOuter = false
  offset = 0
  thread = false
  type = 0
FEATURE [Part::FeaturePython] Screw354  label="M3x5-Screw004"  # Fasteners workbench fastener (typed FeaturePython)
  Placement = pos=(219.82,384.5,120) rot=(0,0,1;0rad)
  baseObject = -> Z_leadscrew_back_bearing_block_01 [Edge79]
  diameter = 1
  invert = false
  length = 1
  matchOuter = false
  offset = 0
  thread = false
  type = 0
FEATURE [Part::FeaturePython] Screw355  label="M3x5-Screw005"  # Fasteners workbench fastener (typed FeaturePython)
  Placement = pos=(231.511,404.75,120) rot=(0,0,1;0rad)
  baseObject = -> Z_leadscrew_back_bearing_block_01 [Edge77]
  diameter = 1
  invert = false
  length = 1
  matchOuter = false
  offset = 0
  thread = false
  type = 0
FEATURE [Part::FeaturePython] Screw356  label="M3x5-Screw006"  # Fasteners workbench fastener (typed FeaturePython)
  Placement = pos=(51.5059,55.04,120) rot=(0,0,1;0rad)
  baseObject = -> Z_leadscrew_edge_bearing_block_01001 [Edge36]
  diameter = 1
  invert = false
  length = 1
  matchOuter = false
  offset = 0
  thread = false
  type = 0
FEATURE [Part::FeaturePython] Screw357  label="M3x5-Screw007"  # Fasteners workbench fastener (typed FeaturePython)
  Placement = pos=(68.04,38.5059,120) rot=(0,0,1;0rad)
  baseObject = -> Z_leadscrew_edge_bearing_block_01001 [Edge39]
  diameter = 1
  invert = false
  length = 1
  matchOuter = false
  offset = 0
  thread = false
  type = 0
FEATURE [Part::FeaturePython] Screw358  label="M3x5-Screw008"  # Fasteners workbench fastener (typed FeaturePython)
  Placement = pos=(45.4541,32.4541,120) rot=(0,0,1;0rad)
  baseObject = -> Z_leadscrew_edge_bearing_block_01001 [Edge37]
  diameter = 1
  invert = false
  length = 1
  matchOuter = false
  offset = 0
  thread = false
  type = 0
FEATURE [Part::FeaturePython] Screw359  label="M3x5-Screw009"  # Fasteners workbench fastener (typed FeaturePython)
  Placement = pos=(388.494,55.04,120) rot=(0,0,1;0rad)
  baseObject = -> Z_leadscrew_edge_bearing_block_01 [Edge22]
  diameter = 1
  invert = true
  length = 1
  matchOuter = false
  offset = 0
  thread = false
  type = 0
FEATURE [Part::FeaturePython] Screw360  label="M3x5-Screw010"  # Fasteners workbench fastener (typed FeaturePython)
  Placement = pos=(371.96,38.5059,120) rot=(0,0,1;0rad)
  baseObject = -> Z_leadscrew_edge_bearing_block_01 [Edge25]
  diameter = 1
  invert = true
  length = 1
  matchOuter = false
  offset = 0
  thread = false
  type = 0
FEATURE [Part::FeaturePython] Screw361  label="M3x5-Screw011"  # Fasteners workbench fastener (typed FeaturePython)
  Placement = pos=(394.546,32.4541,120) rot=(0,0,1;0rad)
  baseObject = -> Z_leadscrew_edge_bearing_block_01 [Edge23]
  diameter = 1
  invert = true
  length = 1
  matchOuter = false
  offset = 0
  thread = false
  type = 0
FEATURE [Part::FeaturePython] Screw362  label="M3x5-Screw012"  # Fasteners workbench fastener (typed FeaturePython)
  Placement = pos=(388.494,55.04,100) rot=(1,0,0;3.14159rad)
  baseObject = -> Z_leadscrew_edge_bearing_block_01 [Edge36]
  diameter = 1
  invert = false
  length = 1
  matchOuter = false
  offset = 0
  thread = false
  type = 0
FEATURE [Part::FeaturePython] Screw363  label="M3x5-Screw013"  # Fasteners workbench fastener (typed FeaturePython)
  Placement = pos=(371.96,38.5059,100) rot=(1,0,0;3.14159rad)
  baseObject = -> Z_leadscrew_edge_bearing_block_01 [Edge39]
  diameter = 1
  invert = false
  length = 1
  matchOuter = false
  offset = 0
  thread = false
  type = 0
FEATURE [Part::FeaturePython] Screw364  label="M3x5-Screw014"  # Fasteners workbench fastener (typed FeaturePython)
  Placement = pos=(394.546,32.4541,100) rot=(1,0,0;3.14159rad)
  baseObject = -> Z_leadscrew_edge_bearing_block_01 [Edge37]
  diameter = 1
  invert = false
  length = 1
  matchOuter = false
  offset = 0
  thread = false
  type = 0
FEATURE [Part::FeaturePython] Screw365  label="M3x5-Screw015"  # Fasteners workbench fastener (typed FeaturePython)
  Placement = pos=(68.04,38.5059,100) rot=(1,0,0;3.14159rad)
  baseObject = -> Z_leadscrew_edge_bearing_block_01001 [Edge25]
  diameter = 1
  invert = true
  length = 1
  matchOuter = false
  offset = 0
  thread = false
  type = 0
FEATURE [Part::FeaturePython] Screw366  label="M3x5-Screw016"  # Fasteners workbench fastener (typed FeaturePython)
  Placement = pos=(51.5059,55.04,100) rot=(1,0,0;3.14159rad)
  baseObject = -> Z_leadscrew_edge_bearing_block_01001 [Edge22]
  diameter = 1
  invert = true
  length = 1
  matchOuter = false
  offset = 0
  thread = false
  type = 0
FEATURE [Part::FeaturePython] Screw367  label="M3x5-Screw017"  # Fasteners workbench fastener (typed FeaturePython)
  Placement = pos=(45.4541,32.4541,100) rot=(1,0,0;3.14159rad)
  baseObject = -> Z_leadscrew_edge_bearing_block_01001 [Edge23]
  diameter = 1
  invert = true
  length = 1
  matchOuter = false
  offset = 0
  thread = false
  type = 0
FEATURE [App::DocumentObjectGroup] Gruppe116  label="Screws013"
  Group = -> [Hammermutter_B_Typ_Nut6_M4_import01096,Hammermutter_B_Typ_Nut6_M4_import01095,Hammermutter_B_Typ_Nut6_M4_import01094,Hammermutter_B_Typ_Nut6_M4_import01090,Hammermutter_B_Typ_Nut6_M4_import01093,Hammermutter_B_Typ_Nut6_M4_import01091,Hammermutter_B_Typ_Nut6_M4_import01092,Hammermutter_B_Typ_Nut6_M4_import01056,Hammermutter_B_Typ_Nut6_M4_import01057,Hammermutter_B_Typ_Nut6_M4_import01058,+59 more]
FEATURE [App::DocumentObjectGroup] Gruppe103  label="z-Slide"
  Group = -> [Gruppe115,Gruppe116,Gruppe117,Gruppe118]
FEATURE [Part::FeaturePython] LM8uu_025  # a2plus imported part (geometry in sourceFile) (typed FeaturePython)
  Placement = pos=(13,196.6,470.2) rot=(0,0,1;3.14159rad)
  fixedPosition = false
  sourceFile = <userpath>/CloudStation/Hobbyprojekte/3D Drucker/CoreXY/Assembly/Parts/Bearings/LM8uu.fcstd
  timeLastImport = 1430143348
  updateColors = true
FEATURE [Part::FeaturePython] LM8uu_026  # a2plus imported part (geometry in sourceFile) (typed FeaturePython)
  Placement = pos=(13,220.6,470.2) rot=(0,0,1;3.14159rad)
  fixedPosition = true
  sourceFile = <userpath>/CloudStation/Hobbyprojekte/3D Drucker/CoreXY/Assembly/Parts/Bearings/LM8uu.fcstd
  timeLastImport = 1430143348
  updateColors = true
FEATURE [Part::FeaturePython] F624zz_import024  # a2plus imported part (geometry in sourceFile) (typed FeaturePython)
  Placement = pos=(37.7,215.9,459.5) rot=(0,0,1;3.14159rad)
  fixedPosition = false
  sourceFile = <userpath>/CloudStation/Hobbyprojekte/3D Drucker/CoreXY/Assembly/Parts/Bearings/DIN625-1_F624zz.FCStd
  timeLastImport = 1430848638
FEATURE [Part::FeaturePython] DIN625_1_624_ZZ_import01030  # a2plus imported part (geometry in sourceFile) (typed FeaturePython)
  Placement = pos=(37.7,215.9,464.5) rot=(0,0,1;3.14159rad)
  fixedPosition = false
  sourceFile = <userpath>/CloudStation/Hobbyprojekte/3D Drucker/CoreXY/Assembly/Parts/Bearings/DIN625-1_624-ZZ.FCStd
  timeLastImport = 1430517302
  updateColors = true
FEATURE [Part::FeaturePython] GT2Bearing_011  # a2plus imported part (geometry in sourceFile) (typed FeaturePython)
  Placement = pos=(37.7,201.5,470.21) rot=(0,0,1;0rad)
  fixedPosition = false
  sourceFile = <userpath>/CloudStation/Hobbyprojekte/3D Drucker/CoreXY/Assembly/Parts/Belts/GT2Bearing.FCStd
  timeLastImport = 1444935738
  updateColors = true
FEATURE [App::DocumentObjectGroup] Gruppe157  label="Bearings015"
  Group = -> [F624zz_import024,DIN625_1_624_ZZ_import01030,GT2Bearing_011]
FEATURE [Part::FeaturePython] CustomBushingXYBlock_LM8UU_003  # a2plus imported part (geometry in sourceFile) (typed FeaturePython)
  Placement = pos=(3,241.4,470.2) rot=(0,0,-1;1.5708rad)
  fixedPosition = true
  sourceFile = <userpath>/CloudStation/Hobbyprojekte/3D Drucker/CoreXY/Assembly/Parts/Printed Parts/CustomBushingXYBlock_LM8UU.FCStd
  timeLastImport = 1458171204
  updateColors = true
FEATURE [Part::FeaturePython] CustomBushingXYBlock_LM8UU_004  # a2plus imported part (geometry in sourceFile) (typed FeaturePython)
  Placement = pos=(3,176,470.2) rot=(0.707107,0.707107,0;3.14159rad)
  fixedPosition = true
  sourceFile = <userpath>/CloudStation/Hobbyprojekte/3D Drucker/CoreXY/Assembly/Parts/Printed Parts/CustomBushingXYBlock_LM8UU.FCStd
  timeLastImport = 1458171204
  updateColors = true
FEATURE [Part::FeaturePython] spacer10_0mm_002  # a2plus imported part (geometry in sourceFile) (typed FeaturePython)
  Placement = pos=(37.7,215.9,471.8) rot=(0,0,1;3.14159rad)
  fixedPosition = false
  sourceFile = <userpath>/CloudStation/Hobbyprojekte/3D Drucker/CoreXY/Assembly/Parts/Printed Parts/spacer10_0mm.FCStd
  timeLastImport = 1458256983
  updateColors = true
FEATURE [Part::FeaturePython] Washer257  label="M4-Washer575"  # Fasteners workbench fastener (typed FeaturePython)
  Placement = pos=(37.7,201.5,496.627) rot=(0,0,1;0rad)
  baseObject = -> CustomBushingXYBlock_LM8UU_003 [Edge141]
  diameter = 5
  invert = false
  matchOuter = false
  offset = 0
  type = 0
FEATURE [Part::FeaturePython] Washer258  label="M4-Washer576"  # Fasteners workbench fastener (typed FeaturePython)
  Placement = pos=(37.7,215.9,496.627) rot=(0,0,1;0rad)
  baseObject = -> CustomBushingXYBlock_LM8UU_003 [Edge139]
  diameter = 5
  invert = false
  matchOuter = false
  offset = 0
  type = 0
FEATURE [Part::FeaturePython] Washer259  label="M4-Washer554"  # Fasteners workbench fastener (typed FeaturePython)
  Placement = pos=(37.7,201.5,443.773) rot=(1,0,0;3.14159rad)
  baseObject = -> CustomBushingXYBlock_LM8UU_004 [Edge139]
  diameter = 5
  invert = false
  matchOuter = false
  offset = 0
  type = 0
FEATURE [Part::FeaturePython] Washer260  label="M4-Washer555"  # Fasteners workbench fastener (typed FeaturePython)
  Placement = pos=(37.7,215.9,443.773) rot=(1,0,0;3.14159rad)
  baseObject = -> CustomBushingXYBlock_LM8UU_004 [Edge141]
  diameter = 5
  invert = false
  matchOuter = false
  offset = 0
  type = 0
FEATURE [Part::FeaturePython] Nut076  label="M4-Nut070"  # Fasteners workbench fastener (typed FeaturePython)
  Placement = pos=(37.7,201.5,497.527) rot=(0,0,1;0rad)
  baseObject = -> Washer257 [Edge1]
  diameter = 6
  invert = false
  matchOuter = false
  offset = 0
  thread = false
  type = 1
FEATURE [Part::FeaturePython] Nut077  label="M4-Nut071"  # Fasteners workbench fastener (typed FeaturePython)
  Placement = pos=(37.7,215.9,497.527) rot=(0,0,1;0rad)
  baseObject = -> Washer258 [Edge1]
  diameter = 6
  invert = false
  matchOuter = false
  offset = 0
  thread = false
  type = 1
FEATURE [Part::FeaturePython] Nut078  label="M4-Nut058"  # Fasteners workbench fastener (typed FeaturePython)
  Placement = pos=(37.7,201.5,442.873) rot=(1,0,0;3.14159rad)
  baseObject = -> Washer259 [Edge1]
  diameter = 6
  invert = false
  matchOuter = false
  offset = 0
  thread = false
  type = 1
FEATURE [Part::FeaturePython] Nut079  label="M4-Nut059"  # Fasteners workbench fastener (typed FeaturePython)
  Placement = pos=(37.7,215.9,442.873) rot=(1,0,0;3.14159rad)
  baseObject = -> Washer260 [Edge1]
  diameter = 6
  invert = false
  matchOuter = false
  offset = 0
  thread = false
  type = 1
FEATURE [Part::FeaturePython] ScrewTap004  label="M4x62.0-ScrewTap"  # Fasteners workbench fastener (typed FeaturePython)
  Placement = pos=(37.7,201.5,500.927) rot=(0,0,1;0rad)
  baseObject = -> CustomBushingXYBlock_LM8UU_003 [Edge141]
  diameter = 6
  invert = false
  length = 62
  matchOuter = false
  offset = 4.3
  thread = false
FEATURE [Part::FeaturePython] ScrewTap005  label="M4x62.0-ScrewTap004"  # Fasteners workbench fastener (typed FeaturePython)
  Placement = pos=(37.7,215.9,500.927) rot=(0,0,1;0rad)
  baseObject = -> CustomBushingXYBlock_LM8UU_003 [Edge139]
  diameter = 6
  invert = false
  length = 62
  matchOuter = false
  offset = 4.3
  thread = false
FEATURE [Part::FeaturePython] Washer261  label="M4-Washer703"  # Fasteners workbench fastener (typed FeaturePython)
  Placement = pos=(37.7,215.9,469.5) rot=(0,0,1;0rad)
  baseObject = -> DIN625_1_624_ZZ_import01030 [Edge29]
  diameter = 5
  invert = false
  matchOuter = false
  offset = 0
  type = 2
FEATURE [Part::FeaturePython] Washer262  label="M4-Washer704"  # Fasteners workbench fastener (typed FeaturePython)
  Placement = pos=(37.7,215.9,470.05) rot=(0,0,1;0rad)
  baseObject = -> Washer261 [Edge1]
  diameter = 5
  invert = false
  matchOuter = false
  offset = 0
  type = 0
FEATURE [Part::FeaturePython] Washer263  label="M4-Washer705"  # Fasteners workbench fastener (typed FeaturePython)
  Placement = pos=(37.7,215.9,470.95) rot=(0,0,1;0rad)
  baseObject = -> Washer262 [Edge1]
  diameter = 5
  invert = false
  matchOuter = false
  offset = 0
  type = 0
FEATURE [Part::FeaturePython] Washer264  label="M4-Washer587"  # Fasteners workbench fastener (typed FeaturePython)
  Placement = pos=(37.7,201.5,479.45) rot=(0,0,1;0rad)
  baseObject = -> GT2Bearing_011 [Edge566]
  diameter = 5
  invert = true
  matchOuter = false
  offset = 0
  type = 2
FEATURE [Part::FeaturePython] Washer267  label="M4-Washer629"  # Fasteners workbench fastener (typed FeaturePython)
  Placement = pos=(37.7,215.9,459.5) rot=(1,0,0;3.14159rad)
  baseObject = -> F624zz_import024 [Edge8]
  diameter = 5
  invert = true
  matchOuter = false
  offset = 0
  type = 0
FEATURE [Part::FeaturePython] Washer268  label="M4-Washer588"  # Fasteners workbench fastener (typed FeaturePython)
  Placement = pos=(37.7,201.5,470.57) rot=(1,0,0;3.14159rad)
  baseObject = -> GT2Bearing_011 [Edge336]
  diameter = 5
  invert = false
  matchOuter = false
  offset = 0
  type = 2
FEATURE [Part::FeaturePython] smooth_bar_8x430_01  # a2plus imported part (geometry in sourceFile) (typed FeaturePython)
  Placement = pos=(434.775,208.7,447.7) rot=(-0.57735,-0.57735,0.57735;2.0944rad)
  fixedPosition = false
  sourceFile = <userpath>/CloudStation/Hobbyprojekte/3D Drucker/CoreXY/Assembly/Parts/Bearings/smooth-bar-8x430.FCStd
  timeLastImport = 1458331381
  updateColors = true
FEATURE [Part::FeaturePython] smooth_bar_8x430_002  # a2plus imported part (geometry in sourceFile) (typed FeaturePython)
  Placement = pos=(434.775,208.7,492.7) rot=(-0.57735,-0.57735,0.57735;2.0944rad)
  fixedPosition = false
  sourceFile = <userpath>/CloudStation/Hobbyprojekte/3D Drucker/CoreXY/Assembly/Parts/Bearings/smooth-bar-8x430.FCStd
  timeLastImport = 1458331381
  updateColors = true
FEATURE [App::DocumentObjectGroup] Gruppe161  label="Smooth Bars003"
  Group = -> [smooth_bar_8x430_01,smooth_bar_8x430_002]
FEATURE [Part::Feature] Pocket026  label="extruder-support"
  Placement = pos=(-0.216609,16.1847,149.63) rot=(0.57735,-0.57735,-0.57735;2.0944rad)
  shape: bbox 37 x 50 x 42 mm, 65 faces (baked)
FEATURE [Part::Feature] Chamfer001001001001001001108  label="M3x10-bolt-extruder-support-1"
  Placement = pos=(-15.2166,14.2847,184.63) rot=(1,0,0;1.5708rad)
  shape: bbox 5.5 x 13 x 5.5 mm, 16 faces (baked)
FEATURE [Part::Feature] Chamfer001001001001001001109  label="M3-nut-extruder-support-1"
  Placement = pos=(14.7834,21.1847,184.63) rot=(0,1,0;0.523599rad)
  shape: bbox 6.35 x 2.4 x 6.35 mm, 29 faces (baked)
FEATURE [Part::Feature] Chamfer001001001001001001110  label="M3x10-bolt-extruder-support-2"
  Placement = pos=(14.7834,14.2847,184.63) rot=(1,0,0;1.5708rad)
  shape: bbox 5.5 x 13 x 5.5 mm, 16 faces (baked)
FEATURE [Part::Feature] Chamfer001001001001001001111  label="M3-nut-extruder-support-002"
  Placement = pos=(-15.2166,21.1847,184.63) rot=(0,1,0;0.523599rad)
  shape: bbox 6.35 x 2.4 x 6.35 mm, 29 faces (baked)
FEATURE [Part::Feature] Chamfer001001001001001001112  label="M4x6-bolt-extruder-support-1"
  Placement = pos=(-0.216609,6.43474,149.63) rot=(1,0,0;3.14159rad)
  shape: bbox 7 x 7 x 10 mm, 23 faces (baked)
FEATURE [Part::Feature] Pocket027  label="extruder-body-part"
  Placement = pos=(9.78339,-11.0653,151.63) rot=(0.57735,-0.57735,-0.57735;2.0944rad)
  shape: bbox 20 x 45 x 47.5 mm, 42 faces (baked)
FEATURE [Part::Feature] Chamfer001001001001001001113  label="M4x6-bolt-extruder-support-2"
  Placement = pos=(-0.216609,-28.5653,149.63) rot=(1,0,0;3.14159rad)
  shape: bbox 7 x 7 x 10 mm, 23 faces (baked)
FEATURE [Part::Feature] Sweep013  label="Extruder-spring-final"
  Placement = pos=(-0.2,3.68474,172.13) rot=(0,0,1;0rad)
  shape: bbox 5.171 x 5.171 x 17.14 mm, 3 faces (baked)
FEATURE [Part::Feature] Revolution015  label="lever-shaft-final"
  Placement = pos=(-0.216609,-28.3153,186.13) rot=(0,0,1;0rad)
  shape: bbox 20 x 3 x 3 mm, 5 faces (baked)
FEATURE [Part::MultiFuse] Fusion022  label="Extruder-lever-623zz-bearing"
  Placement = pos=(-1.96661,-22.5653,178.13) rot=(0,0,1;1.5708rad)
FEATURE [Part::Feature] Chamfer001001001001001001115  label="extruder-lever-final"
  Placement = pos=(-2.71661,-22.5653,178.13) rot=(0.57735,-0.57735,-0.57735;2.0944rad)
  shape: bbox 15 x 42.5 x 16 mm, 23 faces (baked)
FEATURE [Part::Feature] Fusion023  label="Extruder-motor-Nema-17-40mm-with-connector"
  Placement = pos=(49.8834,-11.0653,178.13) rot=(0.57735,-0.57735,-0.57735;2.0944rad)
  shape: bbox 60.1 x 48 x 42.3 mm, 110 faces (baked)
FEATURE [App::DocumentObjectGroup] Group026  label="Extruder-support-plate"
  Group = -> [Pocket026,Chamfer001001001001001001108,Chamfer001001001001001001109,Chamfer001001001001001001110,Chamfer001001001001001001111,Chamfer001001001001001001113,Chamfer001001001001001001112]
FEATURE [Part::Feature] Cut008  label="Extruder-drive-gear"
  Placement = pos=(6.78339,-11.0653,178.13) rot=(0.707107,0,-0.707107;3.14159rad)
  shape: bbox 11 x 12.5 x 12.5 mm, 7 faces (baked)
FEATURE [Part::Feature] Pocket028  label="Extruder-drive-gear-setscrew"
  Placement = pos=(6.38339,-11.9653,178.13) rot=(0.57735,0.57735,-0.57735;4.18879rad)
  shape: bbox 2.5 x 4 x 2.5 mm, 11 faces (baked)
FEATURE [Part::Feature] Chamfer001001001001001001118  label="Extruder-M3x20-bolt-1"
  Placement = pos=(-6.81661,4.43474,162.63) rot=(0,-1,0;1.5708rad)
  shape: bbox 23 x 5.5 x 5.5 mm, 16 faces (baked)
FEATURE [Part::Feature] Chamfer001001001001001001119  label="Extruder-M3x20-bolt-002"
  Placement = pos=(-6.81661,-26.5653,162.63) rot=(0,-1,0;1.5708rad)
  shape: bbox 23 x 5.5 x 5.5 mm, 16 faces (baked)
FEATURE [App::DocumentObjectGroup] Group027  label="Extruder-body-motor"
  Group = -> [Pocket027,Fusion023,Cut008,Pocket028,Chamfer001001001001001001119,Chamfer001001001001001001118]
FEATURE [Part::Feature] Chamfer001001001001001001120  label="ISO-10642-M3x12-bolt-1"
  Placement = pos=(5.03339,-22.5653,178.13) rot=(0,1,0;1.5708rad)
  shape: bbox 12 x 6.046 x 6.046 mm, 26 faces (baked)
FEATURE [App::DocumentObjectGroup] Group028  label="Extruder-lever"
  Group = -> [Sweep013,Revolution015,Fusion022,Chamfer001001001001001001115,Chamfer001001001001001001120]
FEATURE [Part::Feature] Pocket029  label="Hotend-main-tube-final"
  Placement = pos=(-0.216609,-17.0653,138.63) rot=(0.57735,-0.57735,-0.57735;2.0944rad)
  shape: bbox 10 x 10 x 36 mm, 30 faces (baked)
FEATURE [Part::Feature] Pocket030  label="hot-end-nozzle-final"
  Placement = pos=(-0.216609,-17.0653,125.63) rot=(0.57735,-0.57735,-0.57735;2.0944rad)
  shape: bbox 8.08 x 8.08 x 13 mm, 22 faces (baked)
FEATURE [Part::Feature] Revolution016  label="hotend-short-metal-tube-final"
  Placement = pos=(-0.216609,-17.0653,138.88) rot=(0.57735,-0.57735,-0.57735;2.0944rad)
  shape: bbox 4 x 4 x 6 mm, 8 faces (baked)
FEATURE [Part::Feature] Revolution017  label="extruder-ptfe-tube-final"
  Placement = pos=(-0.216609,-17.0653,144.88) rot=(0.57735,-0.57735,-0.57735;2.0944rad)
  shape: bbox 4 x 4 x 25.2 mm, 4 faces (baked)
FEATURE [Part::Feature] Chamfer001001001001001001121  label="hotend-heater-block-main"
  Placement = pos=(2.28339,-13.5653,138.63) rot=(0,0,-1;1.5708rad)
  shape: bbox 19 x 19 x 10 mm, 31 faces (baked)
FEATURE [Part::Compound] Compound013  label="hotend-heater-cartridge"
  Placement = pos=(29.2969,-10.0686,138.629) rot=(0,0,-1;1.5708rad)
FEATURE [Part::Compound] Compound014  label="hotend-thermistor-final"
  Placement = pos=(15.7834,-17.0653,138.63) rot=(0,0,-1;1.5708rad)
FEATURE [App::DocumentObjectGroup] Group029  label="hotend"
  Group = -> [Pocket029,Pocket030,Revolution017,Revolution016,Chamfer001001001001001001121,Compound013,Compound014]
FEATURE [Part::Feature] Chamfer001001001001001001122  label="extruder-setscrew1"
  Placement = pos=(-3.2166,-17.0653,162.63) rot=(-0.701644,-0.124066,0.701644;2.89472rad)
  shape: bbox 3 x 3 x 3 mm, 12 faces (baked)
FEATURE [Part::Feature] Chamfer001001001001001001123  label="extruder-setscrew2"
  Placement = pos=(-0.216609,-10.0653,141.63) rot=(0,0,1;3.27553rad)
  shape: bbox 3 x 3 x 3 mm, 12 faces (baked)
FEATURE [Part::Compound] Compound015  label="Extruder-Blower-50x50"
  Placement = pos=(16.7068,-38.8136,174.407) rot=(1,-0.000583,0.000583;1.5708rad)
FEATURE [Part::Feature] Chamfer001001001001001001124  label="Extruder-blower-support-final"
  Placement = pos=(16.7834,-34.8136,174.38) rot=(1,0,0;1.5708rad)
  shape: bbox 50.65 x 2 x 61.4 mm, 26 faces (baked)
FEATURE [Part::Feature] Chamfer001001001001001001125  label="M3x6-iso-10642-blower-support-1"
  Placement = pos=(-6.21661,-36.5136,169.38) rot=(1,0,0;1.5708rad)
  shape: bbox 6.046 x 6 x 6.046 mm, 25 faces (baked)
FEATURE [Part::Feature] Chamfer001001001001001001126  label="M3x6-iso-10642-blower-support-002"
  Placement = pos=(-6.21661,-36.5136,154.38) rot=(1,0,0;1.5708rad)
  shape: bbox 6.046 x 6 x 6.046 mm, 25 faces (baked)
FEATURE [Part::Feature] Part__Feature002  label="M3x18-bolt-blower-1"
  Placement = pos=(-6.51661,-51.8136,194.48) rot=(1,0,0;1.5708rad)
  shape: bbox 5.5 x 21 x 5.5 mm, 16 faces (baked)
FEATURE [Part::Feature] Part__Feature003  label="M3x18-bolt-blower-002"
  Placement = pos=(36.1281,-51.8136,156.13) rot=(1,0,0;1.5708rad)
  shape: bbox 5.5 x 21 x 5.5 mm, 16 faces (baked)
FEATURE [Part::Feature] Pocket031  label="extruder-heat-sink-final"
  Placement = pos=(-10.2166,-11.0653,172.63) rot=(0.57735,0.57735,-0.57735;4.18879rad)
  shape: bbox 11 x 40 x 40 mm, 661 faces (baked)
FEATURE [Part::Feature] Part__Feature004  label="fan-40x40mm-final"
  Placement = pos=(-21.25,-11.0705,172.625) rot=(0,-1,0;1.5708rad)
  shape: bbox 10 x 40 x 40 mm, 172 faces (baked)
FEATURE [Part::Feature] Part__Feature005  label="M3x22-bolt-screw-extruder-fan"
  Placement = pos=(-27.91,4.92426,156.63) rot=(0,-1,0;1.5708rad)
  shape: bbox 25 x 5.5 x 5.5 mm, 16 faces (baked)
FEATURE [Part::Feature] Part__Feature006  label="M3x22-bolt-screw-extruder-fan001"
  Placement = pos=(-28.01,-27.0653,156.63) rot=(0,-1,0;1.5708rad)
  shape: bbox 25 x 5.5 x 5.5 mm, 16 faces (baked)
FEATURE [Part::Feature] Pad002001002001001001001001001023  label="air-nozzle"
  Placement = pos=(-1.56392,-37.2136,149.286) rot=(0.57735,0.57735,0.57735;2.0944rad)
  shape: bbox 19 x 25 x 26 mm, 37 faces (baked)
FEATURE [Part::Feature] Pocket032  label="hotend-safety-final"
  Placement = pos=(-1.21661,-15.4636,142.88) rot=(0,0,-1;1.5708rad)
  shape: bbox 50 x 59.55 x 19.3 mm, 68 faces (baked)
FEATURE [Part::Feature] Chamfer001001001001001001127  label="M3-nut-hotend-safety"
  Placement = pos=(-1.21661,-33.0636,142.88) rot=(0,0,1;0rad)
  shape: bbox 6.35 x 2.4 x 6.35 mm, 29 faces (baked)
FEATURE [App::DocumentObjectGroup] Group031  label="fan"
  Group = -> [Pocket031,Part__Feature004,Part__Feature005,Part__Feature006]
FEATURE [Part::Feature] Part__Feature007  label="M3x22-bolt-air-nozzle"
  Placement = pos=(-1.56392,-48.8136,143.286) rot=(1,0,0;1.5708rad)
  shape: bbox 5.5 x 25 x 5.5 mm, 16 faces (baked)
FEATURE [App::DocumentObjectGroup] Group030  label="blower"
  Group = -> [Chamfer001001001001001001124,Chamfer001001001001001001125,Chamfer001001001001001001126,Compound015,Part__Feature002,Part__Feature003,Pad002001002001001001001001001023,Part__Feature007]
FEATURE [App::DocumentObjectGroup] Group025  label="Prusa Hephestos"
  Group = -> [Group026,Group027,Group028,Group029,Chamfer001001001001001001122,Chamfer001001001001001001123,Pocket032,Chamfer001001001001001001127,Group030,Group031]
FEATURE [Part::Feature] Pad002001002001001001001001001022  label="Reel-holder-left-support-final"
  Placement = pos=(-50,48.9,369.5) rot=(0,1,0;1.5708rad)
  shape: bbox 35 x 67 x 188 mm, 17 faces (baked)
FEATURE [Part::Feature] Part__Mirroring004  label="Reel-holder-right-support-final"
  Placement = pos=(52.1,48.9,369.5) rot=(0,1,0;1.5708rad)
  shape: bbox 35 x 67 x 188 mm, 17 faces (baked)
FEATURE [Part::Feature] Cut007  label="Reel-holder-union-final"
  Placement = pos=(-39,90.9,499.5) rot=(0,1,0;1.5708rad)
  shape: bbox 80 x 24 x 24 mm, 4 faces (baked)
FEATURE [Part::Compound] Compound024  label="yellow-pla-reel"
  Placement = pos=(-35,90.9,484.5) rot=(0,1,0;1.5708rad)
FEATURE [Sketcher::SketchObject] Sketch016  label="pla-path-sketch"
  Placement = pos=(0,0,0) rot=(0.57735,0.57735,0.57735;2.0944rad)
  sketch-geometry (7):
    g0: Circle [constr] CenterX=90.9 CenterY=484.5 CenterZ=0 NormalX=0 NormalY=0 NormalZ=1 Radius=85
    g1: LineSegment StartX=-17.07 StartY=138.13 StartZ=0 EndX=-17.07 EndY=199.13 EndZ=0
    g2: LineSegment StartX=6.16877 StartY=491.254 StartZ=0 EndX=-17.0226 EndY=200.322 EndZ=0
    g3: ArcOfCircle CenterX=-2.07 CenterY=199.13 CenterZ=0 NormalX=0 NormalY=0 NormalZ=1 Radius=15 StartAngle=3.06205 EndAngle=3.14159
    g4: LineSegment [constr] StartX=-17.07 StartY=199.13 StartZ=0 EndX=-2.07 EndY=199.13 EndZ=0
    g5: ArcOfCircle CenterX=90.9 CenterY=484.5 CenterZ=0 NormalX=0 NormalY=0 NormalZ=1 Radius=85 StartAngle=1.5708 EndAngle=3.06205
    g6: LineSegment [constr] StartX=90.9 StartY=569.5 StartZ=0 EndX=90.9 EndY=484.5 EndZ=0
  constraints (21):
    c: DistanceX(g-1,g0) = 90.9
    c: DistanceY(g-1,g0) = 484.5
    c: Radius(g0) = 85
    c: Vertical(g1)
    c: DistanceY(g-1,g1) = 138.13
    c: DistanceX(g-1,g1) = -17.07
    c: DistanceY(g1) = 61
    c: Radius(g3) = 15
    c: Coincident(g3,g1)
    c: Coincident(g4,g1)
    c: Coincident(g3,g4)
    c: Horizontal(g4)
    c: Coincident(g2,g3)
    c: Tangent(g3,g2)
    c: Tangent(g2,g0)
    c: PointOnObject(g2,g0)
    c: Coincident(g5,g0)
    c: Coincident(g5,g2)
    c: Coincident(g6,g5)
    c: Coincident(g6,g0)
    c: Vertical(g6)
FEATURE [Sketcher::SketchObject] Sketch017  label="pla-section-sketch"
  Placement = pos=(0,90.9,569.5) rot=(1,0,0;1.5708rad)
  sketch-geometry (1):
    g0: Circle CenterX=0 CenterY=0 CenterZ=0 NormalX=0 NormalY=0 NormalZ=1 Radius=0.9
  constraints (1):
    c: Radius(g0) = 0.9
FEATURE [Part::Sweep] Sweep014  label="pla-into-extruder"
  Frenet = true
  Sections = -> [Sketch017]
  Solid = true
  Spine = -> Sketch016
  Transition = 1
FEATURE [App::DocumentObjectGroup] Group024  label="Plastic-reel"
  Group = -> [Pad002001002001001001001001001022,Part__Mirroring004,Cut007,Compound024,Sketch016,Sweep014]
FEATURE [Part::Feature] Fillet  label="lcd-hinge-final"
  Placement = pos=(-158.9,48.4,360) rot=(0,0.707107,0.707107;3.14159rad)
  shape: bbox 49 x 10 x 28.6 mm, 64 faces (baked)
FEATURE [Part::Feature] Chamfer001001001001001001096  label="M3-nut-lcd-hinge-1"
  Placement = pos=(-178.9,53.4,360) rot=(0,0,1;0rad)
  shape: bbox 6.35 x 2.4 x 6.35 mm, 29 faces (baked)
FEATURE [Part::Feature] Chamfer001001001001001001097  label="M3-nut-lcd-hinge-2"
  Placement = pos=(-158.9,53.4,360) rot=(0,0,1;0rad)
  shape: bbox 6.35 x 2.4 x 6.35 mm, 29 faces (baked)
FEATURE [Part::Feature] Fillet001  label="lcd-holder"
  Placement = pos=(-158.9,73.9801,400.646) rot=(0,-0.5,0.866025;3.14159rad)
  shape: bbox 156 x 40.33 x 61.19 mm, 141 faces (baked)
FEATURE [Part::Feature] Chamfer001001001001001001098  label="M3-nut-lcd-hinge-003"
  Placement = pos=(-169.5,53.4,375) rot=(-0.250563,0.250563,0.935113;1.63783rad)
  shape: bbox 2.4 x 6.35 x 6.35 mm, 29 faces (baked)
FEATURE [Part::Feature] Chamfer001001001001001001099  label="M3-nut-lcd-hinge-004"
  Placement = pos=(-145.9,53.4,375) rot=(-0.250563,0.250563,0.935113;1.63783rad)
  shape: bbox 2.4 x 6.35 x 6.35 mm, 29 faces (baked)
FEATURE [Part::Feature] Chamfer001001001001001001100  label="M3x20-hex-bolt003"
  Placement = pos=(-188.9,53.4,375) rot=(0,-1,0;1.5708rad)
  shape: bbox 23 x 5.5 x 5.5 mm, 16 faces (baked)
FEATURE [Part::Feature] Chamfer001001001001001001101  label="M3x20-hex-bolt004"
  Placement = pos=(-128.9,53.4,375) rot=(0,1,0;1.5708rad)
  shape: bbox 23 x 5.5 x 5.5 mm, 16 faces (baked)
FEATURE [Part::Compound] Compound023  label="smart-lcd-ramps"
  Placement = pos=(-158.75,65.3198,405.646) rot=(1,0,0;1.0472rad)
FEATURE [Part::Feature] Chamfer001001001001001001130  label="M3-nut-lcd-1"
  Placement = pos=(-86.6,57.4,381.928) rot=(-0.612642,0.76343,-0.20456;0.824597rad)
  shape: bbox 6.35 x 4.828 x 6.454 mm, 29 faces (baked)
FEATURE [Part::Feature] Chamfer001001001001001001131  label="M3-nut-lcd-002"
  Placement = pos=(-86.6,81.9,424.364) rot=(-0.612642,0.76343,-0.20456;0.824597rad)
  shape: bbox 6.35 x 4.828 x 6.454 mm, 29 faces (baked)
FEATURE [Part::Feature] Chamfer001001001001001001132  label="M3-nut-lcd-003"
  Placement = pos=(-230.9,81.9,424.364) rot=(-0.612642,0.76343,-0.20456;0.824597rad)
  shape: bbox 6.35 x 4.828 x 6.454 mm, 29 faces (baked)
FEATURE [Part::Feature] Chamfer001001001001001001133  label="M3-nut-lcd-004"
  Placement = pos=(-230.9,57.4,381.928) rot=(-0.612642,0.76343,-0.20456;0.824597rad)
  shape: bbox 6.35 x 4.828 x 6.454 mm, 29 faces (baked)
FEATURE [Part::Feature] Chamfer001001001001001001134  label="M3x10-bolt-lcd-1"
  Placement = pos=(-230.9,51.511,385.328) rot=(0.012505,-0.499961,0.865958;3.09828rad)
  shape: bbox 5.5 x 13.13 x 9.931 mm, 16 faces (baked)
FEATURE [Part::Feature] Chamfer001001001001001001135  label="M3x10-bolt-lcd-002"
  Placement = pos=(-230.9,76.011,427.764) rot=(0.012505,-0.499961,0.865958;3.09828rad)
  shape: bbox 5.5 x 13.13 x 9.931 mm, 16 faces (baked)
FEATURE [Part::Feature] Chamfer001001001001001001136  label="M3x10-bolt-lcd-003"
  Placement = pos=(-86.6,76.011,427.764) rot=(0.012505,-0.499961,0.865958;3.09828rad)
  shape: bbox 5.5 x 13.13 x 9.931 mm, 16 faces (baked)
FEATURE [Part::Feature] Chamfer001001001001001001137  label="M3x10-bolt-lcd-004"
  Placement = pos=(-86.6,51.511,385.328) rot=(0.012505,-0.499961,0.865958;3.09828rad)
  shape: bbox 5.5 x 13.13 x 9.931 mm, 16 faces (baked)
FEATURE [App::DocumentObjectGroup] Group023  label="lcd"
  Group = -> [Fillet,Chamfer001001001001001001096,Chamfer001001001001001001097,Fillet001,Chamfer001001001001001001098,Chamfer001001001001001001099,Chamfer001001001001001001100,Chamfer001001001001001001101,Compound023,Chamfer001001001001001001130,Chamfer001001001001001001131,Chamfer001001001001001001132,Chamfer001001001001001001133,Chamfer001001001001001001134,Chamfer001001001001001001135,+2 more]
FEATURE [Part::Feature] Fusion021  label="ramps-holder"
  Placement = pos=(-160.95,48.4,134.73) rot=(-1,0,0;1.5708rad)
  shape: bbox 75.12 x 27.99 x 105 mm, 84 faces (baked)
FEATURE [Part::Feature] Pocket025  label="fan-holder"
  Placement = pos=(-162.4,56.0125,245.024) rot=(-1,0,0;1.48353rad)
  shape: bbox 68 x 64.38 x 105.7 mm, 84 faces (baked)
FEATURE [Part::Feature] Chamfer001001001001001001102  label="M3-nut-fan-holder-1"
  Placement = pos=(-140.9,51.7514,269.489) rot=(0,1,0;0.523599rad)
  shape: bbox 6.35 x 2.4 x 6.35 mm, 29 faces (baked)
FEATURE [Part::Feature] Chamfer001001001001001001103  label="M3-nut-fan-holder-002"
  Placement = pos=(-183.9,51.7514,269.489) rot=(0,1,0;0.523599rad)
  shape: bbox 6.35 x 2.4 x 6.35 mm, 29 faces (baked)
FEATURE [Part::Feature] Chamfer001001001001001001104  label="M3-nut-fan-holder-003"
  Placement = pos=(-142.4,106.491,174.143) rot=(0,1,0;0.523599rad)
  shape: bbox 6.35 x 2.4 x 6.35 mm, 29 faces (baked)
FEATURE [Part::Feature] Chamfer001001001001001001105  label="M3-nut-fan-holder-004"
  Placement = pos=(-182.4,106.491,174.143) rot=(0,1,0;0.523599rad)
  shape: bbox 6.35 x 2.4 x 6.35 mm, 29 faces (baked)
FEATURE [Part::Feature] Chamfer001001001001001001106  label="M3x12-bolt-fan-holder-1"
  Placement = pos=(-183.9,42.4,269.5) rot=(1,0,0;1.5708rad)
  shape: bbox 5.5 x 15 x 5.5 mm, 16 faces (baked)
FEATURE [Part::Feature] Chamfer001001001001001001107  label="M3x12-bolt-fan-holder-002"
  Placement = pos=(-140.9,42.4,269.5) rot=(1,0,0;1.5708rad)
  shape: bbox 5.5 x 15 x 5.5 mm, 16 faces (baked)
FEATURE [Part::Compound] Compound016  label="Arduino-mega"
  Placement = pos=(-161.02,51.4,135.72) rot=(-0.57735,-0.57735,-0.57735;2.0944rad)
FEATURE [Part::Compound] Compound017  label="ramps-1.4"
  Placement = pos=(-164.95,66.3,136.12) rot=(-0.57735,-0.57735,-0.57735;2.0944rad)
FEATURE [Part::Compound] Compound018  label="pololu-A500"
  Placement = pos=(-153.3,77.2,124.5) rot=(-0.57735,-0.57735,-0.57735;2.0944rad)
FEATURE [Part::Compound] Compound019  label="pololu-A501"
  Placement = pos=(-176.3,77.2,124.5) rot=(-0.57735,-0.57735,-0.57735;2.0944rad)
FEATURE [Part::Compound] Compound020  label="pololu-A502"
  Placement = pos=(-176.3,77.2,145.5) rot=(-0.57735,-0.57735,-0.57735;2.0944rad)
FEATURE [Part::Compound] Compound021  label="pololu-A503"
  Placement = pos=(-176.3,77.2,166.5) rot=(-0.57735,-0.57735,-0.57735;2.0944rad)
FEATURE [Part::Compound] Compound022  label="fan-50x50mm"
  Placement = pos=(-162.6,111.88,154.204) rot=(-1,0,0;1.5708rad)
FEATURE [Part::Feature] Chamfer001001001001001001128  label="M3x16-bolt-fan-holder-3"
  Placement = pos=(-182.8,118.88,174.404) rot=(-1,0,0;1.5708rad)
  shape: bbox 5.5 x 19 x 5.5 mm, 16 faces (baked)
FEATURE [Part::Feature] Chamfer001001001001001001129  label="M3x16-bolt-fan-holder-004"
  Placement = pos=(-142.4,118.88,174.404) rot=(-1,0,0;1.5708rad)
  shape: bbox 5.5 x 19 x 5.5 mm, 16 faces (baked)
FEATURE [App::DocumentObjectGroup] Group022  label="Ramps"
  Group = -> [Fusion021,Chamfer001001001001001001107,Chamfer001001001001001001106,Chamfer001001001001001001105,Chamfer001001001001001001104,Chamfer001001001001001001103,Chamfer001001001001001001102,Pocket025,Compound016,Compound017,Compound018,Compound019,Compound020,Compound021,Chamfer001001001001001001128,Chamfer001001001001001001129,Compound022]
FEATURE [Part::Feature] Pocket020  label="x-end-idler-final"
  Placement = pos=(191.9,36.6,204) rot=(0,1,0;3.14159rad)
  shape: bbox 45 x 34.5 x 58 mm, 59 faces (baked)
FEATURE [Part::Feature] Revolution008  label="z-LM8uu-right-1"
  Placement = pos=(176.9,13.1,192) rot=(1,0,0;1.5708rad)
  shape: bbox 15 x 15 x 24 mm, 20 faces (baked)
FEATURE [Part::Feature] Revolution009  label="z-LM8uu-right-002"
  Placement = pos=(176.9,13.1,158) rot=(1,0,0;1.5708rad)
  shape: bbox 15 x 15 x 24 mm, 20 faces (baked)
FEATURE [Part::Feature] Chamfer001001001001001001077  label="x-axis-threaded-rod-M5-nut-002"
  Placement = pos=(159.9,13.1,197) rot=(1,0,0;1.5708rad)
  shape: bbox 9.238 x 9.238 x 4 mm, 23 faces (baked)
FEATURE [Part::Feature] Fusion012  label="x-axis-belt-tensioner-final"
  Placement = pos=(139.9,28.1,174) rot=(0,1,0;1.5708rad)
  shape: bbox 40 x 19 x 28 mm, 44 faces (baked)
FEATURE [Part::Feature] Chamfer001001001001001001078  label="M3-nut-y-tensor-004"
  Placement = pos=(149.9,36.1,174) rot=(0,1,0;0.518242rad)
  shape: bbox 6.35 x 2.4 x 6.35 mm, 29 faces (baked)
FEATURE [Part::Feature] Revolution010  label="belt-guide-half003"
  Placement = pos=(0,0,0) rot=(1,0,0;1.5708rad)
  shape: bbox 18 x 18 x 4.5 mm, 8 faces (baked)
FEATURE [Part::Feature] Revolution011  label="belt-guide-half004"
  Placement = pos=(0,0,9) rot=(0,0.707107,-0.707107;3.14159rad)
  shape: bbox 18 x 18 x 4.5 mm, 8 faces (baked)
FEATURE [Part::Compound] Compound011  label="Bearing-623zz001"
  Placement = pos=(0,0,6) rot=(1,0,0;1.5708rad)
FEATURE [Part::Compound] Compound010  label="x-belt-guide001"
  Links = -> [Compound011,Revolution011,Revolution010]
  Placement = pos=(149.9,23.6,174) rot=(0.57735,-0.57735,-0.57735;4.18879rad)
FEATURE [Part::Feature] Chamfer001001001001001001079  label="M3x20-hex-bolt001"
  Placement = pos=(149.9,20.2,174) rot=(1,0,0;1.5708rad)
  shape: bbox 5.5 x 23 x 5.5 mm, 16 faces (baked)
FEATURE [Part::Feature] Chamfer001001001001001001080  label="M6x40-hex-bolt"
  Placement = pos=(171.9,28.1,174) rot=(0,-1,0;1.5708rad)
  shape: bbox 46 x 10 x 10 mm, 21 faces (baked)
FEATURE [Part::Feature] Chamfer001001001001001001081  label="M6-nut-1"
  Placement = pos=(192.9,28.1,174) rot=(0.654468,0.654468,-0.378608;2.41773rad)
  shape: bbox 5.2 x 11.55 x 11.55 mm, 30 faces (baked)
FEATURE [Part::Feature] Chamfer001001001001001001082  label="M6-nut-2"
  Placement = pos=(200.9,28.1,174) rot=(0.654468,0.654468,-0.378608;2.41773rad)
  shape: bbox 5.2 x 11.55 x 11.55 mm, 30 faces (baked)
FEATURE [Part::Feature] Chamfer001001001001001001083  label="M6-nut-3"
  Placement = pos=(206.1,28.1,174) rot=(0.578002,0.578002,-0.576044;2.09636rad)
  shape: bbox 5.2 x 11.55 x 11.55 mm, 30 faces (baked)
FEATURE [App::DocumentObjectGroup] Group018  label="x-axis-idler-end"
  Group = -> [Pocket020,Revolution008,Revolution009,Chamfer001001001001001001077,Fusion012,Chamfer001001001001001001078,Compound010,Chamfer001001001001001001079,Chamfer001001001001001001080,Chamfer001001001001001001081,Chamfer001001001001001001082,Chamfer001001001001001001083]
FEATURE [Part::Feature] Cut006  label="x-carriage-final"
  Placement = pos=(-0.216609,28.1,198) rot=(0.57735,0.57735,-0.57735;4.18879rad)
  shape: bbox 60.89 x 24.79 x 82.58 mm, 108 faces (baked)
FEATURE [Part::Feature] Revolution012  label="x-LM8uu-top-1"
  Placement = pos=(14.7834,28.115,197.987) rot=(0,0,1;1.5708rad)
  shape: bbox 24 x 15 x 15 mm, 20 faces (baked)
FEATURE [Part::Feature] Revolution013  label="x-LM8uu-top-002"
  Placement = pos=(-15.2166,28.115,197.987) rot=(0,0,1;1.5708rad)
  shape: bbox 24 x 15 x 15 mm, 20 faces (baked)
FEATURE [Part::Feature] Revolution014  label="x-LM8uu-bottom-003"
  Placement = pos=(-0.0166088,28.087,152.987) rot=(0,0,1;1.5708rad)
  shape: bbox 24 x 15 x 15 mm, 20 faces (baked)
FEATURE [Part::Feature] Pocket023  label="zip-tie-head-003"
  Placement = pos=(-0.216609,26.4347,186.55) rot=(0,0,1;0rad)
  shape: bbox 4.7 x 4.5 x 3.9 mm, 14 faces (baked)
FEATURE [Sketcher::SketchObject] Sketch012  label="zip-tie-x-carriage-path-sketch"
  Placement = pos=(-0.3,0,0) rot=(0.57735,0.57735,0.57735;2.0944rad)
  sketch-geometry (13):
    g0: ArcOfCircle CenterX=28.09 CenterY=199 CenterZ=0 NormalX=0 NormalY=0 NormalZ=1 Radius=9.5 StartAngle=1.98412 EndAngle=4.29906
    g1: LineSegment [constr] StartX=24.2742 StartY=207.7 StartZ=0 EndX=24.2742 EndY=190.3 EndZ=0
    g2: LineSegment StartX=25.3397 StartY=207.691 StartZ=0 EndX=30.1789 EndY=206.307 EndZ=0
    g3: Circle [constr] CenterX=28.09 CenterY=199 CenterZ=0 NormalX=0 NormalY=0 NormalZ=1 Radius=7.6
    g4: LineSegment [constr] StartX=30.1789 StartY=206.307 StartZ=0 EndX=28.09 EndY=199 EndZ=0
    g5: ArcOfCircle CenterX=28.09 CenterY=199 CenterZ=0 NormalX=0 NormalY=0 NormalZ=1 Radius=7.6 StartAngle=4.71239 EndAngle=7.57555
    g6: LineSegment [constr] StartX=28.09 StartY=199 StartZ=0 EndX=28.09 EndY=191.4 EndZ=0
    g7: LineSegment [constr] StartX=24.2742 StartY=207.7 StartZ=0 EndX=24.79 EndY=205.768 EndZ=0
    g8: ArcOfCircle CenterX=24.79 CenterY=205.768 CenterZ=0 NormalX=0 NormalY=0 NormalZ=1 Radius=2 StartAngle=1.29236 EndAngle=1.83162
    g9: ArcOfCircle CenterX=28.09 CenterY=190.1 CenterZ=0 NormalX=0 NormalY=0 NormalZ=1 Radius=1.3 StartAngle=1.5708 EndAngle=3.14159
    g10: LineSegment [constr] StartX=26.79 StartY=190.1 StartZ=0 EndX=28.09 EndY=190.1 EndZ=0
    g11: LineSegment StartX=26.79 StartY=190.1 StartZ=0 EndX=26.79 EndY=185.6 EndZ=0
    g12: LineSegment StartX=24.2742 StartY=190.3 StartZ=0 EndX=25.7742 EndY=190.3 EndZ=0
  constraints (37):
    c: DistanceY(g-1,g0) = 199
    c: DistanceX(g-1,g0) = 28.09
    c: Radius(g0) = 9.5
    c: Vertical(g1)
    c: Coincident(g1,g0)
    c: Coincident(g1,g0)
    c: Coincident(g3,g0)
    c: Coincident(g4,g2)
    c: Coincident(g4,g0)
    c: Perpendicular(g2,g4)
    c: Tangent(g2,g3)
    c: Radius(g3) = 7.6
    c: Coincident(g5,g0)
    c: Coincident(g5,g2)
    c: Vertical(g6)
    c: Coincident(g6,g0)
    c: Coincident(g6,g5)
    c: Coincident(g7,g0)
    c: Coincident(g8,g7)
    c: Coincident(g2,g8)
    c: Coincident(g8,g0)
    c: Tangent(g8,g2)
    c: Horizontal(g10)
    c: Coincident(g10,g9)
    c: Coincident(g10,g9)
    c: PointOnObject(g9,g6)
    c: Coincident(g9,g5)
    c: Vertical(g11)
    c: Tangent(g11,g8)
    c: Coincident(g11,g9)
    c: DistanceY(g11) = -4.5
    c: Radius(g9) = 1.3
    c: DistanceY(g-1,g0) = 190.3
    c: Radius(g8) = 2
    c: Horizontal(g12)
    c: Coincident(g12,g0)
    c: DistanceX(g12) = 1.5
FEATURE [Sketcher::SketchObject] Sketch013  label="zip-tie-section-x-carriage-sketch"
  Placement = pos=(-0.3,26.79,185.6) rot=(0,0,1;0rad)
  sketch-geometry (4):
    g0: LineSegment StartX=-1.25 StartY=1 StartZ=0 EndX=1.25 EndY=1 EndZ=0
    g1: LineSegment StartX=1.25 StartY=1 StartZ=0 EndX=1.25 EndY=0 EndZ=0
    g2: LineSegment StartX=1.25 StartY=0 StartZ=0 EndX=-1.25 EndY=0 EndZ=0
    g3: LineSegment StartX=-1.25 StartY=0 StartZ=0 EndX=-1.25 EndY=1 EndZ=0
  constraints (12):
    c: Coincident(g0,g1)
    c: Coincident(g1,g2)
    c: Coincident(g2,g3)
    c: Coincident(g3,g0)
    c: Horizontal(g0)
    c: Horizontal(g2)
    c: Vertical(g1)
    c: Vertical(g3)
    c: DistanceY(g1) = -1
    c: DistanceX(g0) = 2.5
    c: Symmetric(g2,g1,g-2)
    c: PointOnObject(g2,g-1)
FEATURE [Part::Sweep] Sweep011
  Frenet = true
  Sections = -> [Sketch013]
  Solid = true
  Spine = -> Sketch012
  Transition = 1
FEATURE [Part::MultiFuse] Fusion016  label="x-carriage-zip-tie"
  Placement = pos=(0,0,-46) rot=(0,0,1;0rad)
  Shapes = -> [Sweep011,Pocket023]
FEATURE [Part::Feature] Pocket024  label="x-carriage-B-final"
  Placement = pos=(-32.2166,16.1847,169.797) rot=(0,0,1;0rad)
  shape: bbox 9.5 x 17 x 9.4 mm, 21 faces (baked)
FEATURE [Part::Feature] Chamfer001001001001001001090  label="M3-nut"
  Placement = pos=(-14.2166,22.1,174.5) rot=(0.57735,0.57735,-0.57735;2.0944rad)
  shape: bbox 2.4 x 6.35 x 6.35 mm, 29 faces (baked)
FEATURE [Part::Feature] Chamfer001001001001001001091  label="M3x20-hex-bolt002"
  Placement = pos=(-29.1166,22.1847,174.497) rot=(0.57735,0.57735,-0.57735;4.18879rad)
  shape: bbox 23 x 5.5 x 5.5 mm, 16 faces (baked)
FEATURE [App::DocumentObjectGroup] Group019  label="x-carriage"
  Group = -> [Cut006,Revolution012,Revolution013,Revolution014,Fusion016,Pocket024,Chamfer001001001001001001090,Chamfer001001001001001001091]
FEATURE [Part::Feature] Fusion017  label="x-belt-zip-tie-1"
  Placement = pos=(-60.1639,27.7353,144.802) rot=(0,0,1;1.5708rad)
  shape: bbox 4.7 x 13.61 x 6.61 mm, 35 faces (baked)
FEATURE [Part::Feature] Pocket018  label="y-endstop-holder-final"
  Placement = pos=(-61.9,42.4,38.0788) rot=(0,0.707107,-0.707107;3.14159rad)
  shape: bbox 29 x 16 x 37.08 mm, 21 faces (baked)
FEATURE [Part::Compound] Compound006  label="endstop-final"
  Placement = pos=(-34.8,42.6,39.6788) rot=(0,0.707107,-0.707107;3.14159rad)
FEATURE [Part::Feature] Chamfer001001001001001001055  label="M3x10-y-endstop-1"
  Placement = pos=(-71.4,29.1,35.0788) rot=(0,1,0;3.14159rad)
  shape: bbox 5.5 x 5.5 x 13 mm, 16 faces (baked)
FEATURE [Part::Feature] Chamfer001001001001001001056  label="M3-nut-y-endstop-1"
  Placement = pos=(-52.5,29.1,39.6788) rot=(1,0,0;1.5708rad)
  shape: bbox 6.35 x 6.35 x 2.4 mm, 29 faces (baked)
FEATURE [Part::Feature] Chamfer001001001001001001057  label="M3-nut-y-endstop-2"
  Placement = pos=(-71.4,29.1,39.6788) rot=(1,0,0;1.5708rad)
  shape: bbox 6.35 x 6.35 x 2.4 mm, 29 faces (baked)
FEATURE [Part::Feature] Chamfer001001001001001001058  label="M3x10-y-endstop-002"
  Placement = pos=(-52.4,29.1,35.0788) rot=(0,1,0;3.14159rad)
  shape: bbox 5.5 x 5.5 x 13 mm, 16 faces (baked)
FEATURE [Part::Feature] Chamfer001001001001001001059  label="M3x16-y-endstop-1"
  Placement = pos=(-48.9,38.4,6) rot=(1,0,0;1.5708rad)
  shape: bbox 5.5 x 19 x 5.5 mm, 16 faces (baked)
FEATURE [Part::Feature] Pocket019  label="y-endstop-touch-final"
  Placement = pos=(-51.455,-74.1372,47.3) rot=(0.57735,-0.57735,-0.57735;2.0944rad)
  shape: bbox 10 x 20 x 24 mm, 22 faces (baked)
FEATURE [Part::Feature] Chamfer001001001001001001060  label="M3-nut-y-endstop-003"
  Placement = pos=(-56.455,-66.6372,40.8) rot=(0,0,1;0rad)
  shape: bbox 6.35 x 2.4 x 6.35 mm, 29 faces (baked)
FEATURE [Part::Feature] Chamfer001001001001001001061  label="M3x25-hex-bolt-y-endstop"
  Placement = pos=(-56.455,-69.1372,40.8) rot=(1,0,0;1.5708rad)
  shape: bbox 5.5 x 28 x 5.5 mm, 16 faces (baked)
FEATURE [App::DocumentObjectGroup] Group010  label="y-endstop"
  Group = -> [Compound006,Pocket018,Chamfer001001001001001001055,Chamfer001001001001001001056,Chamfer001001001001001001057,Chamfer001001001001001001058,Chamfer001001001001001001059,Pocket019,Chamfer001001001001001001060,Chamfer001001001001001001061]
FEATURE [Part::Feature] Chamfer001001001001001001031  label="M3x25-hex-bolt-y-carriage-1"
  Placement = pos=(-104.3,104.3,77.8) rot=(0,0,1;0rad)
  shape: bbox 5.5 x 5.5 x 28 mm, 16 faces (baked)
FEATURE [Part::Feature] Chamfer001001001001001001032  label="M3x25-hex-bolt-y-carriage-002"
  Placement = pos=(104.3,104.3,77.8) rot=(0,0,1;0rad)
  shape: bbox 5.5 x 5.5 x 28 mm, 16 faces (baked)
FEATURE [Part::Feature] Chamfer001001001001001001033  label="M3x25-hex-bolt-y-carriage-003"
  Placement = pos=(104.3,-104.3,77.8) rot=(0,0,1;0rad)
  shape: bbox 5.5 x 5.5 x 28 mm, 16 faces (baked)
FEATURE [Part::Feature] Chamfer001001001001001001034  label="M3x25-hex-bolt-y-carriage-004"
  Placement = pos=(-104.3,-104.3,77.8) rot=(0,0,1;0rad)
  shape: bbox 5.5 x 5.5 x 28 mm, 16 faces (baked)
FEATURE [Part::Feature] Sweep007  label="spring-compressed-1"
  Placement = pos=(104.3,-104.3,57) rot=(0,0,1;0rad)
  shape: bbox 7.826 x 7.799 x 14.06 mm, 5 faces (baked)
FEATURE [Part::Feature] Sweep008  label="spring-compressed-002"
  Placement = pos=(-104.3,-104.3,57) rot=(0,0,1;0rad)
  shape: bbox 7.826 x 7.799 x 14.06 mm, 5 faces (baked)
FEATURE [Part::Feature] Sweep009  label="spring-compressed-003"
  Placement = pos=(-104.3,104.3,57) rot=(0,0,1;0rad)
  shape: bbox 7.826 x 7.799 x 14.06 mm, 5 faces (baked)
FEATURE [Part::Feature] Sweep010  label="spring-compressed-004"
  Placement = pos=(104.3,104.3,57) rot=(0,0,1;0rad)
  shape: bbox 7.826 x 7.799 x 14.06 mm, 5 faces (baked)
FEATURE [Part::Feature] Pad002001002001001001001001001017  label="bed-glass"
  Placement = pos=(0,0,78.4) rot=(0,0,1;0rad)
  shape: bbox 220 x 220 x 3 mm, 10 faces (baked)
FEATURE [Part::Feature] Pocket015  label="acrylic-base"
  Placement = pos=(0,0,70.3) rot=(0,0,1;0rad)
  shape: bbox 220 x 220 x 8 mm, 14 faces (baked)
FEATURE [Part::Feature] Fusion004  label="clip-handles001"
  shape: bbox 26 x 34.28 x 18.65 mm, 32 faces, 2 solids (baked)
FEATURE [Part::Feature] Fusion005  label="clip-body001"
  shape: bbox 31.8 x 16.95 x 15.13 mm, 64 faces (baked)
FEATURE [Part::Compound] Compound025  label="bed-clip-1"
  Links = -> [Fusion005,Fusion004]
  Placement = pos=(58,110.2,75.9) rot=(0,0,1;0rad)
FEATURE [Part::Feature] Fusion006  label="clip-handles002"
  shape: bbox 26 x 34.28 x 18.65 mm, 32 faces, 2 solids (baked)
FEATURE [Part::Feature] Fusion007  label="clip-body002"
  shape: bbox 31.8 x 16.95 x 15.13 mm, 64 faces (baked)
FEATURE [Part::Compound] Compound026  label="bed-clip-002"
  Links = -> [Fusion007,Fusion006]
  Placement = pos=(-58,110.2,75.9) rot=(0,0,1;0rad)
FEATURE [Part::Feature] Fusion008  label="clip-handles003"
  shape: bbox 26 x 34.28 x 18.65 mm, 32 faces, 2 solids (baked)
FEATURE [Part::Feature] Fusion009  label="clip-body003"
  shape: bbox 31.8 x 16.95 x 15.13 mm, 64 faces (baked)
FEATURE [Part::Compound] Compound027  label="bed-clip-003"
  Links = -> [Fusion009,Fusion008]
  Placement = pos=(-58,-110.2,75.9) rot=(0,0,1;3.14159rad)
FEATURE [Part::Feature] Fusion010  label="clip-handles004"
  shape: bbox 26 x 34.28 x 18.65 mm, 32 faces, 2 solids (baked)
FEATURE [Part::Feature] Fusion011  label="clip-body004"
  shape: bbox 31.8 x 16.95 x 15.13 mm, 64 faces (baked)
FEATURE [Part::Compound] Compound005  label="bed-clip-004"
  Links = -> [Fusion011,Fusion010]
  Placement = pos=(58,-110.2,75.9) rot=(0,0,1;3.14159rad)
FEATURE [App::DocumentObjectGroup] Group008  label="bed"
  Group = -> [Chamfer001001001001001001031,Chamfer001001001001001001032,Chamfer001001001001001001033,Chamfer001001001001001001034,Sweep007,Sweep008,Sweep009,Sweep010,Pad002001002001001001001001001017,Pocket015,Compound025,Compound026,Compound027,Compound005]
FEATURE [App::DocumentObjectGroup] Gruppe163  label="Zubehör"
  Group = -> [Group024,Group008]
FEATURE [Part::Feature] Revolution003  label="y-LM8uu001-left"
  Placement = pos=(-88.94,0,45) rot=(0,0,1;0rad)
  shape: bbox 15 x 24 x 15 mm, 20 faces (baked)
FEATURE [Part::Feature] Revolution004  label="y-LM8uu001-right-1"
  Placement = pos=(81.1,34,45) rot=(0,0,1;0rad)
  shape: bbox 15 x 24 x 15 mm, 20 faces (baked)
FEATURE [Part::Feature] Revolution005  label="y-LM8uu001-right-2"
  Placement = pos=(81.1,-34,45) rot=(0,0,1;0rad)
  shape: bbox 15 x 24 x 15 mm, 20 faces (baked)
FEATURE [Part::Feature] Chamfer001001001001001001029  label="M3x10-bolt-1-belt-holder"
  Placement = pos=(0,20.5,46.8) rot=(1,0,0;3.14159rad)
  shape: bbox 5.5 x 5.5 x 13 mm, 16 faces (baked)
FEATURE [Part::Feature] Chamfer001001001001001001030  label="M3x10-bolt-2-belt-holder"
  Placement = pos=(0,-20.5,46.8) rot=(1,0,0;3.14159rad)
  shape: bbox 5.5 x 5.5 x 13 mm, 16 faces (baked)
FEATURE [Part::Feature] Pocket012  label="zip-tie-head-002"
  Placement = pos=(-90,0,59.05) rot=(-0.57735,0.57735,0.57735;4.18879rad)
  shape: bbox 3.9 x 4.7 x 4.5 mm, 14 faces (baked)
FEATURE [Sketcher::SketchObject] Sketch009  label="zip-tie-y-carriage-path"
  Placement = pos=(-90,0,56.8) rot=(1,0,0;1.5708rad)
  sketch-geometry (10):
    g0: LineSegment StartX=0 StartY=0 StartZ=0 EndX=0 EndY=-6 EndZ=0
    g1: LineSegment StartX=16.5711 StartY=-13.0391 StartZ=0 EndX=17.76 EndY=-6 EndZ=0
    g2: LineSegment [constr] StartX=1.18894 StartY=-13.0391 StartZ=0 EndX=16.5711 EndY=-13.0391 EndZ=0
    g3: ArcOfCircle CenterX=8.88 CenterY=-11.74 CenterZ=0 NormalX=0 NormalY=0 NormalZ=1 Radius=7.8 StartAngle=3.30892 EndAngle=6.11586
    g4: LineSegment StartX=0 StartY=-6 StartZ=0 EndX=1.18894 EndY=-13.0391 EndZ=0
    g5: LineSegment [constr] StartX=0 StartY=-6 StartZ=0 EndX=17.76 EndY=-6 EndZ=0
    g6: LineSegment StartX=17.76 StartY=-6 StartZ=0 EndX=17.76 EndY=0 EndZ=0
    g7: LineSegment [constr] StartX=0 StartY=0 StartZ=0 EndX=17.76 EndY=0 EndZ=0
    g8: LineSegment StartX=17.76 StartY=0 StartZ=0 EndX=0 EndY=2.7 EndZ=0
    g9: LineSegment StartX=0 StartY=2.7 StartZ=0 EndX=-5.9 EndY=2.7 EndZ=0
  constraints (28):
    c: Coincident(g-1,g0)
    c: Vertical(g0)
    c: Horizontal(g2)
    c: DistanceY(g0) = -6
    c: Coincident(g3,g2)
    c: Coincident(g3,g2)
    c: Coincident(g4,g2)
    c: Coincident(g0,g4)
    c: Tangent(g3,g4)
    c: Coincident(g2,g1)
    c: Tangent(g3,g1)
    c: DistanceX(g3) = 8.88
    c: DistanceY(g3) = -11.74
    c: Radius(g3) = 7.8
    c: Horizontal(g5)
    c: Coincident(g5,g0)
    c: Coincident(g1,g5)
    c: Coincident(g6,g1)
    c: Vertical(g6)
    c: Horizontal(g7)
    c: Coincident(g7,g-1)
    c: Coincident(g7,g6)
    c: PointOnObject(g8,g-2)
    c: Coincident(g8,g9)
    c: Horizontal(g9)
    c: DistanceY(g-1,g8) = 2.7
    c: Coincident(g8,g6)
    c: DistanceX(g9) = -5.9
FEATURE [Sketcher::SketchObject] Sketch010  label="zip-tie-section-y-carriage-1-sketch"
  Placement = pos=(-95.9,-1e-10,60) rot=(0.57735,0.57735,0.57735;2.0944rad)
  sketch-geometry (4):
    g0: LineSegment StartX=-1.25 StartY=0.5 StartZ=0 EndX=1.25 EndY=0.5 EndZ=0
    g1: LineSegment StartX=1.25 StartY=0.5 StartZ=0 EndX=1.25 EndY=-0.5 EndZ=0
    g2: LineSegment StartX=1.25 StartY=-0.5 StartZ=0 EndX=-1.25 EndY=-0.5 EndZ=0
    g3: LineSegment StartX=-1.25 StartY=-0.5 StartZ=0 EndX=-1.25 EndY=0.5 EndZ=0
  constraints (11):
    c: Coincident(g0,g1)
    c: Coincident(g1,g2)
    c: Coincident(g2,g3)
    c: Coincident(g3,g0)
    c: Horizontal(g0)
    c: Horizontal(g2)
    c: Vertical(g1)
    c: Vertical(g3)
    c: Symmetric(g0,g1,g-1)
    c: DistanceY(g1) = -1
    c: DistanceX(g0) = 2.5
FEATURE [Part::Sweep] Sweep004  label="zip-tie-y-carriage"
  Frenet = false
  Sections = -> [Sketch010]
  Solid = true
  Spine = -> Sketch009
  Transition = 2
FEATURE [Part::MultiFuse] Fusion003  label="zip-tie-y-carriage-1"
  Placement = pos=(-7.84,0,0) rot=(0,0,1;0rad)
  Shapes = -> [Sweep004,Pocket012]
FEATURE [Part::FeaturePython] Clone004  label="zip-tie-y-carriage-2"  # Draft clone (typed FeaturePython)
  Objects = -> [Fusion003]
  Placement = pos=(0,33.8,0) rot=(0,0,1;3.14159rad)
  Scale = (1,1,1)
FEATURE [Part::FeaturePython] Clone005  label="zip-tie-y-carriage-3"  # Draft clone (typed FeaturePython)
  Objects = -> [Clone004]
  Placement = pos=(0,-33.8,0) rot=(0,0,1;3.14159rad)
  Scale = (1,1,1)
FEATURE [Part::Feature] Pocket017  label="y-aluminium-carriage2"
  Placement = pos=(0,0,50.8) rot=(0,0,1;1.5708rad)
  shape: bbox 220 x 220 x 6 mm, 98 faces (baked)
FEATURE [App::DocumentObjectGroup] Group007  label="y-carriage"
  Group = -> [Revolution003,Revolution004,Revolution005,Chamfer001001001001001001029,Chamfer001001001001001001030,Fusion003,Clone004,Clone005,Pocket017]
FEATURE [Part::Feature] Pocket011  label="zip-tie-head-1"
  Placement = pos=(-90.1,-161,41.25) rot=(0.57735,0.57735,-0.57735;4.18879rad)
  shape: bbox 3.9 x 4.7 x 4.5 mm, 14 faces (baked)
FEATURE [Sketcher::SketchObject] Sketch007  label="zip-tie-y-corner-path-sketch"
  Placement = pos=(-90.1,-161,43.5) rot=(1,0,0;1.5708rad)
  sketch-geometry (11):
    g0: LineSegment StartX=0 StartY=0 StartZ=0 EndX=0 EndY=1.5 EndZ=0
    g1: LineSegment StartX=18 StartY=-2.5 StartZ=0 EndX=-6 EndY=-2.5 EndZ=0
    g2: LineSegment StartX=0.168082 StartY=1.87394 StartZ=0 EndX=2 EndY=3.5 EndZ=0
    g3: ArcOfCircle CenterX=0.5 CenterY=1.5 CenterZ=0 NormalX=0 NormalY=0 NormalZ=1 Radius=0.5 StartAngle=2.29673 EndAngle=3.14159
    g4: ArcOfCircle CenterX=9 CenterY=-7.45445 CenterZ=0 NormalX=0 NormalY=0 NormalZ=1 Radius=13 StartAngle=1.00219 EndAngle=2.13941
    g5: LineSegment [constr] StartX=2 StartY=3.5 StartZ=0 EndX=16 EndY=3.5 EndZ=0
    g6: LineSegment StartX=16 StartY=3.5 StartZ=0 EndX=18 EndY=1.5 EndZ=0
    g7: ArcOfCircle CenterX=18 CenterY=-2 CenterZ=0 NormalX=0 NormalY=0 NormalZ=1 Radius=0.5 StartAngle=4.71239 EndAngle=6.28319
    g8: LineSegment [constr] StartX=18 StartY=-2 StartZ=0 EndX=18 EndY=-2.5 EndZ=0
    g9: LineSegment [constr] StartX=18 StartY=-2 StartZ=0 EndX=18.5 EndY=-2 EndZ=0
    g10: ArcOfCircle CenterX=6 CenterY=-2 CenterZ=0 NormalX=0 NormalY=0 NormalZ=1 Radius=12.5 StartAngle=6.991e-09 EndAngle=0.283794
  constraints (34):
    c: Vertical(g0)
    c: Horizontal(g1)
    c: Coincident(g0,g-1)
    c: DistanceY(g0) = 1.5
    c: Coincident(g0,g3)
    c: Coincident(g2,g3)
    c: Tangent(g3,g0)
    c: DistanceY(g-1,g2) = 3.5
    c: DistanceX(g0,g2) = 2
    c: Tangent(g3,g2)
    c: Radius(g3) = 0.5
    c: Coincident(g4,g2)
    c: Horizontal(g5)
    c: Coincident(g5,g2)
    c: Coincident(g4,g5)
    c: DistanceX(g5) = 14
    c: Radius(g4) = 13
    c: Coincident(g6,g4)
    c: DistanceX(g-1,g6) = 18
    c: DistanceY(g-1,g6) = 1.5
    c: DistanceY(g-1,g1) = -2.5
    c: DistanceX(g-1,g1) = 18
    c: Vertical(g8)
    c: Radius(g7) = 0.5
    c: Coincident(g8,g7)
    c: Coincident(g8,g7)
    c: Horizontal(g9)
    c: Coincident(g9,g7)
    c: Coincident(g9,g7)
    c: Coincident(g7,g1)
    c: Coincident(g10,g7)
    c: Coincident(g10,g6)
    c: Tangent(g10,g7)
    c: DistanceX(g-1,g1) = -6
FEATURE [Sketcher::SketchObject] Sketch008  label="zip-tie-section001"
  Placement = pos=(-96.1,-161,40.5) rot=(0.57735,0.57735,0.57735;2.0944rad)
  sketch-geometry (4):
    g0: LineSegment StartX=-1.25 StartY=0.5 StartZ=0 EndX=1.25 EndY=0.5 EndZ=0
    g1: LineSegment StartX=1.25 StartY=0.5 StartZ=0 EndX=1.25 EndY=-0.5 EndZ=0
    g2: LineSegment StartX=1.25 StartY=-0.5 StartZ=0 EndX=-1.25 EndY=-0.5 EndZ=0
    g3: LineSegment StartX=-1.25 StartY=-0.5 StartZ=0 EndX=-1.25 EndY=0.5 EndZ=0
  constraints (11):
    c: Coincident(g0,g1)
    c: Coincident(g1,g2)
    c: Coincident(g2,g3)
    c: Coincident(g3,g0)
    c: Horizontal(g0)
    c: Horizontal(g2)
    c: Vertical(g1)
    c: Vertical(g3)
    c: Symmetric(g0,g1,g-1)
    c: DistanceY(g1) = -1
    c: DistanceX(g0) = 2.5
FEATURE [Part::Sweep] Sweep003
  Frenet = false
  Sections = -> [Sketch008]
  Solid = true
  Spine = -> Sketch007
  Transition = 2
FEATURE [Part::MultiFuse] Fusion002  label="zip-tie-y-corner-1"
  Placement = pos=(-7.84,0,0) rot=(0,0,1;0rad)
  Shapes = -> [Pocket011,Sweep003]
FEATURE [Part::Cylinder] Cylinder010  label="z-M5x300mm-threaded-rod-left"
  Angle = 360
  Height = 300
  Placement = pos=(-167.9,13.1,74) rot=(0,0,1;0rad)
  Radius = 2.5
FEATURE [Part::Feature] Chamfer001001001001001001062  label="setscrew-top-2"
  Placement = pos=(-2.05702,-0.399844,20.85) rot=(-0.503588,-0.610901,0.610901;2.20857rad)
  shape: bbox 6.792 x 4.973 x 3.9 mm, 12 faces (baked)
FEATURE [Part::Feature] Chamfer001001001001001001063  label="setscrew-top-1"
  Placement = pos=(-0.399844,2.05702,20.85) rot=(-0.990855,-0.095409,0.095409;1.57998rad)
  shape: bbox 4.973 x 6.792 x 3.9 mm, 12 faces (baked)
FEATURE [Part::Feature] Chamfer001001001001001001064  label="setscrew-bottom-002"
  Placement = pos=(-2.09552,0,3.95) rot=(-0.57735,-0.57735,0.57735;2.0944rad)
  shape: bbox 6.2 x 3.9 x 3.9 mm, 12 faces (baked)
FEATURE [Part::Feature] Chamfer001001001001001001065  label="setscrew-bottom-1"
  Placement = pos=(0,2.09552,3.95) rot=(-1,0,0;1.5708rad)
  shape: bbox 3.9 x 6.2 x 3.9 mm, 12 faces (baked)
FEATURE [Part::Feature] Chamfer001001001001001001066  label="coupling-final"
  shape: bbox 28.44 x 28.71 x 24.7 mm, 28 faces (baked)
FEATURE [Part::Compound] Compound007  label="z-coupling-left"
  Links = -> [Chamfer001001001001001001066,Chamfer001001001001001001065,Chamfer001001001001001001064,Chamfer001001001001001001063,Chamfer001001001001001001062]
  Placement = pos=(-167.9,13.1,53) rot=(0,0,1;1.5708rad)
FEATURE [Part::Compound] Compound009  label="endstop-final001"
  Placement = pos=(-196.3,40.3,79.5333) rot=(0,0,-1;1.5708rad)
FEATURE [Part::Feature] Chamfer001001001001001001072  label="M3x10-z-endstop-1"
  Placement = pos=(-189.7,3.7,93.0333) rot=(0,1,0;1.5708rad)
  shape: bbox 13 x 5.5 x 5.5 mm, 16 faces (baked)
FEATURE [Part::Feature] Chamfer001001001001001001073  label="M3x10-z-endstop-2"
  Placement = pos=(-189.7,22.7,93.0333) rot=(0,1,0;1.5708rad)
  shape: bbox 13 x 5.5 x 5.5 mm, 16 faces (baked)
FEATURE [Part::Feature] Part__Feature  label="z-axis-endstop-final"
  Placement = pos=(-194.7,13.2,96.0333) rot=(-0.57735,0.57735,-0.57735;2.0944rad)
  shape: bbox 16.65 x 26 x 41.03 mm, 23 faces (baked)
FEATURE [Part::Feature] Chamfer001001001001001001074  label="M3-nut-z-endstop-1"
  Placement = pos=(-196.3,3.7,93.0333) rot=(0,0,1;1.5708rad)
  shape: bbox 2.4 x 6.35 x 6.35 mm, 29 faces (baked)
FEATURE [Part::Feature] Chamfer001001001001001001075  label="M3-nut-z-endstop-2"
  Placement = pos=(-196.3,22.6,93.0333) rot=(0,0,1;1.5708rad)
  shape: bbox 2.4 x 6.35 x 6.35 mm, 29 faces (baked)
FEATURE [App::DocumentObjectGroup] Group014  label="z-axis-endstop"
  Group = -> [Compound009,Chamfer001001001001001001072,Chamfer001001001001001001073,Part__Feature,Chamfer001001001001001001074,Chamfer001001001001001001075]
FEATURE [App::DocumentObjectGroup] Gruppe162  label="Elektronik"
  Group = -> [Group023,Group022,Group010,Group014]
FEATURE [PartDesign::Pocket] Pocket010  label="zip-tie-slot"
  Length = 5
  Placement = pos=(3.15,-22.2256,35.55) rot=(0.57735,0.57735,0.57735;2.0944rad)
  Type = 0
FEATURE [Sketcher::SketchObject] Sketch005  label="zip-tie-1-path"
  Placement = pos=(3.15,-22.2256,35.7897) rot=(1,0,0;1.5708rad)
  sketch-geometry (8):
    g0: LineSegment StartX=-0.543103 StartY=-3.59814 StartZ=0 EndX=-6.3 EndY=-3.1 EndZ=0
    g1: LineSegment StartX=-6.75019 StartY=-2.52022 StartZ=0 EndX=-6.3 EndY=0.2 EndZ=0
    g2: LineSegment StartX=0 StartY=0.2 StartZ=0 EndX=5.85 EndY=0.2 EndZ=0
    g3: ArcOfCircle CenterX=-0.5 CenterY=-3.1 CenterZ=0 NormalX=0 NormalY=0 NormalZ=1 Radius=0.5 StartAngle=4.62607 EndAngle=6.28319
    g4: ArcOfCircle CenterX=-6.2569 CenterY=-2.60186 CenterZ=0 NormalX=0 NormalY=0 NormalZ=1 Radius=0.5 StartAngle=2.97758 EndAngle=4.62607
    g5: LineSegment StartX=-5.77067 StartY=0.617062 StartZ=0 EndX=0 EndY=0.2 EndZ=0
    g6: ArcOfCircle CenterX=-5.80671 CenterY=0.118362 CenterZ=0 NormalX=0 NormalY=0 NormalZ=1 Radius=0.5 StartAngle=1.49865 EndAngle=2.97758
    g7: LineSegment StartX=0 StartY=-2.5 StartZ=0 EndX=0 EndY=-3.1 EndZ=0
  constraints (23):
    c: Horizontal(g2)
    c: Tangent(g0,g3)
    c: Radius(g3) = 0.5
    c: Tangent(g0,g4)
    c: Tangent(g1,g4)
    c: Radius(g4) = 0.5
    c: DistanceX(g-1,g0) = -6.3
    c: DistanceY(g-1,g0) = -3.1
    c: Tangent(g1,g6)
    c: Tangent(g5,g6)
    c: DistanceX(g-1,g1) = -6.3
    c: DistanceY(g-1,g1) = 0.2
    c: Radius(g6) = 0.5
    c: DistanceY(g-1,g2) = 0.2
    c: DistanceX(g-1,g2) = 5.85
    c: Vertical(g7)
    c: Coincident(g3,g7)
    c: PointOnObject(g7,g-2)
    c: DistanceY(g-1,g7) = -2.5
    c: Tangent(g7,g3)
    c: DistanceY(g7) = -0.6
    c: PointOnObject(g2,g-2)
    c: Coincident(g5,g2)
FEATURE [Sketcher::SketchObject] Sketch006  label="zip-tie-section"
  Placement = pos=(9,-22.2256,36.4897) rot=(0.57735,0.57735,0.57735;2.0944rad)
  sketch-geometry (4):
    g0: LineSegment StartX=-1.25 StartY=0.5 StartZ=0 EndX=1.25 EndY=0.5 EndZ=0
    g1: LineSegment StartX=1.25 StartY=0.5 StartZ=0 EndX=1.25 EndY=-0.5 EndZ=0
    g2: LineSegment StartX=1.25 StartY=-0.5 StartZ=0 EndX=-1.25 EndY=-0.5 EndZ=0
    g3: LineSegment StartX=-1.25 StartY=-0.5 StartZ=0 EndX=-1.25 EndY=0.5 EndZ=0
  constraints (11):
    c: Coincident(g0,g1)
    c: Coincident(g1,g2)
    c: Coincident(g2,g3)
    c: Coincident(g3,g0)
    c: Horizontal(g0)
    c: Horizontal(g2)
    c: Vertical(g1)
    c: Vertical(g3)
    c: Symmetric(g0,g1,g-1)
    c: DistanceY(g1) = -1
    c: DistanceX(g0) = 2.5
FEATURE [Part::Sweep] Sweep002
  Frenet = false
  Sections = -> [Sketch006]
  Solid = true
  Spine = -> Sketch005
  Transition = 1
FEATURE [Part::MultiFuse] Fusion001  label="y-belt-zip-tie-1"
  Shapes = -> [Pocket010,Sweep002]
FEATURE [App::DocumentObjectGroup] Gruppe164  label="Gute Ideen"
  Group = -> [Group018,Sketch012,Group019,Fusion017,Group007,Sketch009,Sketch007,Fusion002,Compound007,Cylinder010,Fusion001,Sketch005]
FEATURE [Part::FeaturePython] Toronade_Carrier_XY_01001  label="Toronado_Carrier_XY_01001"  # a2plus imported part (geometry in sourceFile) (typed FeaturePython)
  Placement = pos=(247.935,196.2,506.95) rot=(-0.57735,-0.57735,0.57735;2.0944rad)
  fixedPosition = true
  sourceFile = <userpath>/CloudStation/Hobbyprojekte/3D Drucker/CoreXY/Assembly/Parts/Extruder/Toronade-Carrier-XY.FCStd
  timeLastImport = 1458396102
  updateColors = true
FEATURE [Part::FeaturePython] Knurl_Nut_01  # a2plus imported part (geometry in sourceFile) (typed FeaturePython)
  Placement = pos=(203.935,196,458.65) rot=(-1,0,0;1.5708rad)
  fixedPosition = false
  sourceFile = <userpath>/CloudStation/Hobbyprojekte/3D Drucker/CoreXY/Assembly/Parts/Screws/Knurl Nut.FCStd
  timeLastImport = 1457566460
  updateColors = true
FEATURE [Part::FeaturePython] Knurl_Nut_002  # a2plus imported part (geometry in sourceFile) (typed FeaturePython)
  Placement = pos=(234.935,196,436.75) rot=(-1,0,0;1.5708rad)
  fixedPosition = false
  sourceFile = <userpath>/CloudStation/Hobbyprojekte/3D Drucker/CoreXY/Assembly/Parts/Screws/Knurl Nut.FCStd
  timeLastImport = 1457566460
  updateColors = true
FEATURE [Part::FeaturePython] Knurl_Nut_003  # a2plus imported part (geometry in sourceFile) (typed FeaturePython)
  Placement = pos=(204.435,196,470.205) rot=(-1,0,0;1.5708rad)
  fixedPosition = false
  sourceFile = <userpath>/CloudStation/Hobbyprojekte/3D Drucker/CoreXY/Assembly/Parts/Screws/Knurl Nut.FCStd
  timeLastImport = 1457566460
  updateColors = true
FEATURE [Part::FeaturePython] Knurl_Nut_004  # a2plus imported part (geometry in sourceFile) (typed FeaturePython)
  Placement = pos=(234.435,196,470.205) rot=(-1,0,0;1.5708rad)
  fixedPosition = false
  sourceFile = <userpath>/CloudStation/Hobbyprojekte/3D Drucker/CoreXY/Assembly/Parts/Screws/Knurl Nut.FCStd
  timeLastImport = 1457566460
  updateColors = true
FEATURE [Part::FeaturePython] Knurl_Nut_005  # a2plus imported part (geometry in sourceFile) (typed FeaturePython)
  Placement = pos=(234.935,196,458.65) rot=(-1,0,0;1.5708rad)
  fixedPosition = false
  sourceFile = <userpath>/CloudStation/Hobbyprojekte/3D Drucker/CoreXY/Assembly/Parts/Screws/Knurl Nut.FCStd
  timeLastImport = 1457566460
  updateColors = true
FEATURE [Part::FeaturePython] Knurl_Nut_006  # a2plus imported part (geometry in sourceFile) (typed FeaturePython)
  Placement = pos=(228.135,196,503.45) rot=(-1,0,0;1.5708rad)
  fixedPosition = false
  sourceFile = <userpath>/CloudStation/Hobbyprojekte/3D Drucker/CoreXY/Assembly/Parts/Screws/Knurl Nut.FCStd
  timeLastImport = 1457566460
  updateColors = true
FEATURE [Part::FeaturePython] Knurl_Nut_007  # a2plus imported part (geometry in sourceFile) (typed FeaturePython)
  Placement = pos=(241.735,196,481.95) rot=(-1,0,0;1.5708rad)
  fixedPosition = false
  sourceFile = <userpath>/CloudStation/Hobbyprojekte/3D Drucker/CoreXY/Assembly/Parts/Screws/Knurl Nut.FCStd
  timeLastImport = 1457566460
  updateColors = true
FEATURE [Part::FeaturePython] Knurl_Nut_008  # a2plus imported part (geometry in sourceFile) (typed FeaturePython)
  Placement = pos=(203.935,196,436.75) rot=(-1,0,0;1.5708rad)
  fixedPosition = false
  sourceFile = <userpath>/CloudStation/Hobbyprojekte/3D Drucker/CoreXY/Assembly/Parts/Screws/Knurl Nut.FCStd
  timeLastImport = 1457566460
  updateColors = true
FEATURE [Part::Feature] Fusion_solid  label="x-zip-tie"
  Placement = pos=(427,216.7,493) rot=(0.57735,0.57735,0.57735;4.18879rad)
  shape: bbox 4.7 x 19.09 x 14.89 mm, 36 faces (baked)
FEATURE [Part::Feature] Fusion_solid001  label="x-zip-tie001"
  Placement = pos=(13,216.7,493) rot=(0.57735,0.57735,0.57735;4.18879rad)
  shape: bbox 4.7 x 19.09 x 14.89 mm, 36 faces (baked)
FEATURE [Part::Feature] Fusion_solid002  label="x-zip-tie002"
  Placement = pos=(427,200.7,447.3) rot=(0.57735,0.57735,-0.57735;2.0944rad)
  shape: bbox 4.7 x 19.09 x 14.89 mm, 36 faces (baked)
FEATURE [App::DocumentObjectGroup] Gruppe166  label="Zip-Ties"
  Group = -> [Fusion_solid,Fusion_solid002]
FEATURE [Part::Feature] Fusion_solid003  label="x-zip-tie003"
  Placement = pos=(13,200.7,447.3) rot=(0.57735,0.57735,-0.57735;2.0944rad)
  shape: bbox 4.7 x 19.09 x 14.89 mm, 36 faces (baked)
FEATURE [Part::FeaturePython] Toranado_Assembly_03  label="Toranado_Assembly_02"  # a2plus imported part (geometry in sourceFile) (typed FeaturePython)
  Placement = pos=(203.815,146.4,499.2) rot=(0.57735,0.57735,0.57735;2.0944rad)
  fixedPosition = false
  sourceFile = <userpath>/CloudStation/Hobbyprojekte/3D Drucker/CoreXY/Assembly/Parts/Extruder/Toranado_Assembly.FCStd
  timeLastImport = 1458407076
  updateColors = true
FEATURE [App::DocumentObjectGroup] Gruppe119  label="Toranado"
  Group = -> [Toranado_Assembly_01,Toranado_Assembly_03]
FEATURE [App::DocumentObjectGroup] Gruppe092  label="Extruders"
  Group = -> [Group,Gruppe088,Gruppe089,Gruppe090,Gruppe096,Gruppe091,Gruppe119,Group025]
FEATURE [Part::FeaturePython] tpge_xcar_cover1_01  # a2plus imported part (geometry in sourceFile) (typed FeaturePython)
  Placement = pos=(234.7,218.5,492.2) rot=(1,0,0;1.5708rad)
  fixedPosition = false
  sourceFile = <userpath>/CloudStation/Hobbyprojekte/3D Drucker/CoreXY/Assembly/Parts/Extruder/tpge-xcar-cover1.FCStd
  timeLastImport = 1458408322
  updateColors = true
FEATURE [App::DocumentObjectGroup] Gruppe165  label="X-Slider"
  Group = -> [Toronade_Carrier_XY_01001,Knurl_Nut_01,Knurl_Nut_002,Knurl_Nut_003,Knurl_Nut_004,Knurl_Nut_005,Knurl_Nut_006,Knurl_Nut_007,Knurl_Nut_008,tpge_xcar_cover1_01]
FEATURE [Part::FeaturePython] Washer270  label="M4-Washer590"  # Fasteners workbench fastener (typed FeaturePython)
  Placement = pos=(37.7,201.5,480) rot=(0,0,1;0rad)
  baseObject = -> Washer264 [Edge1]
  diameter = 5
  invert = false
  matchOuter = false
  offset = 0
  type = 0
FEATURE [Part::FeaturePython] Washer271  label="M4-Washer591"  # Fasteners workbench fastener (typed FeaturePython)
  Placement = pos=(37.7,201.5,480.9) rot=(0,0,1;0rad)
  baseObject = -> Washer270 [Edge1]
  diameter = 5
  invert = false
  matchOuter = false
  offset = 0
  type = 0
FEATURE [App::DocumentObjectGroup] Gruppe158  label="Screws015"
  Group = -> [Washer257,Washer258,Washer259,Washer260,Nut076,Nut077,Nut078,Nut079,ScrewTap004,ScrewTap005,Washer261,Washer262,Washer263,Washer264,Washer267,Washer268,Washer270,Washer271]
FEATURE [App::DocumentObjectGroup] Gruppe167  label="Zip Ties"
  Group = -> [Fusion_solid003,Fusion_solid001]
FEATURE [Part::FeaturePython] spacer11_5mm_01  # a2plus imported part (geometry in sourceFile) (typed FeaturePython)
  Placement = pos=(37.7,201.5,458.6) rot=(0,0,1;0rad)
  fixedPosition = false
  sourceFile = <userpath>/CloudStation/Hobbyprojekte/3D Drucker/CoreXY/Assembly/Parts/Printed Parts/spacer11_5mm.FCStd
  timeLastImport = 1458410217
  updateColors = true
FEATURE [App::DocumentObjectGroup] Gruppe159  label="Distancers011"
  Group = -> [spacer10_0mm_002,spacer11_5mm_01]
FEATURE [App::DocumentObjectGroup] Gruppe160  label="Right Slider002"
  Group = -> [LM8uu_025,LM8uu_026,Gruppe157,Gruppe158,Gruppe159,CustomBushingXYBlock_LM8UU_003,CustomBushingXYBlock_LM8UU_004,Gruppe167]
FEATURE [Part::FeaturePython] Washer272  label="M4-Washer592"  # Fasteners workbench fastener (typed FeaturePython)
  Placement = pos=(402.3,201.5,459.34) rot=(1,0,0;3.14159rad)
  baseObject = -> Washer238 [Edge1]
  diameter = 5
  invert = false
  matchOuter = false
  offset = 0
  type = 0
FEATURE [App::DocumentObjectGroup] Gruppe123  label="Screws014"
  Group = -> [Washer230,Washer231,Washer232,Washer233,Nut,Nut049,Nut050,Nut051,ScrewTap002,ScrewTap003,Washer234,Washer235,Washer236,Washer,Washer237,Washer238,Washer239,Washer272]
FEATURE [App::DocumentObjectGroup] Gruppe156  label="Left Slider002"
  Group = -> [LM8uu_023,LM8uu_024,Gruppe122,Gruppe123,Gruppe124,CustomBushingXYBlock_LM8UU_01,CustomBushingXYBlock_LM8UU_002,Gruppe166]
FEATURE [App::DocumentObjectGroup] Gruppe120  label="Vertical Carrier"
  Group = -> [Gruppe156,Gruppe160,Gruppe161,Gruppe165]
FEATURE [App::DocumentObjectGroup] Gruppe093  label="Carriers"
  Group = -> [Gruppe120,Gruppe121]
FEATURE [App::DocumentObjectGroup] Gruppe008  label="XY-Slide"
  Group = -> [Gruppe057,Gruppe093,XY_Chain_01]
